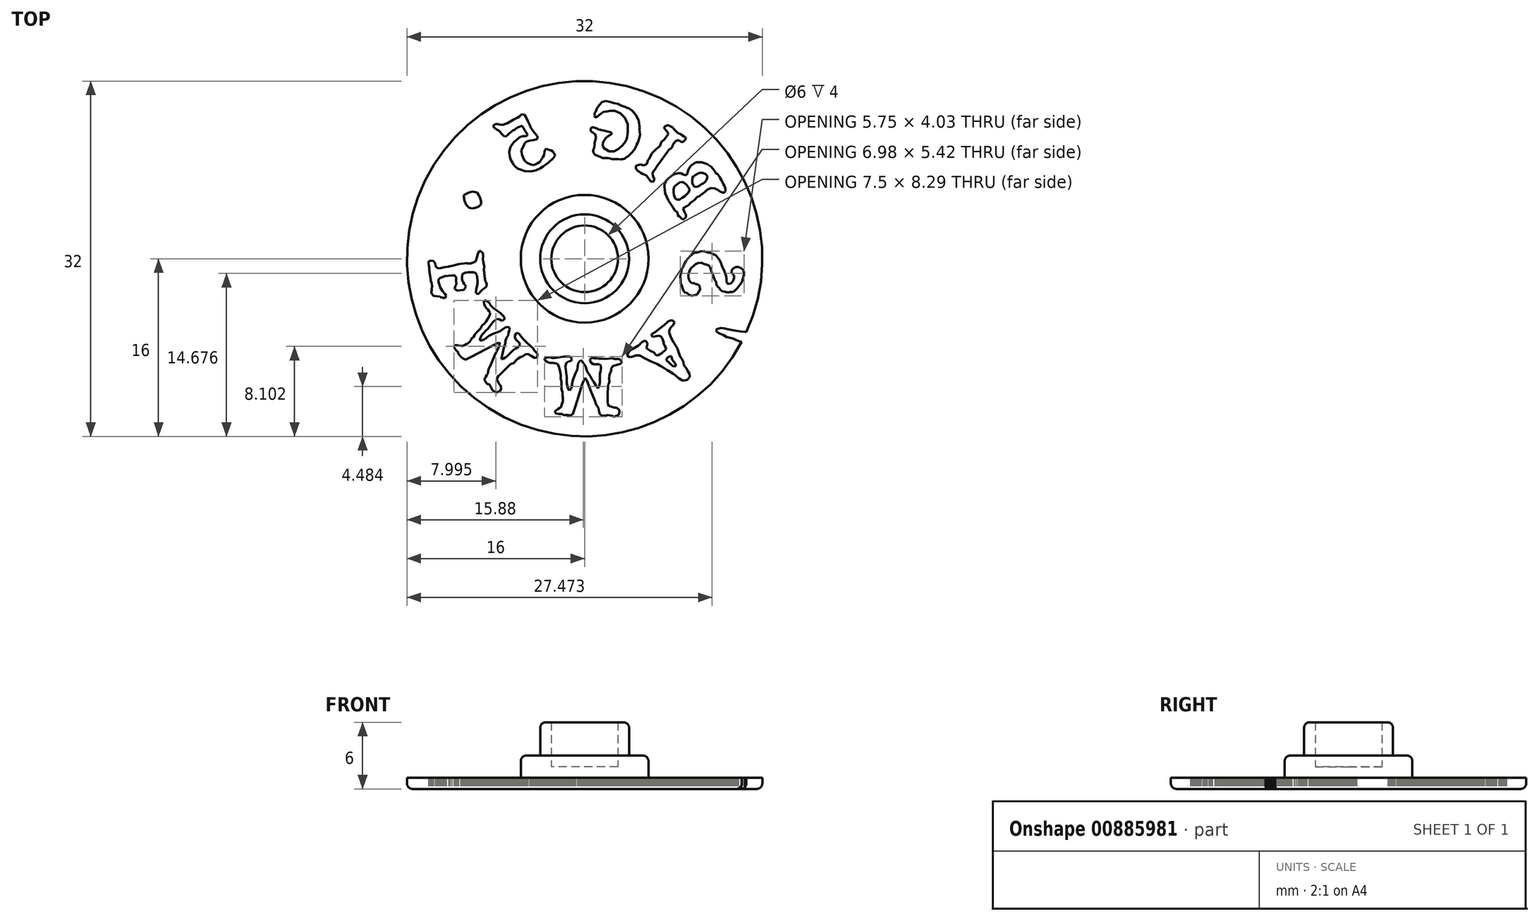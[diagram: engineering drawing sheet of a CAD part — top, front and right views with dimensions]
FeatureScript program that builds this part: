
annotation { "Feature Type Name" : "Feature", "Feature Type Description" : "" }
export const myFeature = defineFeature(function(context is Context, id is Id, definition is map)
    precondition{}
    {
        {
            var Q0;
            Q0=qCreatedBy(makeId("Top.planeOp"),FACE);
            var sketch = newSketch(context, id + "F0", { "sketchPlane" : qUnion([Q0])});
            skCircle(sketch, "E0", {"center": v(0, 0) * mm, "radius": 4 * mm});
            skCircle(sketch, "E1", {"center": v(0, 0) * mm, "radius": 5.75 * mm});
            skCircle(sketch, "E2", {"center": v(0, 0) * mm, "radius": 16 * mm});
            skCircle(sketch, "E3", {"center": v(0, 0) * mm, "radius": 3 * mm});
            skSolve(sketch);
        }
        {
            var Q0;
            Q0=makeQuery(id+"F0.imprint","IMPRINT",FACE,{"disambiguationData":[TD([[makeQuery(id+"F0.imprint","IMPRINT",EDGE,{"derivedFrom":sQuery(id+"F0.wireOp",EDGE,"E1")}),-1.0]])]});
            var Q1;
            Q1=makeQuery(id+"F0.imprint","IMPRINT",FACE,{"disambiguationData":[TD([[makeQuery(id+"F0.imprint","IMPRINT",EDGE,{"derivedFrom":sQuery(id+"F0.wireOp",EDGE,"E0")}),-1.0]])]});
            var Q2;
            Q2=makeQuery(id+"F0.imprint","IMPRINT",FACE,{"disambiguationData":[TD([[makeQuery(id+"F0.imprint","IMPRINT",EDGE,{"derivedFrom":sQuery(id+"F0.wireOp",EDGE,"E0")}),1.0]])]});
            var Q3;
            Q3=makeQuery(id+"F0.imprint","IMPRINT",FACE,{"disambiguationData":[TD([[makeQuery(id+"F0.imprint","IMPRINT",EDGE,{"derivedFrom":sQuery(id+"F0.wireOp",EDGE,"E3")}),1.0]])]});
            extrude(context, id + "F1", {"entities" : qUnion([Q0, Q1, Q2, Q3]), "depth" : 2 * mm, "offsetDistance" : 25 * mm});
        }
        {
            var Q0;
            Q0=makeQuery(id+"F0.imprint","IMPRINT",FACE,{"disambiguationData":[TD([[makeQuery(id+"F0.imprint","IMPRINT",EDGE,{"derivedFrom":sQuery(id+"F0.wireOp",EDGE,"E0")}),-1.0]])]});
            extrude(context, id + "F2", {"entities" : qUnion([Q0]), "operationType" : NewBodyOperationType.ADD, "depth" : 3 * mm, "offsetDistance" : 25 * mm});
        }
        {
            var Q0;
            Q0=makeQuery(id+"F0.imprint","IMPRINT",FACE,{"disambiguationData":[TD([[makeQuery(id+"F0.imprint","IMPRINT",EDGE,{"derivedFrom":sQuery(id+"F0.wireOp",EDGE,"E0")}),1.0]])]});
            extrude(context, id + "F3", {"entities" : qUnion([Q0]), "operationType" : NewBodyOperationType.ADD, "depth" : 6 * mm, "offsetDistance" : 25 * mm});
        }
        {
            var Q0;
            Q0=makeQuery(id+"F1.opExtrude","CAP_FACE",FACE,{"disambiguationData":[OSD([sQuery(id+"F0.wireOp",EDGE,"E2")])],"isStart":true});
            var sketch = newSketch(context, id + "F4", { "sketchPlane" : qUnion([Q0])});
            skLineSegment(sketch, "E4", {"start": v(0.68, -0.15) * mm, "end": v(0.68, -0.15) * mm});
            skLineSegment(sketch, "E5", {"start": v(0.68, -0.15) * mm, "end": v(0.68, -0.16) * mm});
            skLineSegment(sketch, "E6", {"start": v(0.68, -0.16) * mm, "end": v(0.68, -0.16) * mm});
            skLineSegment(sketch, "E7", {"start": v(0.68, -0.16) * mm, "end": v(0.67, -0.18) * mm});
            skLineSegment(sketch, "E8", {"start": v(0.67, -0.18) * mm, "end": v(0.68, -0.19) * mm});
            skLineSegment(sketch, "E9", {"start": v(0.68, -0.19) * mm, "end": v(0.68, -0.2) * mm});
            skLineSegment(sketch, "E10", {"start": v(0.68, -0.2) * mm, "end": v(0.68, -0.2) * mm});
            skLineSegment(sketch, "E11", {"start": v(0.68, -0.2) * mm, "end": v(0.67, -0.2) * mm});
            skLineSegment(sketch, "E12", {"start": v(0.67, -0.2) * mm, "end": v(0.67, -0.21) * mm});
            skLineSegment(sketch, "E13", {"start": v(0.67, -0.21) * mm, "end": v(0.66, -0.22) * mm});
            skLineSegment(sketch, "E14", {"start": v(0.66, -0.22) * mm, "end": v(0.65, -0.22) * mm});
            skLineSegment(sketch, "E15", {"start": v(0.65, -0.22) * mm, "end": v(0.64, -0.22) * mm});
            skLineSegment(sketch, "E16", {"start": v(0.64, -0.22) * mm, "end": v(0.63, -0.22) * mm});
            skLineSegment(sketch, "E17", {"start": v(0.63, -0.22) * mm, "end": v(0.63, -0.22) * mm});
            skLineSegment(sketch, "E18", {"start": v(0.63, -0.22) * mm, "end": v(0.62, -0.22) * mm});
            skLineSegment(sketch, "E19", {"start": v(0.62, -0.22) * mm, "end": v(0.61, -0.21) * mm});
            skLineSegment(sketch, "E20", {"start": v(0.61, -0.21) * mm, "end": v(0.62, -0.2) * mm});
            skLineSegment(sketch, "E21", {"start": v(0.62, -0.2) * mm, "end": v(0.63, -0.2) * mm});
            skLineSegment(sketch, "E22", {"start": v(0.63, -0.2) * mm, "end": v(0.64, -0.18) * mm});
            skLineSegment(sketch, "E23", {"start": v(0.64, -0.18) * mm, "end": v(0.65, -0.16) * mm});
            skLineSegment(sketch, "E24", {"start": v(0.65, -0.16) * mm, "end": v(0.65, -0.15) * mm});
            skLineSegment(sketch, "E25", {"start": v(0.65, -0.15) * mm, "end": v(0.64, -0.14) * mm});
            skLineSegment(sketch, "E26", {"start": v(0.64, -0.14) * mm, "end": v(0.64, -0.14) * mm});
            skLineSegment(sketch, "E27", {"start": v(0.64, -0.14) * mm, "end": v(0.63, -0.13) * mm});
            skLineSegment(sketch, "E28", {"start": v(0.63, -0.13) * mm, "end": v(0.63, -0.13) * mm});
            skLineSegment(sketch, "E29", {"start": v(0.63, -0.13) * mm, "end": v(0.62, -0.13) * mm});
            skLineSegment(sketch, "E30", {"start": v(0.62, -0.13) * mm, "end": v(0.6, -0.12) * mm});
            skLineSegment(sketch, "E31", {"start": v(0.6, -0.12) * mm, "end": v(0.58, -0.12) * mm});
            skLineSegment(sketch, "E32", {"start": v(0.58, -0.12) * mm, "end": v(0.57, -0.13) * mm});
            skLineSegment(sketch, "E33", {"start": v(0.57, -0.13) * mm, "end": v(0.57, -0.13) * mm});
            skLineSegment(sketch, "E34", {"start": v(0.57, -0.13) * mm, "end": v(0.57, -0.14) * mm});
            skLineSegment(sketch, "E35", {"start": v(0.57, -0.14) * mm, "end": v(0.57, -0.15) * mm});
            skLineSegment(sketch, "E36", {"start": v(0.57, -0.15) * mm, "end": v(0.57, -0.16) * mm});
            skLineSegment(sketch, "E37", {"start": v(0.57, -0.16) * mm, "end": v(0.57, -0.16) * mm});
            skLineSegment(sketch, "E38", {"start": v(0.57, -0.16) * mm, "end": v(0.57, -0.17) * mm});
            skLineSegment(sketch, "E39", {"start": v(0.57, -0.17) * mm, "end": v(0.58, -0.17) * mm});
            skLineSegment(sketch, "E40", {"start": v(0.58, -0.17) * mm, "end": v(0.58, -0.18) * mm});
            skLineSegment(sketch, "E41", {"start": v(0.58, -0.18) * mm, "end": v(0.58, -0.18) * mm});
            skLineSegment(sketch, "E42", {"start": v(0.58, -0.18) * mm, "end": v(0.57, -0.18) * mm});
            skLineSegment(sketch, "E43", {"start": v(0.57, -0.18) * mm, "end": v(0.56, -0.19) * mm});
            skLineSegment(sketch, "E44", {"start": v(0.56, -0.19) * mm, "end": v(0.54, -0.18) * mm});
            skLineSegment(sketch, "E45", {"start": v(0.54, -0.18) * mm, "end": v(0.53, -0.17) * mm});
            skLineSegment(sketch, "E46", {"start": v(0.53, -0.17) * mm, "end": v(0.53, -0.16) * mm});
            skLineSegment(sketch, "E47", {"start": v(0.53, -0.16) * mm, "end": v(0.54, -0.16) * mm});
            skLineSegment(sketch, "E48", {"start": v(0.54, -0.16) * mm, "end": v(0.54, -0.15) * mm});
            skLineSegment(sketch, "E49", {"start": v(0.54, -0.15) * mm, "end": v(0.55, -0.14) * mm});
            skLineSegment(sketch, "E50", {"start": v(0.55, -0.14) * mm, "end": v(0.55, -0.14) * mm});
            skLineSegment(sketch, "E51", {"start": v(0.55, -0.14) * mm, "end": v(0.55, -0.13) * mm});
            skLineSegment(sketch, "E52", {"start": v(0.55, -0.13) * mm, "end": v(0.55, -0.11) * mm});
            skLineSegment(sketch, "E53", {"start": v(0.55, -0.11) * mm, "end": v(0.54, -0.1) * mm});
            skLineSegment(sketch, "E54", {"start": v(0.54, -0.1) * mm, "end": v(0.53, -0.1) * mm});
            skLineSegment(sketch, "E55", {"start": v(0.53, -0.1) * mm, "end": v(0.51, -0.1) * mm});
            skLineSegment(sketch, "E56", {"start": v(0.51, -0.1) * mm, "end": v(0.5, -0.1) * mm});
            skLineSegment(sketch, "E57", {"start": v(0.5, -0.1) * mm, "end": v(0.5, -0.1) * mm});
            skLineSegment(sketch, "E58", {"start": v(0.5, -0.1) * mm, "end": v(0.49, -0.11) * mm});
            skLineSegment(sketch, "E59", {"start": v(0.49, -0.11) * mm, "end": v(0.48, -0.14) * mm});
            skLineSegment(sketch, "E60", {"start": v(0.48, -0.14) * mm, "end": v(0.48, -0.15) * mm});
            skLineSegment(sketch, "E61", {"start": v(0.48, -0.15) * mm, "end": v(0.48, -0.16) * mm});
            skLineSegment(sketch, "E62", {"start": v(0.48, -0.16) * mm, "end": v(0.49, -0.18) * mm});
            skLineSegment(sketch, "E63", {"start": v(0.49, -0.18) * mm, "end": v(0.48, -0.19) * mm});
            skLineSegment(sketch, "E64", {"start": v(0.48, -0.19) * mm, "end": v(0.48, -0.2) * mm});
            skLineSegment(sketch, "E65", {"start": v(0.48, -0.2) * mm, "end": v(0.48, -0.2) * mm});
            skLineSegment(sketch, "E66", {"start": v(0.48, -0.2) * mm, "end": v(0.47, -0.19) * mm});
            skLineSegment(sketch, "E67", {"start": v(0.47, -0.19) * mm, "end": v(0.47, -0.18) * mm});
            skLineSegment(sketch, "E68", {"start": v(0.47, -0.18) * mm, "end": v(0.46, -0.17) * mm});
            skLineSegment(sketch, "E69", {"start": v(0.46, -0.17) * mm, "end": v(0.45, -0.17) * mm});
            skLineSegment(sketch, "E70", {"start": v(0.45, -0.17) * mm, "end": v(0.44, -0.16) * mm});
            skLineSegment(sketch, "E71", {"start": v(0.44, -0.16) * mm, "end": v(0.44, -0.15) * mm});
            skLineSegment(sketch, "E72", {"start": v(0.44, -0.15) * mm, "end": v(0.44, -0.14) * mm});
            skLineSegment(sketch, "E73", {"start": v(0.44, -0.14) * mm, "end": v(0.45, -0.14) * mm});
            skLineSegment(sketch, "E74", {"start": v(0.45, -0.14) * mm, "end": v(0.45, -0.14) * mm});
            skLineSegment(sketch, "E75", {"start": v(0.45, -0.14) * mm, "end": v(0.45, -0.13) * mm});
            skLineSegment(sketch, "E76", {"start": v(0.45, -0.13) * mm, "end": v(0.46, -0.09) * mm});
            skLineSegment(sketch, "E77", {"start": v(0.46, -0.09) * mm, "end": v(0.46, -0.07) * mm});
            skLineSegment(sketch, "E78", {"start": v(0.46, -0.07) * mm, "end": v(0.46, -0.05) * mm});
            skLineSegment(sketch, "E79", {"start": v(0.46, -0.05) * mm, "end": v(0.47, -0.04) * mm});
            skLineSegment(sketch, "E80", {"start": v(0.47, -0.04) * mm, "end": v(0.47, -0.03) * mm});
            skLineSegment(sketch, "E81", {"start": v(0.47, -0.03) * mm, "end": v(0.47, -0.02) * mm});
            skLineSegment(sketch, "E82", {"start": v(0.47, -0.02) * mm, "end": v(0.47, -0.01) * mm});
            skLineSegment(sketch, "E83", {"start": v(0.47, -0.01) * mm, "end": v(0.48, -0.01) * mm});
            skLineSegment(sketch, "E84", {"start": v(0.48, -0.01) * mm, "end": v(0.48, 0) * mm});
            skLineSegment(sketch, "E85", {"start": v(0.48, 0) * mm, "end": v(0.49, 0) * mm});
            skLineSegment(sketch, "E86", {"start": v(0.49, 0) * mm, "end": v(0.5, -0.03) * mm});
            skLineSegment(sketch, "E87", {"start": v(0.5, -0.03) * mm, "end": v(0.5, -0.03) * mm});
            skLineSegment(sketch, "E88", {"start": v(0.5, -0.03) * mm, "end": v(0.5, -0.04) * mm});
            skLineSegment(sketch, "E89", {"start": v(0.5, -0.04) * mm, "end": v(0.5, -0.06) * mm});
            skLineSegment(sketch, "E90", {"start": v(0.5, -0.06) * mm, "end": v(0.51, -0.06) * mm});
            skLineSegment(sketch, "E91", {"start": v(0.51, -0.06) * mm, "end": v(0.52, -0.07) * mm});
            skLineSegment(sketch, "E92", {"start": v(0.52, -0.07) * mm, "end": v(0.52, -0.07) * mm});
            skLineSegment(sketch, "E93", {"start": v(0.52, -0.07) * mm, "end": v(0.53, -0.07) * mm});
            skLineSegment(sketch, "E94", {"start": v(0.53, -0.07) * mm, "end": v(0.53, -0.07) * mm});
            skLineSegment(sketch, "E95", {"start": v(0.53, -0.07) * mm, "end": v(0.54, -0.07) * mm});
            skLineSegment(sketch, "E96", {"start": v(0.54, -0.07) * mm, "end": v(0.55, -0.07) * mm});
            skLineSegment(sketch, "E97", {"start": v(0.55, -0.07) * mm, "end": v(0.56, -0.07) * mm});
            skLineSegment(sketch, "E98", {"start": v(0.56, -0.07) * mm, "end": v(0.57, -0.07) * mm});
            skLineSegment(sketch, "E99", {"start": v(0.57, -0.07) * mm, "end": v(0.6, -0.08) * mm});
            skLineSegment(sketch, "E100", {"start": v(0.6, -0.08) * mm, "end": v(0.6, -0.08) * mm});
            skLineSegment(sketch, "E101", {"start": v(0.6, -0.08) * mm, "end": v(0.6, -0.09) * mm});
            skLineSegment(sketch, "E102", {"start": v(0.6, -0.09) * mm, "end": v(0.61, -0.09) * mm});
            skLineSegment(sketch, "E103", {"start": v(0.61, -0.09) * mm, "end": v(0.63, -0.1) * mm});
            skLineSegment(sketch, "E104", {"start": v(0.63, -0.1) * mm, "end": v(0.64, -0.1) * mm});
            skLineSegment(sketch, "E105", {"start": v(0.64, -0.1) * mm, "end": v(0.66, -0.1) * mm});
            skLineSegment(sketch, "E106", {"start": v(0.66, -0.1) * mm, "end": v(0.66, -0.1) * mm});
            skLineSegment(sketch, "E107", {"start": v(0.66, -0.1) * mm, "end": v(0.67, -0.1) * mm});
            skLineSegment(sketch, "E108", {"start": v(0.67, -0.1) * mm, "end": v(0.67, -0.08) * mm});
            skLineSegment(sketch, "E109", {"start": v(0.67, -0.08) * mm, "end": v(0.68, -0.07) * mm});
            skLineSegment(sketch, "E110", {"start": v(0.68, -0.07) * mm, "end": v(0.7, -0.07) * mm});
            skLineSegment(sketch, "E111", {"start": v(0.7, -0.07) * mm, "end": v(0.7, -0.07) * mm});
            skLineSegment(sketch, "E112", {"start": v(0.7, -0.07) * mm, "end": v(0.7, -0.08) * mm});
            skLineSegment(sketch, "E113", {"start": v(0.7, -0.08) * mm, "end": v(0.7, -0.1) * mm});
            skLineSegment(sketch, "E114", {"start": v(0.7, -0.1) * mm, "end": v(0.7, -0.1) * mm});
            skLineSegment(sketch, "E115", {"start": v(0.7, -0.1) * mm, "end": v(0.7, -0.12) * mm});
            skLineSegment(sketch, "E116", {"start": v(0.7, -0.12) * mm, "end": v(0.68, -0.15) * mm});
            skLineSegment(sketch, "E117", {"start": v(0.38, -0.6) * mm, "end": v(0.36, -0.6) * mm});
            skLineSegment(sketch, "E118", {"start": v(0.36, -0.6) * mm, "end": v(0.34, -0.6) * mm});
            skLineSegment(sketch, "E119", {"start": v(0.34, -0.6) * mm, "end": v(0.34, -0.6) * mm});
            skLineSegment(sketch, "E120", {"start": v(0.34, -0.6) * mm, "end": v(0.34, -0.59) * mm});
            skLineSegment(sketch, "E121", {"start": v(0.34, -0.59) * mm, "end": v(0.34, -0.58) * mm});
            skLineSegment(sketch, "E122", {"start": v(0.34, -0.58) * mm, "end": v(0.34, -0.58) * mm});
            skLineSegment(sketch, "E123", {"start": v(0.34, -0.58) * mm, "end": v(0.35, -0.57) * mm});
            skLineSegment(sketch, "E124", {"start": v(0.35, -0.57) * mm, "end": v(0.35, -0.57) * mm});
            skLineSegment(sketch, "E125", {"start": v(0.35, -0.57) * mm, "end": v(0.36, -0.56) * mm});
            skLineSegment(sketch, "E126", {"start": v(0.36, -0.56) * mm, "end": v(0.36, -0.55) * mm});
            skLineSegment(sketch, "E127", {"start": v(0.36, -0.55) * mm, "end": v(0.36, -0.54) * mm});
            skLineSegment(sketch, "E128", {"start": v(0.36, -0.54) * mm, "end": v(0.36, -0.54) * mm});
            skLineSegment(sketch, "E129", {"start": v(0.36, -0.54) * mm, "end": v(0.35, -0.53) * mm});
            skLineSegment(sketch, "E130", {"start": v(0.35, -0.53) * mm, "end": v(0.33, -0.5) * mm});
            skLineSegment(sketch, "E131", {"start": v(0.33, -0.5) * mm, "end": v(0.31, -0.48) * mm});
            skLineSegment(sketch, "E132", {"start": v(0.31, -0.48) * mm, "end": v(0.3, -0.48) * mm});
            skLineSegment(sketch, "E133", {"start": v(0.3, -0.48) * mm, "end": v(0.3, -0.48) * mm});
            skLineSegment(sketch, "E134", {"start": v(0.3, -0.48) * mm, "end": v(0.3, -0.47) * mm});
            skLineSegment(sketch, "E135", {"start": v(0.3, -0.47) * mm, "end": v(0.29, -0.46) * mm});
            skLineSegment(sketch, "E136", {"start": v(0.29, -0.46) * mm, "end": v(0.28, -0.45) * mm});
            skLineSegment(sketch, "E137", {"start": v(0.28, -0.45) * mm, "end": v(0.27, -0.45) * mm});
            skLineSegment(sketch, "E138", {"start": v(0.27, -0.45) * mm, "end": v(0.26, -0.44) * mm});
            skLineSegment(sketch, "E139", {"start": v(0.26, -0.44) * mm, "end": v(0.25, -0.43) * mm});
            skLineSegment(sketch, "E140", {"start": v(0.25, -0.43) * mm, "end": v(0.24, -0.43) * mm});
            skLineSegment(sketch, "E141", {"start": v(0.24, -0.43) * mm, "end": v(0.22, -0.44) * mm});
            skLineSegment(sketch, "E142", {"start": v(0.22, -0.44) * mm, "end": v(0.21, -0.44) * mm});
            skLineSegment(sketch, "E143", {"start": v(0.21, -0.44) * mm, "end": v(0.2, -0.44) * mm});
            skLineSegment(sketch, "E144", {"start": v(0.2, -0.44) * mm, "end": v(0.2, -0.43) * mm});
            skLineSegment(sketch, "E145", {"start": v(0.2, -0.43) * mm, "end": v(0.21, -0.42) * mm});
            skLineSegment(sketch, "E146", {"start": v(0.21, -0.42) * mm, "end": v(0.22, -0.41) * mm});
            skLineSegment(sketch, "E147", {"start": v(0.22, -0.41) * mm, "end": v(0.22, -0.4) * mm});
            skLineSegment(sketch, "E148", {"start": v(0.22, -0.4) * mm, "end": v(0.25, -0.38) * mm});
            skLineSegment(sketch, "E149", {"start": v(0.25, -0.38) * mm, "end": v(0.26, -0.38) * mm});
            skLineSegment(sketch, "E150", {"start": v(0.26, -0.38) * mm, "end": v(0.26, -0.37) * mm});
            skLineSegment(sketch, "E151", {"start": v(0.26, -0.37) * mm, "end": v(0.27, -0.37) * mm});
            skLineSegment(sketch, "E152", {"start": v(0.27, -0.37) * mm, "end": v(0.27, -0.36) * mm});
            skLineSegment(sketch, "E153", {"start": v(0.27, -0.36) * mm, "end": v(0.28, -0.35) * mm});
            skLineSegment(sketch, "E154", {"start": v(0.28, -0.35) * mm, "end": v(0.28, -0.35) * mm});
            skLineSegment(sketch, "E155", {"start": v(0.28, -0.35) * mm, "end": v(0.3, -0.34) * mm});
            skLineSegment(sketch, "E156", {"start": v(0.3, -0.34) * mm, "end": v(0.3, -0.35) * mm});
            skLineSegment(sketch, "E157", {"start": v(0.3, -0.35) * mm, "end": v(0.3, -0.36) * mm});
            skLineSegment(sketch, "E158", {"start": v(0.3, -0.36) * mm, "end": v(0.3, -0.37) * mm});
            skLineSegment(sketch, "E159", {"start": v(0.3, -0.37) * mm, "end": v(0.3, -0.38) * mm});
            skLineSegment(sketch, "E160", {"start": v(0.3, -0.38) * mm, "end": v(0.28, -0.39) * mm});
            skLineSegment(sketch, "E161", {"start": v(0.28, -0.39) * mm, "end": v(0.28, -0.4) * mm});
            skLineSegment(sketch, "E162", {"start": v(0.28, -0.4) * mm, "end": v(0.28, -0.4) * mm});
            skLineSegment(sketch, "E163", {"start": v(0.28, -0.4) * mm, "end": v(0.3, -0.41) * mm});
            skLineSegment(sketch, "E164", {"start": v(0.3, -0.41) * mm, "end": v(0.3, -0.42) * mm});
            skLineSegment(sketch, "E165", {"start": v(0.3, -0.42) * mm, "end": v(0.31, -0.43) * mm});
            skLineSegment(sketch, "E166", {"start": v(0.31, -0.43) * mm, "end": v(0.32, -0.44) * mm});
            skLineSegment(sketch, "E167", {"start": v(0.32, -0.44) * mm, "end": v(0.33, -0.45) * mm});
            skLineSegment(sketch, "E168", {"start": v(0.33, -0.45) * mm, "end": v(0.33, -0.45) * mm});
            skLineSegment(sketch, "E169", {"start": v(0.33, -0.45) * mm, "end": v(0.34, -0.46) * mm});
            skLineSegment(sketch, "E170", {"start": v(0.34, -0.46) * mm, "end": v(0.35, -0.46) * mm});
            skLineSegment(sketch, "E171", {"start": v(0.35, -0.46) * mm, "end": v(0.35, -0.46) * mm});
            skLineSegment(sketch, "E172", {"start": v(0.35, -0.46) * mm, "end": v(0.35, -0.45) * mm});
            skLineSegment(sketch, "E173", {"start": v(0.35, -0.45) * mm, "end": v(0.35, -0.43) * mm});
            skLineSegment(sketch, "E174", {"start": v(0.35, -0.43) * mm, "end": v(0.35, -0.42) * mm});
            skLineSegment(sketch, "E175", {"start": v(0.35, -0.42) * mm, "end": v(0.34, -0.4) * mm});
            skLineSegment(sketch, "E176", {"start": v(0.34, -0.4) * mm, "end": v(0.34, -0.4) * mm});
            skLineSegment(sketch, "E177", {"start": v(0.34, -0.4) * mm, "end": v(0.34, -0.38) * mm});
            skLineSegment(sketch, "E178", {"start": v(0.34, -0.38) * mm, "end": v(0.34, -0.37) * mm});
            skLineSegment(sketch, "E179", {"start": v(0.34, -0.37) * mm, "end": v(0.33, -0.37) * mm});
            skLineSegment(sketch, "E180", {"start": v(0.33, -0.37) * mm, "end": v(0.33, -0.36) * mm});
            skLineSegment(sketch, "E181", {"start": v(0.33, -0.36) * mm, "end": v(0.33, -0.35) * mm});
            skLineSegment(sketch, "E182", {"start": v(0.33, -0.35) * mm, "end": v(0.33, -0.34) * mm});
            skLineSegment(sketch, "E183", {"start": v(0.33, -0.34) * mm, "end": v(0.33, -0.33) * mm});
            skLineSegment(sketch, "E184", {"start": v(0.33, -0.33) * mm, "end": v(0.33, -0.33) * mm});
            skLineSegment(sketch, "E185", {"start": v(0.33, -0.33) * mm, "end": v(0.34, -0.32) * mm});
            skLineSegment(sketch, "E186", {"start": v(0.34, -0.32) * mm, "end": v(0.35, -0.33) * mm});
            skLineSegment(sketch, "E187", {"start": v(0.35, -0.33) * mm, "end": v(0.37, -0.34) * mm});
            skLineSegment(sketch, "E188", {"start": v(0.37, -0.34) * mm, "end": v(0.38, -0.35) * mm});
            skLineSegment(sketch, "E189", {"start": v(0.38, -0.35) * mm, "end": v(0.4, -0.36) * mm});
            skLineSegment(sketch, "E190", {"start": v(0.4, -0.36) * mm, "end": v(0.41, -0.37) * mm});
            skLineSegment(sketch, "E191", {"start": v(0.41, -0.37) * mm, "end": v(0.42, -0.38) * mm});
            skLineSegment(sketch, "E192", {"start": v(0.42, -0.38) * mm, "end": v(0.43, -0.38) * mm});
            skLineSegment(sketch, "E193", {"start": v(0.43, -0.38) * mm, "end": v(0.43, -0.38) * mm});
            skLineSegment(sketch, "E194", {"start": v(0.43, -0.38) * mm, "end": v(0.44, -0.39) * mm});
            skLineSegment(sketch, "E195", {"start": v(0.44, -0.39) * mm, "end": v(0.45, -0.4) * mm});
            skLineSegment(sketch, "E196", {"start": v(0.45, -0.4) * mm, "end": v(0.45, -0.4) * mm});
            skLineSegment(sketch, "E197", {"start": v(0.45, -0.4) * mm, "end": v(0.45, -0.39) * mm});
            skLineSegment(sketch, "E198", {"start": v(0.45, -0.39) * mm, "end": v(0.45, -0.38) * mm});
            skLineSegment(sketch, "E199", {"start": v(0.45, -0.38) * mm, "end": v(0.44, -0.37) * mm});
            skLineSegment(sketch, "E200", {"start": v(0.44, -0.37) * mm, "end": v(0.44, -0.36) * mm});
            skLineSegment(sketch, "E201", {"start": v(0.44, -0.36) * mm, "end": v(0.43, -0.34) * mm});
            skLineSegment(sketch, "E202", {"start": v(0.43, -0.34) * mm, "end": v(0.42, -0.34) * mm});
            skLineSegment(sketch, "E203", {"start": v(0.42, -0.34) * mm, "end": v(0.4, -0.32) * mm});
            skLineSegment(sketch, "E204", {"start": v(0.4, -0.32) * mm, "end": v(0.4, -0.3) * mm});
            skLineSegment(sketch, "E205", {"start": v(0.4, -0.3) * mm, "end": v(0.4, -0.3) * mm});
            skLineSegment(sketch, "E206", {"start": v(0.4, -0.3) * mm, "end": v(0.38, -0.3) * mm});
            skLineSegment(sketch, "E207", {"start": v(0.38, -0.3) * mm, "end": v(0.37, -0.3) * mm});
            skLineSegment(sketch, "E208", {"start": v(0.37, -0.3) * mm, "end": v(0.36, -0.3) * mm});
            skLineSegment(sketch, "E209", {"start": v(0.36, -0.3) * mm, "end": v(0.36, -0.3) * mm});
            skLineSegment(sketch, "E210", {"start": v(0.36, -0.3) * mm, "end": v(0.35, -0.29) * mm});
            skLineSegment(sketch, "E211", {"start": v(0.35, -0.29) * mm, "end": v(0.35, -0.28) * mm});
            skLineSegment(sketch, "E212", {"start": v(0.35, -0.28) * mm, "end": v(0.36, -0.28) * mm});
            skLineSegment(sketch, "E213", {"start": v(0.36, -0.28) * mm, "end": v(0.36, -0.28) * mm});
            skLineSegment(sketch, "E214", {"start": v(0.36, -0.28) * mm, "end": v(0.37, -0.27) * mm});
            skLineSegment(sketch, "E215", {"start": v(0.37, -0.27) * mm, "end": v(0.4, -0.25) * mm});
            skLineSegment(sketch, "E216", {"start": v(0.4, -0.25) * mm, "end": v(0.41, -0.24) * mm});
            skLineSegment(sketch, "E217", {"start": v(0.41, -0.24) * mm, "end": v(0.42, -0.24) * mm});
            skLineSegment(sketch, "E218", {"start": v(0.42, -0.24) * mm, "end": v(0.42, -0.23) * mm});
            skLineSegment(sketch, "E219", {"start": v(0.42, -0.23) * mm, "end": v(0.42, -0.23) * mm});
            skLineSegment(sketch, "E220", {"start": v(0.42, -0.23) * mm, "end": v(0.43, -0.22) * mm});
            skLineSegment(sketch, "E221", {"start": v(0.43, -0.22) * mm, "end": v(0.43, -0.22) * mm});
            skLineSegment(sketch, "E222", {"start": v(0.43, -0.22) * mm, "end": v(0.44, -0.22) * mm});
            skLineSegment(sketch, "E223", {"start": v(0.44, -0.22) * mm, "end": v(0.44, -0.22) * mm});
            skLineSegment(sketch, "E224", {"start": v(0.44, -0.22) * mm, "end": v(0.45, -0.22) * mm});
            skLineSegment(sketch, "E225", {"start": v(0.45, -0.22) * mm, "end": v(0.45, -0.23) * mm});
            skLineSegment(sketch, "E226", {"start": v(0.45, -0.23) * mm, "end": v(0.45, -0.24) * mm});
            skLineSegment(sketch, "E227", {"start": v(0.45, -0.24) * mm, "end": v(0.44, -0.24) * mm});
            skLineSegment(sketch, "E228", {"start": v(0.44, -0.24) * mm, "end": v(0.44, -0.25) * mm});
            skLineSegment(sketch, "E229", {"start": v(0.44, -0.25) * mm, "end": v(0.43, -0.25) * mm});
            skLineSegment(sketch, "E230", {"start": v(0.43, -0.25) * mm, "end": v(0.43, -0.26) * mm});
            skLineSegment(sketch, "E231", {"start": v(0.43, -0.26) * mm, "end": v(0.42, -0.26) * mm});
            skLineSegment(sketch, "E232", {"start": v(0.42, -0.26) * mm, "end": v(0.42, -0.27) * mm});
            skLineSegment(sketch, "E233", {"start": v(0.42, -0.27) * mm, "end": v(0.42, -0.28) * mm});
            skLineSegment(sketch, "E234", {"start": v(0.42, -0.28) * mm, "end": v(0.43, -0.3) * mm});
            skLineSegment(sketch, "E235", {"start": v(0.43, -0.3) * mm, "end": v(0.43, -0.3) * mm});
            skLineSegment(sketch, "E236", {"start": v(0.43, -0.3) * mm, "end": v(0.44, -0.32) * mm});
            skLineSegment(sketch, "E237", {"start": v(0.44, -0.32) * mm, "end": v(0.45, -0.33) * mm});
            skLineSegment(sketch, "E238", {"start": v(0.45, -0.33) * mm, "end": v(0.45, -0.33) * mm});
            skLineSegment(sketch, "E239", {"start": v(0.45, -0.33) * mm, "end": v(0.45, -0.34) * mm});
            skLineSegment(sketch, "E240", {"start": v(0.45, -0.34) * mm, "end": v(0.45, -0.34) * mm});
            skLineSegment(sketch, "E241", {"start": v(0.45, -0.34) * mm, "end": v(0.46, -0.35) * mm});
            skLineSegment(sketch, "E242", {"start": v(0.46, -0.35) * mm, "end": v(0.47, -0.36) * mm});
            skLineSegment(sketch, "E243", {"start": v(0.47, -0.36) * mm, "end": v(0.47, -0.36) * mm});
            skLineSegment(sketch, "E244", {"start": v(0.47, -0.36) * mm, "end": v(0.47, -0.37) * mm});
            skLineSegment(sketch, "E245", {"start": v(0.47, -0.37) * mm, "end": v(0.48, -0.38) * mm});
            skLineSegment(sketch, "E246", {"start": v(0.48, -0.38) * mm, "end": v(0.49, -0.39) * mm});
            skLineSegment(sketch, "E247", {"start": v(0.49, -0.39) * mm, "end": v(0.49, -0.4) * mm});
            skLineSegment(sketch, "E248", {"start": v(0.49, -0.4) * mm, "end": v(0.49, -0.4) * mm});
            skLineSegment(sketch, "E249", {"start": v(0.49, -0.4) * mm, "end": v(0.5, -0.4) * mm});
            skLineSegment(sketch, "E250", {"start": v(0.5, -0.4) * mm, "end": v(0.5, -0.4) * mm});
            skLineSegment(sketch, "E251", {"start": v(0.5, -0.4) * mm, "end": v(0.51, -0.41) * mm});
            skLineSegment(sketch, "E252", {"start": v(0.51, -0.41) * mm, "end": v(0.52, -0.42) * mm});
            skLineSegment(sketch, "E253", {"start": v(0.52, -0.42) * mm, "end": v(0.53, -0.42) * mm});
            skLineSegment(sketch, "E254", {"start": v(0.53, -0.42) * mm, "end": v(0.54, -0.42) * mm});
            skLineSegment(sketch, "E255", {"start": v(0.54, -0.42) * mm, "end": v(0.55, -0.42) * mm});
            skLineSegment(sketch, "E256", {"start": v(0.55, -0.42) * mm, "end": v(0.55, -0.42) * mm});
            skLineSegment(sketch, "E257", {"start": v(0.55, -0.42) * mm, "end": v(0.56, -0.42) * mm});
            skLineSegment(sketch, "E258", {"start": v(0.56, -0.42) * mm, "end": v(0.56, -0.43) * mm});
            skLineSegment(sketch, "E259", {"start": v(0.56, -0.43) * mm, "end": v(0.56, -0.43) * mm});
            skLineSegment(sketch, "E260", {"start": v(0.56, -0.43) * mm, "end": v(0.55, -0.44) * mm});
            skLineSegment(sketch, "E261", {"start": v(0.55, -0.44) * mm, "end": v(0.54, -0.45) * mm});
            skLineSegment(sketch, "E262", {"start": v(0.54, -0.45) * mm, "end": v(0.54, -0.45) * mm});
            skLineSegment(sketch, "E263", {"start": v(0.54, -0.45) * mm, "end": v(0.54, -0.46) * mm});
            skLineSegment(sketch, "E264", {"start": v(0.54, -0.46) * mm, "end": v(0.52, -0.47) * mm});
            skLineSegment(sketch, "E265", {"start": v(0.52, -0.47) * mm, "end": v(0.52, -0.47) * mm});
            skLineSegment(sketch, "E266", {"start": v(0.52, -0.47) * mm, "end": v(0.5, -0.48) * mm});
            skLineSegment(sketch, "E267", {"start": v(0.5, -0.48) * mm, "end": v(0.48, -0.46) * mm});
            skLineSegment(sketch, "E268", {"start": v(0.48, -0.46) * mm, "end": v(0.45, -0.45) * mm});
            skLineSegment(sketch, "E269", {"start": v(0.45, -0.45) * mm, "end": v(0.42, -0.43) * mm});
            skLineSegment(sketch, "E270", {"start": v(0.42, -0.43) * mm, "end": v(0.4, -0.4) * mm});
            skLineSegment(sketch, "E271", {"start": v(0.4, -0.4) * mm, "end": v(0.37, -0.4) * mm});
            skLineSegment(sketch, "E272", {"start": v(0.37, -0.4) * mm, "end": v(0.36, -0.4) * mm});
            skLineSegment(sketch, "E273", {"start": v(0.36, -0.4) * mm, "end": v(0.36, -0.4) * mm});
            skLineSegment(sketch, "E274", {"start": v(0.36, -0.4) * mm, "end": v(0.37, -0.4) * mm});
            skLineSegment(sketch, "E275", {"start": v(0.37, -0.4) * mm, "end": v(0.37, -0.4) * mm});
            skLineSegment(sketch, "E276", {"start": v(0.37, -0.4) * mm, "end": v(0.38, -0.45) * mm});
            skLineSegment(sketch, "E277", {"start": v(0.38, -0.45) * mm, "end": v(0.4, -0.5) * mm});
            skLineSegment(sketch, "E278", {"start": v(0.4, -0.5) * mm, "end": v(0.4, -0.51) * mm});
            skLineSegment(sketch, "E279", {"start": v(0.4, -0.51) * mm, "end": v(0.4, -0.53) * mm});
            skLineSegment(sketch, "E280", {"start": v(0.4, -0.53) * mm, "end": v(0.4, -0.54) * mm});
            skLineSegment(sketch, "E281", {"start": v(0.4, -0.54) * mm, "end": v(0.41, -0.54) * mm});
            skLineSegment(sketch, "E282", {"start": v(0.41, -0.54) * mm, "end": v(0.42, -0.55) * mm});
            skLineSegment(sketch, "E283", {"start": v(0.42, -0.55) * mm, "end": v(0.41, -0.56) * mm});
            skLineSegment(sketch, "E284", {"start": v(0.41, -0.56) * mm, "end": v(0.4, -0.57) * mm});
            skLineSegment(sketch, "E285", {"start": v(0.4, -0.57) * mm, "end": v(0.4, -0.58) * mm});
            skLineSegment(sketch, "E286", {"start": v(0.4, -0.58) * mm, "end": v(0.39, -0.58) * mm});
            skLineSegment(sketch, "E287", {"start": v(0.39, -0.58) * mm, "end": v(0.38, -0.6) * mm});
            skLineSegment(sketch, "E288", {"start": v(0.38, -0.6) * mm, "end": v(0.38, -0.6) * mm});
            skLineSegment(sketch, "E289", {"start": v(-0.15, -0.67) * mm, "end": v(-0.17, -0.66) * mm});
            skLineSegment(sketch, "E290", {"start": v(-0.17, -0.66) * mm, "end": v(-0.17, -0.64) * mm});
            skLineSegment(sketch, "E291", {"start": v(-0.17, -0.64) * mm, "end": v(-0.17, -0.64) * mm});
            skLineSegment(sketch, "E292", {"start": v(-0.17, -0.64) * mm, "end": v(-0.17, -0.63) * mm});
            skLineSegment(sketch, "E293", {"start": v(-0.17, -0.63) * mm, "end": v(-0.16, -0.63) * mm});
            skLineSegment(sketch, "E294", {"start": v(-0.16, -0.63) * mm, "end": v(-0.16, -0.63) * mm});
            skLineSegment(sketch, "E295", {"start": v(-0.16, -0.63) * mm, "end": v(-0.15, -0.63) * mm});
            skLineSegment(sketch, "E296", {"start": v(-0.15, -0.63) * mm, "end": v(-0.14, -0.63) * mm});
            skLineSegment(sketch, "E297", {"start": v(-0.14, -0.63) * mm, "end": v(-0.14, -0.63) * mm});
            skLineSegment(sketch, "E298", {"start": v(-0.14, -0.63) * mm, "end": v(-0.13, -0.62) * mm});
            skLineSegment(sketch, "E299", {"start": v(-0.13, -0.62) * mm, "end": v(-0.12, -0.62) * mm});
            skLineSegment(sketch, "E300", {"start": v(-0.12, -0.62) * mm, "end": v(-0.12, -0.6) * mm});
            skLineSegment(sketch, "E301", {"start": v(-0.12, -0.6) * mm, "end": v(-0.12, -0.6) * mm});
            skLineSegment(sketch, "E302", {"start": v(-0.12, -0.6) * mm, "end": v(-0.12, -0.57) * mm});
            skLineSegment(sketch, "E303", {"start": v(-0.12, -0.57) * mm, "end": v(-0.11, -0.54) * mm});
            skLineSegment(sketch, "E304", {"start": v(-0.11, -0.54) * mm, "end": v(-0.11, -0.53) * mm});
            skLineSegment(sketch, "E305", {"start": v(-0.11, -0.53) * mm, "end": v(-0.12, -0.53) * mm});
            skLineSegment(sketch, "E306", {"start": v(-0.12, -0.53) * mm, "end": v(-0.12, -0.52) * mm});
            skLineSegment(sketch, "E307", {"start": v(-0.12, -0.52) * mm, "end": v(-0.12, -0.52) * mm});
            skLineSegment(sketch, "E308", {"start": v(-0.12, -0.52) * mm, "end": v(-0.12, -0.5) * mm});
            skLineSegment(sketch, "E309", {"start": v(-0.12, -0.5) * mm, "end": v(-0.12, -0.5) * mm});
            skLineSegment(sketch, "E310", {"start": v(-0.12, -0.5) * mm, "end": v(-0.12, -0.48) * mm});
            skLineSegment(sketch, "E311", {"start": v(-0.12, -0.48) * mm, "end": v(-0.12, -0.47) * mm});
            skLineSegment(sketch, "E312", {"start": v(-0.12, -0.47) * mm, "end": v(-0.12, -0.46) * mm});
            skLineSegment(sketch, "E313", {"start": v(-0.12, -0.46) * mm, "end": v(-0.13, -0.45) * mm});
            skLineSegment(sketch, "E314", {"start": v(-0.13, -0.45) * mm, "end": v(-0.14, -0.44) * mm});
            skLineSegment(sketch, "E315", {"start": v(-0.14, -0.44) * mm, "end": v(-0.16, -0.44) * mm});
            skLineSegment(sketch, "E316", {"start": v(-0.16, -0.44) * mm, "end": v(-0.17, -0.43) * mm});
            skLineSegment(sketch, "E317", {"start": v(-0.17, -0.43) * mm, "end": v(-0.15, -0.42) * mm});
            skLineSegment(sketch, "E318", {"start": v(-0.15, -0.42) * mm, "end": v(-0.14, -0.42) * mm});
            skLineSegment(sketch, "E319", {"start": v(-0.14, -0.42) * mm, "end": v(-0.13, -0.42) * mm});
            skLineSegment(sketch, "E320", {"start": v(-0.13, -0.42) * mm, "end": v(-0.12, -0.42) * mm});
            skLineSegment(sketch, "E321", {"start": v(-0.12, -0.42) * mm, "end": v(-0.1, -0.42) * mm});
            skLineSegment(sketch, "E322", {"start": v(-0.1, -0.42) * mm, "end": v(-0.08, -0.42) * mm});
            skLineSegment(sketch, "E323", {"start": v(-0.08, -0.42) * mm, "end": v(-0.07, -0.42) * mm});
            skLineSegment(sketch, "E324", {"start": v(-0.07, -0.42) * mm, "end": v(-0.06, -0.42) * mm});
            skLineSegment(sketch, "E325", {"start": v(-0.06, -0.42) * mm, "end": v(-0.06, -0.42) * mm});
            skLineSegment(sketch, "E326", {"start": v(-0.06, -0.42) * mm, "end": v(-0.05, -0.42) * mm});
            skLineSegment(sketch, "E327", {"start": v(-0.05, -0.42) * mm, "end": v(-0.04, -0.42) * mm});
            skLineSegment(sketch, "E328", {"start": v(-0.04, -0.42) * mm, "end": v(-0.03, -0.43) * mm});
            skLineSegment(sketch, "E329", {"start": v(-0.03, -0.43) * mm, "end": v(-0.03, -0.43) * mm});
            skLineSegment(sketch, "E330", {"start": v(-0.03, -0.43) * mm, "end": v(-0.03, -0.44) * mm});
            skLineSegment(sketch, "E331", {"start": v(-0.03, -0.44) * mm, "end": v(-0.04, -0.45) * mm});
            skLineSegment(sketch, "E332", {"start": v(-0.04, -0.45) * mm, "end": v(-0.05, -0.45) * mm});
            skLineSegment(sketch, "E333", {"start": v(-0.05, -0.45) * mm, "end": v(-0.07, -0.45) * mm});
            skLineSegment(sketch, "E334", {"start": v(-0.07, -0.45) * mm, "end": v(-0.07, -0.45) * mm});
            skLineSegment(sketch, "E335", {"start": v(-0.07, -0.45) * mm, "end": v(-0.08, -0.45) * mm});
            skLineSegment(sketch, "E336", {"start": v(-0.08, -0.45) * mm, "end": v(-0.08, -0.46) * mm});
            skLineSegment(sketch, "E337", {"start": v(-0.08, -0.46) * mm, "end": v(-0.08, -0.46) * mm});
            skLineSegment(sketch, "E338", {"start": v(-0.08, -0.46) * mm, "end": v(-0.08, -0.48) * mm});
            skLineSegment(sketch, "E339", {"start": v(-0.08, -0.48) * mm, "end": v(-0.08, -0.49) * mm});
            skLineSegment(sketch, "E340", {"start": v(-0.08, -0.49) * mm, "end": v(-0.08, -0.5) * mm});
            skLineSegment(sketch, "E341", {"start": v(-0.08, -0.5) * mm, "end": v(-0.08, -0.52) * mm});
            skLineSegment(sketch, "E342", {"start": v(-0.08, -0.52) * mm, "end": v(-0.08, -0.53) * mm});
            skLineSegment(sketch, "E343", {"start": v(-0.08, -0.53) * mm, "end": v(-0.08, -0.53) * mm});
            skLineSegment(sketch, "E344", {"start": v(-0.08, -0.53) * mm, "end": v(-0.08, -0.54) * mm});
            skLineSegment(sketch, "E345", {"start": v(-0.08, -0.54) * mm, "end": v(-0.07, -0.55) * mm});
            skLineSegment(sketch, "E346", {"start": v(-0.07, -0.55) * mm, "end": v(-0.07, -0.55) * mm});
            skLineSegment(sketch, "E347", {"start": v(-0.07, -0.55) * mm, "end": v(-0.06, -0.54) * mm});
            skLineSegment(sketch, "E348", {"start": v(-0.06, -0.54) * mm, "end": v(-0.05, -0.53) * mm});
            skLineSegment(sketch, "E349", {"start": v(-0.05, -0.53) * mm, "end": v(-0.04, -0.51) * mm});
            skLineSegment(sketch, "E350", {"start": v(-0.04, -0.51) * mm, "end": v(-0.03, -0.5) * mm});
            skLineSegment(sketch, "E351", {"start": v(-0.03, -0.5) * mm, "end": v(-0.03, -0.5) * mm});
            skLineSegment(sketch, "E352", {"start": v(-0.03, -0.5) * mm, "end": v(-0.02, -0.49) * mm});
            skLineSegment(sketch, "E353", {"start": v(-0.02, -0.49) * mm, "end": v(-0.02, -0.48) * mm});
            skLineSegment(sketch, "E354", {"start": v(-0.02, -0.48) * mm, "end": v(-0.01, -0.47) * mm});
            skLineSegment(sketch, "E355", {"start": v(-0.01, -0.47) * mm, "end": v(-0.01, -0.46) * mm});
            skLineSegment(sketch, "E356", {"start": v(-0.01, -0.46) * mm, "end": v(0, -0.45) * mm});
            skLineSegment(sketch, "E357", {"start": v(0, -0.45) * mm, "end": v(0, -0.45) * mm});
            skLineSegment(sketch, "E358", {"start": v(0, -0.45) * mm, "end": v(0, -0.44) * mm});
            skLineSegment(sketch, "E359", {"start": v(0, -0.44) * mm, "end": v(0.01, -0.44) * mm});
            skLineSegment(sketch, "E360", {"start": v(0.01, -0.44) * mm, "end": v(0.02, -0.44) * mm});
            skLineSegment(sketch, "E361", {"start": v(0.02, -0.44) * mm, "end": v(0.02, -0.45) * mm});
            skLineSegment(sketch, "E362", {"start": v(0.02, -0.45) * mm, "end": v(0.02, -0.48) * mm});
            skLineSegment(sketch, "E363", {"start": v(0.02, -0.48) * mm, "end": v(0.03, -0.5) * mm});
            skLineSegment(sketch, "E364", {"start": v(0.03, -0.5) * mm, "end": v(0.03, -0.51) * mm});
            skLineSegment(sketch, "E365", {"start": v(0.03, -0.51) * mm, "end": v(0.04, -0.53) * mm});
            skLineSegment(sketch, "E366", {"start": v(0.04, -0.53) * mm, "end": v(0.04, -0.54) * mm});
            skLineSegment(sketch, "E367", {"start": v(0.04, -0.54) * mm, "end": v(0.04, -0.55) * mm});
            skLineSegment(sketch, "E368", {"start": v(0.04, -0.55) * mm, "end": v(0.04, -0.55) * mm});
            skLineSegment(sketch, "E369", {"start": v(0.04, -0.55) * mm, "end": v(0.04, -0.56) * mm});
            skLineSegment(sketch, "E370", {"start": v(0.04, -0.56) * mm, "end": v(0.05, -0.57) * mm});
            skLineSegment(sketch, "E371", {"start": v(0.05, -0.57) * mm, "end": v(0.05, -0.57) * mm});
            skLineSegment(sketch, "E372", {"start": v(0.05, -0.57) * mm, "end": v(0.06, -0.56) * mm});
            skLineSegment(sketch, "E373", {"start": v(0.06, -0.56) * mm, "end": v(0.06, -0.55) * mm});
            skLineSegment(sketch, "E374", {"start": v(0.06, -0.55) * mm, "end": v(0.06, -0.54) * mm});
            skLineSegment(sketch, "E375", {"start": v(0.06, -0.54) * mm, "end": v(0.06, -0.52) * mm});
            skLineSegment(sketch, "E376", {"start": v(0.06, -0.52) * mm, "end": v(0.06, -0.51) * mm});
            skLineSegment(sketch, "E377", {"start": v(0.06, -0.51) * mm, "end": v(0.07, -0.5) * mm});
            skLineSegment(sketch, "E378", {"start": v(0.07, -0.5) * mm, "end": v(0.07, -0.48) * mm});
            skLineSegment(sketch, "E379", {"start": v(0.07, -0.48) * mm, "end": v(0.07, -0.47) * mm});
            skLineSegment(sketch, "E380", {"start": v(0.07, -0.47) * mm, "end": v(0.07, -0.45) * mm});
            skLineSegment(sketch, "E381", {"start": v(0.07, -0.45) * mm, "end": v(0.06, -0.45) * mm});
            skLineSegment(sketch, "E382", {"start": v(0.06, -0.45) * mm, "end": v(0.05, -0.45) * mm});
            skLineSegment(sketch, "E383", {"start": v(0.05, -0.45) * mm, "end": v(0.05, -0.44) * mm});
            skLineSegment(sketch, "E384", {"start": v(0.05, -0.44) * mm, "end": v(0.05, -0.43) * mm});
            skLineSegment(sketch, "E385", {"start": v(0.05, -0.43) * mm, "end": v(0.06, -0.43) * mm});
            skLineSegment(sketch, "E386", {"start": v(0.06, -0.43) * mm, "end": v(0.06, -0.43) * mm});
            skLineSegment(sketch, "E387", {"start": v(0.06, -0.43) * mm, "end": v(0.07, -0.43) * mm});
            skLineSegment(sketch, "E388", {"start": v(0.07, -0.43) * mm, "end": v(0.08, -0.43) * mm});
            skLineSegment(sketch, "E389", {"start": v(0.08, -0.43) * mm, "end": v(0.12, -0.44) * mm});
            skLineSegment(sketch, "E390", {"start": v(0.12, -0.44) * mm, "end": v(0.13, -0.44) * mm});
            skLineSegment(sketch, "E391", {"start": v(0.13, -0.44) * mm, "end": v(0.14, -0.44) * mm});
            skLineSegment(sketch, "E392", {"start": v(0.14, -0.44) * mm, "end": v(0.14, -0.44) * mm});
            skLineSegment(sketch, "E393", {"start": v(0.14, -0.44) * mm, "end": v(0.15, -0.44) * mm});
            skLineSegment(sketch, "E394", {"start": v(0.15, -0.44) * mm, "end": v(0.16, -0.44) * mm});
            skLineSegment(sketch, "E395", {"start": v(0.16, -0.44) * mm, "end": v(0.16, -0.44) * mm});
            skLineSegment(sketch, "E396", {"start": v(0.16, -0.44) * mm, "end": v(0.17, -0.44) * mm});
            skLineSegment(sketch, "E397", {"start": v(0.17, -0.44) * mm, "end": v(0.17, -0.45) * mm});
            skLineSegment(sketch, "E398", {"start": v(0.17, -0.45) * mm, "end": v(0.16, -0.45) * mm});
            skLineSegment(sketch, "E399", {"start": v(0.16, -0.45) * mm, "end": v(0.16, -0.46) * mm});
            skLineSegment(sketch, "E400", {"start": v(0.16, -0.46) * mm, "end": v(0.15, -0.46) * mm});
            skLineSegment(sketch, "E401", {"start": v(0.15, -0.46) * mm, "end": v(0.14, -0.46) * mm});
            skLineSegment(sketch, "E402", {"start": v(0.14, -0.46) * mm, "end": v(0.13, -0.46) * mm});
            skLineSegment(sketch, "E403", {"start": v(0.13, -0.46) * mm, "end": v(0.13, -0.46) * mm});
            skLineSegment(sketch, "E404", {"start": v(0.13, -0.46) * mm, "end": v(0.12, -0.46) * mm});
            skLineSegment(sketch, "E405", {"start": v(0.12, -0.46) * mm, "end": v(0.11, -0.46) * mm});
            skLineSegment(sketch, "E406", {"start": v(0.11, -0.46) * mm, "end": v(0.1, -0.47) * mm});
            skLineSegment(sketch, "E407", {"start": v(0.1, -0.47) * mm, "end": v(0.1, -0.49) * mm});
            skLineSegment(sketch, "E408", {"start": v(0.1, -0.49) * mm, "end": v(0.1, -0.5) * mm});
            skLineSegment(sketch, "E409", {"start": v(0.1, -0.5) * mm, "end": v(0.1, -0.5) * mm});
            skLineSegment(sketch, "E410", {"start": v(0.1, -0.5) * mm, "end": v(0.1, -0.52) * mm});
            skLineSegment(sketch, "E411", {"start": v(0.1, -0.52) * mm, "end": v(0.1, -0.53) * mm});
            skLineSegment(sketch, "E412", {"start": v(0.1, -0.53) * mm, "end": v(0.09, -0.53) * mm});
            skLineSegment(sketch, "E413", {"start": v(0.09, -0.53) * mm, "end": v(0.09, -0.54) * mm});
            skLineSegment(sketch, "E414", {"start": v(0.09, -0.54) * mm, "end": v(0.09, -0.54) * mm});
            skLineSegment(sketch, "E415", {"start": v(0.09, -0.54) * mm, "end": v(0.08, -0.56) * mm});
            skLineSegment(sketch, "E416", {"start": v(0.08, -0.56) * mm, "end": v(0.08, -0.57) * mm});
            skLineSegment(sketch, "E417", {"start": v(0.08, -0.57) * mm, "end": v(0.08, -0.57) * mm});
            skLineSegment(sketch, "E418", {"start": v(0.08, -0.57) * mm, "end": v(0.08, -0.58) * mm});
            skLineSegment(sketch, "E419", {"start": v(0.08, -0.58) * mm, "end": v(0.08, -0.6) * mm});
            skLineSegment(sketch, "E420", {"start": v(0.08, -0.6) * mm, "end": v(0.08, -0.6) * mm});
            skLineSegment(sketch, "E421", {"start": v(0.08, -0.6) * mm, "end": v(0.07, -0.6) * mm});
            skLineSegment(sketch, "E422", {"start": v(0.07, -0.6) * mm, "end": v(0.07, -0.6) * mm});
            skLineSegment(sketch, "E423", {"start": v(0.07, -0.6) * mm, "end": v(0.07, -0.62) * mm});
            skLineSegment(sketch, "E424", {"start": v(0.07, -0.62) * mm, "end": v(0.07, -0.62) * mm});
            skLineSegment(sketch, "E425", {"start": v(0.07, -0.62) * mm, "end": v(0.08, -0.63) * mm});
            skLineSegment(sketch, "E426", {"start": v(0.08, -0.63) * mm, "end": v(0.08, -0.64) * mm});
            skLineSegment(sketch, "E427", {"start": v(0.08, -0.64) * mm, "end": v(0.08, -0.65) * mm});
            skLineSegment(sketch, "E428", {"start": v(0.08, -0.65) * mm, "end": v(0.1, -0.66) * mm});
            skLineSegment(sketch, "E429", {"start": v(0.1, -0.66) * mm, "end": v(0.1, -0.66) * mm});
            skLineSegment(sketch, "E430", {"start": v(0.1, -0.66) * mm, "end": v(0.1, -0.67) * mm});
            skLineSegment(sketch, "E431", {"start": v(0.1, -0.67) * mm, "end": v(0.1, -0.67) * mm});
            skLineSegment(sketch, "E432", {"start": v(0.1, -0.67) * mm, "end": v(0.1, -0.68) * mm});
            skLineSegment(sketch, "E433", {"start": v(0.1, -0.68) * mm, "end": v(0.09, -0.68) * mm});
            skLineSegment(sketch, "E434", {"start": v(0.09, -0.68) * mm, "end": v(0.08, -0.68) * mm});
            skLineSegment(sketch, "E435", {"start": v(0.08, -0.68) * mm, "end": v(0.07, -0.68) * mm});
            skLineSegment(sketch, "E436", {"start": v(0.07, -0.68) * mm, "end": v(0.07, -0.68) * mm});
            skLineSegment(sketch, "E437", {"start": v(0.07, -0.68) * mm, "end": v(0.06, -0.68) * mm});
            skLineSegment(sketch, "E438", {"start": v(0.06, -0.68) * mm, "end": v(0.04, -0.68) * mm});
            skLineSegment(sketch, "E439", {"start": v(0.04, -0.68) * mm, "end": v(0.04, -0.68) * mm});
            skLineSegment(sketch, "E440", {"start": v(0.04, -0.68) * mm, "end": v(0.03, -0.67) * mm});
            skLineSegment(sketch, "E441", {"start": v(0.03, -0.67) * mm, "end": v(0.02, -0.64) * mm});
            skLineSegment(sketch, "E442", {"start": v(0.02, -0.64) * mm, "end": v(0.01, -0.61) * mm});
            skLineSegment(sketch, "E443", {"start": v(0.01, -0.61) * mm, "end": v(0, -0.58) * mm});
            skLineSegment(sketch, "E444", {"start": v(0, -0.58) * mm, "end": v(0, -0.54) * mm});
            skLineSegment(sketch, "E445", {"start": v(0, -0.54) * mm, "end": v(0, -0.52) * mm});
            skLineSegment(sketch, "E446", {"start": v(0, -0.52) * mm, "end": v(-0.01, -0.51) * mm});
            skLineSegment(sketch, "E447", {"start": v(-0.01, -0.51) * mm, "end": v(-0.02, -0.52) * mm});
            skLineSegment(sketch, "E448", {"start": v(-0.02, -0.52) * mm, "end": v(-0.02, -0.52) * mm});
            skLineSegment(sketch, "E449", {"start": v(-0.02, -0.52) * mm, "end": v(-0.04, -0.56) * mm});
            skLineSegment(sketch, "E450", {"start": v(-0.04, -0.56) * mm, "end": v(-0.06, -0.6) * mm});
            skLineSegment(sketch, "E451", {"start": v(-0.06, -0.6) * mm, "end": v(-0.07, -0.62) * mm});
            skLineSegment(sketch, "E452", {"start": v(-0.07, -0.62) * mm, "end": v(-0.08, -0.64) * mm});
            skLineSegment(sketch, "E453", {"start": v(-0.08, -0.64) * mm, "end": v(-0.08, -0.64) * mm});
            skLineSegment(sketch, "E454", {"start": v(-0.08, -0.64) * mm, "end": v(-0.09, -0.65) * mm});
            skLineSegment(sketch, "E455", {"start": v(-0.09, -0.65) * mm, "end": v(-0.1, -0.66) * mm});
            skLineSegment(sketch, "E456", {"start": v(-0.1, -0.66) * mm, "end": v(-0.1, -0.67) * mm});
            skLineSegment(sketch, "E457", {"start": v(-0.1, -0.67) * mm, "end": v(-0.12, -0.67) * mm});
            skLineSegment(sketch, "E458", {"start": v(-0.12, -0.67) * mm, "end": v(-0.12, -0.66) * mm});
            skLineSegment(sketch, "E459", {"start": v(-0.12, -0.66) * mm, "end": v(-0.13, -0.66) * mm});
            skLineSegment(sketch, "E460", {"start": v(-0.13, -0.66) * mm, "end": v(-0.14, -0.66) * mm});
            skLineSegment(sketch, "E461", {"start": v(-0.14, -0.66) * mm, "end": v(-0.15, -0.67) * mm});
            skLineSegment(sketch, "E462", {"start": v(-0.45, -0.48) * mm, "end": v(-0.46, -0.47) * mm});
            skLineSegment(sketch, "E463", {"start": v(-0.46, -0.47) * mm, "end": v(-0.46, -0.45) * mm});
            skLineSegment(sketch, "E464", {"start": v(-0.46, -0.45) * mm, "end": v(-0.45, -0.44) * mm});
            skLineSegment(sketch, "E465", {"start": v(-0.45, -0.44) * mm, "end": v(-0.44, -0.43) * mm});
            skLineSegment(sketch, "E466", {"start": v(-0.44, -0.43) * mm, "end": v(-0.43, -0.42) * mm});
            skLineSegment(sketch, "E467", {"start": v(-0.43, -0.42) * mm, "end": v(-0.43, -0.4) * mm});
            skLineSegment(sketch, "E468", {"start": v(-0.43, -0.4) * mm, "end": v(-0.42, -0.4) * mm});
            skLineSegment(sketch, "E469", {"start": v(-0.42, -0.4) * mm, "end": v(-0.41, -0.39) * mm});
            skLineSegment(sketch, "E470", {"start": v(-0.41, -0.39) * mm, "end": v(-0.4, -0.38) * mm});
            skLineSegment(sketch, "E471", {"start": v(-0.4, -0.38) * mm, "end": v(-0.4, -0.37) * mm});
            skLineSegment(sketch, "E472", {"start": v(-0.4, -0.37) * mm, "end": v(-0.4, -0.35) * mm});
            skLineSegment(sketch, "E473", {"start": v(-0.4, -0.35) * mm, "end": v(-0.4, -0.34) * mm});
            skLineSegment(sketch, "E474", {"start": v(-0.4, -0.34) * mm, "end": v(-0.38, -0.33) * mm});
            skLineSegment(sketch, "E475", {"start": v(-0.38, -0.33) * mm, "end": v(-0.36, -0.3) * mm});
            skLineSegment(sketch, "E476", {"start": v(-0.36, -0.3) * mm, "end": v(-0.36, -0.28) * mm});
            skLineSegment(sketch, "E477", {"start": v(-0.36, -0.28) * mm, "end": v(-0.36, -0.27) * mm});
            skLineSegment(sketch, "E478", {"start": v(-0.36, -0.27) * mm, "end": v(-0.36, -0.26) * mm});
            skLineSegment(sketch, "E479", {"start": v(-0.36, -0.26) * mm, "end": v(-0.37, -0.26) * mm});
            skLineSegment(sketch, "E480", {"start": v(-0.37, -0.26) * mm, "end": v(-0.37, -0.26) * mm});
            skLineSegment(sketch, "E481", {"start": v(-0.37, -0.26) * mm, "end": v(-0.37, -0.25) * mm});
            skLineSegment(sketch, "E482", {"start": v(-0.37, -0.25) * mm, "end": v(-0.37, -0.24) * mm});
            skLineSegment(sketch, "E483", {"start": v(-0.37, -0.24) * mm, "end": v(-0.37, -0.24) * mm});
            skLineSegment(sketch, "E484", {"start": v(-0.37, -0.24) * mm, "end": v(-0.36, -0.23) * mm});
            skLineSegment(sketch, "E485", {"start": v(-0.36, -0.23) * mm, "end": v(-0.35, -0.24) * mm});
            skLineSegment(sketch, "E486", {"start": v(-0.35, -0.24) * mm, "end": v(-0.33, -0.26) * mm});
            skLineSegment(sketch, "E487", {"start": v(-0.33, -0.26) * mm, "end": v(-0.32, -0.27) * mm});
            skLineSegment(sketch, "E488", {"start": v(-0.32, -0.27) * mm, "end": v(-0.3, -0.28) * mm});
            skLineSegment(sketch, "E489", {"start": v(-0.3, -0.28) * mm, "end": v(-0.3, -0.29) * mm});
            skLineSegment(sketch, "E490", {"start": v(-0.3, -0.29) * mm, "end": v(-0.29, -0.3) * mm});
            skLineSegment(sketch, "E491", {"start": v(-0.29, -0.3) * mm, "end": v(-0.28, -0.3) * mm});
            skLineSegment(sketch, "E492", {"start": v(-0.28, -0.3) * mm, "end": v(-0.28, -0.3) * mm});
            skLineSegment(sketch, "E493", {"start": v(-0.28, -0.3) * mm, "end": v(-0.3, -0.31) * mm});
            skLineSegment(sketch, "E494", {"start": v(-0.3, -0.31) * mm, "end": v(-0.3, -0.3) * mm});
            skLineSegment(sketch, "E495", {"start": v(-0.3, -0.3) * mm, "end": v(-0.31, -0.3) * mm});
            skLineSegment(sketch, "E496", {"start": v(-0.31, -0.3) * mm, "end": v(-0.32, -0.3) * mm});
            skLineSegment(sketch, "E497", {"start": v(-0.32, -0.3) * mm, "end": v(-0.33, -0.31) * mm});
            skLineSegment(sketch, "E498", {"start": v(-0.33, -0.31) * mm, "end": v(-0.33, -0.32) * mm});
            skLineSegment(sketch, "E499", {"start": v(-0.33, -0.32) * mm, "end": v(-0.34, -0.33) * mm});
            skLineSegment(sketch, "E500", {"start": v(-0.34, -0.33) * mm, "end": v(-0.34, -0.34) * mm});
            skLineSegment(sketch, "E501", {"start": v(-0.34, -0.34) * mm, "end": v(-0.34, -0.34) * mm});
            skLineSegment(sketch, "E502", {"start": v(-0.34, -0.34) * mm, "end": v(-0.35, -0.35) * mm});
            skLineSegment(sketch, "E503", {"start": v(-0.35, -0.35) * mm, "end": v(-0.35, -0.36) * mm});
            skLineSegment(sketch, "E504", {"start": v(-0.35, -0.36) * mm, "end": v(-0.34, -0.36) * mm});
            skLineSegment(sketch, "E505", {"start": v(-0.34, -0.36) * mm, "end": v(-0.33, -0.37) * mm});
            skLineSegment(sketch, "E506", {"start": v(-0.33, -0.37) * mm, "end": v(-0.33, -0.38) * mm});
            skLineSegment(sketch, "E507", {"start": v(-0.33, -0.38) * mm, "end": v(-0.32, -0.38) * mm});
            skLineSegment(sketch, "E508", {"start": v(-0.32, -0.38) * mm, "end": v(-0.32, -0.39) * mm});
            skLineSegment(sketch, "E509", {"start": v(-0.32, -0.39) * mm, "end": v(-0.31, -0.39) * mm});
            skLineSegment(sketch, "E510", {"start": v(-0.31, -0.39) * mm, "end": v(-0.3, -0.39) * mm});
            skLineSegment(sketch, "E511", {"start": v(-0.3, -0.39) * mm, "end": v(-0.3, -0.38) * mm});
            skLineSegment(sketch, "E512", {"start": v(-0.3, -0.38) * mm, "end": v(-0.3, -0.38) * mm});
            skLineSegment(sketch, "E513", {"start": v(-0.3, -0.38) * mm, "end": v(-0.28, -0.37) * mm});
            skLineSegment(sketch, "E514", {"start": v(-0.28, -0.37) * mm, "end": v(-0.27, -0.37) * mm});
            skLineSegment(sketch, "E515", {"start": v(-0.27, -0.37) * mm, "end": v(-0.27, -0.36) * mm});
            skLineSegment(sketch, "E516", {"start": v(-0.27, -0.36) * mm, "end": v(-0.26, -0.36) * mm});
            skLineSegment(sketch, "E517", {"start": v(-0.26, -0.36) * mm, "end": v(-0.27, -0.35) * mm});
            skLineSegment(sketch, "E518", {"start": v(-0.27, -0.35) * mm, "end": v(-0.27, -0.34) * mm});
            skLineSegment(sketch, "E519", {"start": v(-0.27, -0.34) * mm, "end": v(-0.26, -0.33) * mm});
            skLineSegment(sketch, "E520", {"start": v(-0.26, -0.33) * mm, "end": v(-0.26, -0.33) * mm});
            skLineSegment(sketch, "E521", {"start": v(-0.26, -0.33) * mm, "end": v(-0.25, -0.33) * mm});
            skLineSegment(sketch, "E522", {"start": v(-0.25, -0.33) * mm, "end": v(-0.25, -0.33) * mm});
            skLineSegment(sketch, "E523", {"start": v(-0.25, -0.33) * mm, "end": v(-0.25, -0.34) * mm});
            skLineSegment(sketch, "E524", {"start": v(-0.25, -0.34) * mm, "end": v(-0.24, -0.34) * mm});
            skLineSegment(sketch, "E525", {"start": v(-0.24, -0.34) * mm, "end": v(-0.24, -0.34) * mm});
            skLineSegment(sketch, "E526", {"start": v(-0.24, -0.34) * mm, "end": v(-0.23, -0.35) * mm});
            skLineSegment(sketch, "E527", {"start": v(-0.23, -0.35) * mm, "end": v(-0.23, -0.35) * mm});
            skLineSegment(sketch, "E528", {"start": v(-0.23, -0.35) * mm, "end": v(-0.22, -0.36) * mm});
            skLineSegment(sketch, "E529", {"start": v(-0.22, -0.36) * mm, "end": v(-0.21, -0.36) * mm});
            skLineSegment(sketch, "E530", {"start": v(-0.21, -0.36) * mm, "end": v(-0.2, -0.37) * mm});
            skLineSegment(sketch, "E531", {"start": v(-0.2, -0.37) * mm, "end": v(-0.2, -0.37) * mm});
            skLineSegment(sketch, "E532", {"start": v(-0.2, -0.37) * mm, "end": v(-0.2, -0.38) * mm});
            skLineSegment(sketch, "E533", {"start": v(-0.2, -0.38) * mm, "end": v(-0.19, -0.39) * mm});
            skLineSegment(sketch, "E534", {"start": v(-0.19, -0.39) * mm, "end": v(-0.18, -0.4) * mm});
            skLineSegment(sketch, "E535", {"start": v(-0.18, -0.4) * mm, "end": v(-0.18, -0.4) * mm});
            skLineSegment(sketch, "E536", {"start": v(-0.18, -0.4) * mm, "end": v(-0.2, -0.4) * mm});
            skLineSegment(sketch, "E537", {"start": v(-0.2, -0.4) * mm, "end": v(-0.21, -0.4) * mm});
            skLineSegment(sketch, "E538", {"start": v(-0.21, -0.4) * mm, "end": v(-0.22, -0.4) * mm});
            skLineSegment(sketch, "E539", {"start": v(-0.22, -0.4) * mm, "end": v(-0.22, -0.4) * mm});
            skLineSegment(sketch, "E540", {"start": v(-0.22, -0.4) * mm, "end": v(-0.23, -0.4) * mm});
            skLineSegment(sketch, "E541", {"start": v(-0.23, -0.4) * mm, "end": v(-0.23, -0.4) * mm});
            skLineSegment(sketch, "E542", {"start": v(-0.23, -0.4) * mm, "end": v(-0.24, -0.4) * mm});
            skLineSegment(sketch, "E543", {"start": v(-0.24, -0.4) * mm, "end": v(-0.26, -0.4) * mm});
            skLineSegment(sketch, "E544", {"start": v(-0.26, -0.4) * mm, "end": v(-0.29, -0.42) * mm});
            skLineSegment(sketch, "E545", {"start": v(-0.29, -0.42) * mm, "end": v(-0.3, -0.42) * mm});
            skLineSegment(sketch, "E546", {"start": v(-0.3, -0.42) * mm, "end": v(-0.31, -0.43) * mm});
            skLineSegment(sketch, "E547", {"start": v(-0.31, -0.43) * mm, "end": v(-0.33, -0.43) * mm});
            skLineSegment(sketch, "E548", {"start": v(-0.33, -0.43) * mm, "end": v(-0.35, -0.44) * mm});
            skLineSegment(sketch, "E549", {"start": v(-0.35, -0.44) * mm, "end": v(-0.36, -0.45) * mm});
            skLineSegment(sketch, "E550", {"start": v(-0.36, -0.45) * mm, "end": v(-0.38, -0.45) * mm});
            skLineSegment(sketch, "E551", {"start": v(-0.38, -0.45) * mm, "end": v(-0.39, -0.46) * mm});
            skLineSegment(sketch, "E552", {"start": v(-0.39, -0.46) * mm, "end": v(-0.4, -0.47) * mm});
            skLineSegment(sketch, "E553", {"start": v(-0.4, -0.47) * mm, "end": v(-0.41, -0.48) * mm});
            skLineSegment(sketch, "E554", {"start": v(-0.41, -0.48) * mm, "end": v(-0.43, -0.49) * mm});
            skLineSegment(sketch, "E555", {"start": v(-0.43, -0.49) * mm, "end": v(-0.44, -0.49) * mm});
            skLineSegment(sketch, "E556", {"start": v(-0.44, -0.49) * mm, "end": v(-0.45, -0.48) * mm});
            skLineSegment(sketch, "E557", {"start": v(-0.45, -0.48) * mm, "end": v(-0.45, -0.48) * mm});
            skLineSegment(sketch, "E558", {"start": v(-0.4, -0.43) * mm, "end": v(-0.4, -0.43) * mm});
            skLineSegment(sketch, "E559", {"start": v(-0.4, -0.43) * mm, "end": v(-0.38, -0.43) * mm});
            skLineSegment(sketch, "E560", {"start": v(-0.38, -0.43) * mm, "end": v(-0.38, -0.42) * mm});
            skLineSegment(sketch, "E561", {"start": v(-0.38, -0.42) * mm, "end": v(-0.37, -0.42) * mm});
            skLineSegment(sketch, "E562", {"start": v(-0.37, -0.42) * mm, "end": v(-0.37, -0.42) * mm});
            skLineSegment(sketch, "E563", {"start": v(-0.37, -0.42) * mm, "end": v(-0.36, -0.41) * mm});
            skLineSegment(sketch, "E564", {"start": v(-0.36, -0.41) * mm, "end": v(-0.36, -0.4) * mm});
            skLineSegment(sketch, "E565", {"start": v(-0.36, -0.4) * mm, "end": v(-0.36, -0.4) * mm});
            skLineSegment(sketch, "E566", {"start": v(-0.36, -0.4) * mm, "end": v(-0.35, -0.4) * mm});
            skLineSegment(sketch, "E567", {"start": v(-0.35, -0.4) * mm, "end": v(-0.36, -0.4) * mm});
            skLineSegment(sketch, "E568", {"start": v(-0.36, -0.4) * mm, "end": v(-0.37, -0.39) * mm});
            skLineSegment(sketch, "E569", {"start": v(-0.37, -0.39) * mm, "end": v(-0.37, -0.39) * mm});
            skLineSegment(sketch, "E570", {"start": v(-0.37, -0.39) * mm, "end": v(-0.38, -0.4) * mm});
            skLineSegment(sketch, "E571", {"start": v(-0.38, -0.4) * mm, "end": v(-0.38, -0.4) * mm});
            skLineSegment(sketch, "E572", {"start": v(-0.38, -0.4) * mm, "end": v(-0.4, -0.42) * mm});
            skLineSegment(sketch, "E573", {"start": v(-0.4, -0.42) * mm, "end": v(-0.4, -0.42) * mm});
            skLineSegment(sketch, "E574", {"start": v(-0.4, -0.42) * mm, "end": v(-0.4, -0.43) * mm});
            skLineSegment(sketch, "E575", {"start": v(-0.57, -0.27) * mm, "end": v(-0.58, -0.28) * mm});
            skLineSegment(sketch, "E576", {"start": v(-0.58, -0.28) * mm, "end": v(-0.59, -0.28) * mm});
            skLineSegment(sketch, "E577", {"start": v(-0.59, -0.28) * mm, "end": v(-0.6, -0.28) * mm});
            skLineSegment(sketch, "E578", {"start": v(-0.6, -0.28) * mm, "end": v(-0.6, -0.28) * mm});
            skLineSegment(sketch, "E579", {"start": v(-0.6, -0.28) * mm, "end": v(-0.61, -0.29) * mm});
            skLineSegment(sketch, "E580", {"start": v(-0.61, -0.29) * mm, "end": v(-0.62, -0.29) * mm});
            skLineSegment(sketch, "E581", {"start": v(-0.62, -0.29) * mm, "end": v(-0.62, -0.29) * mm});
            skLineSegment(sketch, "E582", {"start": v(-0.62, -0.29) * mm, "end": v(-0.63, -0.29) * mm});
            skLineSegment(sketch, "E583", {"start": v(-0.63, -0.29) * mm, "end": v(-0.64, -0.3) * mm});
            skLineSegment(sketch, "E584", {"start": v(-0.64, -0.3) * mm, "end": v(-0.65, -0.3) * mm});
            skLineSegment(sketch, "E585", {"start": v(-0.65, -0.3) * mm, "end": v(-0.67, -0.3) * mm});
            skLineSegment(sketch, "E586", {"start": v(-0.67, -0.3) * mm, "end": v(-0.67, -0.3) * mm});
            skLineSegment(sketch, "E587", {"start": v(-0.67, -0.3) * mm, "end": v(-0.68, -0.28) * mm});
            skLineSegment(sketch, "E588", {"start": v(-0.68, -0.28) * mm, "end": v(-0.69, -0.28) * mm});
            skLineSegment(sketch, "E589", {"start": v(-0.69, -0.28) * mm, "end": v(-0.7, -0.27) * mm});
            skLineSegment(sketch, "E590", {"start": v(-0.7, -0.27) * mm, "end": v(-0.7, -0.27) * mm});
            skLineSegment(sketch, "E591", {"start": v(-0.7, -0.27) * mm, "end": v(-0.7, -0.26) * mm});
            skLineSegment(sketch, "E592", {"start": v(-0.7, -0.26) * mm, "end": v(-0.68, -0.25) * mm});
            skLineSegment(sketch, "E593", {"start": v(-0.68, -0.25) * mm, "end": v(-0.66, -0.26) * mm});
            skLineSegment(sketch, "E594", {"start": v(-0.66, -0.26) * mm, "end": v(-0.64, -0.25) * mm});
            skLineSegment(sketch, "E595", {"start": v(-0.64, -0.25) * mm, "end": v(-0.62, -0.25) * mm});
            skLineSegment(sketch, "E596", {"start": v(-0.62, -0.25) * mm, "end": v(-0.6, -0.25) * mm});
            skLineSegment(sketch, "E597", {"start": v(-0.6, -0.25) * mm, "end": v(-0.59, -0.25) * mm});
            skLineSegment(sketch, "E598", {"start": v(-0.59, -0.25) * mm, "end": v(-0.58, -0.25) * mm});
            skLineSegment(sketch, "E599", {"start": v(-0.58, -0.25) * mm, "end": v(-0.56, -0.25) * mm});
            skLineSegment(sketch, "E600", {"start": v(-0.56, -0.25) * mm, "end": v(-0.56, -0.25) * mm});
            skLineSegment(sketch, "E601", {"start": v(-0.56, -0.25) * mm, "end": v(-0.55, -0.26) * mm});
            skLineSegment(sketch, "E602", {"start": v(-0.55, -0.26) * mm, "end": v(-0.56, -0.27) * mm});
            skLineSegment(sketch, "E603", {"start": v(-0.56, -0.27) * mm, "end": v(-0.57, -0.27) * mm});
            skLineSegment(sketch, "E604", {"start": v(-0.6, -0.1) * mm, "end": v(-0.61, -0.09) * mm});
            skLineSegment(sketch, "E605", {"start": v(-0.61, -0.09) * mm, "end": v(-0.62, -0.08) * mm});
            skLineSegment(sketch, "E606", {"start": v(-0.62, -0.08) * mm, "end": v(-0.63, -0.08) * mm});
            skLineSegment(sketch, "E607", {"start": v(-0.63, -0.08) * mm, "end": v(-0.63, -0.06) * mm});
            skLineSegment(sketch, "E608", {"start": v(-0.63, -0.06) * mm, "end": v(-0.65, -0.05) * mm});
            skLineSegment(sketch, "E609", {"start": v(-0.65, -0.05) * mm, "end": v(-0.65, -0.02) * mm});
            skLineSegment(sketch, "E610", {"start": v(-0.65, -0.02) * mm, "end": v(-0.65, 0) * mm});
            skLineSegment(sketch, "E611", {"start": v(-0.65, 0) * mm, "end": v(-0.65, 0) * mm});
            skLineSegment(sketch, "E612", {"start": v(-0.65, 0) * mm, "end": v(-0.64, 0.02) * mm});
            skLineSegment(sketch, "E613", {"start": v(-0.64, 0.02) * mm, "end": v(-0.63, 0.02) * mm});
            skLineSegment(sketch, "E614", {"start": v(-0.63, 0.02) * mm, "end": v(-0.62, 0.02) * mm});
            skLineSegment(sketch, "E615", {"start": v(-0.62, 0.02) * mm, "end": v(-0.6, 0.01) * mm});
            skLineSegment(sketch, "E616", {"start": v(-0.6, 0.01) * mm, "end": v(-0.6, 0) * mm});
            skLineSegment(sketch, "E617", {"start": v(-0.6, 0) * mm, "end": v(-0.6, 0) * mm});
            skLineSegment(sketch, "E618", {"start": v(-0.6, 0) * mm, "end": v(-0.6, -0.01) * mm});
            skLineSegment(sketch, "E619", {"start": v(-0.6, -0.01) * mm, "end": v(-0.61, -0.02) * mm});
            skLineSegment(sketch, "E620", {"start": v(-0.61, -0.02) * mm, "end": v(-0.61, -0.03) * mm});
            skLineSegment(sketch, "E621", {"start": v(-0.61, -0.03) * mm, "end": v(-0.61, -0.04) * mm});
            skLineSegment(sketch, "E622", {"start": v(-0.61, -0.04) * mm, "end": v(-0.6, -0.05) * mm});
            skLineSegment(sketch, "E623", {"start": v(-0.6, -0.05) * mm, "end": v(-0.6, -0.05) * mm});
            skLineSegment(sketch, "E624", {"start": v(-0.6, -0.05) * mm, "end": v(-0.6, -0.06) * mm});
            skLineSegment(sketch, "E625", {"start": v(-0.6, -0.06) * mm, "end": v(-0.58, -0.05) * mm});
            skLineSegment(sketch, "E626", {"start": v(-0.58, -0.05) * mm, "end": v(-0.58, -0.04) * mm});
            skLineSegment(sketch, "E627", {"start": v(-0.58, -0.04) * mm, "end": v(-0.58, -0.03) * mm});
            skLineSegment(sketch, "E628", {"start": v(-0.58, -0.03) * mm, "end": v(-0.58, -0.02) * mm});
            skLineSegment(sketch, "E629", {"start": v(-0.58, -0.02) * mm, "end": v(-0.57, 0) * mm});
            skLineSegment(sketch, "E630", {"start": v(-0.57, 0) * mm, "end": v(-0.56, 0.02) * mm});
            skLineSegment(sketch, "E631", {"start": v(-0.56, 0.02) * mm, "end": v(-0.55, 0.02) * mm});
            skLineSegment(sketch, "E632", {"start": v(-0.55, 0.02) * mm, "end": v(-0.55, 0.03) * mm});
            skLineSegment(sketch, "E633", {"start": v(-0.55, 0.03) * mm, "end": v(-0.55, 0.03) * mm});
            skLineSegment(sketch, "E634", {"start": v(-0.55, 0.03) * mm, "end": v(-0.54, 0.04) * mm});
            skLineSegment(sketch, "E635", {"start": v(-0.54, 0.04) * mm, "end": v(-0.53, 0.06) * mm});
            skLineSegment(sketch, "E636", {"start": v(-0.53, 0.06) * mm, "end": v(-0.5, 0.07) * mm});
            skLineSegment(sketch, "E637", {"start": v(-0.5, 0.07) * mm, "end": v(-0.5, 0.07) * mm});
            skLineSegment(sketch, "E638", {"start": v(-0.5, 0.07) * mm, "end": v(-0.48, 0.07) * mm});
            skLineSegment(sketch, "E639", {"start": v(-0.48, 0.07) * mm, "end": v(-0.47, 0.07) * mm});
            skLineSegment(sketch, "E640", {"start": v(-0.47, 0.07) * mm, "end": v(-0.46, 0.07) * mm});
            skLineSegment(sketch, "E641", {"start": v(-0.46, 0.07) * mm, "end": v(-0.45, 0.07) * mm});
            skLineSegment(sketch, "E642", {"start": v(-0.45, 0.07) * mm, "end": v(-0.44, 0.07) * mm});
            skLineSegment(sketch, "E643", {"start": v(-0.44, 0.07) * mm, "end": v(-0.44, 0.06) * mm});
            skLineSegment(sketch, "E644", {"start": v(-0.44, 0.06) * mm, "end": v(-0.43, 0.06) * mm});
            skLineSegment(sketch, "E645", {"start": v(-0.43, 0.06) * mm, "end": v(-0.42, 0.05) * mm});
            skLineSegment(sketch, "E646", {"start": v(-0.42, 0.05) * mm, "end": v(-0.42, 0.05) * mm});
            skLineSegment(sketch, "E647", {"start": v(-0.42, 0.05) * mm, "end": v(-0.41, 0.04) * mm});
            skLineSegment(sketch, "E648", {"start": v(-0.41, 0.04) * mm, "end": v(-0.4, 0.03) * mm});
            skLineSegment(sketch, "E649", {"start": v(-0.4, 0.03) * mm, "end": v(-0.4, 0.02) * mm});
            skLineSegment(sketch, "E650", {"start": v(-0.4, 0.02) * mm, "end": v(-0.4, 0.01) * mm});
            skLineSegment(sketch, "E651", {"start": v(-0.4, 0.01) * mm, "end": v(-0.39, 0) * mm});
            skLineSegment(sketch, "E652", {"start": v(-0.39, 0) * mm, "end": v(-0.39, 0) * mm});
            skLineSegment(sketch, "E653", {"start": v(-0.39, 0) * mm, "end": v(-0.38, -0.01) * mm});
            skLineSegment(sketch, "E654", {"start": v(-0.38, -0.01) * mm, "end": v(-0.38, -0.02) * mm});
            skLineSegment(sketch, "E655", {"start": v(-0.38, -0.02) * mm, "end": v(-0.38, -0.02) * mm});
            skLineSegment(sketch, "E656", {"start": v(-0.38, -0.02) * mm, "end": v(-0.38, -0.03) * mm});
            skLineSegment(sketch, "E657", {"start": v(-0.38, -0.03) * mm, "end": v(-0.38, -0.04) * mm});
            skLineSegment(sketch, "E658", {"start": v(-0.38, -0.04) * mm, "end": v(-0.38, -0.05) * mm});
            skLineSegment(sketch, "E659", {"start": v(-0.38, -0.05) * mm, "end": v(-0.38, -0.05) * mm});
            skLineSegment(sketch, "E660", {"start": v(-0.38, -0.05) * mm, "end": v(-0.39, -0.06) * mm});
            skLineSegment(sketch, "E661", {"start": v(-0.39, -0.06) * mm, "end": v(-0.39, -0.07) * mm});
            skLineSegment(sketch, "E662", {"start": v(-0.39, -0.07) * mm, "end": v(-0.39, -0.08) * mm});
            skLineSegment(sketch, "E663", {"start": v(-0.39, -0.08) * mm, "end": v(-0.4, -0.09) * mm});
            skLineSegment(sketch, "E664", {"start": v(-0.4, -0.09) * mm, "end": v(-0.4, -0.1) * mm});
            skLineSegment(sketch, "E665", {"start": v(-0.4, -0.1) * mm, "end": v(-0.4, -0.1) * mm});
            skLineSegment(sketch, "E666", {"start": v(-0.4, -0.1) * mm, "end": v(-0.42, -0.11) * mm});
            skLineSegment(sketch, "E667", {"start": v(-0.42, -0.11) * mm, "end": v(-0.43, -0.12) * mm});
            skLineSegment(sketch, "E668", {"start": v(-0.43, -0.12) * mm, "end": v(-0.44, -0.12) * mm});
            skLineSegment(sketch, "E669", {"start": v(-0.44, -0.12) * mm, "end": v(-0.46, -0.11) * mm});
            skLineSegment(sketch, "E670", {"start": v(-0.46, -0.11) * mm, "end": v(-0.47, -0.1) * mm});
            skLineSegment(sketch, "E671", {"start": v(-0.47, -0.1) * mm, "end": v(-0.47, -0.08) * mm});
            skLineSegment(sketch, "E672", {"start": v(-0.47, -0.08) * mm, "end": v(-0.46, -0.07) * mm});
            skLineSegment(sketch, "E673", {"start": v(-0.46, -0.07) * mm, "end": v(-0.45, -0.07) * mm});
            skLineSegment(sketch, "E674", {"start": v(-0.45, -0.07) * mm, "end": v(-0.45, -0.07) * mm});
            skLineSegment(sketch, "E675", {"start": v(-0.45, -0.07) * mm, "end": v(-0.44, -0.07) * mm});
            skLineSegment(sketch, "E676", {"start": v(-0.44, -0.07) * mm, "end": v(-0.44, -0.07) * mm});
            skLineSegment(sketch, "E677", {"start": v(-0.44, -0.07) * mm, "end": v(-0.43, -0.06) * mm});
            skLineSegment(sketch, "E678", {"start": v(-0.43, -0.06) * mm, "end": v(-0.42, -0.05) * mm});
            skLineSegment(sketch, "E679", {"start": v(-0.42, -0.05) * mm, "end": v(-0.42, -0.04) * mm});
            skLineSegment(sketch, "E680", {"start": v(-0.42, -0.04) * mm, "end": v(-0.42, -0.03) * mm});
            skLineSegment(sketch, "E681", {"start": v(-0.42, -0.03) * mm, "end": v(-0.42, 0) * mm});
            skLineSegment(sketch, "E682", {"start": v(-0.42, 0) * mm, "end": v(-0.44, 0.01) * mm});
            skLineSegment(sketch, "E683", {"start": v(-0.44, 0.01) * mm, "end": v(-0.45, 0.02) * mm});
            skLineSegment(sketch, "E684", {"start": v(-0.45, 0.02) * mm, "end": v(-0.47, 0.02) * mm});
            skLineSegment(sketch, "E685", {"start": v(-0.47, 0.02) * mm, "end": v(-0.48, 0.02) * mm});
            skLineSegment(sketch, "E686", {"start": v(-0.48, 0.02) * mm, "end": v(-0.49, 0.02) * mm});
            skLineSegment(sketch, "E687", {"start": v(-0.49, 0.02) * mm, "end": v(-0.49, 0.02) * mm});
            skLineSegment(sketch, "E688", {"start": v(-0.49, 0.02) * mm, "end": v(-0.5, 0.01) * mm});
            skLineSegment(sketch, "E689", {"start": v(-0.5, 0.01) * mm, "end": v(-0.5, 0) * mm});
            skLineSegment(sketch, "E690", {"start": v(-0.5, 0) * mm, "end": v(-0.51, 0) * mm});
            skLineSegment(sketch, "E691", {"start": v(-0.51, 0) * mm, "end": v(-0.52, -0.02) * mm});
            skLineSegment(sketch, "E692", {"start": v(-0.52, -0.02) * mm, "end": v(-0.52, -0.02) * mm});
            skLineSegment(sketch, "E693", {"start": v(-0.52, -0.02) * mm, "end": v(-0.52, -0.03) * mm});
            skLineSegment(sketch, "E694", {"start": v(-0.52, -0.03) * mm, "end": v(-0.53, -0.03) * mm});
            skLineSegment(sketch, "E695", {"start": v(-0.53, -0.03) * mm, "end": v(-0.53, -0.04) * mm});
            skLineSegment(sketch, "E696", {"start": v(-0.53, -0.04) * mm, "end": v(-0.53, -0.05) * mm});
            skLineSegment(sketch, "E697", {"start": v(-0.53, -0.05) * mm, "end": v(-0.54, -0.05) * mm});
            skLineSegment(sketch, "E698", {"start": v(-0.54, -0.05) * mm, "end": v(-0.54, -0.06) * mm});
            skLineSegment(sketch, "E699", {"start": v(-0.54, -0.06) * mm, "end": v(-0.54, -0.07) * mm});
            skLineSegment(sketch, "E700", {"start": v(-0.54, -0.07) * mm, "end": v(-0.55, -0.07) * mm});
            skLineSegment(sketch, "E701", {"start": v(-0.55, -0.07) * mm, "end": v(-0.55, -0.08) * mm});
            skLineSegment(sketch, "E702", {"start": v(-0.55, -0.08) * mm, "end": v(-0.56, -0.09) * mm});
            skLineSegment(sketch, "E703", {"start": v(-0.56, -0.09) * mm, "end": v(-0.57, -0.1) * mm});
            skLineSegment(sketch, "E704", {"start": v(-0.57, -0.1) * mm, "end": v(-0.58, -0.1) * mm});
            skLineSegment(sketch, "E705", {"start": v(-0.58, -0.1) * mm, "end": v(-0.58, -0.1) * mm});
            skLineSegment(sketch, "E706", {"start": v(-0.58, -0.1) * mm, "end": v(-0.59, -0.1) * mm});
            skLineSegment(sketch, "E707", {"start": v(-0.59, -0.1) * mm, "end": v(-0.6, -0.1) * mm});
            skLineSegment(sketch, "E708", {"start": v(-0.6, -0.1) * mm, "end": v(-0.6, -0.1) * mm});
            skLineSegment(sketch, "E709", {"start": v(-0.51, 0.4) * mm, "end": v(-0.5, 0.4) * mm});
            skLineSegment(sketch, "E710", {"start": v(-0.5, 0.4) * mm, "end": v(-0.5, 0.4) * mm});
            skLineSegment(sketch, "E711", {"start": v(-0.5, 0.4) * mm, "end": v(-0.5, 0.41) * mm});
            skLineSegment(sketch, "E712", {"start": v(-0.5, 0.41) * mm, "end": v(-0.5, 0.42) * mm});
            skLineSegment(sketch, "E713", {"start": v(-0.5, 0.42) * mm, "end": v(-0.5, 0.42) * mm});
            skLineSegment(sketch, "E714", {"start": v(-0.5, 0.42) * mm, "end": v(-0.49, 0.42) * mm});
            skLineSegment(sketch, "E715", {"start": v(-0.49, 0.42) * mm, "end": v(-0.47, 0.44) * mm});
            skLineSegment(sketch, "E716", {"start": v(-0.47, 0.44) * mm, "end": v(-0.45, 0.45) * mm});
            skLineSegment(sketch, "E717", {"start": v(-0.45, 0.45) * mm, "end": v(-0.43, 0.45) * mm});
            skLineSegment(sketch, "E718", {"start": v(-0.43, 0.45) * mm, "end": v(-0.4, 0.45) * mm});
            skLineSegment(sketch, "E719", {"start": v(-0.4, 0.45) * mm, "end": v(-0.39, 0.44) * mm});
            skLineSegment(sketch, "E720", {"start": v(-0.39, 0.44) * mm, "end": v(-0.38, 0.43) * mm});
            skLineSegment(sketch, "E721", {"start": v(-0.38, 0.43) * mm, "end": v(-0.38, 0.41) * mm});
            skLineSegment(sketch, "E722", {"start": v(-0.38, 0.41) * mm, "end": v(-0.37, 0.4) * mm});
            skLineSegment(sketch, "E723", {"start": v(-0.37, 0.4) * mm, "end": v(-0.37, 0.4) * mm});
            skLineSegment(sketch, "E724", {"start": v(-0.37, 0.4) * mm, "end": v(-0.36, 0.4) * mm});
            skLineSegment(sketch, "E725", {"start": v(-0.36, 0.4) * mm, "end": v(-0.35, 0.4) * mm});
            skLineSegment(sketch, "E726", {"start": v(-0.35, 0.4) * mm, "end": v(-0.35, 0.4) * mm});
            skLineSegment(sketch, "E727", {"start": v(-0.35, 0.4) * mm, "end": v(-0.33, 0.4) * mm});
            skLineSegment(sketch, "E728", {"start": v(-0.33, 0.4) * mm, "end": v(-0.32, 0.4) * mm});
            skLineSegment(sketch, "E729", {"start": v(-0.32, 0.4) * mm, "end": v(-0.31, 0.39) * mm});
            skLineSegment(sketch, "E730", {"start": v(-0.31, 0.39) * mm, "end": v(-0.3, 0.38) * mm});
            skLineSegment(sketch, "E731", {"start": v(-0.3, 0.38) * mm, "end": v(-0.3, 0.37) * mm});
            skLineSegment(sketch, "E732", {"start": v(-0.3, 0.37) * mm, "end": v(-0.28, 0.36) * mm});
            skLineSegment(sketch, "E733", {"start": v(-0.28, 0.36) * mm, "end": v(-0.28, 0.35) * mm});
            skLineSegment(sketch, "E734", {"start": v(-0.28, 0.35) * mm, "end": v(-0.28, 0.35) * mm});
            skLineSegment(sketch, "E735", {"start": v(-0.28, 0.35) * mm, "end": v(-0.28, 0.34) * mm});
            skLineSegment(sketch, "E736", {"start": v(-0.28, 0.34) * mm, "end": v(-0.28, 0.34) * mm});
            skLineSegment(sketch, "E737", {"start": v(-0.28, 0.34) * mm, "end": v(-0.29, 0.3) * mm});
            skLineSegment(sketch, "E738", {"start": v(-0.29, 0.3) * mm, "end": v(-0.3, 0.28) * mm});
            skLineSegment(sketch, "E739", {"start": v(-0.3, 0.28) * mm, "end": v(-0.32, 0.26) * mm});
            skLineSegment(sketch, "E740", {"start": v(-0.32, 0.26) * mm, "end": v(-0.33, 0.25) * mm});
            skLineSegment(sketch, "E741", {"start": v(-0.33, 0.25) * mm, "end": v(-0.33, 0.24) * mm});
            skLineSegment(sketch, "E742", {"start": v(-0.33, 0.24) * mm, "end": v(-0.33, 0.24) * mm});
            skLineSegment(sketch, "E743", {"start": v(-0.33, 0.24) * mm, "end": v(-0.35, 0.23) * mm});
            skLineSegment(sketch, "E744", {"start": v(-0.35, 0.23) * mm, "end": v(-0.35, 0.23) * mm});
            skLineSegment(sketch, "E745", {"start": v(-0.35, 0.23) * mm, "end": v(-0.35, 0.22) * mm});
            skLineSegment(sketch, "E746", {"start": v(-0.35, 0.22) * mm, "end": v(-0.35, 0.21) * mm});
            skLineSegment(sketch, "E747", {"start": v(-0.35, 0.21) * mm, "end": v(-0.35, 0.21) * mm});
            skLineSegment(sketch, "E748", {"start": v(-0.35, 0.21) * mm, "end": v(-0.36, 0.21) * mm});
            skLineSegment(sketch, "E749", {"start": v(-0.36, 0.21) * mm, "end": v(-0.36, 0.2) * mm});
            skLineSegment(sketch, "E750", {"start": v(-0.36, 0.2) * mm, "end": v(-0.36, 0.2) * mm});
            skLineSegment(sketch, "E751", {"start": v(-0.36, 0.2) * mm, "end": v(-0.37, 0.2) * mm});
            skLineSegment(sketch, "E752", {"start": v(-0.37, 0.2) * mm, "end": v(-0.38, 0.2) * mm});
            skLineSegment(sketch, "E753", {"start": v(-0.38, 0.2) * mm, "end": v(-0.38, 0.21) * mm});
            skLineSegment(sketch, "E754", {"start": v(-0.38, 0.21) * mm, "end": v(-0.38, 0.22) * mm});
            skLineSegment(sketch, "E755", {"start": v(-0.38, 0.22) * mm, "end": v(-0.38, 0.23) * mm});
            skLineSegment(sketch, "E756", {"start": v(-0.38, 0.23) * mm, "end": v(-0.37, 0.24) * mm});
            skLineSegment(sketch, "E757", {"start": v(-0.37, 0.24) * mm, "end": v(-0.37, 0.25) * mm});
            skLineSegment(sketch, "E758", {"start": v(-0.37, 0.25) * mm, "end": v(-0.37, 0.25) * mm});
            skLineSegment(sketch, "E759", {"start": v(-0.37, 0.25) * mm, "end": v(-0.38, 0.26) * mm});
            skLineSegment(sketch, "E760", {"start": v(-0.38, 0.26) * mm, "end": v(-0.38, 0.26) * mm});
            skLineSegment(sketch, "E761", {"start": v(-0.38, 0.26) * mm, "end": v(-0.4, 0.27) * mm});
            skLineSegment(sketch, "E762", {"start": v(-0.4, 0.27) * mm, "end": v(-0.4, 0.27) * mm});
            skLineSegment(sketch, "E763", {"start": v(-0.4, 0.27) * mm, "end": v(-0.4, 0.28) * mm});
            skLineSegment(sketch, "E764", {"start": v(-0.4, 0.28) * mm, "end": v(-0.41, 0.29) * mm});
            skLineSegment(sketch, "E765", {"start": v(-0.41, 0.29) * mm, "end": v(-0.42, 0.3) * mm});
            skLineSegment(sketch, "E766", {"start": v(-0.42, 0.3) * mm, "end": v(-0.42, 0.3) * mm});
            skLineSegment(sketch, "E767", {"start": v(-0.42, 0.3) * mm, "end": v(-0.43, 0.3) * mm});
            skLineSegment(sketch, "E768", {"start": v(-0.43, 0.3) * mm, "end": v(-0.43, 0.3) * mm});
            skLineSegment(sketch, "E769", {"start": v(-0.43, 0.3) * mm, "end": v(-0.44, 0.32) * mm});
            skLineSegment(sketch, "E770", {"start": v(-0.44, 0.32) * mm, "end": v(-0.45, 0.32) * mm});
            skLineSegment(sketch, "E771", {"start": v(-0.45, 0.32) * mm, "end": v(-0.46, 0.33) * mm});
            skLineSegment(sketch, "E772", {"start": v(-0.46, 0.33) * mm, "end": v(-0.46, 0.33) * mm});
            skLineSegment(sketch, "E773", {"start": v(-0.46, 0.33) * mm, "end": v(-0.46, 0.34) * mm});
            skLineSegment(sketch, "E774", {"start": v(-0.46, 0.34) * mm, "end": v(-0.48, 0.35) * mm});
            skLineSegment(sketch, "E775", {"start": v(-0.48, 0.35) * mm, "end": v(-0.5, 0.35) * mm});
            skLineSegment(sketch, "E776", {"start": v(-0.5, 0.35) * mm, "end": v(-0.5, 0.34) * mm});
            skLineSegment(sketch, "E777", {"start": v(-0.5, 0.34) * mm, "end": v(-0.52, 0.33) * mm});
            skLineSegment(sketch, "E778", {"start": v(-0.52, 0.33) * mm, "end": v(-0.53, 0.33) * mm});
            skLineSegment(sketch, "E779", {"start": v(-0.53, 0.33) * mm, "end": v(-0.54, 0.33) * mm});
            skLineSegment(sketch, "E780", {"start": v(-0.54, 0.33) * mm, "end": v(-0.54, 0.34) * mm});
            skLineSegment(sketch, "E781", {"start": v(-0.54, 0.34) * mm, "end": v(-0.54, 0.35) * mm});
            skLineSegment(sketch, "E782", {"start": v(-0.54, 0.35) * mm, "end": v(-0.54, 0.35) * mm});
            skLineSegment(sketch, "E783", {"start": v(-0.54, 0.35) * mm, "end": v(-0.54, 0.36) * mm});
            skLineSegment(sketch, "E784", {"start": v(-0.54, 0.36) * mm, "end": v(-0.53, 0.37) * mm});
            skLineSegment(sketch, "E785", {"start": v(-0.53, 0.37) * mm, "end": v(-0.52, 0.38) * mm});
            skLineSegment(sketch, "E786", {"start": v(-0.52, 0.38) * mm, "end": v(-0.51, 0.4) * mm});
            skLineSegment(sketch, "E787", {"start": v(-0.46, 0.4) * mm, "end": v(-0.46, 0.4) * mm});
            skLineSegment(sketch, "E788", {"start": v(-0.46, 0.4) * mm, "end": v(-0.46, 0.38) * mm});
            skLineSegment(sketch, "E789", {"start": v(-0.46, 0.38) * mm, "end": v(-0.46, 0.37) * mm});
            skLineSegment(sketch, "E790", {"start": v(-0.46, 0.37) * mm, "end": v(-0.45, 0.37) * mm});
            skLineSegment(sketch, "E791", {"start": v(-0.45, 0.37) * mm, "end": v(-0.44, 0.36) * mm});
            skLineSegment(sketch, "E792", {"start": v(-0.44, 0.36) * mm, "end": v(-0.44, 0.36) * mm});
            skLineSegment(sketch, "E793", {"start": v(-0.44, 0.36) * mm, "end": v(-0.43, 0.35) * mm});
            skLineSegment(sketch, "E794", {"start": v(-0.43, 0.35) * mm, "end": v(-0.42, 0.35) * mm});
            skLineSegment(sketch, "E795", {"start": v(-0.42, 0.35) * mm, "end": v(-0.41, 0.35) * mm});
            skLineSegment(sketch, "E796", {"start": v(-0.41, 0.35) * mm, "end": v(-0.4, 0.35) * mm});
            skLineSegment(sketch, "E797", {"start": v(-0.4, 0.35) * mm, "end": v(-0.4, 0.35) * mm});
            skLineSegment(sketch, "E798", {"start": v(-0.4, 0.35) * mm, "end": v(-0.4, 0.36) * mm});
            skLineSegment(sketch, "E799", {"start": v(-0.4, 0.36) * mm, "end": v(-0.4, 0.37) * mm});
            skLineSegment(sketch, "E800", {"start": v(-0.4, 0.37) * mm, "end": v(-0.4, 0.38) * mm});
            skLineSegment(sketch, "E801", {"start": v(-0.4, 0.38) * mm, "end": v(-0.4, 0.39) * mm});
            skLineSegment(sketch, "E802", {"start": v(-0.4, 0.39) * mm, "end": v(-0.4, 0.4) * mm});
            skLineSegment(sketch, "E803", {"start": v(-0.4, 0.4) * mm, "end": v(-0.42, 0.4) * mm});
            skLineSegment(sketch, "E804", {"start": v(-0.42, 0.4) * mm, "end": v(-0.43, 0.4) * mm});
            skLineSegment(sketch, "E805", {"start": v(-0.43, 0.4) * mm, "end": v(-0.44, 0.4) * mm});
            skLineSegment(sketch, "E806", {"start": v(-0.44, 0.4) * mm, "end": v(-0.45, 0.4) * mm});
            skLineSegment(sketch, "E807", {"start": v(-0.45, 0.4) * mm, "end": v(-0.46, 0.4) * mm});
            skLineSegment(sketch, "E808", {"start": v(-0.39, 0.34) * mm, "end": v(-0.39, 0.33) * mm});
            skLineSegment(sketch, "E809", {"start": v(-0.39, 0.33) * mm, "end": v(-0.38, 0.32) * mm});
            skLineSegment(sketch, "E810", {"start": v(-0.38, 0.32) * mm, "end": v(-0.38, 0.3) * mm});
            skLineSegment(sketch, "E811", {"start": v(-0.38, 0.3) * mm, "end": v(-0.37, 0.3) * mm});
            skLineSegment(sketch, "E812", {"start": v(-0.37, 0.3) * mm, "end": v(-0.36, 0.3) * mm});
            skLineSegment(sketch, "E813", {"start": v(-0.36, 0.3) * mm, "end": v(-0.35, 0.29) * mm});
            skLineSegment(sketch, "E814", {"start": v(-0.35, 0.29) * mm, "end": v(-0.35, 0.29) * mm});
            skLineSegment(sketch, "E815", {"start": v(-0.35, 0.29) * mm, "end": v(-0.34, 0.28) * mm});
            skLineSegment(sketch, "E816", {"start": v(-0.34, 0.28) * mm, "end": v(-0.34, 0.29) * mm});
            skLineSegment(sketch, "E817", {"start": v(-0.34, 0.29) * mm, "end": v(-0.33, 0.29) * mm});
            skLineSegment(sketch, "E818", {"start": v(-0.33, 0.29) * mm, "end": v(-0.33, 0.3) * mm});
            skLineSegment(sketch, "E819", {"start": v(-0.33, 0.3) * mm, "end": v(-0.33, 0.3) * mm});
            skLineSegment(sketch, "E820", {"start": v(-0.33, 0.3) * mm, "end": v(-0.32, 0.31) * mm});
            skLineSegment(sketch, "E821", {"start": v(-0.32, 0.31) * mm, "end": v(-0.32, 0.33) * mm});
            skLineSegment(sketch, "E822", {"start": v(-0.32, 0.33) * mm, "end": v(-0.32, 0.34) * mm});
            skLineSegment(sketch, "E823", {"start": v(-0.32, 0.34) * mm, "end": v(-0.33, 0.35) * mm});
            skLineSegment(sketch, "E824", {"start": v(-0.33, 0.35) * mm, "end": v(-0.34, 0.35) * mm});
            skLineSegment(sketch, "E825", {"start": v(-0.34, 0.35) * mm, "end": v(-0.34, 0.36) * mm});
            skLineSegment(sketch, "E826", {"start": v(-0.34, 0.36) * mm, "end": v(-0.34, 0.36) * mm});
            skLineSegment(sketch, "E827", {"start": v(-0.34, 0.36) * mm, "end": v(-0.35, 0.36) * mm});
            skLineSegment(sketch, "E828", {"start": v(-0.35, 0.36) * mm, "end": v(-0.36, 0.36) * mm});
            skLineSegment(sketch, "E829", {"start": v(-0.36, 0.36) * mm, "end": v(-0.37, 0.36) * mm});
            skLineSegment(sketch, "E830", {"start": v(-0.37, 0.36) * mm, "end": v(-0.37, 0.35) * mm});
            skLineSegment(sketch, "E831", {"start": v(-0.37, 0.35) * mm, "end": v(-0.38, 0.34) * mm});
            skLineSegment(sketch, "E832", {"start": v(-0.38, 0.34) * mm, "end": v(-0.38, 0.34) * mm});
            skLineSegment(sketch, "E833", {"start": v(-0.38, 0.34) * mm, "end": v(-0.39, 0.34) * mm});
            skLineSegment(sketch, "E834", {"start": v(-0.3, 0.59) * mm, "end": v(-0.3, 0.6) * mm});
            skLineSegment(sketch, "E835", {"start": v(-0.3, 0.6) * mm, "end": v(-0.29, 0.6) * mm});
            skLineSegment(sketch, "E836", {"start": v(-0.29, 0.6) * mm, "end": v(-0.28, 0.6) * mm});
            skLineSegment(sketch, "E837", {"start": v(-0.28, 0.6) * mm, "end": v(-0.28, 0.6) * mm});
            skLineSegment(sketch, "E838", {"start": v(-0.28, 0.6) * mm, "end": v(-0.27, 0.6) * mm});
            skLineSegment(sketch, "E839", {"start": v(-0.27, 0.6) * mm, "end": v(-0.27, 0.6) * mm});
            skLineSegment(sketch, "E840", {"start": v(-0.27, 0.6) * mm, "end": v(-0.26, 0.6) * mm});
            skLineSegment(sketch, "E841", {"start": v(-0.26, 0.6) * mm, "end": v(-0.26, 0.59) * mm});
            skLineSegment(sketch, "E842", {"start": v(-0.26, 0.59) * mm, "end": v(-0.26, 0.58) * mm});
            skLineSegment(sketch, "E843", {"start": v(-0.26, 0.58) * mm, "end": v(-0.27, 0.58) * mm});
            skLineSegment(sketch, "E844", {"start": v(-0.27, 0.58) * mm, "end": v(-0.28, 0.57) * mm});
            skLineSegment(sketch, "E845", {"start": v(-0.28, 0.57) * mm, "end": v(-0.28, 0.56) * mm});
            skLineSegment(sketch, "E846", {"start": v(-0.28, 0.56) * mm, "end": v(-0.26, 0.54) * mm});
            skLineSegment(sketch, "E847", {"start": v(-0.26, 0.54) * mm, "end": v(-0.26, 0.53) * mm});
            skLineSegment(sketch, "E848", {"start": v(-0.26, 0.53) * mm, "end": v(-0.25, 0.53) * mm});
            skLineSegment(sketch, "E849", {"start": v(-0.25, 0.53) * mm, "end": v(-0.25, 0.53) * mm});
            skLineSegment(sketch, "E850", {"start": v(-0.25, 0.53) * mm, "end": v(-0.25, 0.5) * mm});
            skLineSegment(sketch, "E851", {"start": v(-0.25, 0.5) * mm, "end": v(-0.24, 0.5) * mm});
            skLineSegment(sketch, "E852", {"start": v(-0.24, 0.5) * mm, "end": v(-0.24, 0.5) * mm});
            skLineSegment(sketch, "E853", {"start": v(-0.24, 0.5) * mm, "end": v(-0.23, 0.5) * mm});
            skLineSegment(sketch, "E854", {"start": v(-0.23, 0.5) * mm, "end": v(-0.23, 0.49) * mm});
            skLineSegment(sketch, "E855", {"start": v(-0.23, 0.49) * mm, "end": v(-0.22, 0.47) * mm});
            skLineSegment(sketch, "E856", {"start": v(-0.22, 0.47) * mm, "end": v(-0.2, 0.46) * mm});
            skLineSegment(sketch, "E857", {"start": v(-0.2, 0.46) * mm, "end": v(-0.2, 0.45) * mm});
            skLineSegment(sketch, "E858", {"start": v(-0.2, 0.45) * mm, "end": v(-0.2, 0.44) * mm});
            skLineSegment(sketch, "E859", {"start": v(-0.2, 0.44) * mm, "end": v(-0.2, 0.43) * mm});
            skLineSegment(sketch, "E860", {"start": v(-0.2, 0.43) * mm, "end": v(-0.2, 0.42) * mm});
            skLineSegment(sketch, "E861", {"start": v(-0.2, 0.42) * mm, "end": v(-0.2, 0.42) * mm});
            skLineSegment(sketch, "E862", {"start": v(-0.2, 0.42) * mm, "end": v(-0.19, 0.42) * mm});
            skLineSegment(sketch, "E863", {"start": v(-0.19, 0.42) * mm, "end": v(-0.18, 0.42) * mm});
            skLineSegment(sketch, "E864", {"start": v(-0.18, 0.42) * mm, "end": v(-0.18, 0.42) * mm});
            skLineSegment(sketch, "E865", {"start": v(-0.18, 0.42) * mm, "end": v(-0.17, 0.42) * mm});
            skLineSegment(sketch, "E866", {"start": v(-0.17, 0.42) * mm, "end": v(-0.15, 0.41) * mm});
            skLineSegment(sketch, "E867", {"start": v(-0.15, 0.41) * mm, "end": v(-0.15, 0.4) * mm});
            skLineSegment(sketch, "E868", {"start": v(-0.15, 0.4) * mm, "end": v(-0.16, 0.4) * mm});
            skLineSegment(sketch, "E869", {"start": v(-0.16, 0.4) * mm, "end": v(-0.17, 0.39) * mm});
            skLineSegment(sketch, "E870", {"start": v(-0.17, 0.39) * mm, "end": v(-0.18, 0.38) * mm});
            skLineSegment(sketch, "E871", {"start": v(-0.18, 0.38) * mm, "end": v(-0.18, 0.38) * mm});
            skLineSegment(sketch, "E872", {"start": v(-0.18, 0.38) * mm, "end": v(-0.2, 0.38) * mm});
            skLineSegment(sketch, "E873", {"start": v(-0.2, 0.38) * mm, "end": v(-0.2, 0.37) * mm});
            skLineSegment(sketch, "E874", {"start": v(-0.2, 0.37) * mm, "end": v(-0.2, 0.36) * mm});
            skLineSegment(sketch, "E875", {"start": v(-0.2, 0.36) * mm, "end": v(-0.22, 0.36) * mm});
            skLineSegment(sketch, "E876", {"start": v(-0.22, 0.36) * mm, "end": v(-0.22, 0.35) * mm});
            skLineSegment(sketch, "E877", {"start": v(-0.22, 0.35) * mm, "end": v(-0.23, 0.35) * mm});
            skLineSegment(sketch, "E878", {"start": v(-0.23, 0.35) * mm, "end": v(-0.23, 0.35) * mm});
            skLineSegment(sketch, "E879", {"start": v(-0.23, 0.35) * mm, "end": v(-0.23, 0.36) * mm});
            skLineSegment(sketch, "E880", {"start": v(-0.23, 0.36) * mm, "end": v(-0.23, 0.38) * mm});
            skLineSegment(sketch, "E881", {"start": v(-0.23, 0.38) * mm, "end": v(-0.22, 0.39) * mm});
            skLineSegment(sketch, "E882", {"start": v(-0.22, 0.39) * mm, "end": v(-0.23, 0.4) * mm});
            skLineSegment(sketch, "E883", {"start": v(-0.23, 0.4) * mm, "end": v(-0.23, 0.4) * mm});
            skLineSegment(sketch, "E884", {"start": v(-0.23, 0.4) * mm, "end": v(-0.24, 0.41) * mm});
            skLineSegment(sketch, "E885", {"start": v(-0.24, 0.41) * mm, "end": v(-0.24, 0.42) * mm});
            skLineSegment(sketch, "E886", {"start": v(-0.24, 0.42) * mm, "end": v(-0.26, 0.44) * mm});
            skLineSegment(sketch, "E887", {"start": v(-0.26, 0.44) * mm, "end": v(-0.29, 0.5) * mm});
            skLineSegment(sketch, "E888", {"start": v(-0.29, 0.5) * mm, "end": v(-0.3, 0.5) * mm});
            skLineSegment(sketch, "E889", {"start": v(-0.3, 0.5) * mm, "end": v(-0.3, 0.51) * mm});
            skLineSegment(sketch, "E890", {"start": v(-0.3, 0.51) * mm, "end": v(-0.3, 0.52) * mm});
            skLineSegment(sketch, "E891", {"start": v(-0.3, 0.52) * mm, "end": v(-0.3, 0.52) * mm});
            skLineSegment(sketch, "E892", {"start": v(-0.3, 0.52) * mm, "end": v(-0.31, 0.53) * mm});
            skLineSegment(sketch, "E893", {"start": v(-0.31, 0.53) * mm, "end": v(-0.32, 0.54) * mm});
            skLineSegment(sketch, "E894", {"start": v(-0.32, 0.54) * mm, "end": v(-0.32, 0.54) * mm});
            skLineSegment(sketch, "E895", {"start": v(-0.32, 0.54) * mm, "end": v(-0.33, 0.54) * mm});
            skLineSegment(sketch, "E896", {"start": v(-0.33, 0.54) * mm, "end": v(-0.33, 0.53) * mm});
            skLineSegment(sketch, "E897", {"start": v(-0.33, 0.53) * mm, "end": v(-0.34, 0.53) * mm});
            skLineSegment(sketch, "E898", {"start": v(-0.34, 0.53) * mm, "end": v(-0.35, 0.53) * mm});
            skLineSegment(sketch, "E899", {"start": v(-0.35, 0.53) * mm, "end": v(-0.35, 0.54) * mm});
            skLineSegment(sketch, "E900", {"start": v(-0.35, 0.54) * mm, "end": v(-0.35, 0.55) * mm});
            skLineSegment(sketch, "E901", {"start": v(-0.35, 0.55) * mm, "end": v(-0.35, 0.55) * mm});
            skLineSegment(sketch, "E902", {"start": v(-0.35, 0.55) * mm, "end": v(-0.35, 0.56) * mm});
            skLineSegment(sketch, "E903", {"start": v(-0.35, 0.56) * mm, "end": v(-0.33, 0.56) * mm});
            skLineSegment(sketch, "E904", {"start": v(-0.33, 0.56) * mm, "end": v(-0.33, 0.57) * mm});
            skLineSegment(sketch, "E905", {"start": v(-0.33, 0.57) * mm, "end": v(-0.33, 0.57) * mm});
            skLineSegment(sketch, "E906", {"start": v(-0.33, 0.57) * mm, "end": v(-0.32, 0.57) * mm});
            skLineSegment(sketch, "E907", {"start": v(-0.32, 0.57) * mm, "end": v(-0.32, 0.57) * mm});
            skLineSegment(sketch, "E908", {"start": v(-0.32, 0.57) * mm, "end": v(-0.31, 0.58) * mm});
            skLineSegment(sketch, "E909", {"start": v(-0.31, 0.58) * mm, "end": v(-0.3, 0.58) * mm});
            skLineSegment(sketch, "E910", {"start": v(-0.3, 0.58) * mm, "end": v(-0.3, 0.58) * mm});
            skLineSegment(sketch, "E911", {"start": v(-0.3, 0.58) * mm, "end": v(-0.3, 0.59) * mm});
            skLineSegment(sketch, "E912", {"start": v(-0.3, 0.59) * mm, "end": v(-0.3, 0.59) * mm});
            skLineSegment(sketch, "E913", {"start": v(-0.02, 0.68) * mm, "end": v(-0.01, 0.68) * mm});
            skLineSegment(sketch, "E914", {"start": v(-0.01, 0.68) * mm, "end": v(0, 0.68) * mm});
            skLineSegment(sketch, "E915", {"start": v(0, 0.68) * mm, "end": v(0.02, 0.67) * mm});
            skLineSegment(sketch, "E916", {"start": v(0.02, 0.67) * mm, "end": v(0.03, 0.66) * mm});
            skLineSegment(sketch, "E917", {"start": v(0.03, 0.66) * mm, "end": v(0.04, 0.64) * mm});
            skLineSegment(sketch, "E918", {"start": v(0.04, 0.64) * mm, "end": v(0.04, 0.63) * mm});
            skLineSegment(sketch, "E919", {"start": v(0.04, 0.63) * mm, "end": v(0.04, 0.63) * mm});
            skLineSegment(sketch, "E920", {"start": v(0.04, 0.63) * mm, "end": v(0.04, 0.62) * mm});
            skLineSegment(sketch, "E921", {"start": v(0.04, 0.62) * mm, "end": v(0.05, 0.62) * mm});
            skLineSegment(sketch, "E922", {"start": v(0.05, 0.62) * mm, "end": v(0.05, 0.62) * mm});
            skLineSegment(sketch, "E923", {"start": v(0.05, 0.62) * mm, "end": v(0.04, 0.61) * mm});
            skLineSegment(sketch, "E924", {"start": v(0.04, 0.61) * mm, "end": v(0.04, 0.6) * mm});
            skLineSegment(sketch, "E925", {"start": v(0.04, 0.6) * mm, "end": v(0.04, 0.6) * mm});
            skLineSegment(sketch, "E926", {"start": v(0.04, 0.6) * mm, "end": v(0.03, 0.6) * mm});
            skLineSegment(sketch, "E927", {"start": v(0.03, 0.6) * mm, "end": v(0.02, 0.62) * mm});
            skLineSegment(sketch, "E928", {"start": v(0.02, 0.62) * mm, "end": v(0, 0.63) * mm});
            skLineSegment(sketch, "E929", {"start": v(0, 0.63) * mm, "end": v(0, 0.63) * mm});
            skLineSegment(sketch, "E930", {"start": v(0, 0.63) * mm, "end": v(-0.02, 0.64) * mm});
            skLineSegment(sketch, "E931", {"start": v(-0.02, 0.64) * mm, "end": v(-0.04, 0.64) * mm});
            skLineSegment(sketch, "E932", {"start": v(-0.04, 0.64) * mm, "end": v(-0.06, 0.63) * mm});
            skLineSegment(sketch, "E933", {"start": v(-0.06, 0.63) * mm, "end": v(-0.09, 0.61) * mm});
            skLineSegment(sketch, "E934", {"start": v(-0.09, 0.61) * mm, "end": v(-0.1, 0.59) * mm});
            skLineSegment(sketch, "E935", {"start": v(-0.1, 0.59) * mm, "end": v(-0.1, 0.56) * mm});
            skLineSegment(sketch, "E936", {"start": v(-0.1, 0.56) * mm, "end": v(-0.1, 0.54) * mm});
            skLineSegment(sketch, "E937", {"start": v(-0.1, 0.54) * mm, "end": v(-0.1, 0.53) * mm});
            skLineSegment(sketch, "E938", {"start": v(-0.1, 0.53) * mm, "end": v(-0.1, 0.52) * mm});
            skLineSegment(sketch, "E939", {"start": v(-0.1, 0.52) * mm, "end": v(-0.1, 0.51) * mm});
            skLineSegment(sketch, "E940", {"start": v(-0.1, 0.51) * mm, "end": v(-0.09, 0.5) * mm});
            skLineSegment(sketch, "E941", {"start": v(-0.09, 0.5) * mm, "end": v(-0.07, 0.48) * mm});
            skLineSegment(sketch, "E942", {"start": v(-0.07, 0.48) * mm, "end": v(-0.05, 0.47) * mm});
            skLineSegment(sketch, "E943", {"start": v(-0.05, 0.47) * mm, "end": v(-0.03, 0.46) * mm});
            skLineSegment(sketch, "E944", {"start": v(-0.03, 0.46) * mm, "end": v(-0.02, 0.47) * mm});
            skLineSegment(sketch, "E945", {"start": v(-0.02, 0.47) * mm, "end": v(0, 0.48) * mm});
            skLineSegment(sketch, "E946", {"start": v(0, 0.48) * mm, "end": v(0, 0.5) * mm});
            skLineSegment(sketch, "E947", {"start": v(0, 0.5) * mm, "end": v(0, 0.5) * mm});
            skLineSegment(sketch, "E948", {"start": v(0, 0.5) * mm, "end": v(-0.01, 0.52) * mm});
            skLineSegment(sketch, "E949", {"start": v(-0.01, 0.52) * mm, "end": v(-0.02, 0.53) * mm});
            skLineSegment(sketch, "E950", {"start": v(-0.02, 0.53) * mm, "end": v(-0.03, 0.54) * mm});
            skLineSegment(sketch, "E951", {"start": v(-0.03, 0.54) * mm, "end": v(-0.04, 0.54) * mm});
            skLineSegment(sketch, "E952", {"start": v(-0.04, 0.54) * mm, "end": v(-0.04, 0.54) * mm});
            skLineSegment(sketch, "E953", {"start": v(-0.04, 0.54) * mm, "end": v(-0.03, 0.55) * mm});
            skLineSegment(sketch, "E954", {"start": v(-0.03, 0.55) * mm, "end": v(-0.02, 0.55) * mm});
            skLineSegment(sketch, "E955", {"start": v(-0.02, 0.55) * mm, "end": v(0, 0.55) * mm});
            skLineSegment(sketch, "E956", {"start": v(0, 0.55) * mm, "end": v(0.01, 0.55) * mm});
            skLineSegment(sketch, "E957", {"start": v(0.01, 0.55) * mm, "end": v(0.02, 0.56) * mm});
            skLineSegment(sketch, "E958", {"start": v(0.02, 0.56) * mm, "end": v(0.03, 0.56) * mm});
            skLineSegment(sketch, "E959", {"start": v(0.03, 0.56) * mm, "end": v(0.03, 0.56) * mm});
            skLineSegment(sketch, "E960", {"start": v(0.03, 0.56) * mm, "end": v(0.04, 0.56) * mm});
            skLineSegment(sketch, "E961", {"start": v(0.04, 0.56) * mm, "end": v(0.05, 0.56) * mm});
            skLineSegment(sketch, "E962", {"start": v(0.05, 0.56) * mm, "end": v(0.05, 0.56) * mm});
            skLineSegment(sketch, "E963", {"start": v(0.05, 0.56) * mm, "end": v(0.06, 0.56) * mm});
            skLineSegment(sketch, "E964", {"start": v(0.06, 0.56) * mm, "end": v(0.05, 0.55) * mm});
            skLineSegment(sketch, "E965", {"start": v(0.05, 0.55) * mm, "end": v(0.05, 0.54) * mm});
            skLineSegment(sketch, "E966", {"start": v(0.05, 0.54) * mm, "end": v(0.05, 0.54) * mm});
            skLineSegment(sketch, "E967", {"start": v(0.05, 0.54) * mm, "end": v(0.03, 0.53) * mm});
            skLineSegment(sketch, "E968", {"start": v(0.03, 0.53) * mm, "end": v(0.03, 0.52) * mm});
            skLineSegment(sketch, "E969", {"start": v(0.03, 0.52) * mm, "end": v(0.03, 0.5) * mm});
            skLineSegment(sketch, "E970", {"start": v(0.03, 0.5) * mm, "end": v(0.03, 0.5) * mm});
            skLineSegment(sketch, "E971", {"start": v(0.03, 0.5) * mm, "end": v(0.03, 0.49) * mm});
            skLineSegment(sketch, "E972", {"start": v(0.03, 0.49) * mm, "end": v(0.03, 0.48) * mm});
            skLineSegment(sketch, "E973", {"start": v(0.03, 0.48) * mm, "end": v(0.04, 0.47) * mm});
            skLineSegment(sketch, "E974", {"start": v(0.04, 0.47) * mm, "end": v(0.04, 0.46) * mm});
            skLineSegment(sketch, "E975", {"start": v(0.04, 0.46) * mm, "end": v(0.04, 0.46) * mm});
            skLineSegment(sketch, "E976", {"start": v(0.04, 0.46) * mm, "end": v(0.04, 0.45) * mm});
            skLineSegment(sketch, "E977", {"start": v(0.04, 0.45) * mm, "end": v(0.03, 0.45) * mm});
            skLineSegment(sketch, "E978", {"start": v(0.03, 0.45) * mm, "end": v(0.03, 0.44) * mm});
            skLineSegment(sketch, "E979", {"start": v(0.03, 0.44) * mm, "end": v(0, 0.44) * mm});
            skLineSegment(sketch, "E980", {"start": v(0, 0.44) * mm, "end": v(0, 0.43) * mm});
            skLineSegment(sketch, "E981", {"start": v(0, 0.43) * mm, "end": v(-0.01, 0.43) * mm});
            skLineSegment(sketch, "E982", {"start": v(-0.01, 0.43) * mm, "end": v(-0.02, 0.44) * mm});
            skLineSegment(sketch, "E983", {"start": v(-0.02, 0.44) * mm, "end": v(-0.03, 0.44) * mm});
            skLineSegment(sketch, "E984", {"start": v(-0.03, 0.44) * mm, "end": v(-0.04, 0.43) * mm});
            skLineSegment(sketch, "E985", {"start": v(-0.04, 0.43) * mm, "end": v(-0.05, 0.43) * mm});
            skLineSegment(sketch, "E986", {"start": v(-0.05, 0.43) * mm, "end": v(-0.05, 0.43) * mm});
            skLineSegment(sketch, "E987", {"start": v(-0.05, 0.43) * mm, "end": v(-0.06, 0.43) * mm});
            skLineSegment(sketch, "E988", {"start": v(-0.06, 0.43) * mm, "end": v(-0.07, 0.44) * mm});
            skLineSegment(sketch, "E989", {"start": v(-0.07, 0.44) * mm, "end": v(-0.08, 0.43) * mm});
            skLineSegment(sketch, "E990", {"start": v(-0.08, 0.43) * mm, "end": v(-0.09, 0.44) * mm});
            skLineSegment(sketch, "E991", {"start": v(-0.09, 0.44) * mm, "end": v(-0.1, 0.44) * mm});
            skLineSegment(sketch, "E992", {"start": v(-0.1, 0.44) * mm, "end": v(-0.1, 0.44) * mm});
            skLineSegment(sketch, "E993", {"start": v(-0.1, 0.44) * mm, "end": v(-0.11, 0.45) * mm});
            skLineSegment(sketch, "E994", {"start": v(-0.11, 0.45) * mm, "end": v(-0.13, 0.47) * mm});
            skLineSegment(sketch, "E995", {"start": v(-0.13, 0.47) * mm, "end": v(-0.14, 0.48) * mm});
            skLineSegment(sketch, "E996", {"start": v(-0.14, 0.48) * mm, "end": v(-0.14, 0.5) * mm});
            skLineSegment(sketch, "E997", {"start": v(-0.14, 0.5) * mm, "end": v(-0.15, 0.5) * mm});
            skLineSegment(sketch, "E998", {"start": v(-0.15, 0.5) * mm, "end": v(-0.15, 0.51) * mm});
            skLineSegment(sketch, "E999", {"start": v(-0.15, 0.51) * mm, "end": v(-0.15, 0.52) * mm});
            skLineSegment(sketch, "E1000", {"start": v(-0.15, 0.52) * mm, "end": v(-0.16, 0.54) * mm});
            skLineSegment(sketch, "E1001", {"start": v(-0.16, 0.54) * mm, "end": v(-0.16, 0.55) * mm});
            skLineSegment(sketch, "E1002", {"start": v(-0.16, 0.55) * mm, "end": v(-0.15, 0.56) * mm});
            skLineSegment(sketch, "E1003", {"start": v(-0.15, 0.56) * mm, "end": v(-0.15, 0.57) * mm});
            skLineSegment(sketch, "E1004", {"start": v(-0.15, 0.57) * mm, "end": v(-0.15, 0.58) * mm});
            skLineSegment(sketch, "E1005", {"start": v(-0.15, 0.58) * mm, "end": v(-0.15, 0.59) * mm});
            skLineSegment(sketch, "E1006", {"start": v(-0.15, 0.59) * mm, "end": v(-0.15, 0.6) * mm});
            skLineSegment(sketch, "E1007", {"start": v(-0.15, 0.6) * mm, "end": v(-0.13, 0.63) * mm});
            skLineSegment(sketch, "E1008", {"start": v(-0.13, 0.63) * mm, "end": v(-0.12, 0.65) * mm});
            skLineSegment(sketch, "E1009", {"start": v(-0.12, 0.65) * mm, "end": v(-0.1, 0.66) * mm});
            skLineSegment(sketch, "E1010", {"start": v(-0.1, 0.66) * mm, "end": v(-0.1, 0.66) * mm});
            skLineSegment(sketch, "E1011", {"start": v(-0.1, 0.66) * mm, "end": v(-0.09, 0.66) * mm});
            skLineSegment(sketch, "E1012", {"start": v(-0.09, 0.66) * mm, "end": v(-0.08, 0.66) * mm});
            skLineSegment(sketch, "E1013", {"start": v(-0.08, 0.66) * mm, "end": v(-0.08, 0.66) * mm});
            skLineSegment(sketch, "E1014", {"start": v(-0.08, 0.66) * mm, "end": v(-0.07, 0.66) * mm});
            skLineSegment(sketch, "E1015", {"start": v(-0.07, 0.66) * mm, "end": v(-0.07, 0.67) * mm});
            skLineSegment(sketch, "E1016", {"start": v(-0.07, 0.67) * mm, "end": v(-0.06, 0.67) * mm});
            skLineSegment(sketch, "E1017", {"start": v(-0.06, 0.67) * mm, "end": v(-0.05, 0.67) * mm});
            skLineSegment(sketch, "E1018", {"start": v(-0.05, 0.67) * mm, "end": v(-0.03, 0.67) * mm});
            skLineSegment(sketch, "E1019", {"start": v(-0.03, 0.67) * mm, "end": v(-0.02, 0.68) * mm});
            skLineSegment(sketch, "E1020", {"start": v(0.36, 0.59) * mm, "end": v(0.36, 0.58) * mm});
            skLineSegment(sketch, "E1021", {"start": v(0.36, 0.58) * mm, "end": v(0.37, 0.58) * mm});
            skLineSegment(sketch, "E1022", {"start": v(0.37, 0.58) * mm, "end": v(0.38, 0.57) * mm});
            skLineSegment(sketch, "E1023", {"start": v(0.38, 0.57) * mm, "end": v(0.39, 0.57) * mm});
            skLineSegment(sketch, "E1024", {"start": v(0.39, 0.57) * mm, "end": v(0.41, 0.55) * mm});
            skLineSegment(sketch, "E1025", {"start": v(0.41, 0.55) * mm, "end": v(0.43, 0.54) * mm});
            skLineSegment(sketch, "E1026", {"start": v(0.43, 0.54) * mm, "end": v(0.45, 0.54) * mm});
            skLineSegment(sketch, "E1027", {"start": v(0.45, 0.54) * mm, "end": v(0.46, 0.54) * mm});
            skLineSegment(sketch, "E1028", {"start": v(0.46, 0.54) * mm, "end": v(0.46, 0.54) * mm});
            skLineSegment(sketch, "E1029", {"start": v(0.46, 0.54) * mm, "end": v(0.47, 0.54) * mm});
            skLineSegment(sketch, "E1030", {"start": v(0.47, 0.54) * mm, "end": v(0.47, 0.53) * mm});
            skLineSegment(sketch, "E1031", {"start": v(0.47, 0.53) * mm, "end": v(0.47, 0.53) * mm});
            skLineSegment(sketch, "E1032", {"start": v(0.47, 0.53) * mm, "end": v(0.46, 0.52) * mm});
            skLineSegment(sketch, "E1033", {"start": v(0.46, 0.52) * mm, "end": v(0.45, 0.52) * mm});
            skLineSegment(sketch, "E1034", {"start": v(0.45, 0.52) * mm, "end": v(0.45, 0.51) * mm});
            skLineSegment(sketch, "E1035", {"start": v(0.45, 0.51) * mm, "end": v(0.44, 0.5) * mm});
            skLineSegment(sketch, "E1036", {"start": v(0.44, 0.5) * mm, "end": v(0.43, 0.5) * mm});
            skLineSegment(sketch, "E1037", {"start": v(0.43, 0.5) * mm, "end": v(0.43, 0.5) * mm});
            skLineSegment(sketch, "E1038", {"start": v(0.43, 0.5) * mm, "end": v(0.42, 0.49) * mm});
            skLineSegment(sketch, "E1039", {"start": v(0.42, 0.49) * mm, "end": v(0.41, 0.5) * mm});
            skLineSegment(sketch, "E1040", {"start": v(0.41, 0.5) * mm, "end": v(0.4, 0.5) * mm});
            skLineSegment(sketch, "E1041", {"start": v(0.4, 0.5) * mm, "end": v(0.4, 0.5) * mm});
            skLineSegment(sketch, "E1042", {"start": v(0.4, 0.5) * mm, "end": v(0.4, 0.51) * mm});
            skLineSegment(sketch, "E1043", {"start": v(0.4, 0.51) * mm, "end": v(0.39, 0.52) * mm});
            skLineSegment(sketch, "E1044", {"start": v(0.39, 0.52) * mm, "end": v(0.38, 0.52) * mm});
            skLineSegment(sketch, "E1045", {"start": v(0.38, 0.52) * mm, "end": v(0.38, 0.53) * mm});
            skLineSegment(sketch, "E1046", {"start": v(0.38, 0.53) * mm, "end": v(0.37, 0.53) * mm});
            skLineSegment(sketch, "E1047", {"start": v(0.37, 0.53) * mm, "end": v(0.36, 0.54) * mm});
            skLineSegment(sketch, "E1048", {"start": v(0.36, 0.54) * mm, "end": v(0.35, 0.54) * mm});
            skLineSegment(sketch, "E1049", {"start": v(0.35, 0.54) * mm, "end": v(0.35, 0.54) * mm});
            skLineSegment(sketch, "E1050", {"start": v(0.35, 0.54) * mm, "end": v(0.34, 0.53) * mm});
            skLineSegment(sketch, "E1051", {"start": v(0.34, 0.53) * mm, "end": v(0.34, 0.52) * mm});
            skLineSegment(sketch, "E1052", {"start": v(0.34, 0.52) * mm, "end": v(0.33, 0.52) * mm});
            skLineSegment(sketch, "E1053", {"start": v(0.33, 0.52) * mm, "end": v(0.33, 0.51) * mm});
            skLineSegment(sketch, "E1054", {"start": v(0.33, 0.51) * mm, "end": v(0.32, 0.5) * mm});
            skLineSegment(sketch, "E1055", {"start": v(0.32, 0.5) * mm, "end": v(0.33, 0.5) * mm});
            skLineSegment(sketch, "E1056", {"start": v(0.33, 0.5) * mm, "end": v(0.33, 0.5) * mm});
            skLineSegment(sketch, "E1057", {"start": v(0.33, 0.5) * mm, "end": v(0.34, 0.5) * mm});
            skLineSegment(sketch, "E1058", {"start": v(0.34, 0.5) * mm, "end": v(0.35, 0.5) * mm});
            skLineSegment(sketch, "E1059", {"start": v(0.35, 0.5) * mm, "end": v(0.37, 0.48) * mm});
            skLineSegment(sketch, "E1060", {"start": v(0.37, 0.48) * mm, "end": v(0.38, 0.47) * mm});
            skLineSegment(sketch, "E1061", {"start": v(0.38, 0.47) * mm, "end": v(0.4, 0.45) * mm});
            skLineSegment(sketch, "E1062", {"start": v(0.4, 0.45) * mm, "end": v(0.4, 0.43) * mm});
            skLineSegment(sketch, "E1063", {"start": v(0.4, 0.43) * mm, "end": v(0.4, 0.4) * mm});
            skLineSegment(sketch, "E1064", {"start": v(0.4, 0.4) * mm, "end": v(0.39, 0.4) * mm});
            skLineSegment(sketch, "E1065", {"start": v(0.39, 0.4) * mm, "end": v(0.38, 0.38) * mm});
            skLineSegment(sketch, "E1066", {"start": v(0.38, 0.38) * mm, "end": v(0.37, 0.37) * mm});
            skLineSegment(sketch, "E1067", {"start": v(0.37, 0.37) * mm, "end": v(0.36, 0.36) * mm});
            skLineSegment(sketch, "E1068", {"start": v(0.36, 0.36) * mm, "end": v(0.35, 0.36) * mm});
            skLineSegment(sketch, "E1069", {"start": v(0.35, 0.36) * mm, "end": v(0.32, 0.35) * mm});
            skLineSegment(sketch, "E1070", {"start": v(0.32, 0.35) * mm, "end": v(0.3, 0.35) * mm});
            skLineSegment(sketch, "E1071", {"start": v(0.3, 0.35) * mm, "end": v(0.28, 0.36) * mm});
            skLineSegment(sketch, "E1072", {"start": v(0.28, 0.36) * mm, "end": v(0.26, 0.37) * mm});
            skLineSegment(sketch, "E1073", {"start": v(0.26, 0.37) * mm, "end": v(0.24, 0.38) * mm});
            skLineSegment(sketch, "E1074", {"start": v(0.24, 0.38) * mm, "end": v(0.22, 0.4) * mm});
            skLineSegment(sketch, "E1075", {"start": v(0.22, 0.4) * mm, "end": v(0.2, 0.41) * mm});
            skLineSegment(sketch, "E1076", {"start": v(0.2, 0.41) * mm, "end": v(0.2, 0.43) * mm});
            skLineSegment(sketch, "E1077", {"start": v(0.2, 0.43) * mm, "end": v(0.2, 0.44) * mm});
            skLineSegment(sketch, "E1078", {"start": v(0.2, 0.44) * mm, "end": v(0.2, 0.44) * mm});
            skLineSegment(sketch, "E1079", {"start": v(0.2, 0.44) * mm, "end": v(0.22, 0.45) * mm});
            skLineSegment(sketch, "E1080", {"start": v(0.22, 0.45) * mm, "end": v(0.23, 0.45) * mm});
            skLineSegment(sketch, "E1081", {"start": v(0.23, 0.45) * mm, "end": v(0.23, 0.45) * mm});
            skLineSegment(sketch, "E1082", {"start": v(0.23, 0.45) * mm, "end": v(0.24, 0.45) * mm});
            skLineSegment(sketch, "E1083", {"start": v(0.24, 0.45) * mm, "end": v(0.24, 0.45) * mm});
            skLineSegment(sketch, "E1084", {"start": v(0.24, 0.45) * mm, "end": v(0.24, 0.44) * mm});
            skLineSegment(sketch, "E1085", {"start": v(0.24, 0.44) * mm, "end": v(0.24, 0.43) * mm});
            skLineSegment(sketch, "E1086", {"start": v(0.24, 0.43) * mm, "end": v(0.25, 0.42) * mm});
            skLineSegment(sketch, "E1087", {"start": v(0.25, 0.42) * mm, "end": v(0.25, 0.42) * mm});
            skLineSegment(sketch, "E1088", {"start": v(0.25, 0.42) * mm, "end": v(0.25, 0.4) * mm});
            skLineSegment(sketch, "E1089", {"start": v(0.25, 0.4) * mm, "end": v(0.26, 0.4) * mm});
            skLineSegment(sketch, "E1090", {"start": v(0.26, 0.4) * mm, "end": v(0.26, 0.4) * mm});
            skLineSegment(sketch, "E1091", {"start": v(0.26, 0.4) * mm, "end": v(0.27, 0.39) * mm});
            skLineSegment(sketch, "E1092", {"start": v(0.27, 0.39) * mm, "end": v(0.28, 0.38) * mm});
            skLineSegment(sketch, "E1093", {"start": v(0.28, 0.38) * mm, "end": v(0.29, 0.38) * mm});
            skLineSegment(sketch, "E1094", {"start": v(0.29, 0.38) * mm, "end": v(0.3, 0.38) * mm});
            skLineSegment(sketch, "E1095", {"start": v(0.3, 0.38) * mm, "end": v(0.31, 0.39) * mm});
            skLineSegment(sketch, "E1096", {"start": v(0.31, 0.39) * mm, "end": v(0.33, 0.4) * mm});
            skLineSegment(sketch, "E1097", {"start": v(0.33, 0.4) * mm, "end": v(0.33, 0.4) * mm});
            skLineSegment(sketch, "E1098", {"start": v(0.33, 0.4) * mm, "end": v(0.34, 0.42) * mm});
            skLineSegment(sketch, "E1099", {"start": v(0.34, 0.42) * mm, "end": v(0.34, 0.43) * mm});
            skLineSegment(sketch, "E1100", {"start": v(0.34, 0.43) * mm, "end": v(0.34, 0.44) * mm});
            skLineSegment(sketch, "E1101", {"start": v(0.34, 0.44) * mm, "end": v(0.34, 0.45) * mm});
            skLineSegment(sketch, "E1102", {"start": v(0.34, 0.45) * mm, "end": v(0.34, 0.46) * mm});
            skLineSegment(sketch, "E1103", {"start": v(0.34, 0.46) * mm, "end": v(0.33, 0.47) * mm});
            skLineSegment(sketch, "E1104", {"start": v(0.33, 0.47) * mm, "end": v(0.33, 0.47) * mm});
            skLineSegment(sketch, "E1105", {"start": v(0.33, 0.47) * mm, "end": v(0.32, 0.48) * mm});
            skLineSegment(sketch, "E1106", {"start": v(0.32, 0.48) * mm, "end": v(0.3, 0.48) * mm});
            skLineSegment(sketch, "E1107", {"start": v(0.3, 0.48) * mm, "end": v(0.3, 0.49) * mm});
            skLineSegment(sketch, "E1108", {"start": v(0.3, 0.49) * mm, "end": v(0.28, 0.49) * mm});
            skLineSegment(sketch, "E1109", {"start": v(0.28, 0.49) * mm, "end": v(0.28, 0.5) * mm});
            skLineSegment(sketch, "E1110", {"start": v(0.28, 0.5) * mm, "end": v(0.28, 0.5) * mm});
            skLineSegment(sketch, "E1111", {"start": v(0.28, 0.5) * mm, "end": v(0.3, 0.51) * mm});
            skLineSegment(sketch, "E1112", {"start": v(0.3, 0.51) * mm, "end": v(0.3, 0.52) * mm});
            skLineSegment(sketch, "E1113", {"start": v(0.3, 0.52) * mm, "end": v(0.3, 0.53) * mm});
            skLineSegment(sketch, "E1114", {"start": v(0.3, 0.53) * mm, "end": v(0.31, 0.54) * mm});
            skLineSegment(sketch, "E1115", {"start": v(0.31, 0.54) * mm, "end": v(0.32, 0.55) * mm});
            skLineSegment(sketch, "E1116", {"start": v(0.32, 0.55) * mm, "end": v(0.33, 0.56) * mm});
            skLineSegment(sketch, "E1117", {"start": v(0.33, 0.56) * mm, "end": v(0.34, 0.58) * mm});
            skLineSegment(sketch, "E1118", {"start": v(0.34, 0.58) * mm, "end": v(0.34, 0.59) * mm});
            skLineSegment(sketch, "E1119", {"start": v(0.34, 0.59) * mm, "end": v(0.35, 0.6) * mm});
            skLineSegment(sketch, "E1120", {"start": v(0.35, 0.6) * mm, "end": v(0.36, 0.59) * mm});
            skLineSegment(sketch, "E1121", {"start": v(0.57, 0.22) * mm, "end": v(0.57, 0.22) * mm});
            skLineSegment(sketch, "E1122", {"start": v(0.57, 0.22) * mm, "end": v(0.57, 0.2) * mm});
            skLineSegment(sketch, "E1123", {"start": v(0.57, 0.2) * mm, "end": v(0.56, 0.18) * mm});
            skLineSegment(sketch, "E1124", {"start": v(0.56, 0.18) * mm, "end": v(0.55, 0.17) * mm});
            skLineSegment(sketch, "E1125", {"start": v(0.55, 0.17) * mm, "end": v(0.53, 0.17) * mm});
            skLineSegment(sketch, "E1126", {"start": v(0.53, 0.17) * mm, "end": v(0.52, 0.17) * mm});
            skLineSegment(sketch, "E1127", {"start": v(0.52, 0.17) * mm, "end": v(0.5, 0.18) * mm});
            skLineSegment(sketch, "E1128", {"start": v(0.5, 0.18) * mm, "end": v(0.5, 0.2) * mm});
            skLineSegment(sketch, "E1129", {"start": v(0.5, 0.2) * mm, "end": v(0.5, 0.2) * mm});
            skLineSegment(sketch, "E1130", {"start": v(0.5, 0.2) * mm, "end": v(0.5, 0.22) * mm});
            skLineSegment(sketch, "E1131", {"start": v(0.5, 0.22) * mm, "end": v(0.51, 0.23) * mm});
            skLineSegment(sketch, "E1132", {"start": v(0.51, 0.23) * mm, "end": v(0.52, 0.24) * mm});
            skLineSegment(sketch, "E1133", {"start": v(0.52, 0.24) * mm, "end": v(0.54, 0.24) * mm});
            skLineSegment(sketch, "E1134", {"start": v(0.54, 0.24) * mm, "end": v(0.55, 0.24) * mm});
            skLineSegment(sketch, "E1135", {"start": v(0.55, 0.24) * mm, "end": v(0.57, 0.23) * mm});
            skLineSegment(sketch, "E1136", {"start": v(0.57, 0.23) * mm, "end": v(0.57, 0.22) * mm});
            skSolve(sketch);
        }
        {
            var Q0;
            Q0=makeQuery(id+"F4.imprint","IMPRINT",FACE,{"disambiguationData":[TD([[makeQuery(id+"F4.imprint","IMPRINT",EDGE,{"derivedFrom":sQuery(id+"F4.wireOp",EDGE,"E913")}),-1.0]])]});
            var Q1;
            Q1=makeQuery(id+"F4.imprint","IMPRINT",FACE,{"disambiguationData":[TD([[makeQuery(id+"F4.imprint","IMPRINT",EDGE,{"derivedFrom":sQuery(id+"F4.wireOp",EDGE,"E1020")}),-1.0]])]});
            var Q2;
            Q2=makeQuery(id+"F4.imprint","IMPRINT",FACE,{"disambiguationData":[TD([[makeQuery(id+"F4.imprint","IMPRINT",EDGE,{"derivedFrom":sQuery(id+"F4.wireOp",EDGE,"E4")}),-1.0]])]});
            var Q3;
            Q3=makeQuery(id+"F4.imprint","IMPRINT",FACE,{"disambiguationData":[TD([[makeQuery(id+"F4.imprint","IMPRINT",EDGE,{"derivedFrom":sQuery(id+"F4.wireOp",EDGE,"E117")}),-1.0]])]});
            var Q4;
            Q4=makeQuery(id+"F4.imprint","IMPRINT",FACE,{"disambiguationData":[TD([[makeQuery(id+"F4.imprint","IMPRINT",EDGE,{"derivedFrom":sQuery(id+"F4.wireOp",EDGE,"E462")}),-1.0]])]});
            var Q5;
            Q5=makeQuery(id+"F4.imprint","IMPRINT",FACE,{"disambiguationData":[TD([[makeQuery(id+"F4.imprint","IMPRINT",EDGE,{"derivedFrom":sQuery(id+"F4.wireOp",EDGE,"E834")}),-1.0]])]});
            var Q6;
            Q6=makeQuery(id+"F4.imprint","IMPRINT",FACE,{"disambiguationData":[TD([[makeQuery(id+"F4.imprint","IMPRINT",EDGE,{"derivedFrom":sQuery(id+"F4.wireOp",EDGE,"E1121")}),-1.0]])]});
            var Q7;
            Q7=makeQuery(id+"F4.imprint","IMPRINT",FACE,{"disambiguationData":[TD([[makeQuery(id+"F4.imprint","IMPRINT",EDGE,{"derivedFrom":sQuery(id+"F4.wireOp",EDGE,"E709")}),-1.0]])]});
            var Q8;
            Q8=makeQuery(id+"F4.imprint","IMPRINT",FACE,{"disambiguationData":[TD([[makeQuery(id+"F4.imprint","IMPRINT",EDGE,{"derivedFrom":sQuery(id+"F4.wireOp",EDGE,"E575")}),-1.0]])]});
            var Q9;
            Q9=makeQuery(id+"F4.imprint","IMPRINT",FACE,{"disambiguationData":[TD([[makeQuery(id+"F4.imprint","IMPRINT",EDGE,{"derivedFrom":sQuery(id+"F4.wireOp",EDGE,"E604")}),-1.0]])]});
            var Q10;
            Q10=makeQuery(id+"F4.imprint","IMPRINT",FACE,{"disambiguationData":[TD([[makeQuery(id+"F4.imprint","IMPRINT",EDGE,{"derivedFrom":sQuery(id+"F4.wireOp",EDGE,"E289")}),-1.0]])]});
            extrude(context, id + "F5", {"entities" : qUnion([Q0, Q1, Q2, Q3, Q4, Q5, Q6, Q7, Q8, Q9, Q10]), "oppositeDirection" : true, "depth" : 1 * mm, "offsetDistance" : 25 * mm});
        }
        {
            var Q0;
            Q0=makeQuery(id+"F5.opExtrude","SWEPT_BODY",BODY,{"disambiguationData":[OSD([sQuery(id+"F4.wireOp",EDGE,"E4"),sQuery(id+"F4.wireOp",EDGE,"E5"),sQuery(id+"F4.wireOp",EDGE,"E6"),sQuery(id+"F4.wireOp",EDGE,"E7"),sQuery(id+"F4.wireOp",EDGE,"E8"),sQuery(id+"F4.wireOp",EDGE,"E9"),sQuery(id+"F4.wireOp",EDGE,"E10"),sQuery(id+"F4.wireOp",EDGE,"E11"),sQuery(id+"F4.wireOp",EDGE,"E12"),sQuery(id+"F4.wireOp",EDGE,"E13"),sQuery(id+"F4.wireOp",EDGE,"E14"),sQuery(id+"F4.wireOp",EDGE,"E15"),sQuery(id+"F4.wireOp",EDGE,"E16"),sQuery(id+"F4.wireOp",EDGE,"E17"),sQuery(id+"F4.wireOp",EDGE,"E18"),sQuery(id+"F4.wireOp",EDGE,"E19"),sQuery(id+"F4.wireOp",EDGE,"E20"),sQuery(id+"F4.wireOp",EDGE,"E21"),sQuery(id+"F4.wireOp",EDGE,"E22"),sQuery(id+"F4.wireOp",EDGE,"E23"),sQuery(id+"F4.wireOp",EDGE,"E24"),sQuery(id+"F4.wireOp",EDGE,"E25"),sQuery(id+"F4.wireOp",EDGE,"E26"),sQuery(id+"F4.wireOp",EDGE,"E26"),sQuery(id+"F4.wireOp",EDGE,"E27"),sQuery(id+"F4.wireOp",EDGE,"E28"),sQuery(id+"F4.wireOp",EDGE,"E29"),sQuery(id+"F4.wireOp",EDGE,"E30"),sQuery(id+"F4.wireOp",EDGE,"E31"),sQuery(id+"F4.wireOp",EDGE,"E32"),sQuery(id+"F4.wireOp",EDGE,"E33"),sQuery(id+"F4.wireOp",EDGE,"E34"),sQuery(id+"F4.wireOp",EDGE,"E35"),sQuery(id+"F4.wireOp",EDGE,"E36"),sQuery(id+"F4.wireOp",EDGE,"E37"),sQuery(id+"F4.wireOp",EDGE,"E38"),sQuery(id+"F4.wireOp",EDGE,"E39"),sQuery(id+"F4.wireOp",EDGE,"E40"),sQuery(id+"F4.wireOp",EDGE,"E41"),sQuery(id+"F4.wireOp",EDGE,"E42"),sQuery(id+"F4.wireOp",EDGE,"E43"),sQuery(id+"F4.wireOp",EDGE,"E44"),sQuery(id+"F4.wireOp",EDGE,"E45"),sQuery(id+"F4.wireOp",EDGE,"E46"),sQuery(id+"F4.wireOp",EDGE,"E47"),sQuery(id+"F4.wireOp",EDGE,"E48"),sQuery(id+"F4.wireOp",EDGE,"E49"),sQuery(id+"F4.wireOp",EDGE,"E50"),sQuery(id+"F4.wireOp",EDGE,"E51"),sQuery(id+"F4.wireOp",EDGE,"E52"),sQuery(id+"F4.wireOp",EDGE,"E53"),sQuery(id+"F4.wireOp",EDGE,"E54"),sQuery(id+"F4.wireOp",EDGE,"E55"),sQuery(id+"F4.wireOp",EDGE,"E56"),sQuery(id+"F4.wireOp",EDGE,"E57"),sQuery(id+"F4.wireOp",EDGE,"E58"),sQuery(id+"F4.wireOp",EDGE,"E59"),sQuery(id+"F4.wireOp",EDGE,"E60"),sQuery(id+"F4.wireOp",EDGE,"E61"),sQuery(id+"F4.wireOp",EDGE,"E62"),sQuery(id+"F4.wireOp",EDGE,"E63"),sQuery(id+"F4.wireOp",EDGE,"E64"),sQuery(id+"F4.wireOp",EDGE,"E65"),sQuery(id+"F4.wireOp",EDGE,"E65"),sQuery(id+"F4.wireOp",EDGE,"E66"),sQuery(id+"F4.wireOp",EDGE,"E67"),sQuery(id+"F4.wireOp",EDGE,"E68"),sQuery(id+"F4.wireOp",EDGE,"E69"),sQuery(id+"F4.wireOp",EDGE,"E70"),sQuery(id+"F4.wireOp",EDGE,"E71"),sQuery(id+"F4.wireOp",EDGE,"E72"),sQuery(id+"F4.wireOp",EDGE,"E73"),sQuery(id+"F4.wireOp",EDGE,"E74"),sQuery(id+"F4.wireOp",EDGE,"E75"),sQuery(id+"F4.wireOp",EDGE,"E76"),sQuery(id+"F4.wireOp",EDGE,"E77"),sQuery(id+"F4.wireOp",EDGE,"E78"),sQuery(id+"F4.wireOp",EDGE,"E79"),sQuery(id+"F4.wireOp",EDGE,"E80"),sQuery(id+"F4.wireOp",EDGE,"E81"),sQuery(id+"F4.wireOp",EDGE,"E82"),sQuery(id+"F4.wireOp",EDGE,"E83"),sQuery(id+"F4.wireOp",EDGE,"E84"),sQuery(id+"F4.wireOp",EDGE,"E85"),sQuery(id+"F4.wireOp",EDGE,"E86"),sQuery(id+"F4.wireOp",EDGE,"E87"),sQuery(id+"F4.wireOp",EDGE,"E88"),sQuery(id+"F4.wireOp",EDGE,"E89"),sQuery(id+"F4.wireOp",EDGE,"E90"),sQuery(id+"F4.wireOp",EDGE,"E91"),sQuery(id+"F4.wireOp",EDGE,"E92"),sQuery(id+"F4.wireOp",EDGE,"E93"),sQuery(id+"F4.wireOp",EDGE,"E94"),sQuery(id+"F4.wireOp",EDGE,"E95"),sQuery(id+"F4.wireOp",EDGE,"E96"),sQuery(id+"F4.wireOp",EDGE,"E97"),sQuery(id+"F4.wireOp",EDGE,"E98"),sQuery(id+"F4.wireOp",EDGE,"E99"),sQuery(id+"F4.wireOp",EDGE,"E100"),sQuery(id+"F4.wireOp",EDGE,"E101"),sQuery(id+"F4.wireOp",EDGE,"E102"),sQuery(id+"F4.wireOp",EDGE,"E103"),sQuery(id+"F4.wireOp",EDGE,"E104"),sQuery(id+"F4.wireOp",EDGE,"E105"),sQuery(id+"F4.wireOp",EDGE,"E106"),sQuery(id+"F4.wireOp",EDGE,"E107"),sQuery(id+"F4.wireOp",EDGE,"E108"),sQuery(id+"F4.wireOp",EDGE,"E109"),sQuery(id+"F4.wireOp",EDGE,"E110"),sQuery(id+"F4.wireOp",EDGE,"E111"),sQuery(id+"F4.wireOp",EDGE,"E112"),sQuery(id+"F4.wireOp",EDGE,"E113"),sQuery(id+"F4.wireOp",EDGE,"E114"),sQuery(id+"F4.wireOp",EDGE,"E114"),sQuery(id+"F4.wireOp",EDGE,"E115"),sQuery(id+"F4.wireOp",EDGE,"E116")])]});
            var Q1;
            Q1=makeQuery(id+"F5.opExtrude","SWEPT_BODY",BODY,{"disambiguationData":[OSD([sQuery(id+"F4.wireOp",EDGE,"E117"),sQuery(id+"F4.wireOp",EDGE,"E118"),sQuery(id+"F4.wireOp",EDGE,"E119"),sQuery(id+"F4.wireOp",EDGE,"E120"),sQuery(id+"F4.wireOp",EDGE,"E121"),sQuery(id+"F4.wireOp",EDGE,"E122"),sQuery(id+"F4.wireOp",EDGE,"E123"),sQuery(id+"F4.wireOp",EDGE,"E124"),sQuery(id+"F4.wireOp",EDGE,"E125"),sQuery(id+"F4.wireOp",EDGE,"E126"),sQuery(id+"F4.wireOp",EDGE,"E127"),sQuery(id+"F4.wireOp",EDGE,"E128"),sQuery(id+"F4.wireOp",EDGE,"E129"),sQuery(id+"F4.wireOp",EDGE,"E130"),sQuery(id+"F4.wireOp",EDGE,"E131"),sQuery(id+"F4.wireOp",EDGE,"E132"),sQuery(id+"F4.wireOp",EDGE,"E133"),sQuery(id+"F4.wireOp",EDGE,"E133"),sQuery(id+"F4.wireOp",EDGE,"E134"),sQuery(id+"F4.wireOp",EDGE,"E135"),sQuery(id+"F4.wireOp",EDGE,"E136"),sQuery(id+"F4.wireOp",EDGE,"E137"),sQuery(id+"F4.wireOp",EDGE,"E138"),sQuery(id+"F4.wireOp",EDGE,"E139"),sQuery(id+"F4.wireOp",EDGE,"E140"),sQuery(id+"F4.wireOp",EDGE,"E141"),sQuery(id+"F4.wireOp",EDGE,"E142"),sQuery(id+"F4.wireOp",EDGE,"E143"),sQuery(id+"F4.wireOp",EDGE,"E144"),sQuery(id+"F4.wireOp",EDGE,"E145"),sQuery(id+"F4.wireOp",EDGE,"E146"),sQuery(id+"F4.wireOp",EDGE,"E147"),sQuery(id+"F4.wireOp",EDGE,"E148"),sQuery(id+"F4.wireOp",EDGE,"E149"),sQuery(id+"F4.wireOp",EDGE,"E150"),sQuery(id+"F4.wireOp",EDGE,"E151"),sQuery(id+"F4.wireOp",EDGE,"E152"),sQuery(id+"F4.wireOp",EDGE,"E153"),sQuery(id+"F4.wireOp",EDGE,"E154"),sQuery(id+"F4.wireOp",EDGE,"E155"),sQuery(id+"F4.wireOp",EDGE,"E156"),sQuery(id+"F4.wireOp",EDGE,"E157"),sQuery(id+"F4.wireOp",EDGE,"E158"),sQuery(id+"F4.wireOp",EDGE,"E159"),sQuery(id+"F4.wireOp",EDGE,"E160"),sQuery(id+"F4.wireOp",EDGE,"E161"),sQuery(id+"F4.wireOp",EDGE,"E162"),sQuery(id+"F4.wireOp",EDGE,"E162"),sQuery(id+"F4.wireOp",EDGE,"E162"),sQuery(id+"F4.wireOp",EDGE,"E163"),sQuery(id+"F4.wireOp",EDGE,"E164"),sQuery(id+"F4.wireOp",EDGE,"E165"),sQuery(id+"F4.wireOp",EDGE,"E166"),sQuery(id+"F4.wireOp",EDGE,"E167"),sQuery(id+"F4.wireOp",EDGE,"E168"),sQuery(id+"F4.wireOp",EDGE,"E169"),sQuery(id+"F4.wireOp",EDGE,"E170"),sQuery(id+"F4.wireOp",EDGE,"E171"),sQuery(id+"F4.wireOp",EDGE,"E171"),sQuery(id+"F4.wireOp",EDGE,"E172"),sQuery(id+"F4.wireOp",EDGE,"E173"),sQuery(id+"F4.wireOp",EDGE,"E174"),sQuery(id+"F4.wireOp",EDGE,"E175"),sQuery(id+"F4.wireOp",EDGE,"E176"),sQuery(id+"F4.wireOp",EDGE,"E177"),sQuery(id+"F4.wireOp",EDGE,"E178"),sQuery(id+"F4.wireOp",EDGE,"E179"),sQuery(id+"F4.wireOp",EDGE,"E180"),sQuery(id+"F4.wireOp",EDGE,"E181"),sQuery(id+"F4.wireOp",EDGE,"E182"),sQuery(id+"F4.wireOp",EDGE,"E183"),sQuery(id+"F4.wireOp",EDGE,"E184"),sQuery(id+"F4.wireOp",EDGE,"E185"),sQuery(id+"F4.wireOp",EDGE,"E186"),sQuery(id+"F4.wireOp",EDGE,"E187"),sQuery(id+"F4.wireOp",EDGE,"E188"),sQuery(id+"F4.wireOp",EDGE,"E189"),sQuery(id+"F4.wireOp",EDGE,"E190"),sQuery(id+"F4.wireOp",EDGE,"E191"),sQuery(id+"F4.wireOp",EDGE,"E192"),sQuery(id+"F4.wireOp",EDGE,"E193"),sQuery(id+"F4.wireOp",EDGE,"E194"),sQuery(id+"F4.wireOp",EDGE,"E195"),sQuery(id+"F4.wireOp",EDGE,"E196"),sQuery(id+"F4.wireOp",EDGE,"E197"),sQuery(id+"F4.wireOp",EDGE,"E198"),sQuery(id+"F4.wireOp",EDGE,"E199"),sQuery(id+"F4.wireOp",EDGE,"E200"),sQuery(id+"F4.wireOp",EDGE,"E201"),sQuery(id+"F4.wireOp",EDGE,"E202"),sQuery(id+"F4.wireOp",EDGE,"E203"),sQuery(id+"F4.wireOp",EDGE,"E204"),sQuery(id+"F4.wireOp",EDGE,"E205"),sQuery(id+"F4.wireOp",EDGE,"E206"),sQuery(id+"F4.wireOp",EDGE,"E207"),sQuery(id+"F4.wireOp",EDGE,"E208"),sQuery(id+"F4.wireOp",EDGE,"E209"),sQuery(id+"F4.wireOp",EDGE,"E210"),sQuery(id+"F4.wireOp",EDGE,"E211"),sQuery(id+"F4.wireOp",EDGE,"E212"),sQuery(id+"F4.wireOp",EDGE,"E213"),sQuery(id+"F4.wireOp",EDGE,"E214"),sQuery(id+"F4.wireOp",EDGE,"E215"),sQuery(id+"F4.wireOp",EDGE,"E216"),sQuery(id+"F4.wireOp",EDGE,"E217"),sQuery(id+"F4.wireOp",EDGE,"E218"),sQuery(id+"F4.wireOp",EDGE,"E219"),sQuery(id+"F4.wireOp",EDGE,"E220"),sQuery(id+"F4.wireOp",EDGE,"E221"),sQuery(id+"F4.wireOp",EDGE,"E222"),sQuery(id+"F4.wireOp",EDGE,"E223"),sQuery(id+"F4.wireOp",EDGE,"E224"),sQuery(id+"F4.wireOp",EDGE,"E225"),sQuery(id+"F4.wireOp",EDGE,"E226"),sQuery(id+"F4.wireOp",EDGE,"E227"),sQuery(id+"F4.wireOp",EDGE,"E228"),sQuery(id+"F4.wireOp",EDGE,"E229"),sQuery(id+"F4.wireOp",EDGE,"E230"),sQuery(id+"F4.wireOp",EDGE,"E231"),sQuery(id+"F4.wireOp",EDGE,"E232"),sQuery(id+"F4.wireOp",EDGE,"E233"),sQuery(id+"F4.wireOp",EDGE,"E234"),sQuery(id+"F4.wireOp",EDGE,"E235"),sQuery(id+"F4.wireOp",EDGE,"E236"),sQuery(id+"F4.wireOp",EDGE,"E237"),sQuery(id+"F4.wireOp",EDGE,"E238"),sQuery(id+"F4.wireOp",EDGE,"E239"),sQuery(id+"F4.wireOp",EDGE,"E240"),sQuery(id+"F4.wireOp",EDGE,"E241"),sQuery(id+"F4.wireOp",EDGE,"E242"),sQuery(id+"F4.wireOp",EDGE,"E243"),sQuery(id+"F4.wireOp",EDGE,"E244"),sQuery(id+"F4.wireOp",EDGE,"E245"),sQuery(id+"F4.wireOp",EDGE,"E246"),sQuery(id+"F4.wireOp",EDGE,"E247"),sQuery(id+"F4.wireOp",EDGE,"E248"),sQuery(id+"F4.wireOp",EDGE,"E249"),sQuery(id+"F4.wireOp",EDGE,"E250"),sQuery(id+"F4.wireOp",EDGE,"E250"),sQuery(id+"F4.wireOp",EDGE,"E251"),sQuery(id+"F4.wireOp",EDGE,"E252"),sQuery(id+"F4.wireOp",EDGE,"E253"),sQuery(id+"F4.wireOp",EDGE,"E254"),sQuery(id+"F4.wireOp",EDGE,"E255"),sQuery(id+"F4.wireOp",EDGE,"E256"),sQuery(id+"F4.wireOp",EDGE,"E257"),sQuery(id+"F4.wireOp",EDGE,"E258"),sQuery(id+"F4.wireOp",EDGE,"E259"),sQuery(id+"F4.wireOp",EDGE,"E260"),sQuery(id+"F4.wireOp",EDGE,"E261"),sQuery(id+"F4.wireOp",EDGE,"E262"),sQuery(id+"F4.wireOp",EDGE,"E262"),sQuery(id+"F4.wireOp",EDGE,"E262"),sQuery(id+"F4.wireOp",EDGE,"E263"),sQuery(id+"F4.wireOp",EDGE,"E264"),sQuery(id+"F4.wireOp",EDGE,"E265"),sQuery(id+"F4.wireOp",EDGE,"E266"),sQuery(id+"F4.wireOp",EDGE,"E267"),sQuery(id+"F4.wireOp",EDGE,"E268"),sQuery(id+"F4.wireOp",EDGE,"E269"),sQuery(id+"F4.wireOp",EDGE,"E270"),sQuery(id+"F4.wireOp",EDGE,"E271"),sQuery(id+"F4.wireOp",EDGE,"E272"),sQuery(id+"F4.wireOp",EDGE,"E273"),sQuery(id+"F4.wireOp",EDGE,"E274"),sQuery(id+"F4.wireOp",EDGE,"E275"),sQuery(id+"F4.wireOp",EDGE,"E276"),sQuery(id+"F4.wireOp",EDGE,"E277"),sQuery(id+"F4.wireOp",EDGE,"E278"),sQuery(id+"F4.wireOp",EDGE,"E279"),sQuery(id+"F4.wireOp",EDGE,"E280"),sQuery(id+"F4.wireOp",EDGE,"E281"),sQuery(id+"F4.wireOp",EDGE,"E282"),sQuery(id+"F4.wireOp",EDGE,"E283"),sQuery(id+"F4.wireOp",EDGE,"E284"),sQuery(id+"F4.wireOp",EDGE,"E285"),sQuery(id+"F4.wireOp",EDGE,"E286"),sQuery(id+"F4.wireOp",EDGE,"E287"),sQuery(id+"F4.wireOp",EDGE,"E288")])]});
            var Q2;
            Q2=makeQuery(id+"F5.opExtrude","SWEPT_BODY",BODY,{"disambiguationData":[OSD([sQuery(id+"F4.wireOp",EDGE,"E289"),sQuery(id+"F4.wireOp",EDGE,"E290"),sQuery(id+"F4.wireOp",EDGE,"E291"),sQuery(id+"F4.wireOp",EDGE,"E292"),sQuery(id+"F4.wireOp",EDGE,"E293"),sQuery(id+"F4.wireOp",EDGE,"E294"),sQuery(id+"F4.wireOp",EDGE,"E295"),sQuery(id+"F4.wireOp",EDGE,"E296"),sQuery(id+"F4.wireOp",EDGE,"E297"),sQuery(id+"F4.wireOp",EDGE,"E298"),sQuery(id+"F4.wireOp",EDGE,"E299"),sQuery(id+"F4.wireOp",EDGE,"E300"),sQuery(id+"F4.wireOp",EDGE,"E301"),sQuery(id+"F4.wireOp",EDGE,"E302"),sQuery(id+"F4.wireOp",EDGE,"E303"),sQuery(id+"F4.wireOp",EDGE,"E304"),sQuery(id+"F4.wireOp",EDGE,"E305"),sQuery(id+"F4.wireOp",EDGE,"E306"),sQuery(id+"F4.wireOp",EDGE,"E307"),sQuery(id+"F4.wireOp",EDGE,"E308"),sQuery(id+"F4.wireOp",EDGE,"E309"),sQuery(id+"F4.wireOp",EDGE,"E310"),sQuery(id+"F4.wireOp",EDGE,"E311"),sQuery(id+"F4.wireOp",EDGE,"E312"),sQuery(id+"F4.wireOp",EDGE,"E313"),sQuery(id+"F4.wireOp",EDGE,"E314"),sQuery(id+"F4.wireOp",EDGE,"E315"),sQuery(id+"F4.wireOp",EDGE,"E316"),sQuery(id+"F4.wireOp",EDGE,"E317"),sQuery(id+"F4.wireOp",EDGE,"E318"),sQuery(id+"F4.wireOp",EDGE,"E319"),sQuery(id+"F4.wireOp",EDGE,"E320"),sQuery(id+"F4.wireOp",EDGE,"E321"),sQuery(id+"F4.wireOp",EDGE,"E322"),sQuery(id+"F4.wireOp",EDGE,"E323"),sQuery(id+"F4.wireOp",EDGE,"E324"),sQuery(id+"F4.wireOp",EDGE,"E325"),sQuery(id+"F4.wireOp",EDGE,"E326"),sQuery(id+"F4.wireOp",EDGE,"E327"),sQuery(id+"F4.wireOp",EDGE,"E328"),sQuery(id+"F4.wireOp",EDGE,"E329"),sQuery(id+"F4.wireOp",EDGE,"E330"),sQuery(id+"F4.wireOp",EDGE,"E331"),sQuery(id+"F4.wireOp",EDGE,"E332"),sQuery(id+"F4.wireOp",EDGE,"E333"),sQuery(id+"F4.wireOp",EDGE,"E334"),sQuery(id+"F4.wireOp",EDGE,"E335"),sQuery(id+"F4.wireOp",EDGE,"E336"),sQuery(id+"F4.wireOp",EDGE,"E337"),sQuery(id+"F4.wireOp",EDGE,"E338"),sQuery(id+"F4.wireOp",EDGE,"E339"),sQuery(id+"F4.wireOp",EDGE,"E340"),sQuery(id+"F4.wireOp",EDGE,"E341"),sQuery(id+"F4.wireOp",EDGE,"E342"),sQuery(id+"F4.wireOp",EDGE,"E343"),sQuery(id+"F4.wireOp",EDGE,"E344"),sQuery(id+"F4.wireOp",EDGE,"E345"),sQuery(id+"F4.wireOp",EDGE,"E346"),sQuery(id+"F4.wireOp",EDGE,"E346"),sQuery(id+"F4.wireOp",EDGE,"E347"),sQuery(id+"F4.wireOp",EDGE,"E348"),sQuery(id+"F4.wireOp",EDGE,"E349"),sQuery(id+"F4.wireOp",EDGE,"E350"),sQuery(id+"F4.wireOp",EDGE,"E351"),sQuery(id+"F4.wireOp",EDGE,"E352"),sQuery(id+"F4.wireOp",EDGE,"E353"),sQuery(id+"F4.wireOp",EDGE,"E354"),sQuery(id+"F4.wireOp",EDGE,"E355"),sQuery(id+"F4.wireOp",EDGE,"E356"),sQuery(id+"F4.wireOp",EDGE,"E357"),sQuery(id+"F4.wireOp",EDGE,"E358"),sQuery(id+"F4.wireOp",EDGE,"E359"),sQuery(id+"F4.wireOp",EDGE,"E360"),sQuery(id+"F4.wireOp",EDGE,"E361"),sQuery(id+"F4.wireOp",EDGE,"E362"),sQuery(id+"F4.wireOp",EDGE,"E363"),sQuery(id+"F4.wireOp",EDGE,"E364"),sQuery(id+"F4.wireOp",EDGE,"E365"),sQuery(id+"F4.wireOp",EDGE,"E366"),sQuery(id+"F4.wireOp",EDGE,"E367"),sQuery(id+"F4.wireOp",EDGE,"E368"),sQuery(id+"F4.wireOp",EDGE,"E369"),sQuery(id+"F4.wireOp",EDGE,"E370"),sQuery(id+"F4.wireOp",EDGE,"E371"),sQuery(id+"F4.wireOp",EDGE,"E371"),sQuery(id+"F4.wireOp",EDGE,"E372"),sQuery(id+"F4.wireOp",EDGE,"E373"),sQuery(id+"F4.wireOp",EDGE,"E374"),sQuery(id+"F4.wireOp",EDGE,"E375"),sQuery(id+"F4.wireOp",EDGE,"E376"),sQuery(id+"F4.wireOp",EDGE,"E377"),sQuery(id+"F4.wireOp",EDGE,"E378"),sQuery(id+"F4.wireOp",EDGE,"E379"),sQuery(id+"F4.wireOp",EDGE,"E380"),sQuery(id+"F4.wireOp",EDGE,"E381"),sQuery(id+"F4.wireOp",EDGE,"E382"),sQuery(id+"F4.wireOp",EDGE,"E383"),sQuery(id+"F4.wireOp",EDGE,"E384"),sQuery(id+"F4.wireOp",EDGE,"E385"),sQuery(id+"F4.wireOp",EDGE,"E386"),sQuery(id+"F4.wireOp",EDGE,"E387"),sQuery(id+"F4.wireOp",EDGE,"E388"),sQuery(id+"F4.wireOp",EDGE,"E389"),sQuery(id+"F4.wireOp",EDGE,"E390"),sQuery(id+"F4.wireOp",EDGE,"E391"),sQuery(id+"F4.wireOp",EDGE,"E392"),sQuery(id+"F4.wireOp",EDGE,"E392"),sQuery(id+"F4.wireOp",EDGE,"E393"),sQuery(id+"F4.wireOp",EDGE,"E394"),sQuery(id+"F4.wireOp",EDGE,"E395"),sQuery(id+"F4.wireOp",EDGE,"E396"),sQuery(id+"F4.wireOp",EDGE,"E397"),sQuery(id+"F4.wireOp",EDGE,"E398"),sQuery(id+"F4.wireOp",EDGE,"E399"),sQuery(id+"F4.wireOp",EDGE,"E400"),sQuery(id+"F4.wireOp",EDGE,"E401"),sQuery(id+"F4.wireOp",EDGE,"E402"),sQuery(id+"F4.wireOp",EDGE,"E403"),sQuery(id+"F4.wireOp",EDGE,"E404"),sQuery(id+"F4.wireOp",EDGE,"E405"),sQuery(id+"F4.wireOp",EDGE,"E406"),sQuery(id+"F4.wireOp",EDGE,"E407"),sQuery(id+"F4.wireOp",EDGE,"E408"),sQuery(id+"F4.wireOp",EDGE,"E409"),sQuery(id+"F4.wireOp",EDGE,"E410"),sQuery(id+"F4.wireOp",EDGE,"E411"),sQuery(id+"F4.wireOp",EDGE,"E412"),sQuery(id+"F4.wireOp",EDGE,"E413"),sQuery(id+"F4.wireOp",EDGE,"E414"),sQuery(id+"F4.wireOp",EDGE,"E415"),sQuery(id+"F4.wireOp",EDGE,"E416"),sQuery(id+"F4.wireOp",EDGE,"E417"),sQuery(id+"F4.wireOp",EDGE,"E418"),sQuery(id+"F4.wireOp",EDGE,"E419"),sQuery(id+"F4.wireOp",EDGE,"E420"),sQuery(id+"F4.wireOp",EDGE,"E421"),sQuery(id+"F4.wireOp",EDGE,"E422"),sQuery(id+"F4.wireOp",EDGE,"E423"),sQuery(id+"F4.wireOp",EDGE,"E424"),sQuery(id+"F4.wireOp",EDGE,"E425"),sQuery(id+"F4.wireOp",EDGE,"E426"),sQuery(id+"F4.wireOp",EDGE,"E427"),sQuery(id+"F4.wireOp",EDGE,"E428"),sQuery(id+"F4.wireOp",EDGE,"E429"),sQuery(id+"F4.wireOp",EDGE,"E430"),sQuery(id+"F4.wireOp",EDGE,"E431"),sQuery(id+"F4.wireOp",EDGE,"E431"),sQuery(id+"F4.wireOp",EDGE,"E432"),sQuery(id+"F4.wireOp",EDGE,"E433"),sQuery(id+"F4.wireOp",EDGE,"E434"),sQuery(id+"F4.wireOp",EDGE,"E435"),sQuery(id+"F4.wireOp",EDGE,"E436"),sQuery(id+"F4.wireOp",EDGE,"E436"),sQuery(id+"F4.wireOp",EDGE,"E437"),sQuery(id+"F4.wireOp",EDGE,"E438"),sQuery(id+"F4.wireOp",EDGE,"E439"),sQuery(id+"F4.wireOp",EDGE,"E440"),sQuery(id+"F4.wireOp",EDGE,"E441"),sQuery(id+"F4.wireOp",EDGE,"E442"),sQuery(id+"F4.wireOp",EDGE,"E443"),sQuery(id+"F4.wireOp",EDGE,"E444"),sQuery(id+"F4.wireOp",EDGE,"E445"),sQuery(id+"F4.wireOp",EDGE,"E446"),sQuery(id+"F4.wireOp",EDGE,"E447"),sQuery(id+"F4.wireOp",EDGE,"E448"),sQuery(id+"F4.wireOp",EDGE,"E448"),sQuery(id+"F4.wireOp",EDGE,"E449"),sQuery(id+"F4.wireOp",EDGE,"E450"),sQuery(id+"F4.wireOp",EDGE,"E451"),sQuery(id+"F4.wireOp",EDGE,"E452"),sQuery(id+"F4.wireOp",EDGE,"E453"),sQuery(id+"F4.wireOp",EDGE,"E454"),sQuery(id+"F4.wireOp",EDGE,"E455"),sQuery(id+"F4.wireOp",EDGE,"E456"),sQuery(id+"F4.wireOp",EDGE,"E457"),sQuery(id+"F4.wireOp",EDGE,"E458"),sQuery(id+"F4.wireOp",EDGE,"E459"),sQuery(id+"F4.wireOp",EDGE,"E460"),sQuery(id+"F4.wireOp",EDGE,"E461")])]});
            var Q3;
            Q3=makeQuery(id+"F5.opExtrude","SWEPT_BODY",BODY,{"disambiguationData":[OSD([sQuery(id+"F4.wireOp",EDGE,"E462"),sQuery(id+"F4.wireOp",EDGE,"E463"),sQuery(id+"F4.wireOp",EDGE,"E464"),sQuery(id+"F4.wireOp",EDGE,"E465"),sQuery(id+"F4.wireOp",EDGE,"E466"),sQuery(id+"F4.wireOp",EDGE,"E467"),sQuery(id+"F4.wireOp",EDGE,"E468"),sQuery(id+"F4.wireOp",EDGE,"E469"),sQuery(id+"F4.wireOp",EDGE,"E470"),sQuery(id+"F4.wireOp",EDGE,"E471"),sQuery(id+"F4.wireOp",EDGE,"E472"),sQuery(id+"F4.wireOp",EDGE,"E473"),sQuery(id+"F4.wireOp",EDGE,"E474"),sQuery(id+"F4.wireOp",EDGE,"E475"),sQuery(id+"F4.wireOp",EDGE,"E476"),sQuery(id+"F4.wireOp",EDGE,"E477"),sQuery(id+"F4.wireOp",EDGE,"E478"),sQuery(id+"F4.wireOp",EDGE,"E479"),sQuery(id+"F4.wireOp",EDGE,"E480"),sQuery(id+"F4.wireOp",EDGE,"E481"),sQuery(id+"F4.wireOp",EDGE,"E482"),sQuery(id+"F4.wireOp",EDGE,"E483"),sQuery(id+"F4.wireOp",EDGE,"E484"),sQuery(id+"F4.wireOp",EDGE,"E485"),sQuery(id+"F4.wireOp",EDGE,"E486"),sQuery(id+"F4.wireOp",EDGE,"E487"),sQuery(id+"F4.wireOp",EDGE,"E488"),sQuery(id+"F4.wireOp",EDGE,"E489"),sQuery(id+"F4.wireOp",EDGE,"E490"),sQuery(id+"F4.wireOp",EDGE,"E491"),sQuery(id+"F4.wireOp",EDGE,"E492"),sQuery(id+"F4.wireOp",EDGE,"E493"),sQuery(id+"F4.wireOp",EDGE,"E494"),sQuery(id+"F4.wireOp",EDGE,"E495"),sQuery(id+"F4.wireOp",EDGE,"E496"),sQuery(id+"F4.wireOp",EDGE,"E497"),sQuery(id+"F4.wireOp",EDGE,"E498"),sQuery(id+"F4.wireOp",EDGE,"E499"),sQuery(id+"F4.wireOp",EDGE,"E500"),sQuery(id+"F4.wireOp",EDGE,"E501"),sQuery(id+"F4.wireOp",EDGE,"E502"),sQuery(id+"F4.wireOp",EDGE,"E503"),sQuery(id+"F4.wireOp",EDGE,"E504"),sQuery(id+"F4.wireOp",EDGE,"E505"),sQuery(id+"F4.wireOp",EDGE,"E506"),sQuery(id+"F4.wireOp",EDGE,"E507"),sQuery(id+"F4.wireOp",EDGE,"E508"),sQuery(id+"F4.wireOp",EDGE,"E509"),sQuery(id+"F4.wireOp",EDGE,"E510"),sQuery(id+"F4.wireOp",EDGE,"E511"),sQuery(id+"F4.wireOp",EDGE,"E512"),sQuery(id+"F4.wireOp",EDGE,"E513"),sQuery(id+"F4.wireOp",EDGE,"E514"),sQuery(id+"F4.wireOp",EDGE,"E515"),sQuery(id+"F4.wireOp",EDGE,"E516"),sQuery(id+"F4.wireOp",EDGE,"E517"),sQuery(id+"F4.wireOp",EDGE,"E518"),sQuery(id+"F4.wireOp",EDGE,"E519"),sQuery(id+"F4.wireOp",EDGE,"E520"),sQuery(id+"F4.wireOp",EDGE,"E521"),sQuery(id+"F4.wireOp",EDGE,"E522"),sQuery(id+"F4.wireOp",EDGE,"E523"),sQuery(id+"F4.wireOp",EDGE,"E524"),sQuery(id+"F4.wireOp",EDGE,"E525"),sQuery(id+"F4.wireOp",EDGE,"E525"),sQuery(id+"F4.wireOp",EDGE,"E525"),sQuery(id+"F4.wireOp",EDGE,"E526"),sQuery(id+"F4.wireOp",EDGE,"E527"),sQuery(id+"F4.wireOp",EDGE,"E528"),sQuery(id+"F4.wireOp",EDGE,"E529"),sQuery(id+"F4.wireOp",EDGE,"E530"),sQuery(id+"F4.wireOp",EDGE,"E531"),sQuery(id+"F4.wireOp",EDGE,"E531"),sQuery(id+"F4.wireOp",EDGE,"E531"),sQuery(id+"F4.wireOp",EDGE,"E532"),sQuery(id+"F4.wireOp",EDGE,"E533"),sQuery(id+"F4.wireOp",EDGE,"E534"),sQuery(id+"F4.wireOp",EDGE,"E535"),sQuery(id+"F4.wireOp",EDGE,"E536"),sQuery(id+"F4.wireOp",EDGE,"E537"),sQuery(id+"F4.wireOp",EDGE,"E538"),sQuery(id+"F4.wireOp",EDGE,"E539"),sQuery(id+"F4.wireOp",EDGE,"E540"),sQuery(id+"F4.wireOp",EDGE,"E541"),sQuery(id+"F4.wireOp",EDGE,"E542"),sQuery(id+"F4.wireOp",EDGE,"E543"),sQuery(id+"F4.wireOp",EDGE,"E544"),sQuery(id+"F4.wireOp",EDGE,"E545"),sQuery(id+"F4.wireOp",EDGE,"E546"),sQuery(id+"F4.wireOp",EDGE,"E547"),sQuery(id+"F4.wireOp",EDGE,"E548"),sQuery(id+"F4.wireOp",EDGE,"E549"),sQuery(id+"F4.wireOp",EDGE,"E550"),sQuery(id+"F4.wireOp",EDGE,"E551"),sQuery(id+"F4.wireOp",EDGE,"E552"),sQuery(id+"F4.wireOp",EDGE,"E553"),sQuery(id+"F4.wireOp",EDGE,"E554"),sQuery(id+"F4.wireOp",EDGE,"E555"),sQuery(id+"F4.wireOp",EDGE,"E556"),sQuery(id+"F4.wireOp",EDGE,"E557"),sQuery(id+"F4.wireOp",EDGE,"E558"),sQuery(id+"F4.wireOp",EDGE,"E559"),sQuery(id+"F4.wireOp",EDGE,"E560"),sQuery(id+"F4.wireOp",EDGE,"E561"),sQuery(id+"F4.wireOp",EDGE,"E562"),sQuery(id+"F4.wireOp",EDGE,"E562"),sQuery(id+"F4.wireOp",EDGE,"E563"),sQuery(id+"F4.wireOp",EDGE,"E564"),sQuery(id+"F4.wireOp",EDGE,"E565"),sQuery(id+"F4.wireOp",EDGE,"E566"),sQuery(id+"F4.wireOp",EDGE,"E567"),sQuery(id+"F4.wireOp",EDGE,"E565"),sQuery(id+"F4.wireOp",EDGE,"E568"),sQuery(id+"F4.wireOp",EDGE,"E569"),sQuery(id+"F4.wireOp",EDGE,"E569"),sQuery(id+"F4.wireOp",EDGE,"E570"),sQuery(id+"F4.wireOp",EDGE,"E571"),sQuery(id+"F4.wireOp",EDGE,"E572"),sQuery(id+"F4.wireOp",EDGE,"E573"),sQuery(id+"F4.wireOp",EDGE,"E574")])]});
            var Q4;
            Q4=makeQuery(id+"F5.opExtrude","SWEPT_BODY",BODY,{"disambiguationData":[OSD([sQuery(id+"F4.wireOp",EDGE,"E575"),sQuery(id+"F4.wireOp",EDGE,"E576"),sQuery(id+"F4.wireOp",EDGE,"E577"),sQuery(id+"F4.wireOp",EDGE,"E578"),sQuery(id+"F4.wireOp",EDGE,"E579"),sQuery(id+"F4.wireOp",EDGE,"E580"),sQuery(id+"F4.wireOp",EDGE,"E581"),sQuery(id+"F4.wireOp",EDGE,"E582"),sQuery(id+"F4.wireOp",EDGE,"E583"),sQuery(id+"F4.wireOp",EDGE,"E584"),sQuery(id+"F4.wireOp",EDGE,"E585"),sQuery(id+"F4.wireOp",EDGE,"E586"),sQuery(id+"F4.wireOp",EDGE,"E587"),sQuery(id+"F4.wireOp",EDGE,"E588"),sQuery(id+"F4.wireOp",EDGE,"E589"),sQuery(id+"F4.wireOp",EDGE,"E590"),sQuery(id+"F4.wireOp",EDGE,"E591"),sQuery(id+"F4.wireOp",EDGE,"E592"),sQuery(id+"F4.wireOp",EDGE,"E593"),sQuery(id+"F4.wireOp",EDGE,"E594"),sQuery(id+"F4.wireOp",EDGE,"E595"),sQuery(id+"F4.wireOp",EDGE,"E596"),sQuery(id+"F4.wireOp",EDGE,"E597"),sQuery(id+"F4.wireOp",EDGE,"E598"),sQuery(id+"F4.wireOp",EDGE,"E599"),sQuery(id+"F4.wireOp",EDGE,"E600"),sQuery(id+"F4.wireOp",EDGE,"E601"),sQuery(id+"F4.wireOp",EDGE,"E602"),sQuery(id+"F4.wireOp",EDGE,"E603")])]});
            var Q5;
            Q5=makeQuery(id+"F5.opExtrude","SWEPT_BODY",BODY,{"disambiguationData":[OSD([sQuery(id+"F4.wireOp",EDGE,"E604"),sQuery(id+"F4.wireOp",EDGE,"E605"),sQuery(id+"F4.wireOp",EDGE,"E606"),sQuery(id+"F4.wireOp",EDGE,"E607"),sQuery(id+"F4.wireOp",EDGE,"E608"),sQuery(id+"F4.wireOp",EDGE,"E609"),sQuery(id+"F4.wireOp",EDGE,"E610"),sQuery(id+"F4.wireOp",EDGE,"E611"),sQuery(id+"F4.wireOp",EDGE,"E612"),sQuery(id+"F4.wireOp",EDGE,"E613"),sQuery(id+"F4.wireOp",EDGE,"E614"),sQuery(id+"F4.wireOp",EDGE,"E615"),sQuery(id+"F4.wireOp",EDGE,"E616"),sQuery(id+"F4.wireOp",EDGE,"E617"),sQuery(id+"F4.wireOp",EDGE,"E617"),sQuery(id+"F4.wireOp",EDGE,"E618"),sQuery(id+"F4.wireOp",EDGE,"E619"),sQuery(id+"F4.wireOp",EDGE,"E620"),sQuery(id+"F4.wireOp",EDGE,"E621"),sQuery(id+"F4.wireOp",EDGE,"E622"),sQuery(id+"F4.wireOp",EDGE,"E623"),sQuery(id+"F4.wireOp",EDGE,"E624"),sQuery(id+"F4.wireOp",EDGE,"E625"),sQuery(id+"F4.wireOp",EDGE,"E626"),sQuery(id+"F4.wireOp",EDGE,"E627"),sQuery(id+"F4.wireOp",EDGE,"E628"),sQuery(id+"F4.wireOp",EDGE,"E629"),sQuery(id+"F4.wireOp",EDGE,"E630"),sQuery(id+"F4.wireOp",EDGE,"E631"),sQuery(id+"F4.wireOp",EDGE,"E632"),sQuery(id+"F4.wireOp",EDGE,"E633"),sQuery(id+"F4.wireOp",EDGE,"E634"),sQuery(id+"F4.wireOp",EDGE,"E635"),sQuery(id+"F4.wireOp",EDGE,"E636"),sQuery(id+"F4.wireOp",EDGE,"E637"),sQuery(id+"F4.wireOp",EDGE,"E638"),sQuery(id+"F4.wireOp",EDGE,"E639"),sQuery(id+"F4.wireOp",EDGE,"E640"),sQuery(id+"F4.wireOp",EDGE,"E641"),sQuery(id+"F4.wireOp",EDGE,"E642"),sQuery(id+"F4.wireOp",EDGE,"E643"),sQuery(id+"F4.wireOp",EDGE,"E644"),sQuery(id+"F4.wireOp",EDGE,"E645"),sQuery(id+"F4.wireOp",EDGE,"E646"),sQuery(id+"F4.wireOp",EDGE,"E647"),sQuery(id+"F4.wireOp",EDGE,"E648"),sQuery(id+"F4.wireOp",EDGE,"E649"),sQuery(id+"F4.wireOp",EDGE,"E650"),sQuery(id+"F4.wireOp",EDGE,"E651"),sQuery(id+"F4.wireOp",EDGE,"E652"),sQuery(id+"F4.wireOp",EDGE,"E653"),sQuery(id+"F4.wireOp",EDGE,"E654"),sQuery(id+"F4.wireOp",EDGE,"E655"),sQuery(id+"F4.wireOp",EDGE,"E656"),sQuery(id+"F4.wireOp",EDGE,"E657"),sQuery(id+"F4.wireOp",EDGE,"E658"),sQuery(id+"F4.wireOp",EDGE,"E659"),sQuery(id+"F4.wireOp",EDGE,"E660"),sQuery(id+"F4.wireOp",EDGE,"E661"),sQuery(id+"F4.wireOp",EDGE,"E662"),sQuery(id+"F4.wireOp",EDGE,"E663"),sQuery(id+"F4.wireOp",EDGE,"E664"),sQuery(id+"F4.wireOp",EDGE,"E665"),sQuery(id+"F4.wireOp",EDGE,"E665"),sQuery(id+"F4.wireOp",EDGE,"E666"),sQuery(id+"F4.wireOp",EDGE,"E667"),sQuery(id+"F4.wireOp",EDGE,"E668"),sQuery(id+"F4.wireOp",EDGE,"E669"),sQuery(id+"F4.wireOp",EDGE,"E670"),sQuery(id+"F4.wireOp",EDGE,"E671"),sQuery(id+"F4.wireOp",EDGE,"E672"),sQuery(id+"F4.wireOp",EDGE,"E673"),sQuery(id+"F4.wireOp",EDGE,"E674"),sQuery(id+"F4.wireOp",EDGE,"E674"),sQuery(id+"F4.wireOp",EDGE,"E675"),sQuery(id+"F4.wireOp",EDGE,"E676"),sQuery(id+"F4.wireOp",EDGE,"E676"),sQuery(id+"F4.wireOp",EDGE,"E677"),sQuery(id+"F4.wireOp",EDGE,"E678"),sQuery(id+"F4.wireOp",EDGE,"E679"),sQuery(id+"F4.wireOp",EDGE,"E680"),sQuery(id+"F4.wireOp",EDGE,"E681"),sQuery(id+"F4.wireOp",EDGE,"E682"),sQuery(id+"F4.wireOp",EDGE,"E683"),sQuery(id+"F4.wireOp",EDGE,"E684"),sQuery(id+"F4.wireOp",EDGE,"E685"),sQuery(id+"F4.wireOp",EDGE,"E686"),sQuery(id+"F4.wireOp",EDGE,"E687"),sQuery(id+"F4.wireOp",EDGE,"E687"),sQuery(id+"F4.wireOp",EDGE,"E688"),sQuery(id+"F4.wireOp",EDGE,"E689"),sQuery(id+"F4.wireOp",EDGE,"E690"),sQuery(id+"F4.wireOp",EDGE,"E691"),sQuery(id+"F4.wireOp",EDGE,"E692"),sQuery(id+"F4.wireOp",EDGE,"E693"),sQuery(id+"F4.wireOp",EDGE,"E694"),sQuery(id+"F4.wireOp",EDGE,"E695"),sQuery(id+"F4.wireOp",EDGE,"E696"),sQuery(id+"F4.wireOp",EDGE,"E697"),sQuery(id+"F4.wireOp",EDGE,"E698"),sQuery(id+"F4.wireOp",EDGE,"E699"),sQuery(id+"F4.wireOp",EDGE,"E700"),sQuery(id+"F4.wireOp",EDGE,"E701"),sQuery(id+"F4.wireOp",EDGE,"E702"),sQuery(id+"F4.wireOp",EDGE,"E703"),sQuery(id+"F4.wireOp",EDGE,"E704"),sQuery(id+"F4.wireOp",EDGE,"E705"),sQuery(id+"F4.wireOp",EDGE,"E706"),sQuery(id+"F4.wireOp",EDGE,"E707"),sQuery(id+"F4.wireOp",EDGE,"E708"),sQuery(id+"F4.wireOp",EDGE,"E708"),sQuery(id+"F4.wireOp",EDGE,"E708")])]});
            var Q6;
            Q6=makeQuery(id+"F5.opExtrude","SWEPT_BODY",BODY,{"disambiguationData":[OSD([sQuery(id+"F4.wireOp",EDGE,"E709"),sQuery(id+"F4.wireOp",EDGE,"E710"),sQuery(id+"F4.wireOp",EDGE,"E711"),sQuery(id+"F4.wireOp",EDGE,"E712"),sQuery(id+"F4.wireOp",EDGE,"E713"),sQuery(id+"F4.wireOp",EDGE,"E714"),sQuery(id+"F4.wireOp",EDGE,"E715"),sQuery(id+"F4.wireOp",EDGE,"E716"),sQuery(id+"F4.wireOp",EDGE,"E717"),sQuery(id+"F4.wireOp",EDGE,"E718"),sQuery(id+"F4.wireOp",EDGE,"E719"),sQuery(id+"F4.wireOp",EDGE,"E720"),sQuery(id+"F4.wireOp",EDGE,"E721"),sQuery(id+"F4.wireOp",EDGE,"E722"),sQuery(id+"F4.wireOp",EDGE,"E723"),sQuery(id+"F4.wireOp",EDGE,"E723"),sQuery(id+"F4.wireOp",EDGE,"E724"),sQuery(id+"F4.wireOp",EDGE,"E725"),sQuery(id+"F4.wireOp",EDGE,"E726"),sQuery(id+"F4.wireOp",EDGE,"E727"),sQuery(id+"F4.wireOp",EDGE,"E728"),sQuery(id+"F4.wireOp",EDGE,"E729"),sQuery(id+"F4.wireOp",EDGE,"E730"),sQuery(id+"F4.wireOp",EDGE,"E731"),sQuery(id+"F4.wireOp",EDGE,"E732"),sQuery(id+"F4.wireOp",EDGE,"E733"),sQuery(id+"F4.wireOp",EDGE,"E734"),sQuery(id+"F4.wireOp",EDGE,"E735"),sQuery(id+"F4.wireOp",EDGE,"E736"),sQuery(id+"F4.wireOp",EDGE,"E737"),sQuery(id+"F4.wireOp",EDGE,"E738"),sQuery(id+"F4.wireOp",EDGE,"E739"),sQuery(id+"F4.wireOp",EDGE,"E740"),sQuery(id+"F4.wireOp",EDGE,"E741"),sQuery(id+"F4.wireOp",EDGE,"E742"),sQuery(id+"F4.wireOp",EDGE,"E743"),sQuery(id+"F4.wireOp",EDGE,"E744"),sQuery(id+"F4.wireOp",EDGE,"E745"),sQuery(id+"F4.wireOp",EDGE,"E746"),sQuery(id+"F4.wireOp",EDGE,"E747"),sQuery(id+"F4.wireOp",EDGE,"E748"),sQuery(id+"F4.wireOp",EDGE,"E749"),sQuery(id+"F4.wireOp",EDGE,"E750"),sQuery(id+"F4.wireOp",EDGE,"E751"),sQuery(id+"F4.wireOp",EDGE,"E752"),sQuery(id+"F4.wireOp",EDGE,"E753"),sQuery(id+"F4.wireOp",EDGE,"E754"),sQuery(id+"F4.wireOp",EDGE,"E755"),sQuery(id+"F4.wireOp",EDGE,"E756"),sQuery(id+"F4.wireOp",EDGE,"E757"),sQuery(id+"F4.wireOp",EDGE,"E758"),sQuery(id+"F4.wireOp",EDGE,"E758"),sQuery(id+"F4.wireOp",EDGE,"E758"),sQuery(id+"F4.wireOp",EDGE,"E759"),sQuery(id+"F4.wireOp",EDGE,"E760"),sQuery(id+"F4.wireOp",EDGE,"E760"),sQuery(id+"F4.wireOp",EDGE,"E761"),sQuery(id+"F4.wireOp",EDGE,"E762"),sQuery(id+"F4.wireOp",EDGE,"E763"),sQuery(id+"F4.wireOp",EDGE,"E764"),sQuery(id+"F4.wireOp",EDGE,"E765"),sQuery(id+"F4.wireOp",EDGE,"E766"),sQuery(id+"F4.wireOp",EDGE,"E767"),sQuery(id+"F4.wireOp",EDGE,"E768"),sQuery(id+"F4.wireOp",EDGE,"E768"),sQuery(id+"F4.wireOp",EDGE,"E768"),sQuery(id+"F4.wireOp",EDGE,"E769"),sQuery(id+"F4.wireOp",EDGE,"E770"),sQuery(id+"F4.wireOp",EDGE,"E771"),sQuery(id+"F4.wireOp",EDGE,"E772"),sQuery(id+"F4.wireOp",EDGE,"E773"),sQuery(id+"F4.wireOp",EDGE,"E774"),sQuery(id+"F4.wireOp",EDGE,"E775"),sQuery(id+"F4.wireOp",EDGE,"E776"),sQuery(id+"F4.wireOp",EDGE,"E777"),sQuery(id+"F4.wireOp",EDGE,"E778"),sQuery(id+"F4.wireOp",EDGE,"E779"),sQuery(id+"F4.wireOp",EDGE,"E780"),sQuery(id+"F4.wireOp",EDGE,"E781"),sQuery(id+"F4.wireOp",EDGE,"E782"),sQuery(id+"F4.wireOp",EDGE,"E783"),sQuery(id+"F4.wireOp",EDGE,"E784"),sQuery(id+"F4.wireOp",EDGE,"E785"),sQuery(id+"F4.wireOp",EDGE,"E786"),sQuery(id+"F4.wireOp",EDGE,"E787"),sQuery(id+"F4.wireOp",EDGE,"E788"),sQuery(id+"F4.wireOp",EDGE,"E789"),sQuery(id+"F4.wireOp",EDGE,"E790"),sQuery(id+"F4.wireOp",EDGE,"E791"),sQuery(id+"F4.wireOp",EDGE,"E792"),sQuery(id+"F4.wireOp",EDGE,"E793"),sQuery(id+"F4.wireOp",EDGE,"E794"),sQuery(id+"F4.wireOp",EDGE,"E795"),sQuery(id+"F4.wireOp",EDGE,"E796"),sQuery(id+"F4.wireOp",EDGE,"E797"),sQuery(id+"F4.wireOp",EDGE,"E798"),sQuery(id+"F4.wireOp",EDGE,"E799"),sQuery(id+"F4.wireOp",EDGE,"E800"),sQuery(id+"F4.wireOp",EDGE,"E801"),sQuery(id+"F4.wireOp",EDGE,"E802"),sQuery(id+"F4.wireOp",EDGE,"E803"),sQuery(id+"F4.wireOp",EDGE,"E804"),sQuery(id+"F4.wireOp",EDGE,"E805"),sQuery(id+"F4.wireOp",EDGE,"E806"),sQuery(id+"F4.wireOp",EDGE,"E807"),sQuery(id+"F4.wireOp",EDGE,"E808"),sQuery(id+"F4.wireOp",EDGE,"E809"),sQuery(id+"F4.wireOp",EDGE,"E810"),sQuery(id+"F4.wireOp",EDGE,"E811"),sQuery(id+"F4.wireOp",EDGE,"E812"),sQuery(id+"F4.wireOp",EDGE,"E813"),sQuery(id+"F4.wireOp",EDGE,"E814"),sQuery(id+"F4.wireOp",EDGE,"E815"),sQuery(id+"F4.wireOp",EDGE,"E816"),sQuery(id+"F4.wireOp",EDGE,"E817"),sQuery(id+"F4.wireOp",EDGE,"E818"),sQuery(id+"F4.wireOp",EDGE,"E819"),sQuery(id+"F4.wireOp",EDGE,"E820"),sQuery(id+"F4.wireOp",EDGE,"E821"),sQuery(id+"F4.wireOp",EDGE,"E822"),sQuery(id+"F4.wireOp",EDGE,"E823"),sQuery(id+"F4.wireOp",EDGE,"E824"),sQuery(id+"F4.wireOp",EDGE,"E825"),sQuery(id+"F4.wireOp",EDGE,"E826"),sQuery(id+"F4.wireOp",EDGE,"E827"),sQuery(id+"F4.wireOp",EDGE,"E828"),sQuery(id+"F4.wireOp",EDGE,"E829"),sQuery(id+"F4.wireOp",EDGE,"E830"),sQuery(id+"F4.wireOp",EDGE,"E831"),sQuery(id+"F4.wireOp",EDGE,"E832"),sQuery(id+"F4.wireOp",EDGE,"E833")])]});
            var Q7;
            Q7=makeQuery(id+"F5.opExtrude","SWEPT_BODY",BODY,{"disambiguationData":[OSD([sQuery(id+"F4.wireOp",EDGE,"E834"),sQuery(id+"F4.wireOp",EDGE,"E835"),sQuery(id+"F4.wireOp",EDGE,"E836"),sQuery(id+"F4.wireOp",EDGE,"E837"),sQuery(id+"F4.wireOp",EDGE,"E838"),sQuery(id+"F4.wireOp",EDGE,"E839"),sQuery(id+"F4.wireOp",EDGE,"E840"),sQuery(id+"F4.wireOp",EDGE,"E841"),sQuery(id+"F4.wireOp",EDGE,"E842"),sQuery(id+"F4.wireOp",EDGE,"E843"),sQuery(id+"F4.wireOp",EDGE,"E844"),sQuery(id+"F4.wireOp",EDGE,"E845"),sQuery(id+"F4.wireOp",EDGE,"E846"),sQuery(id+"F4.wireOp",EDGE,"E847"),sQuery(id+"F4.wireOp",EDGE,"E848"),sQuery(id+"F4.wireOp",EDGE,"E849"),sQuery(id+"F4.wireOp",EDGE,"E850"),sQuery(id+"F4.wireOp",EDGE,"E851"),sQuery(id+"F4.wireOp",EDGE,"E852"),sQuery(id+"F4.wireOp",EDGE,"E853"),sQuery(id+"F4.wireOp",EDGE,"E854"),sQuery(id+"F4.wireOp",EDGE,"E855"),sQuery(id+"F4.wireOp",EDGE,"E856"),sQuery(id+"F4.wireOp",EDGE,"E857"),sQuery(id+"F4.wireOp",EDGE,"E858"),sQuery(id+"F4.wireOp",EDGE,"E859"),sQuery(id+"F4.wireOp",EDGE,"E860"),sQuery(id+"F4.wireOp",EDGE,"E861"),sQuery(id+"F4.wireOp",EDGE,"E862"),sQuery(id+"F4.wireOp",EDGE,"E863"),sQuery(id+"F4.wireOp",EDGE,"E864"),sQuery(id+"F4.wireOp",EDGE,"E865"),sQuery(id+"F4.wireOp",EDGE,"E866"),sQuery(id+"F4.wireOp",EDGE,"E867"),sQuery(id+"F4.wireOp",EDGE,"E868"),sQuery(id+"F4.wireOp",EDGE,"E869"),sQuery(id+"F4.wireOp",EDGE,"E870"),sQuery(id+"F4.wireOp",EDGE,"E871"),sQuery(id+"F4.wireOp",EDGE,"E872"),sQuery(id+"F4.wireOp",EDGE,"E873"),sQuery(id+"F4.wireOp",EDGE,"E874"),sQuery(id+"F4.wireOp",EDGE,"E875"),sQuery(id+"F4.wireOp",EDGE,"E876"),sQuery(id+"F4.wireOp",EDGE,"E877"),sQuery(id+"F4.wireOp",EDGE,"E878"),sQuery(id+"F4.wireOp",EDGE,"E879"),sQuery(id+"F4.wireOp",EDGE,"E880"),sQuery(id+"F4.wireOp",EDGE,"E881"),sQuery(id+"F4.wireOp",EDGE,"E882"),sQuery(id+"F4.wireOp",EDGE,"E883"),sQuery(id+"F4.wireOp",EDGE,"E884"),sQuery(id+"F4.wireOp",EDGE,"E885"),sQuery(id+"F4.wireOp",EDGE,"E886"),sQuery(id+"F4.wireOp",EDGE,"E887"),sQuery(id+"F4.wireOp",EDGE,"E888"),sQuery(id+"F4.wireOp",EDGE,"E889"),sQuery(id+"F4.wireOp",EDGE,"E890"),sQuery(id+"F4.wireOp",EDGE,"E891"),sQuery(id+"F4.wireOp",EDGE,"E892"),sQuery(id+"F4.wireOp",EDGE,"E893"),sQuery(id+"F4.wireOp",EDGE,"E894"),sQuery(id+"F4.wireOp",EDGE,"E895"),sQuery(id+"F4.wireOp",EDGE,"E896"),sQuery(id+"F4.wireOp",EDGE,"E897"),sQuery(id+"F4.wireOp",EDGE,"E898"),sQuery(id+"F4.wireOp",EDGE,"E899"),sQuery(id+"F4.wireOp",EDGE,"E900"),sQuery(id+"F4.wireOp",EDGE,"E901"),sQuery(id+"F4.wireOp",EDGE,"E901"),sQuery(id+"F4.wireOp",EDGE,"E902"),sQuery(id+"F4.wireOp",EDGE,"E903"),sQuery(id+"F4.wireOp",EDGE,"E904"),sQuery(id+"F4.wireOp",EDGE,"E905"),sQuery(id+"F4.wireOp",EDGE,"E906"),sQuery(id+"F4.wireOp",EDGE,"E907"),sQuery(id+"F4.wireOp",EDGE,"E908"),sQuery(id+"F4.wireOp",EDGE,"E909"),sQuery(id+"F4.wireOp",EDGE,"E910"),sQuery(id+"F4.wireOp",EDGE,"E911"),sQuery(id+"F4.wireOp",EDGE,"E912")])]});
            var Q8;
            Q8=makeQuery(id+"F5.opExtrude","SWEPT_BODY",BODY,{"disambiguationData":[OSD([sQuery(id+"F4.wireOp",EDGE,"E913"),sQuery(id+"F4.wireOp",EDGE,"E914"),sQuery(id+"F4.wireOp",EDGE,"E915"),sQuery(id+"F4.wireOp",EDGE,"E916"),sQuery(id+"F4.wireOp",EDGE,"E917"),sQuery(id+"F4.wireOp",EDGE,"E918"),sQuery(id+"F4.wireOp",EDGE,"E919"),sQuery(id+"F4.wireOp",EDGE,"E920"),sQuery(id+"F4.wireOp",EDGE,"E921"),sQuery(id+"F4.wireOp",EDGE,"E922"),sQuery(id+"F4.wireOp",EDGE,"E923"),sQuery(id+"F4.wireOp",EDGE,"E924"),sQuery(id+"F4.wireOp",EDGE,"E925"),sQuery(id+"F4.wireOp",EDGE,"E926"),sQuery(id+"F4.wireOp",EDGE,"E927"),sQuery(id+"F4.wireOp",EDGE,"E928"),sQuery(id+"F4.wireOp",EDGE,"E929"),sQuery(id+"F4.wireOp",EDGE,"E930"),sQuery(id+"F4.wireOp",EDGE,"E931"),sQuery(id+"F4.wireOp",EDGE,"E932"),sQuery(id+"F4.wireOp",EDGE,"E933"),sQuery(id+"F4.wireOp",EDGE,"E934"),sQuery(id+"F4.wireOp",EDGE,"E935"),sQuery(id+"F4.wireOp",EDGE,"E936"),sQuery(id+"F4.wireOp",EDGE,"E937"),sQuery(id+"F4.wireOp",EDGE,"E938"),sQuery(id+"F4.wireOp",EDGE,"E939"),sQuery(id+"F4.wireOp",EDGE,"E940"),sQuery(id+"F4.wireOp",EDGE,"E941"),sQuery(id+"F4.wireOp",EDGE,"E942"),sQuery(id+"F4.wireOp",EDGE,"E943"),sQuery(id+"F4.wireOp",EDGE,"E944"),sQuery(id+"F4.wireOp",EDGE,"E945"),sQuery(id+"F4.wireOp",EDGE,"E946"),sQuery(id+"F4.wireOp",EDGE,"E947"),sQuery(id+"F4.wireOp",EDGE,"E947"),sQuery(id+"F4.wireOp",EDGE,"E948"),sQuery(id+"F4.wireOp",EDGE,"E949"),sQuery(id+"F4.wireOp",EDGE,"E950"),sQuery(id+"F4.wireOp",EDGE,"E951"),sQuery(id+"F4.wireOp",EDGE,"E952"),sQuery(id+"F4.wireOp",EDGE,"E953"),sQuery(id+"F4.wireOp",EDGE,"E954"),sQuery(id+"F4.wireOp",EDGE,"E955"),sQuery(id+"F4.wireOp",EDGE,"E956"),sQuery(id+"F4.wireOp",EDGE,"E957"),sQuery(id+"F4.wireOp",EDGE,"E958"),sQuery(id+"F4.wireOp",EDGE,"E959"),sQuery(id+"F4.wireOp",EDGE,"E959"),sQuery(id+"F4.wireOp",EDGE,"E960"),sQuery(id+"F4.wireOp",EDGE,"E961"),sQuery(id+"F4.wireOp",EDGE,"E962"),sQuery(id+"F4.wireOp",EDGE,"E963"),sQuery(id+"F4.wireOp",EDGE,"E964"),sQuery(id+"F4.wireOp",EDGE,"E965"),sQuery(id+"F4.wireOp",EDGE,"E966"),sQuery(id+"F4.wireOp",EDGE,"E967"),sQuery(id+"F4.wireOp",EDGE,"E968"),sQuery(id+"F4.wireOp",EDGE,"E969"),sQuery(id+"F4.wireOp",EDGE,"E970"),sQuery(id+"F4.wireOp",EDGE,"E971"),sQuery(id+"F4.wireOp",EDGE,"E972"),sQuery(id+"F4.wireOp",EDGE,"E973"),sQuery(id+"F4.wireOp",EDGE,"E974"),sQuery(id+"F4.wireOp",EDGE,"E975"),sQuery(id+"F4.wireOp",EDGE,"E976"),sQuery(id+"F4.wireOp",EDGE,"E977"),sQuery(id+"F4.wireOp",EDGE,"E978"),sQuery(id+"F4.wireOp",EDGE,"E979"),sQuery(id+"F4.wireOp",EDGE,"E980"),sQuery(id+"F4.wireOp",EDGE,"E981"),sQuery(id+"F4.wireOp",EDGE,"E982"),sQuery(id+"F4.wireOp",EDGE,"E983"),sQuery(id+"F4.wireOp",EDGE,"E984"),sQuery(id+"F4.wireOp",EDGE,"E985"),sQuery(id+"F4.wireOp",EDGE,"E986"),sQuery(id+"F4.wireOp",EDGE,"E987"),sQuery(id+"F4.wireOp",EDGE,"E988"),sQuery(id+"F4.wireOp",EDGE,"E989"),sQuery(id+"F4.wireOp",EDGE,"E990"),sQuery(id+"F4.wireOp",EDGE,"E991"),sQuery(id+"F4.wireOp",EDGE,"E992"),sQuery(id+"F4.wireOp",EDGE,"E992"),sQuery(id+"F4.wireOp",EDGE,"E993"),sQuery(id+"F4.wireOp",EDGE,"E994"),sQuery(id+"F4.wireOp",EDGE,"E995"),sQuery(id+"F4.wireOp",EDGE,"E996"),sQuery(id+"F4.wireOp",EDGE,"E997"),sQuery(id+"F4.wireOp",EDGE,"E998"),sQuery(id+"F4.wireOp",EDGE,"E999"),sQuery(id+"F4.wireOp",EDGE,"E1000"),sQuery(id+"F4.wireOp",EDGE,"E1001"),sQuery(id+"F4.wireOp",EDGE,"E1002"),sQuery(id+"F4.wireOp",EDGE,"E1003"),sQuery(id+"F4.wireOp",EDGE,"E1004"),sQuery(id+"F4.wireOp",EDGE,"E1005"),sQuery(id+"F4.wireOp",EDGE,"E1006"),sQuery(id+"F4.wireOp",EDGE,"E1007"),sQuery(id+"F4.wireOp",EDGE,"E1008"),sQuery(id+"F4.wireOp",EDGE,"E1009"),sQuery(id+"F4.wireOp",EDGE,"E1010"),sQuery(id+"F4.wireOp",EDGE,"E1011"),sQuery(id+"F4.wireOp",EDGE,"E1012"),sQuery(id+"F4.wireOp",EDGE,"E1013"),sQuery(id+"F4.wireOp",EDGE,"E1014"),sQuery(id+"F4.wireOp",EDGE,"E1015"),sQuery(id+"F4.wireOp",EDGE,"E1016"),sQuery(id+"F4.wireOp",EDGE,"E1017"),sQuery(id+"F4.wireOp",EDGE,"E1018"),sQuery(id+"F4.wireOp",EDGE,"E1019")])]});
            var Q9;
            Q9=makeQuery(id+"F5.opExtrude","SWEPT_BODY",BODY,{"disambiguationData":[OSD([sQuery(id+"F4.wireOp",EDGE,"E1020"),sQuery(id+"F4.wireOp",EDGE,"E1021"),sQuery(id+"F4.wireOp",EDGE,"E1022"),sQuery(id+"F4.wireOp",EDGE,"E1023"),sQuery(id+"F4.wireOp",EDGE,"E1024"),sQuery(id+"F4.wireOp",EDGE,"E1025"),sQuery(id+"F4.wireOp",EDGE,"E1026"),sQuery(id+"F4.wireOp",EDGE,"E1027"),sQuery(id+"F4.wireOp",EDGE,"E1028"),sQuery(id+"F4.wireOp",EDGE,"E1029"),sQuery(id+"F4.wireOp",EDGE,"E1030"),sQuery(id+"F4.wireOp",EDGE,"E1031"),sQuery(id+"F4.wireOp",EDGE,"E1031"),sQuery(id+"F4.wireOp",EDGE,"E1032"),sQuery(id+"F4.wireOp",EDGE,"E1033"),sQuery(id+"F4.wireOp",EDGE,"E1034"),sQuery(id+"F4.wireOp",EDGE,"E1035"),sQuery(id+"F4.wireOp",EDGE,"E1036"),sQuery(id+"F4.wireOp",EDGE,"E1037"),sQuery(id+"F4.wireOp",EDGE,"E1038"),sQuery(id+"F4.wireOp",EDGE,"E1039"),sQuery(id+"F4.wireOp",EDGE,"E1040"),sQuery(id+"F4.wireOp",EDGE,"E1041"),sQuery(id+"F4.wireOp",EDGE,"E1041"),sQuery(id+"F4.wireOp",EDGE,"E1042"),sQuery(id+"F4.wireOp",EDGE,"E1043"),sQuery(id+"F4.wireOp",EDGE,"E1044"),sQuery(id+"F4.wireOp",EDGE,"E1045"),sQuery(id+"F4.wireOp",EDGE,"E1046"),sQuery(id+"F4.wireOp",EDGE,"E1047"),sQuery(id+"F4.wireOp",EDGE,"E1048"),sQuery(id+"F4.wireOp",EDGE,"E1049"),sQuery(id+"F4.wireOp",EDGE,"E1049"),sQuery(id+"F4.wireOp",EDGE,"E1049"),sQuery(id+"F4.wireOp",EDGE,"E1049"),sQuery(id+"F4.wireOp",EDGE,"E1050"),sQuery(id+"F4.wireOp",EDGE,"E1051"),sQuery(id+"F4.wireOp",EDGE,"E1052"),sQuery(id+"F4.wireOp",EDGE,"E1053"),sQuery(id+"F4.wireOp",EDGE,"E1054"),sQuery(id+"F4.wireOp",EDGE,"E1055"),sQuery(id+"F4.wireOp",EDGE,"E1056"),sQuery(id+"F4.wireOp",EDGE,"E1057"),sQuery(id+"F4.wireOp",EDGE,"E1058"),sQuery(id+"F4.wireOp",EDGE,"E1059"),sQuery(id+"F4.wireOp",EDGE,"E1060"),sQuery(id+"F4.wireOp",EDGE,"E1061"),sQuery(id+"F4.wireOp",EDGE,"E1062"),sQuery(id+"F4.wireOp",EDGE,"E1063"),sQuery(id+"F4.wireOp",EDGE,"E1064"),sQuery(id+"F4.wireOp",EDGE,"E1065"),sQuery(id+"F4.wireOp",EDGE,"E1066"),sQuery(id+"F4.wireOp",EDGE,"E1067"),sQuery(id+"F4.wireOp",EDGE,"E1068"),sQuery(id+"F4.wireOp",EDGE,"E1069"),sQuery(id+"F4.wireOp",EDGE,"E1070"),sQuery(id+"F4.wireOp",EDGE,"E1071"),sQuery(id+"F4.wireOp",EDGE,"E1072"),sQuery(id+"F4.wireOp",EDGE,"E1073"),sQuery(id+"F4.wireOp",EDGE,"E1074"),sQuery(id+"F4.wireOp",EDGE,"E1075"),sQuery(id+"F4.wireOp",EDGE,"E1076"),sQuery(id+"F4.wireOp",EDGE,"E1077"),sQuery(id+"F4.wireOp",EDGE,"E1078"),sQuery(id+"F4.wireOp",EDGE,"E1079"),sQuery(id+"F4.wireOp",EDGE,"E1080"),sQuery(id+"F4.wireOp",EDGE,"E1081"),sQuery(id+"F4.wireOp",EDGE,"E1082"),sQuery(id+"F4.wireOp",EDGE,"E1083"),sQuery(id+"F4.wireOp",EDGE,"E1083"),sQuery(id+"F4.wireOp",EDGE,"E1084"),sQuery(id+"F4.wireOp",EDGE,"E1085"),sQuery(id+"F4.wireOp",EDGE,"E1086"),sQuery(id+"F4.wireOp",EDGE,"E1087"),sQuery(id+"F4.wireOp",EDGE,"E1088"),sQuery(id+"F4.wireOp",EDGE,"E1089"),sQuery(id+"F4.wireOp",EDGE,"E1090"),sQuery(id+"F4.wireOp",EDGE,"E1090"),sQuery(id+"F4.wireOp",EDGE,"E1091"),sQuery(id+"F4.wireOp",EDGE,"E1092"),sQuery(id+"F4.wireOp",EDGE,"E1093"),sQuery(id+"F4.wireOp",EDGE,"E1094"),sQuery(id+"F4.wireOp",EDGE,"E1095"),sQuery(id+"F4.wireOp",EDGE,"E1096"),sQuery(id+"F4.wireOp",EDGE,"E1097"),sQuery(id+"F4.wireOp",EDGE,"E1098"),sQuery(id+"F4.wireOp",EDGE,"E1099"),sQuery(id+"F4.wireOp",EDGE,"E1100"),sQuery(id+"F4.wireOp",EDGE,"E1101"),sQuery(id+"F4.wireOp",EDGE,"E1102"),sQuery(id+"F4.wireOp",EDGE,"E1103"),sQuery(id+"F4.wireOp",EDGE,"E1104"),sQuery(id+"F4.wireOp",EDGE,"E1105"),sQuery(id+"F4.wireOp",EDGE,"E1106"),sQuery(id+"F4.wireOp",EDGE,"E1107"),sQuery(id+"F4.wireOp",EDGE,"E1108"),sQuery(id+"F4.wireOp",EDGE,"E1109"),sQuery(id+"F4.wireOp",EDGE,"E1110"),sQuery(id+"F4.wireOp",EDGE,"E1110"),sQuery(id+"F4.wireOp",EDGE,"E1110"),sQuery(id+"F4.wireOp",EDGE,"E1111"),sQuery(id+"F4.wireOp",EDGE,"E1112"),sQuery(id+"F4.wireOp",EDGE,"E1113"),sQuery(id+"F4.wireOp",EDGE,"E1114"),sQuery(id+"F4.wireOp",EDGE,"E1115"),sQuery(id+"F4.wireOp",EDGE,"E1116"),sQuery(id+"F4.wireOp",EDGE,"E1117"),sQuery(id+"F4.wireOp",EDGE,"E1118"),sQuery(id+"F4.wireOp",EDGE,"E1119"),sQuery(id+"F4.wireOp",EDGE,"E1120")])]});
            var Q10;
            Q10=makeQuery(id+"F5.opExtrude","SWEPT_BODY",BODY,{"disambiguationData":[OSD([sQuery(id+"F4.wireOp",EDGE,"E1121"),sQuery(id+"F4.wireOp",EDGE,"E1122"),sQuery(id+"F4.wireOp",EDGE,"E1123"),sQuery(id+"F4.wireOp",EDGE,"E1124"),sQuery(id+"F4.wireOp",EDGE,"E1125"),sQuery(id+"F4.wireOp",EDGE,"E1126"),sQuery(id+"F4.wireOp",EDGE,"E1127"),sQuery(id+"F4.wireOp",EDGE,"E1128"),sQuery(id+"F4.wireOp",EDGE,"E1129"),sQuery(id+"F4.wireOp",EDGE,"E1130"),sQuery(id+"F4.wireOp",EDGE,"E1131"),sQuery(id+"F4.wireOp",EDGE,"E1132"),sQuery(id+"F4.wireOp",EDGE,"E1133"),sQuery(id+"F4.wireOp",EDGE,"E1134"),sQuery(id+"F4.wireOp",EDGE,"E1135"),sQuery(id+"F4.wireOp",EDGE,"E1136")])]});
            var Q11;
            Q11=qCreatedBy(makeId("Origin.pointOp"),VERTEX);
            transform(context, id + "F6", {"entities" : qUnion([Q0, Q1, Q2, Q3, Q4, Q5, Q6, Q7, Q8, Q9, Q10]), "transformType" : TransformType.SCALE_UNIFORMLY, "scale" : 21, "scalePoint" : qUnion([Q11]), "makeCopy" : false});
        }
        {
            var Q0;
            Q0=qCreatedBy(makeId("Right.planeOp"),FACE);
            var sketch = newSketch(context, id + "F7", { "sketchPlane" : qUnion([Q0])});
            skLineSegment(sketch, "E1137", {"start": v(0, 29.93) * mm, "end": v(0, 0) * mm, "construction": true});
            skSolve(sketch);
        }
        {
            var Q0;
            Q0=makeQuery(id+"F5.opExtrude","SWEPT_BODY",BODY,{"disambiguationData":[OSD([sQuery(id+"F4.wireOp",EDGE,"E4"),sQuery(id+"F4.wireOp",EDGE,"E5"),sQuery(id+"F4.wireOp",EDGE,"E6"),sQuery(id+"F4.wireOp",EDGE,"E7"),sQuery(id+"F4.wireOp",EDGE,"E8"),sQuery(id+"F4.wireOp",EDGE,"E9"),sQuery(id+"F4.wireOp",EDGE,"E10"),sQuery(id+"F4.wireOp",EDGE,"E11"),sQuery(id+"F4.wireOp",EDGE,"E12"),sQuery(id+"F4.wireOp",EDGE,"E13"),sQuery(id+"F4.wireOp",EDGE,"E14"),sQuery(id+"F4.wireOp",EDGE,"E15"),sQuery(id+"F4.wireOp",EDGE,"E16"),sQuery(id+"F4.wireOp",EDGE,"E17"),sQuery(id+"F4.wireOp",EDGE,"E18"),sQuery(id+"F4.wireOp",EDGE,"E19"),sQuery(id+"F4.wireOp",EDGE,"E20"),sQuery(id+"F4.wireOp",EDGE,"E21"),sQuery(id+"F4.wireOp",EDGE,"E22"),sQuery(id+"F4.wireOp",EDGE,"E23"),sQuery(id+"F4.wireOp",EDGE,"E24"),sQuery(id+"F4.wireOp",EDGE,"E25"),sQuery(id+"F4.wireOp",EDGE,"E26"),sQuery(id+"F4.wireOp",EDGE,"E26"),sQuery(id+"F4.wireOp",EDGE,"E27"),sQuery(id+"F4.wireOp",EDGE,"E28"),sQuery(id+"F4.wireOp",EDGE,"E29"),sQuery(id+"F4.wireOp",EDGE,"E30"),sQuery(id+"F4.wireOp",EDGE,"E31"),sQuery(id+"F4.wireOp",EDGE,"E32"),sQuery(id+"F4.wireOp",EDGE,"E33"),sQuery(id+"F4.wireOp",EDGE,"E34"),sQuery(id+"F4.wireOp",EDGE,"E35"),sQuery(id+"F4.wireOp",EDGE,"E36"),sQuery(id+"F4.wireOp",EDGE,"E37"),sQuery(id+"F4.wireOp",EDGE,"E38"),sQuery(id+"F4.wireOp",EDGE,"E39"),sQuery(id+"F4.wireOp",EDGE,"E40"),sQuery(id+"F4.wireOp",EDGE,"E41"),sQuery(id+"F4.wireOp",EDGE,"E42"),sQuery(id+"F4.wireOp",EDGE,"E43"),sQuery(id+"F4.wireOp",EDGE,"E44"),sQuery(id+"F4.wireOp",EDGE,"E45"),sQuery(id+"F4.wireOp",EDGE,"E46"),sQuery(id+"F4.wireOp",EDGE,"E47"),sQuery(id+"F4.wireOp",EDGE,"E48"),sQuery(id+"F4.wireOp",EDGE,"E49"),sQuery(id+"F4.wireOp",EDGE,"E50"),sQuery(id+"F4.wireOp",EDGE,"E51"),sQuery(id+"F4.wireOp",EDGE,"E52"),sQuery(id+"F4.wireOp",EDGE,"E53"),sQuery(id+"F4.wireOp",EDGE,"E54"),sQuery(id+"F4.wireOp",EDGE,"E55"),sQuery(id+"F4.wireOp",EDGE,"E56"),sQuery(id+"F4.wireOp",EDGE,"E57"),sQuery(id+"F4.wireOp",EDGE,"E58"),sQuery(id+"F4.wireOp",EDGE,"E59"),sQuery(id+"F4.wireOp",EDGE,"E60"),sQuery(id+"F4.wireOp",EDGE,"E61"),sQuery(id+"F4.wireOp",EDGE,"E62"),sQuery(id+"F4.wireOp",EDGE,"E63"),sQuery(id+"F4.wireOp",EDGE,"E64"),sQuery(id+"F4.wireOp",EDGE,"E65"),sQuery(id+"F4.wireOp",EDGE,"E65"),sQuery(id+"F4.wireOp",EDGE,"E66"),sQuery(id+"F4.wireOp",EDGE,"E67"),sQuery(id+"F4.wireOp",EDGE,"E68"),sQuery(id+"F4.wireOp",EDGE,"E69"),sQuery(id+"F4.wireOp",EDGE,"E70"),sQuery(id+"F4.wireOp",EDGE,"E71"),sQuery(id+"F4.wireOp",EDGE,"E72"),sQuery(id+"F4.wireOp",EDGE,"E73"),sQuery(id+"F4.wireOp",EDGE,"E74"),sQuery(id+"F4.wireOp",EDGE,"E75"),sQuery(id+"F4.wireOp",EDGE,"E76"),sQuery(id+"F4.wireOp",EDGE,"E77"),sQuery(id+"F4.wireOp",EDGE,"E78"),sQuery(id+"F4.wireOp",EDGE,"E79"),sQuery(id+"F4.wireOp",EDGE,"E80"),sQuery(id+"F4.wireOp",EDGE,"E81"),sQuery(id+"F4.wireOp",EDGE,"E82"),sQuery(id+"F4.wireOp",EDGE,"E83"),sQuery(id+"F4.wireOp",EDGE,"E84"),sQuery(id+"F4.wireOp",EDGE,"E85"),sQuery(id+"F4.wireOp",EDGE,"E86"),sQuery(id+"F4.wireOp",EDGE,"E87"),sQuery(id+"F4.wireOp",EDGE,"E88"),sQuery(id+"F4.wireOp",EDGE,"E89"),sQuery(id+"F4.wireOp",EDGE,"E90"),sQuery(id+"F4.wireOp",EDGE,"E91"),sQuery(id+"F4.wireOp",EDGE,"E92"),sQuery(id+"F4.wireOp",EDGE,"E93"),sQuery(id+"F4.wireOp",EDGE,"E94"),sQuery(id+"F4.wireOp",EDGE,"E95"),sQuery(id+"F4.wireOp",EDGE,"E96"),sQuery(id+"F4.wireOp",EDGE,"E97"),sQuery(id+"F4.wireOp",EDGE,"E98"),sQuery(id+"F4.wireOp",EDGE,"E99"),sQuery(id+"F4.wireOp",EDGE,"E100"),sQuery(id+"F4.wireOp",EDGE,"E101"),sQuery(id+"F4.wireOp",EDGE,"E102"),sQuery(id+"F4.wireOp",EDGE,"E103"),sQuery(id+"F4.wireOp",EDGE,"E104"),sQuery(id+"F4.wireOp",EDGE,"E105"),sQuery(id+"F4.wireOp",EDGE,"E106"),sQuery(id+"F4.wireOp",EDGE,"E107"),sQuery(id+"F4.wireOp",EDGE,"E108"),sQuery(id+"F4.wireOp",EDGE,"E109"),sQuery(id+"F4.wireOp",EDGE,"E110"),sQuery(id+"F4.wireOp",EDGE,"E111"),sQuery(id+"F4.wireOp",EDGE,"E112"),sQuery(id+"F4.wireOp",EDGE,"E113"),sQuery(id+"F4.wireOp",EDGE,"E114"),sQuery(id+"F4.wireOp",EDGE,"E114"),sQuery(id+"F4.wireOp",EDGE,"E115"),sQuery(id+"F4.wireOp",EDGE,"E116")])]});
            var Q1;
            Q1=makeQuery(id+"F5.opExtrude","SWEPT_BODY",BODY,{"disambiguationData":[OSD([sQuery(id+"F4.wireOp",EDGE,"E117"),sQuery(id+"F4.wireOp",EDGE,"E118"),sQuery(id+"F4.wireOp",EDGE,"E119"),sQuery(id+"F4.wireOp",EDGE,"E120"),sQuery(id+"F4.wireOp",EDGE,"E121"),sQuery(id+"F4.wireOp",EDGE,"E122"),sQuery(id+"F4.wireOp",EDGE,"E123"),sQuery(id+"F4.wireOp",EDGE,"E124"),sQuery(id+"F4.wireOp",EDGE,"E125"),sQuery(id+"F4.wireOp",EDGE,"E126"),sQuery(id+"F4.wireOp",EDGE,"E127"),sQuery(id+"F4.wireOp",EDGE,"E128"),sQuery(id+"F4.wireOp",EDGE,"E129"),sQuery(id+"F4.wireOp",EDGE,"E130"),sQuery(id+"F4.wireOp",EDGE,"E131"),sQuery(id+"F4.wireOp",EDGE,"E132"),sQuery(id+"F4.wireOp",EDGE,"E133"),sQuery(id+"F4.wireOp",EDGE,"E133"),sQuery(id+"F4.wireOp",EDGE,"E134"),sQuery(id+"F4.wireOp",EDGE,"E135"),sQuery(id+"F4.wireOp",EDGE,"E136"),sQuery(id+"F4.wireOp",EDGE,"E137"),sQuery(id+"F4.wireOp",EDGE,"E138"),sQuery(id+"F4.wireOp",EDGE,"E139"),sQuery(id+"F4.wireOp",EDGE,"E140"),sQuery(id+"F4.wireOp",EDGE,"E141"),sQuery(id+"F4.wireOp",EDGE,"E142"),sQuery(id+"F4.wireOp",EDGE,"E143"),sQuery(id+"F4.wireOp",EDGE,"E144"),sQuery(id+"F4.wireOp",EDGE,"E145"),sQuery(id+"F4.wireOp",EDGE,"E146"),sQuery(id+"F4.wireOp",EDGE,"E147"),sQuery(id+"F4.wireOp",EDGE,"E148"),sQuery(id+"F4.wireOp",EDGE,"E149"),sQuery(id+"F4.wireOp",EDGE,"E150"),sQuery(id+"F4.wireOp",EDGE,"E151"),sQuery(id+"F4.wireOp",EDGE,"E152"),sQuery(id+"F4.wireOp",EDGE,"E153"),sQuery(id+"F4.wireOp",EDGE,"E154"),sQuery(id+"F4.wireOp",EDGE,"E155"),sQuery(id+"F4.wireOp",EDGE,"E156"),sQuery(id+"F4.wireOp",EDGE,"E157"),sQuery(id+"F4.wireOp",EDGE,"E158"),sQuery(id+"F4.wireOp",EDGE,"E159"),sQuery(id+"F4.wireOp",EDGE,"E160"),sQuery(id+"F4.wireOp",EDGE,"E161"),sQuery(id+"F4.wireOp",EDGE,"E162"),sQuery(id+"F4.wireOp",EDGE,"E162"),sQuery(id+"F4.wireOp",EDGE,"E162"),sQuery(id+"F4.wireOp",EDGE,"E163"),sQuery(id+"F4.wireOp",EDGE,"E164"),sQuery(id+"F4.wireOp",EDGE,"E165"),sQuery(id+"F4.wireOp",EDGE,"E166"),sQuery(id+"F4.wireOp",EDGE,"E167"),sQuery(id+"F4.wireOp",EDGE,"E168"),sQuery(id+"F4.wireOp",EDGE,"E169"),sQuery(id+"F4.wireOp",EDGE,"E170"),sQuery(id+"F4.wireOp",EDGE,"E171"),sQuery(id+"F4.wireOp",EDGE,"E171"),sQuery(id+"F4.wireOp",EDGE,"E172"),sQuery(id+"F4.wireOp",EDGE,"E173"),sQuery(id+"F4.wireOp",EDGE,"E174"),sQuery(id+"F4.wireOp",EDGE,"E175"),sQuery(id+"F4.wireOp",EDGE,"E176"),sQuery(id+"F4.wireOp",EDGE,"E177"),sQuery(id+"F4.wireOp",EDGE,"E178"),sQuery(id+"F4.wireOp",EDGE,"E179"),sQuery(id+"F4.wireOp",EDGE,"E180"),sQuery(id+"F4.wireOp",EDGE,"E181"),sQuery(id+"F4.wireOp",EDGE,"E182"),sQuery(id+"F4.wireOp",EDGE,"E183"),sQuery(id+"F4.wireOp",EDGE,"E184"),sQuery(id+"F4.wireOp",EDGE,"E185"),sQuery(id+"F4.wireOp",EDGE,"E186"),sQuery(id+"F4.wireOp",EDGE,"E187"),sQuery(id+"F4.wireOp",EDGE,"E188"),sQuery(id+"F4.wireOp",EDGE,"E189"),sQuery(id+"F4.wireOp",EDGE,"E190"),sQuery(id+"F4.wireOp",EDGE,"E191"),sQuery(id+"F4.wireOp",EDGE,"E192"),sQuery(id+"F4.wireOp",EDGE,"E193"),sQuery(id+"F4.wireOp",EDGE,"E194"),sQuery(id+"F4.wireOp",EDGE,"E195"),sQuery(id+"F4.wireOp",EDGE,"E196"),sQuery(id+"F4.wireOp",EDGE,"E197"),sQuery(id+"F4.wireOp",EDGE,"E198"),sQuery(id+"F4.wireOp",EDGE,"E199"),sQuery(id+"F4.wireOp",EDGE,"E200"),sQuery(id+"F4.wireOp",EDGE,"E201"),sQuery(id+"F4.wireOp",EDGE,"E202"),sQuery(id+"F4.wireOp",EDGE,"E203"),sQuery(id+"F4.wireOp",EDGE,"E204"),sQuery(id+"F4.wireOp",EDGE,"E205"),sQuery(id+"F4.wireOp",EDGE,"E206"),sQuery(id+"F4.wireOp",EDGE,"E207"),sQuery(id+"F4.wireOp",EDGE,"E208"),sQuery(id+"F4.wireOp",EDGE,"E209"),sQuery(id+"F4.wireOp",EDGE,"E210"),sQuery(id+"F4.wireOp",EDGE,"E211"),sQuery(id+"F4.wireOp",EDGE,"E212"),sQuery(id+"F4.wireOp",EDGE,"E213"),sQuery(id+"F4.wireOp",EDGE,"E214"),sQuery(id+"F4.wireOp",EDGE,"E215"),sQuery(id+"F4.wireOp",EDGE,"E216"),sQuery(id+"F4.wireOp",EDGE,"E217"),sQuery(id+"F4.wireOp",EDGE,"E218"),sQuery(id+"F4.wireOp",EDGE,"E219"),sQuery(id+"F4.wireOp",EDGE,"E220"),sQuery(id+"F4.wireOp",EDGE,"E221"),sQuery(id+"F4.wireOp",EDGE,"E222"),sQuery(id+"F4.wireOp",EDGE,"E223"),sQuery(id+"F4.wireOp",EDGE,"E224"),sQuery(id+"F4.wireOp",EDGE,"E225"),sQuery(id+"F4.wireOp",EDGE,"E226"),sQuery(id+"F4.wireOp",EDGE,"E227"),sQuery(id+"F4.wireOp",EDGE,"E228"),sQuery(id+"F4.wireOp",EDGE,"E229"),sQuery(id+"F4.wireOp",EDGE,"E230"),sQuery(id+"F4.wireOp",EDGE,"E231"),sQuery(id+"F4.wireOp",EDGE,"E232"),sQuery(id+"F4.wireOp",EDGE,"E233"),sQuery(id+"F4.wireOp",EDGE,"E234"),sQuery(id+"F4.wireOp",EDGE,"E235"),sQuery(id+"F4.wireOp",EDGE,"E236"),sQuery(id+"F4.wireOp",EDGE,"E237"),sQuery(id+"F4.wireOp",EDGE,"E238"),sQuery(id+"F4.wireOp",EDGE,"E239"),sQuery(id+"F4.wireOp",EDGE,"E240"),sQuery(id+"F4.wireOp",EDGE,"E241"),sQuery(id+"F4.wireOp",EDGE,"E242"),sQuery(id+"F4.wireOp",EDGE,"E243"),sQuery(id+"F4.wireOp",EDGE,"E244"),sQuery(id+"F4.wireOp",EDGE,"E245"),sQuery(id+"F4.wireOp",EDGE,"E246"),sQuery(id+"F4.wireOp",EDGE,"E247"),sQuery(id+"F4.wireOp",EDGE,"E248"),sQuery(id+"F4.wireOp",EDGE,"E249"),sQuery(id+"F4.wireOp",EDGE,"E250"),sQuery(id+"F4.wireOp",EDGE,"E250"),sQuery(id+"F4.wireOp",EDGE,"E251"),sQuery(id+"F4.wireOp",EDGE,"E252"),sQuery(id+"F4.wireOp",EDGE,"E253"),sQuery(id+"F4.wireOp",EDGE,"E254"),sQuery(id+"F4.wireOp",EDGE,"E255"),sQuery(id+"F4.wireOp",EDGE,"E256"),sQuery(id+"F4.wireOp",EDGE,"E257"),sQuery(id+"F4.wireOp",EDGE,"E258"),sQuery(id+"F4.wireOp",EDGE,"E259"),sQuery(id+"F4.wireOp",EDGE,"E260"),sQuery(id+"F4.wireOp",EDGE,"E261"),sQuery(id+"F4.wireOp",EDGE,"E262"),sQuery(id+"F4.wireOp",EDGE,"E262"),sQuery(id+"F4.wireOp",EDGE,"E262"),sQuery(id+"F4.wireOp",EDGE,"E263"),sQuery(id+"F4.wireOp",EDGE,"E264"),sQuery(id+"F4.wireOp",EDGE,"E265"),sQuery(id+"F4.wireOp",EDGE,"E266"),sQuery(id+"F4.wireOp",EDGE,"E267"),sQuery(id+"F4.wireOp",EDGE,"E268"),sQuery(id+"F4.wireOp",EDGE,"E269"),sQuery(id+"F4.wireOp",EDGE,"E270"),sQuery(id+"F4.wireOp",EDGE,"E271"),sQuery(id+"F4.wireOp",EDGE,"E272"),sQuery(id+"F4.wireOp",EDGE,"E273"),sQuery(id+"F4.wireOp",EDGE,"E274"),sQuery(id+"F4.wireOp",EDGE,"E275"),sQuery(id+"F4.wireOp",EDGE,"E276"),sQuery(id+"F4.wireOp",EDGE,"E277"),sQuery(id+"F4.wireOp",EDGE,"E278"),sQuery(id+"F4.wireOp",EDGE,"E279"),sQuery(id+"F4.wireOp",EDGE,"E280"),sQuery(id+"F4.wireOp",EDGE,"E281"),sQuery(id+"F4.wireOp",EDGE,"E282"),sQuery(id+"F4.wireOp",EDGE,"E283"),sQuery(id+"F4.wireOp",EDGE,"E284"),sQuery(id+"F4.wireOp",EDGE,"E285"),sQuery(id+"F4.wireOp",EDGE,"E286"),sQuery(id+"F4.wireOp",EDGE,"E287"),sQuery(id+"F4.wireOp",EDGE,"E288")])]});
            var Q2;
            Q2=makeQuery(id+"F5.opExtrude","SWEPT_BODY",BODY,{"disambiguationData":[OSD([sQuery(id+"F4.wireOp",EDGE,"E289"),sQuery(id+"F4.wireOp",EDGE,"E290"),sQuery(id+"F4.wireOp",EDGE,"E291"),sQuery(id+"F4.wireOp",EDGE,"E292"),sQuery(id+"F4.wireOp",EDGE,"E293"),sQuery(id+"F4.wireOp",EDGE,"E294"),sQuery(id+"F4.wireOp",EDGE,"E295"),sQuery(id+"F4.wireOp",EDGE,"E296"),sQuery(id+"F4.wireOp",EDGE,"E297"),sQuery(id+"F4.wireOp",EDGE,"E298"),sQuery(id+"F4.wireOp",EDGE,"E299"),sQuery(id+"F4.wireOp",EDGE,"E300"),sQuery(id+"F4.wireOp",EDGE,"E301"),sQuery(id+"F4.wireOp",EDGE,"E302"),sQuery(id+"F4.wireOp",EDGE,"E303"),sQuery(id+"F4.wireOp",EDGE,"E304"),sQuery(id+"F4.wireOp",EDGE,"E305"),sQuery(id+"F4.wireOp",EDGE,"E306"),sQuery(id+"F4.wireOp",EDGE,"E307"),sQuery(id+"F4.wireOp",EDGE,"E308"),sQuery(id+"F4.wireOp",EDGE,"E309"),sQuery(id+"F4.wireOp",EDGE,"E310"),sQuery(id+"F4.wireOp",EDGE,"E311"),sQuery(id+"F4.wireOp",EDGE,"E312"),sQuery(id+"F4.wireOp",EDGE,"E313"),sQuery(id+"F4.wireOp",EDGE,"E314"),sQuery(id+"F4.wireOp",EDGE,"E315"),sQuery(id+"F4.wireOp",EDGE,"E316"),sQuery(id+"F4.wireOp",EDGE,"E317"),sQuery(id+"F4.wireOp",EDGE,"E318"),sQuery(id+"F4.wireOp",EDGE,"E319"),sQuery(id+"F4.wireOp",EDGE,"E320"),sQuery(id+"F4.wireOp",EDGE,"E321"),sQuery(id+"F4.wireOp",EDGE,"E322"),sQuery(id+"F4.wireOp",EDGE,"E323"),sQuery(id+"F4.wireOp",EDGE,"E324"),sQuery(id+"F4.wireOp",EDGE,"E325"),sQuery(id+"F4.wireOp",EDGE,"E326"),sQuery(id+"F4.wireOp",EDGE,"E327"),sQuery(id+"F4.wireOp",EDGE,"E328"),sQuery(id+"F4.wireOp",EDGE,"E329"),sQuery(id+"F4.wireOp",EDGE,"E330"),sQuery(id+"F4.wireOp",EDGE,"E331"),sQuery(id+"F4.wireOp",EDGE,"E332"),sQuery(id+"F4.wireOp",EDGE,"E333"),sQuery(id+"F4.wireOp",EDGE,"E334"),sQuery(id+"F4.wireOp",EDGE,"E335"),sQuery(id+"F4.wireOp",EDGE,"E336"),sQuery(id+"F4.wireOp",EDGE,"E337"),sQuery(id+"F4.wireOp",EDGE,"E338"),sQuery(id+"F4.wireOp",EDGE,"E339"),sQuery(id+"F4.wireOp",EDGE,"E340"),sQuery(id+"F4.wireOp",EDGE,"E341"),sQuery(id+"F4.wireOp",EDGE,"E342"),sQuery(id+"F4.wireOp",EDGE,"E343"),sQuery(id+"F4.wireOp",EDGE,"E344"),sQuery(id+"F4.wireOp",EDGE,"E345"),sQuery(id+"F4.wireOp",EDGE,"E346"),sQuery(id+"F4.wireOp",EDGE,"E346"),sQuery(id+"F4.wireOp",EDGE,"E347"),sQuery(id+"F4.wireOp",EDGE,"E348"),sQuery(id+"F4.wireOp",EDGE,"E349"),sQuery(id+"F4.wireOp",EDGE,"E350"),sQuery(id+"F4.wireOp",EDGE,"E351"),sQuery(id+"F4.wireOp",EDGE,"E352"),sQuery(id+"F4.wireOp",EDGE,"E353"),sQuery(id+"F4.wireOp",EDGE,"E354"),sQuery(id+"F4.wireOp",EDGE,"E355"),sQuery(id+"F4.wireOp",EDGE,"E356"),sQuery(id+"F4.wireOp",EDGE,"E357"),sQuery(id+"F4.wireOp",EDGE,"E358"),sQuery(id+"F4.wireOp",EDGE,"E359"),sQuery(id+"F4.wireOp",EDGE,"E360"),sQuery(id+"F4.wireOp",EDGE,"E361"),sQuery(id+"F4.wireOp",EDGE,"E362"),sQuery(id+"F4.wireOp",EDGE,"E363"),sQuery(id+"F4.wireOp",EDGE,"E364"),sQuery(id+"F4.wireOp",EDGE,"E365"),sQuery(id+"F4.wireOp",EDGE,"E366"),sQuery(id+"F4.wireOp",EDGE,"E367"),sQuery(id+"F4.wireOp",EDGE,"E368"),sQuery(id+"F4.wireOp",EDGE,"E369"),sQuery(id+"F4.wireOp",EDGE,"E370"),sQuery(id+"F4.wireOp",EDGE,"E371"),sQuery(id+"F4.wireOp",EDGE,"E371"),sQuery(id+"F4.wireOp",EDGE,"E372"),sQuery(id+"F4.wireOp",EDGE,"E373"),sQuery(id+"F4.wireOp",EDGE,"E374"),sQuery(id+"F4.wireOp",EDGE,"E375"),sQuery(id+"F4.wireOp",EDGE,"E376"),sQuery(id+"F4.wireOp",EDGE,"E377"),sQuery(id+"F4.wireOp",EDGE,"E378"),sQuery(id+"F4.wireOp",EDGE,"E379"),sQuery(id+"F4.wireOp",EDGE,"E380"),sQuery(id+"F4.wireOp",EDGE,"E381"),sQuery(id+"F4.wireOp",EDGE,"E382"),sQuery(id+"F4.wireOp",EDGE,"E383"),sQuery(id+"F4.wireOp",EDGE,"E384"),sQuery(id+"F4.wireOp",EDGE,"E385"),sQuery(id+"F4.wireOp",EDGE,"E386"),sQuery(id+"F4.wireOp",EDGE,"E387"),sQuery(id+"F4.wireOp",EDGE,"E388"),sQuery(id+"F4.wireOp",EDGE,"E389"),sQuery(id+"F4.wireOp",EDGE,"E390"),sQuery(id+"F4.wireOp",EDGE,"E391"),sQuery(id+"F4.wireOp",EDGE,"E392"),sQuery(id+"F4.wireOp",EDGE,"E392"),sQuery(id+"F4.wireOp",EDGE,"E393"),sQuery(id+"F4.wireOp",EDGE,"E394"),sQuery(id+"F4.wireOp",EDGE,"E395"),sQuery(id+"F4.wireOp",EDGE,"E396"),sQuery(id+"F4.wireOp",EDGE,"E397"),sQuery(id+"F4.wireOp",EDGE,"E398"),sQuery(id+"F4.wireOp",EDGE,"E399"),sQuery(id+"F4.wireOp",EDGE,"E400"),sQuery(id+"F4.wireOp",EDGE,"E401"),sQuery(id+"F4.wireOp",EDGE,"E402"),sQuery(id+"F4.wireOp",EDGE,"E403"),sQuery(id+"F4.wireOp",EDGE,"E404"),sQuery(id+"F4.wireOp",EDGE,"E405"),sQuery(id+"F4.wireOp",EDGE,"E406"),sQuery(id+"F4.wireOp",EDGE,"E407"),sQuery(id+"F4.wireOp",EDGE,"E408"),sQuery(id+"F4.wireOp",EDGE,"E409"),sQuery(id+"F4.wireOp",EDGE,"E410"),sQuery(id+"F4.wireOp",EDGE,"E411"),sQuery(id+"F4.wireOp",EDGE,"E412"),sQuery(id+"F4.wireOp",EDGE,"E413"),sQuery(id+"F4.wireOp",EDGE,"E414"),sQuery(id+"F4.wireOp",EDGE,"E415"),sQuery(id+"F4.wireOp",EDGE,"E416"),sQuery(id+"F4.wireOp",EDGE,"E417"),sQuery(id+"F4.wireOp",EDGE,"E418"),sQuery(id+"F4.wireOp",EDGE,"E419"),sQuery(id+"F4.wireOp",EDGE,"E420"),sQuery(id+"F4.wireOp",EDGE,"E421"),sQuery(id+"F4.wireOp",EDGE,"E422"),sQuery(id+"F4.wireOp",EDGE,"E423"),sQuery(id+"F4.wireOp",EDGE,"E424"),sQuery(id+"F4.wireOp",EDGE,"E425"),sQuery(id+"F4.wireOp",EDGE,"E426"),sQuery(id+"F4.wireOp",EDGE,"E427"),sQuery(id+"F4.wireOp",EDGE,"E428"),sQuery(id+"F4.wireOp",EDGE,"E429"),sQuery(id+"F4.wireOp",EDGE,"E430"),sQuery(id+"F4.wireOp",EDGE,"E431"),sQuery(id+"F4.wireOp",EDGE,"E431"),sQuery(id+"F4.wireOp",EDGE,"E432"),sQuery(id+"F4.wireOp",EDGE,"E433"),sQuery(id+"F4.wireOp",EDGE,"E434"),sQuery(id+"F4.wireOp",EDGE,"E435"),sQuery(id+"F4.wireOp",EDGE,"E436"),sQuery(id+"F4.wireOp",EDGE,"E436"),sQuery(id+"F4.wireOp",EDGE,"E437"),sQuery(id+"F4.wireOp",EDGE,"E438"),sQuery(id+"F4.wireOp",EDGE,"E439"),sQuery(id+"F4.wireOp",EDGE,"E440"),sQuery(id+"F4.wireOp",EDGE,"E441"),sQuery(id+"F4.wireOp",EDGE,"E442"),sQuery(id+"F4.wireOp",EDGE,"E443"),sQuery(id+"F4.wireOp",EDGE,"E444"),sQuery(id+"F4.wireOp",EDGE,"E445"),sQuery(id+"F4.wireOp",EDGE,"E446"),sQuery(id+"F4.wireOp",EDGE,"E447"),sQuery(id+"F4.wireOp",EDGE,"E448"),sQuery(id+"F4.wireOp",EDGE,"E448"),sQuery(id+"F4.wireOp",EDGE,"E449"),sQuery(id+"F4.wireOp",EDGE,"E450"),sQuery(id+"F4.wireOp",EDGE,"E451"),sQuery(id+"F4.wireOp",EDGE,"E452"),sQuery(id+"F4.wireOp",EDGE,"E453"),sQuery(id+"F4.wireOp",EDGE,"E454"),sQuery(id+"F4.wireOp",EDGE,"E455"),sQuery(id+"F4.wireOp",EDGE,"E456"),sQuery(id+"F4.wireOp",EDGE,"E457"),sQuery(id+"F4.wireOp",EDGE,"E458"),sQuery(id+"F4.wireOp",EDGE,"E459"),sQuery(id+"F4.wireOp",EDGE,"E460"),sQuery(id+"F4.wireOp",EDGE,"E461")])]});
            var Q3;
            Q3=makeQuery(id+"F5.opExtrude","SWEPT_BODY",BODY,{"disambiguationData":[OSD([sQuery(id+"F4.wireOp",EDGE,"E462"),sQuery(id+"F4.wireOp",EDGE,"E463"),sQuery(id+"F4.wireOp",EDGE,"E464"),sQuery(id+"F4.wireOp",EDGE,"E465"),sQuery(id+"F4.wireOp",EDGE,"E466"),sQuery(id+"F4.wireOp",EDGE,"E467"),sQuery(id+"F4.wireOp",EDGE,"E468"),sQuery(id+"F4.wireOp",EDGE,"E469"),sQuery(id+"F4.wireOp",EDGE,"E470"),sQuery(id+"F4.wireOp",EDGE,"E471"),sQuery(id+"F4.wireOp",EDGE,"E472"),sQuery(id+"F4.wireOp",EDGE,"E473"),sQuery(id+"F4.wireOp",EDGE,"E474"),sQuery(id+"F4.wireOp",EDGE,"E475"),sQuery(id+"F4.wireOp",EDGE,"E476"),sQuery(id+"F4.wireOp",EDGE,"E477"),sQuery(id+"F4.wireOp",EDGE,"E478"),sQuery(id+"F4.wireOp",EDGE,"E479"),sQuery(id+"F4.wireOp",EDGE,"E480"),sQuery(id+"F4.wireOp",EDGE,"E481"),sQuery(id+"F4.wireOp",EDGE,"E482"),sQuery(id+"F4.wireOp",EDGE,"E483"),sQuery(id+"F4.wireOp",EDGE,"E484"),sQuery(id+"F4.wireOp",EDGE,"E485"),sQuery(id+"F4.wireOp",EDGE,"E486"),sQuery(id+"F4.wireOp",EDGE,"E487"),sQuery(id+"F4.wireOp",EDGE,"E488"),sQuery(id+"F4.wireOp",EDGE,"E489"),sQuery(id+"F4.wireOp",EDGE,"E490"),sQuery(id+"F4.wireOp",EDGE,"E491"),sQuery(id+"F4.wireOp",EDGE,"E492"),sQuery(id+"F4.wireOp",EDGE,"E493"),sQuery(id+"F4.wireOp",EDGE,"E494"),sQuery(id+"F4.wireOp",EDGE,"E495"),sQuery(id+"F4.wireOp",EDGE,"E496"),sQuery(id+"F4.wireOp",EDGE,"E497"),sQuery(id+"F4.wireOp",EDGE,"E498"),sQuery(id+"F4.wireOp",EDGE,"E499"),sQuery(id+"F4.wireOp",EDGE,"E500"),sQuery(id+"F4.wireOp",EDGE,"E501"),sQuery(id+"F4.wireOp",EDGE,"E502"),sQuery(id+"F4.wireOp",EDGE,"E503"),sQuery(id+"F4.wireOp",EDGE,"E504"),sQuery(id+"F4.wireOp",EDGE,"E505"),sQuery(id+"F4.wireOp",EDGE,"E506"),sQuery(id+"F4.wireOp",EDGE,"E507"),sQuery(id+"F4.wireOp",EDGE,"E508"),sQuery(id+"F4.wireOp",EDGE,"E509"),sQuery(id+"F4.wireOp",EDGE,"E510"),sQuery(id+"F4.wireOp",EDGE,"E511"),sQuery(id+"F4.wireOp",EDGE,"E512"),sQuery(id+"F4.wireOp",EDGE,"E513"),sQuery(id+"F4.wireOp",EDGE,"E514"),sQuery(id+"F4.wireOp",EDGE,"E515"),sQuery(id+"F4.wireOp",EDGE,"E516"),sQuery(id+"F4.wireOp",EDGE,"E517"),sQuery(id+"F4.wireOp",EDGE,"E518"),sQuery(id+"F4.wireOp",EDGE,"E519"),sQuery(id+"F4.wireOp",EDGE,"E520"),sQuery(id+"F4.wireOp",EDGE,"E521"),sQuery(id+"F4.wireOp",EDGE,"E522"),sQuery(id+"F4.wireOp",EDGE,"E523"),sQuery(id+"F4.wireOp",EDGE,"E524"),sQuery(id+"F4.wireOp",EDGE,"E525"),sQuery(id+"F4.wireOp",EDGE,"E525"),sQuery(id+"F4.wireOp",EDGE,"E525"),sQuery(id+"F4.wireOp",EDGE,"E526"),sQuery(id+"F4.wireOp",EDGE,"E527"),sQuery(id+"F4.wireOp",EDGE,"E528"),sQuery(id+"F4.wireOp",EDGE,"E529"),sQuery(id+"F4.wireOp",EDGE,"E530"),sQuery(id+"F4.wireOp",EDGE,"E531"),sQuery(id+"F4.wireOp",EDGE,"E531"),sQuery(id+"F4.wireOp",EDGE,"E531"),sQuery(id+"F4.wireOp",EDGE,"E532"),sQuery(id+"F4.wireOp",EDGE,"E533"),sQuery(id+"F4.wireOp",EDGE,"E534"),sQuery(id+"F4.wireOp",EDGE,"E535"),sQuery(id+"F4.wireOp",EDGE,"E536"),sQuery(id+"F4.wireOp",EDGE,"E537"),sQuery(id+"F4.wireOp",EDGE,"E538"),sQuery(id+"F4.wireOp",EDGE,"E539"),sQuery(id+"F4.wireOp",EDGE,"E540"),sQuery(id+"F4.wireOp",EDGE,"E541"),sQuery(id+"F4.wireOp",EDGE,"E542"),sQuery(id+"F4.wireOp",EDGE,"E543"),sQuery(id+"F4.wireOp",EDGE,"E544"),sQuery(id+"F4.wireOp",EDGE,"E545"),sQuery(id+"F4.wireOp",EDGE,"E546"),sQuery(id+"F4.wireOp",EDGE,"E547"),sQuery(id+"F4.wireOp",EDGE,"E548"),sQuery(id+"F4.wireOp",EDGE,"E549"),sQuery(id+"F4.wireOp",EDGE,"E550"),sQuery(id+"F4.wireOp",EDGE,"E551"),sQuery(id+"F4.wireOp",EDGE,"E552"),sQuery(id+"F4.wireOp",EDGE,"E553"),sQuery(id+"F4.wireOp",EDGE,"E554"),sQuery(id+"F4.wireOp",EDGE,"E555"),sQuery(id+"F4.wireOp",EDGE,"E556"),sQuery(id+"F4.wireOp",EDGE,"E557"),sQuery(id+"F4.wireOp",EDGE,"E558"),sQuery(id+"F4.wireOp",EDGE,"E559"),sQuery(id+"F4.wireOp",EDGE,"E560"),sQuery(id+"F4.wireOp",EDGE,"E561"),sQuery(id+"F4.wireOp",EDGE,"E562"),sQuery(id+"F4.wireOp",EDGE,"E562"),sQuery(id+"F4.wireOp",EDGE,"E563"),sQuery(id+"F4.wireOp",EDGE,"E564"),sQuery(id+"F4.wireOp",EDGE,"E565"),sQuery(id+"F4.wireOp",EDGE,"E566"),sQuery(id+"F4.wireOp",EDGE,"E567"),sQuery(id+"F4.wireOp",EDGE,"E565"),sQuery(id+"F4.wireOp",EDGE,"E568"),sQuery(id+"F4.wireOp",EDGE,"E569"),sQuery(id+"F4.wireOp",EDGE,"E569"),sQuery(id+"F4.wireOp",EDGE,"E570"),sQuery(id+"F4.wireOp",EDGE,"E571"),sQuery(id+"F4.wireOp",EDGE,"E572"),sQuery(id+"F4.wireOp",EDGE,"E573"),sQuery(id+"F4.wireOp",EDGE,"E574")])]});
            var Q4;
            Q4=makeQuery(id+"F5.opExtrude","SWEPT_BODY",BODY,{"disambiguationData":[OSD([sQuery(id+"F4.wireOp",EDGE,"E575"),sQuery(id+"F4.wireOp",EDGE,"E576"),sQuery(id+"F4.wireOp",EDGE,"E577"),sQuery(id+"F4.wireOp",EDGE,"E578"),sQuery(id+"F4.wireOp",EDGE,"E579"),sQuery(id+"F4.wireOp",EDGE,"E580"),sQuery(id+"F4.wireOp",EDGE,"E581"),sQuery(id+"F4.wireOp",EDGE,"E582"),sQuery(id+"F4.wireOp",EDGE,"E583"),sQuery(id+"F4.wireOp",EDGE,"E584"),sQuery(id+"F4.wireOp",EDGE,"E585"),sQuery(id+"F4.wireOp",EDGE,"E586"),sQuery(id+"F4.wireOp",EDGE,"E587"),sQuery(id+"F4.wireOp",EDGE,"E588"),sQuery(id+"F4.wireOp",EDGE,"E589"),sQuery(id+"F4.wireOp",EDGE,"E590"),sQuery(id+"F4.wireOp",EDGE,"E591"),sQuery(id+"F4.wireOp",EDGE,"E592"),sQuery(id+"F4.wireOp",EDGE,"E593"),sQuery(id+"F4.wireOp",EDGE,"E594"),sQuery(id+"F4.wireOp",EDGE,"E595"),sQuery(id+"F4.wireOp",EDGE,"E596"),sQuery(id+"F4.wireOp",EDGE,"E597"),sQuery(id+"F4.wireOp",EDGE,"E598"),sQuery(id+"F4.wireOp",EDGE,"E599"),sQuery(id+"F4.wireOp",EDGE,"E600"),sQuery(id+"F4.wireOp",EDGE,"E601"),sQuery(id+"F4.wireOp",EDGE,"E602"),sQuery(id+"F4.wireOp",EDGE,"E603")])]});
            var Q5;
            Q5=makeQuery(id+"F5.opExtrude","SWEPT_BODY",BODY,{"disambiguationData":[OSD([sQuery(id+"F4.wireOp",EDGE,"E604"),sQuery(id+"F4.wireOp",EDGE,"E605"),sQuery(id+"F4.wireOp",EDGE,"E606"),sQuery(id+"F4.wireOp",EDGE,"E607"),sQuery(id+"F4.wireOp",EDGE,"E608"),sQuery(id+"F4.wireOp",EDGE,"E609"),sQuery(id+"F4.wireOp",EDGE,"E610"),sQuery(id+"F4.wireOp",EDGE,"E611"),sQuery(id+"F4.wireOp",EDGE,"E612"),sQuery(id+"F4.wireOp",EDGE,"E613"),sQuery(id+"F4.wireOp",EDGE,"E614"),sQuery(id+"F4.wireOp",EDGE,"E615"),sQuery(id+"F4.wireOp",EDGE,"E616"),sQuery(id+"F4.wireOp",EDGE,"E617"),sQuery(id+"F4.wireOp",EDGE,"E617"),sQuery(id+"F4.wireOp",EDGE,"E618"),sQuery(id+"F4.wireOp",EDGE,"E619"),sQuery(id+"F4.wireOp",EDGE,"E620"),sQuery(id+"F4.wireOp",EDGE,"E621"),sQuery(id+"F4.wireOp",EDGE,"E622"),sQuery(id+"F4.wireOp",EDGE,"E623"),sQuery(id+"F4.wireOp",EDGE,"E624"),sQuery(id+"F4.wireOp",EDGE,"E625"),sQuery(id+"F4.wireOp",EDGE,"E626"),sQuery(id+"F4.wireOp",EDGE,"E627"),sQuery(id+"F4.wireOp",EDGE,"E628"),sQuery(id+"F4.wireOp",EDGE,"E629"),sQuery(id+"F4.wireOp",EDGE,"E630"),sQuery(id+"F4.wireOp",EDGE,"E631"),sQuery(id+"F4.wireOp",EDGE,"E632"),sQuery(id+"F4.wireOp",EDGE,"E633"),sQuery(id+"F4.wireOp",EDGE,"E634"),sQuery(id+"F4.wireOp",EDGE,"E635"),sQuery(id+"F4.wireOp",EDGE,"E636"),sQuery(id+"F4.wireOp",EDGE,"E637"),sQuery(id+"F4.wireOp",EDGE,"E638"),sQuery(id+"F4.wireOp",EDGE,"E639"),sQuery(id+"F4.wireOp",EDGE,"E640"),sQuery(id+"F4.wireOp",EDGE,"E641"),sQuery(id+"F4.wireOp",EDGE,"E642"),sQuery(id+"F4.wireOp",EDGE,"E643"),sQuery(id+"F4.wireOp",EDGE,"E644"),sQuery(id+"F4.wireOp",EDGE,"E645"),sQuery(id+"F4.wireOp",EDGE,"E646"),sQuery(id+"F4.wireOp",EDGE,"E647"),sQuery(id+"F4.wireOp",EDGE,"E648"),sQuery(id+"F4.wireOp",EDGE,"E649"),sQuery(id+"F4.wireOp",EDGE,"E650"),sQuery(id+"F4.wireOp",EDGE,"E651"),sQuery(id+"F4.wireOp",EDGE,"E652"),sQuery(id+"F4.wireOp",EDGE,"E653"),sQuery(id+"F4.wireOp",EDGE,"E654"),sQuery(id+"F4.wireOp",EDGE,"E655"),sQuery(id+"F4.wireOp",EDGE,"E656"),sQuery(id+"F4.wireOp",EDGE,"E657"),sQuery(id+"F4.wireOp",EDGE,"E658"),sQuery(id+"F4.wireOp",EDGE,"E659"),sQuery(id+"F4.wireOp",EDGE,"E660"),sQuery(id+"F4.wireOp",EDGE,"E661"),sQuery(id+"F4.wireOp",EDGE,"E662"),sQuery(id+"F4.wireOp",EDGE,"E663"),sQuery(id+"F4.wireOp",EDGE,"E664"),sQuery(id+"F4.wireOp",EDGE,"E665"),sQuery(id+"F4.wireOp",EDGE,"E665"),sQuery(id+"F4.wireOp",EDGE,"E666"),sQuery(id+"F4.wireOp",EDGE,"E667"),sQuery(id+"F4.wireOp",EDGE,"E668"),sQuery(id+"F4.wireOp",EDGE,"E669"),sQuery(id+"F4.wireOp",EDGE,"E670"),sQuery(id+"F4.wireOp",EDGE,"E671"),sQuery(id+"F4.wireOp",EDGE,"E672"),sQuery(id+"F4.wireOp",EDGE,"E673"),sQuery(id+"F4.wireOp",EDGE,"E674"),sQuery(id+"F4.wireOp",EDGE,"E674"),sQuery(id+"F4.wireOp",EDGE,"E675"),sQuery(id+"F4.wireOp",EDGE,"E676"),sQuery(id+"F4.wireOp",EDGE,"E676"),sQuery(id+"F4.wireOp",EDGE,"E677"),sQuery(id+"F4.wireOp",EDGE,"E678"),sQuery(id+"F4.wireOp",EDGE,"E679"),sQuery(id+"F4.wireOp",EDGE,"E680"),sQuery(id+"F4.wireOp",EDGE,"E681"),sQuery(id+"F4.wireOp",EDGE,"E682"),sQuery(id+"F4.wireOp",EDGE,"E683"),sQuery(id+"F4.wireOp",EDGE,"E684"),sQuery(id+"F4.wireOp",EDGE,"E685"),sQuery(id+"F4.wireOp",EDGE,"E686"),sQuery(id+"F4.wireOp",EDGE,"E687"),sQuery(id+"F4.wireOp",EDGE,"E687"),sQuery(id+"F4.wireOp",EDGE,"E688"),sQuery(id+"F4.wireOp",EDGE,"E689"),sQuery(id+"F4.wireOp",EDGE,"E690"),sQuery(id+"F4.wireOp",EDGE,"E691"),sQuery(id+"F4.wireOp",EDGE,"E692"),sQuery(id+"F4.wireOp",EDGE,"E693"),sQuery(id+"F4.wireOp",EDGE,"E694"),sQuery(id+"F4.wireOp",EDGE,"E695"),sQuery(id+"F4.wireOp",EDGE,"E696"),sQuery(id+"F4.wireOp",EDGE,"E697"),sQuery(id+"F4.wireOp",EDGE,"E698"),sQuery(id+"F4.wireOp",EDGE,"E699"),sQuery(id+"F4.wireOp",EDGE,"E700"),sQuery(id+"F4.wireOp",EDGE,"E701"),sQuery(id+"F4.wireOp",EDGE,"E702"),sQuery(id+"F4.wireOp",EDGE,"E703"),sQuery(id+"F4.wireOp",EDGE,"E704"),sQuery(id+"F4.wireOp",EDGE,"E705"),sQuery(id+"F4.wireOp",EDGE,"E706"),sQuery(id+"F4.wireOp",EDGE,"E707"),sQuery(id+"F4.wireOp",EDGE,"E708"),sQuery(id+"F4.wireOp",EDGE,"E708"),sQuery(id+"F4.wireOp",EDGE,"E708")])]});
            var Q6;
            Q6=makeQuery(id+"F5.opExtrude","SWEPT_BODY",BODY,{"disambiguationData":[OSD([sQuery(id+"F4.wireOp",EDGE,"E709"),sQuery(id+"F4.wireOp",EDGE,"E710"),sQuery(id+"F4.wireOp",EDGE,"E711"),sQuery(id+"F4.wireOp",EDGE,"E712"),sQuery(id+"F4.wireOp",EDGE,"E713"),sQuery(id+"F4.wireOp",EDGE,"E714"),sQuery(id+"F4.wireOp",EDGE,"E715"),sQuery(id+"F4.wireOp",EDGE,"E716"),sQuery(id+"F4.wireOp",EDGE,"E717"),sQuery(id+"F4.wireOp",EDGE,"E718"),sQuery(id+"F4.wireOp",EDGE,"E719"),sQuery(id+"F4.wireOp",EDGE,"E720"),sQuery(id+"F4.wireOp",EDGE,"E721"),sQuery(id+"F4.wireOp",EDGE,"E722"),sQuery(id+"F4.wireOp",EDGE,"E723"),sQuery(id+"F4.wireOp",EDGE,"E723"),sQuery(id+"F4.wireOp",EDGE,"E724"),sQuery(id+"F4.wireOp",EDGE,"E725"),sQuery(id+"F4.wireOp",EDGE,"E726"),sQuery(id+"F4.wireOp",EDGE,"E727"),sQuery(id+"F4.wireOp",EDGE,"E728"),sQuery(id+"F4.wireOp",EDGE,"E729"),sQuery(id+"F4.wireOp",EDGE,"E730"),sQuery(id+"F4.wireOp",EDGE,"E731"),sQuery(id+"F4.wireOp",EDGE,"E732"),sQuery(id+"F4.wireOp",EDGE,"E733"),sQuery(id+"F4.wireOp",EDGE,"E734"),sQuery(id+"F4.wireOp",EDGE,"E735"),sQuery(id+"F4.wireOp",EDGE,"E736"),sQuery(id+"F4.wireOp",EDGE,"E737"),sQuery(id+"F4.wireOp",EDGE,"E738"),sQuery(id+"F4.wireOp",EDGE,"E739"),sQuery(id+"F4.wireOp",EDGE,"E740"),sQuery(id+"F4.wireOp",EDGE,"E741"),sQuery(id+"F4.wireOp",EDGE,"E742"),sQuery(id+"F4.wireOp",EDGE,"E743"),sQuery(id+"F4.wireOp",EDGE,"E744"),sQuery(id+"F4.wireOp",EDGE,"E745"),sQuery(id+"F4.wireOp",EDGE,"E746"),sQuery(id+"F4.wireOp",EDGE,"E747"),sQuery(id+"F4.wireOp",EDGE,"E748"),sQuery(id+"F4.wireOp",EDGE,"E749"),sQuery(id+"F4.wireOp",EDGE,"E750"),sQuery(id+"F4.wireOp",EDGE,"E751"),sQuery(id+"F4.wireOp",EDGE,"E752"),sQuery(id+"F4.wireOp",EDGE,"E753"),sQuery(id+"F4.wireOp",EDGE,"E754"),sQuery(id+"F4.wireOp",EDGE,"E755"),sQuery(id+"F4.wireOp",EDGE,"E756"),sQuery(id+"F4.wireOp",EDGE,"E757"),sQuery(id+"F4.wireOp",EDGE,"E758"),sQuery(id+"F4.wireOp",EDGE,"E758"),sQuery(id+"F4.wireOp",EDGE,"E758"),sQuery(id+"F4.wireOp",EDGE,"E759"),sQuery(id+"F4.wireOp",EDGE,"E760"),sQuery(id+"F4.wireOp",EDGE,"E760"),sQuery(id+"F4.wireOp",EDGE,"E761"),sQuery(id+"F4.wireOp",EDGE,"E762"),sQuery(id+"F4.wireOp",EDGE,"E763"),sQuery(id+"F4.wireOp",EDGE,"E764"),sQuery(id+"F4.wireOp",EDGE,"E765"),sQuery(id+"F4.wireOp",EDGE,"E766"),sQuery(id+"F4.wireOp",EDGE,"E767"),sQuery(id+"F4.wireOp",EDGE,"E768"),sQuery(id+"F4.wireOp",EDGE,"E768"),sQuery(id+"F4.wireOp",EDGE,"E768"),sQuery(id+"F4.wireOp",EDGE,"E769"),sQuery(id+"F4.wireOp",EDGE,"E770"),sQuery(id+"F4.wireOp",EDGE,"E771"),sQuery(id+"F4.wireOp",EDGE,"E772"),sQuery(id+"F4.wireOp",EDGE,"E773"),sQuery(id+"F4.wireOp",EDGE,"E774"),sQuery(id+"F4.wireOp",EDGE,"E775"),sQuery(id+"F4.wireOp",EDGE,"E776"),sQuery(id+"F4.wireOp",EDGE,"E777"),sQuery(id+"F4.wireOp",EDGE,"E778"),sQuery(id+"F4.wireOp",EDGE,"E779"),sQuery(id+"F4.wireOp",EDGE,"E780"),sQuery(id+"F4.wireOp",EDGE,"E781"),sQuery(id+"F4.wireOp",EDGE,"E782"),sQuery(id+"F4.wireOp",EDGE,"E783"),sQuery(id+"F4.wireOp",EDGE,"E784"),sQuery(id+"F4.wireOp",EDGE,"E785"),sQuery(id+"F4.wireOp",EDGE,"E786"),sQuery(id+"F4.wireOp",EDGE,"E787"),sQuery(id+"F4.wireOp",EDGE,"E788"),sQuery(id+"F4.wireOp",EDGE,"E789"),sQuery(id+"F4.wireOp",EDGE,"E790"),sQuery(id+"F4.wireOp",EDGE,"E791"),sQuery(id+"F4.wireOp",EDGE,"E792"),sQuery(id+"F4.wireOp",EDGE,"E793"),sQuery(id+"F4.wireOp",EDGE,"E794"),sQuery(id+"F4.wireOp",EDGE,"E795"),sQuery(id+"F4.wireOp",EDGE,"E796"),sQuery(id+"F4.wireOp",EDGE,"E797"),sQuery(id+"F4.wireOp",EDGE,"E798"),sQuery(id+"F4.wireOp",EDGE,"E799"),sQuery(id+"F4.wireOp",EDGE,"E800"),sQuery(id+"F4.wireOp",EDGE,"E801"),sQuery(id+"F4.wireOp",EDGE,"E802"),sQuery(id+"F4.wireOp",EDGE,"E803"),sQuery(id+"F4.wireOp",EDGE,"E804"),sQuery(id+"F4.wireOp",EDGE,"E805"),sQuery(id+"F4.wireOp",EDGE,"E806"),sQuery(id+"F4.wireOp",EDGE,"E807"),sQuery(id+"F4.wireOp",EDGE,"E808"),sQuery(id+"F4.wireOp",EDGE,"E809"),sQuery(id+"F4.wireOp",EDGE,"E810"),sQuery(id+"F4.wireOp",EDGE,"E811"),sQuery(id+"F4.wireOp",EDGE,"E812"),sQuery(id+"F4.wireOp",EDGE,"E813"),sQuery(id+"F4.wireOp",EDGE,"E814"),sQuery(id+"F4.wireOp",EDGE,"E815"),sQuery(id+"F4.wireOp",EDGE,"E816"),sQuery(id+"F4.wireOp",EDGE,"E817"),sQuery(id+"F4.wireOp",EDGE,"E818"),sQuery(id+"F4.wireOp",EDGE,"E819"),sQuery(id+"F4.wireOp",EDGE,"E820"),sQuery(id+"F4.wireOp",EDGE,"E821"),sQuery(id+"F4.wireOp",EDGE,"E822"),sQuery(id+"F4.wireOp",EDGE,"E823"),sQuery(id+"F4.wireOp",EDGE,"E824"),sQuery(id+"F4.wireOp",EDGE,"E825"),sQuery(id+"F4.wireOp",EDGE,"E826"),sQuery(id+"F4.wireOp",EDGE,"E827"),sQuery(id+"F4.wireOp",EDGE,"E828"),sQuery(id+"F4.wireOp",EDGE,"E829"),sQuery(id+"F4.wireOp",EDGE,"E830"),sQuery(id+"F4.wireOp",EDGE,"E831"),sQuery(id+"F4.wireOp",EDGE,"E832"),sQuery(id+"F4.wireOp",EDGE,"E833")])]});
            var Q7;
            Q7=makeQuery(id+"F5.opExtrude","SWEPT_BODY",BODY,{"disambiguationData":[OSD([sQuery(id+"F4.wireOp",EDGE,"E834"),sQuery(id+"F4.wireOp",EDGE,"E835"),sQuery(id+"F4.wireOp",EDGE,"E836"),sQuery(id+"F4.wireOp",EDGE,"E837"),sQuery(id+"F4.wireOp",EDGE,"E838"),sQuery(id+"F4.wireOp",EDGE,"E839"),sQuery(id+"F4.wireOp",EDGE,"E840"),sQuery(id+"F4.wireOp",EDGE,"E841"),sQuery(id+"F4.wireOp",EDGE,"E842"),sQuery(id+"F4.wireOp",EDGE,"E843"),sQuery(id+"F4.wireOp",EDGE,"E844"),sQuery(id+"F4.wireOp",EDGE,"E845"),sQuery(id+"F4.wireOp",EDGE,"E846"),sQuery(id+"F4.wireOp",EDGE,"E847"),sQuery(id+"F4.wireOp",EDGE,"E848"),sQuery(id+"F4.wireOp",EDGE,"E849"),sQuery(id+"F4.wireOp",EDGE,"E850"),sQuery(id+"F4.wireOp",EDGE,"E851"),sQuery(id+"F4.wireOp",EDGE,"E852"),sQuery(id+"F4.wireOp",EDGE,"E853"),sQuery(id+"F4.wireOp",EDGE,"E854"),sQuery(id+"F4.wireOp",EDGE,"E855"),sQuery(id+"F4.wireOp",EDGE,"E856"),sQuery(id+"F4.wireOp",EDGE,"E857"),sQuery(id+"F4.wireOp",EDGE,"E858"),sQuery(id+"F4.wireOp",EDGE,"E859"),sQuery(id+"F4.wireOp",EDGE,"E860"),sQuery(id+"F4.wireOp",EDGE,"E861"),sQuery(id+"F4.wireOp",EDGE,"E862"),sQuery(id+"F4.wireOp",EDGE,"E863"),sQuery(id+"F4.wireOp",EDGE,"E864"),sQuery(id+"F4.wireOp",EDGE,"E865"),sQuery(id+"F4.wireOp",EDGE,"E866"),sQuery(id+"F4.wireOp",EDGE,"E867"),sQuery(id+"F4.wireOp",EDGE,"E868"),sQuery(id+"F4.wireOp",EDGE,"E869"),sQuery(id+"F4.wireOp",EDGE,"E870"),sQuery(id+"F4.wireOp",EDGE,"E871"),sQuery(id+"F4.wireOp",EDGE,"E872"),sQuery(id+"F4.wireOp",EDGE,"E873"),sQuery(id+"F4.wireOp",EDGE,"E874"),sQuery(id+"F4.wireOp",EDGE,"E875"),sQuery(id+"F4.wireOp",EDGE,"E876"),sQuery(id+"F4.wireOp",EDGE,"E877"),sQuery(id+"F4.wireOp",EDGE,"E878"),sQuery(id+"F4.wireOp",EDGE,"E879"),sQuery(id+"F4.wireOp",EDGE,"E880"),sQuery(id+"F4.wireOp",EDGE,"E881"),sQuery(id+"F4.wireOp",EDGE,"E882"),sQuery(id+"F4.wireOp",EDGE,"E883"),sQuery(id+"F4.wireOp",EDGE,"E884"),sQuery(id+"F4.wireOp",EDGE,"E885"),sQuery(id+"F4.wireOp",EDGE,"E886"),sQuery(id+"F4.wireOp",EDGE,"E887"),sQuery(id+"F4.wireOp",EDGE,"E888"),sQuery(id+"F4.wireOp",EDGE,"E889"),sQuery(id+"F4.wireOp",EDGE,"E890"),sQuery(id+"F4.wireOp",EDGE,"E891"),sQuery(id+"F4.wireOp",EDGE,"E892"),sQuery(id+"F4.wireOp",EDGE,"E893"),sQuery(id+"F4.wireOp",EDGE,"E894"),sQuery(id+"F4.wireOp",EDGE,"E895"),sQuery(id+"F4.wireOp",EDGE,"E896"),sQuery(id+"F4.wireOp",EDGE,"E897"),sQuery(id+"F4.wireOp",EDGE,"E898"),sQuery(id+"F4.wireOp",EDGE,"E899"),sQuery(id+"F4.wireOp",EDGE,"E900"),sQuery(id+"F4.wireOp",EDGE,"E901"),sQuery(id+"F4.wireOp",EDGE,"E901"),sQuery(id+"F4.wireOp",EDGE,"E902"),sQuery(id+"F4.wireOp",EDGE,"E903"),sQuery(id+"F4.wireOp",EDGE,"E904"),sQuery(id+"F4.wireOp",EDGE,"E905"),sQuery(id+"F4.wireOp",EDGE,"E906"),sQuery(id+"F4.wireOp",EDGE,"E907"),sQuery(id+"F4.wireOp",EDGE,"E908"),sQuery(id+"F4.wireOp",EDGE,"E909"),sQuery(id+"F4.wireOp",EDGE,"E910"),sQuery(id+"F4.wireOp",EDGE,"E911"),sQuery(id+"F4.wireOp",EDGE,"E912")])]});
            var Q8;
            Q8=makeQuery(id+"F5.opExtrude","SWEPT_BODY",BODY,{"disambiguationData":[OSD([sQuery(id+"F4.wireOp",EDGE,"E913"),sQuery(id+"F4.wireOp",EDGE,"E914"),sQuery(id+"F4.wireOp",EDGE,"E915"),sQuery(id+"F4.wireOp",EDGE,"E916"),sQuery(id+"F4.wireOp",EDGE,"E917"),sQuery(id+"F4.wireOp",EDGE,"E918"),sQuery(id+"F4.wireOp",EDGE,"E919"),sQuery(id+"F4.wireOp",EDGE,"E920"),sQuery(id+"F4.wireOp",EDGE,"E921"),sQuery(id+"F4.wireOp",EDGE,"E922"),sQuery(id+"F4.wireOp",EDGE,"E923"),sQuery(id+"F4.wireOp",EDGE,"E924"),sQuery(id+"F4.wireOp",EDGE,"E925"),sQuery(id+"F4.wireOp",EDGE,"E926"),sQuery(id+"F4.wireOp",EDGE,"E927"),sQuery(id+"F4.wireOp",EDGE,"E928"),sQuery(id+"F4.wireOp",EDGE,"E929"),sQuery(id+"F4.wireOp",EDGE,"E930"),sQuery(id+"F4.wireOp",EDGE,"E931"),sQuery(id+"F4.wireOp",EDGE,"E932"),sQuery(id+"F4.wireOp",EDGE,"E933"),sQuery(id+"F4.wireOp",EDGE,"E934"),sQuery(id+"F4.wireOp",EDGE,"E935"),sQuery(id+"F4.wireOp",EDGE,"E936"),sQuery(id+"F4.wireOp",EDGE,"E937"),sQuery(id+"F4.wireOp",EDGE,"E938"),sQuery(id+"F4.wireOp",EDGE,"E939"),sQuery(id+"F4.wireOp",EDGE,"E940"),sQuery(id+"F4.wireOp",EDGE,"E941"),sQuery(id+"F4.wireOp",EDGE,"E942"),sQuery(id+"F4.wireOp",EDGE,"E943"),sQuery(id+"F4.wireOp",EDGE,"E944"),sQuery(id+"F4.wireOp",EDGE,"E945"),sQuery(id+"F4.wireOp",EDGE,"E946"),sQuery(id+"F4.wireOp",EDGE,"E947"),sQuery(id+"F4.wireOp",EDGE,"E947"),sQuery(id+"F4.wireOp",EDGE,"E948"),sQuery(id+"F4.wireOp",EDGE,"E949"),sQuery(id+"F4.wireOp",EDGE,"E950"),sQuery(id+"F4.wireOp",EDGE,"E951"),sQuery(id+"F4.wireOp",EDGE,"E952"),sQuery(id+"F4.wireOp",EDGE,"E953"),sQuery(id+"F4.wireOp",EDGE,"E954"),sQuery(id+"F4.wireOp",EDGE,"E955"),sQuery(id+"F4.wireOp",EDGE,"E956"),sQuery(id+"F4.wireOp",EDGE,"E957"),sQuery(id+"F4.wireOp",EDGE,"E958"),sQuery(id+"F4.wireOp",EDGE,"E959"),sQuery(id+"F4.wireOp",EDGE,"E959"),sQuery(id+"F4.wireOp",EDGE,"E960"),sQuery(id+"F4.wireOp",EDGE,"E961"),sQuery(id+"F4.wireOp",EDGE,"E962"),sQuery(id+"F4.wireOp",EDGE,"E963"),sQuery(id+"F4.wireOp",EDGE,"E964"),sQuery(id+"F4.wireOp",EDGE,"E965"),sQuery(id+"F4.wireOp",EDGE,"E966"),sQuery(id+"F4.wireOp",EDGE,"E967"),sQuery(id+"F4.wireOp",EDGE,"E968"),sQuery(id+"F4.wireOp",EDGE,"E969"),sQuery(id+"F4.wireOp",EDGE,"E970"),sQuery(id+"F4.wireOp",EDGE,"E971"),sQuery(id+"F4.wireOp",EDGE,"E972"),sQuery(id+"F4.wireOp",EDGE,"E973"),sQuery(id+"F4.wireOp",EDGE,"E974"),sQuery(id+"F4.wireOp",EDGE,"E975"),sQuery(id+"F4.wireOp",EDGE,"E976"),sQuery(id+"F4.wireOp",EDGE,"E977"),sQuery(id+"F4.wireOp",EDGE,"E978"),sQuery(id+"F4.wireOp",EDGE,"E979"),sQuery(id+"F4.wireOp",EDGE,"E980"),sQuery(id+"F4.wireOp",EDGE,"E981"),sQuery(id+"F4.wireOp",EDGE,"E982"),sQuery(id+"F4.wireOp",EDGE,"E983"),sQuery(id+"F4.wireOp",EDGE,"E984"),sQuery(id+"F4.wireOp",EDGE,"E985"),sQuery(id+"F4.wireOp",EDGE,"E986"),sQuery(id+"F4.wireOp",EDGE,"E987"),sQuery(id+"F4.wireOp",EDGE,"E988"),sQuery(id+"F4.wireOp",EDGE,"E989"),sQuery(id+"F4.wireOp",EDGE,"E990"),sQuery(id+"F4.wireOp",EDGE,"E991"),sQuery(id+"F4.wireOp",EDGE,"E992"),sQuery(id+"F4.wireOp",EDGE,"E992"),sQuery(id+"F4.wireOp",EDGE,"E993"),sQuery(id+"F4.wireOp",EDGE,"E994"),sQuery(id+"F4.wireOp",EDGE,"E995"),sQuery(id+"F4.wireOp",EDGE,"E996"),sQuery(id+"F4.wireOp",EDGE,"E997"),sQuery(id+"F4.wireOp",EDGE,"E998"),sQuery(id+"F4.wireOp",EDGE,"E999"),sQuery(id+"F4.wireOp",EDGE,"E1000"),sQuery(id+"F4.wireOp",EDGE,"E1001"),sQuery(id+"F4.wireOp",EDGE,"E1002"),sQuery(id+"F4.wireOp",EDGE,"E1003"),sQuery(id+"F4.wireOp",EDGE,"E1004"),sQuery(id+"F4.wireOp",EDGE,"E1005"),sQuery(id+"F4.wireOp",EDGE,"E1006"),sQuery(id+"F4.wireOp",EDGE,"E1007"),sQuery(id+"F4.wireOp",EDGE,"E1008"),sQuery(id+"F4.wireOp",EDGE,"E1009"),sQuery(id+"F4.wireOp",EDGE,"E1010"),sQuery(id+"F4.wireOp",EDGE,"E1011"),sQuery(id+"F4.wireOp",EDGE,"E1012"),sQuery(id+"F4.wireOp",EDGE,"E1013"),sQuery(id+"F4.wireOp",EDGE,"E1014"),sQuery(id+"F4.wireOp",EDGE,"E1015"),sQuery(id+"F4.wireOp",EDGE,"E1016"),sQuery(id+"F4.wireOp",EDGE,"E1017"),sQuery(id+"F4.wireOp",EDGE,"E1018"),sQuery(id+"F4.wireOp",EDGE,"E1019")])]});
            var Q9;
            Q9=makeQuery(id+"F5.opExtrude","SWEPT_BODY",BODY,{"disambiguationData":[OSD([sQuery(id+"F4.wireOp",EDGE,"E1020"),sQuery(id+"F4.wireOp",EDGE,"E1021"),sQuery(id+"F4.wireOp",EDGE,"E1022"),sQuery(id+"F4.wireOp",EDGE,"E1023"),sQuery(id+"F4.wireOp",EDGE,"E1024"),sQuery(id+"F4.wireOp",EDGE,"E1025"),sQuery(id+"F4.wireOp",EDGE,"E1026"),sQuery(id+"F4.wireOp",EDGE,"E1027"),sQuery(id+"F4.wireOp",EDGE,"E1028"),sQuery(id+"F4.wireOp",EDGE,"E1029"),sQuery(id+"F4.wireOp",EDGE,"E1030"),sQuery(id+"F4.wireOp",EDGE,"E1031"),sQuery(id+"F4.wireOp",EDGE,"E1031"),sQuery(id+"F4.wireOp",EDGE,"E1032"),sQuery(id+"F4.wireOp",EDGE,"E1033"),sQuery(id+"F4.wireOp",EDGE,"E1034"),sQuery(id+"F4.wireOp",EDGE,"E1035"),sQuery(id+"F4.wireOp",EDGE,"E1036"),sQuery(id+"F4.wireOp",EDGE,"E1037"),sQuery(id+"F4.wireOp",EDGE,"E1038"),sQuery(id+"F4.wireOp",EDGE,"E1039"),sQuery(id+"F4.wireOp",EDGE,"E1040"),sQuery(id+"F4.wireOp",EDGE,"E1041"),sQuery(id+"F4.wireOp",EDGE,"E1041"),sQuery(id+"F4.wireOp",EDGE,"E1042"),sQuery(id+"F4.wireOp",EDGE,"E1043"),sQuery(id+"F4.wireOp",EDGE,"E1044"),sQuery(id+"F4.wireOp",EDGE,"E1045"),sQuery(id+"F4.wireOp",EDGE,"E1046"),sQuery(id+"F4.wireOp",EDGE,"E1047"),sQuery(id+"F4.wireOp",EDGE,"E1048"),sQuery(id+"F4.wireOp",EDGE,"E1049"),sQuery(id+"F4.wireOp",EDGE,"E1049"),sQuery(id+"F4.wireOp",EDGE,"E1049"),sQuery(id+"F4.wireOp",EDGE,"E1049"),sQuery(id+"F4.wireOp",EDGE,"E1050"),sQuery(id+"F4.wireOp",EDGE,"E1051"),sQuery(id+"F4.wireOp",EDGE,"E1052"),sQuery(id+"F4.wireOp",EDGE,"E1053"),sQuery(id+"F4.wireOp",EDGE,"E1054"),sQuery(id+"F4.wireOp",EDGE,"E1055"),sQuery(id+"F4.wireOp",EDGE,"E1056"),sQuery(id+"F4.wireOp",EDGE,"E1057"),sQuery(id+"F4.wireOp",EDGE,"E1058"),sQuery(id+"F4.wireOp",EDGE,"E1059"),sQuery(id+"F4.wireOp",EDGE,"E1060"),sQuery(id+"F4.wireOp",EDGE,"E1061"),sQuery(id+"F4.wireOp",EDGE,"E1062"),sQuery(id+"F4.wireOp",EDGE,"E1063"),sQuery(id+"F4.wireOp",EDGE,"E1064"),sQuery(id+"F4.wireOp",EDGE,"E1065"),sQuery(id+"F4.wireOp",EDGE,"E1066"),sQuery(id+"F4.wireOp",EDGE,"E1067"),sQuery(id+"F4.wireOp",EDGE,"E1068"),sQuery(id+"F4.wireOp",EDGE,"E1069"),sQuery(id+"F4.wireOp",EDGE,"E1070"),sQuery(id+"F4.wireOp",EDGE,"E1071"),sQuery(id+"F4.wireOp",EDGE,"E1072"),sQuery(id+"F4.wireOp",EDGE,"E1073"),sQuery(id+"F4.wireOp",EDGE,"E1074"),sQuery(id+"F4.wireOp",EDGE,"E1075"),sQuery(id+"F4.wireOp",EDGE,"E1076"),sQuery(id+"F4.wireOp",EDGE,"E1077"),sQuery(id+"F4.wireOp",EDGE,"E1078"),sQuery(id+"F4.wireOp",EDGE,"E1079"),sQuery(id+"F4.wireOp",EDGE,"E1080"),sQuery(id+"F4.wireOp",EDGE,"E1081"),sQuery(id+"F4.wireOp",EDGE,"E1082"),sQuery(id+"F4.wireOp",EDGE,"E1083"),sQuery(id+"F4.wireOp",EDGE,"E1083"),sQuery(id+"F4.wireOp",EDGE,"E1084"),sQuery(id+"F4.wireOp",EDGE,"E1085"),sQuery(id+"F4.wireOp",EDGE,"E1086"),sQuery(id+"F4.wireOp",EDGE,"E1087"),sQuery(id+"F4.wireOp",EDGE,"E1088"),sQuery(id+"F4.wireOp",EDGE,"E1089"),sQuery(id+"F4.wireOp",EDGE,"E1090"),sQuery(id+"F4.wireOp",EDGE,"E1090"),sQuery(id+"F4.wireOp",EDGE,"E1091"),sQuery(id+"F4.wireOp",EDGE,"E1092"),sQuery(id+"F4.wireOp",EDGE,"E1093"),sQuery(id+"F4.wireOp",EDGE,"E1094"),sQuery(id+"F4.wireOp",EDGE,"E1095"),sQuery(id+"F4.wireOp",EDGE,"E1096"),sQuery(id+"F4.wireOp",EDGE,"E1097"),sQuery(id+"F4.wireOp",EDGE,"E1098"),sQuery(id+"F4.wireOp",EDGE,"E1099"),sQuery(id+"F4.wireOp",EDGE,"E1100"),sQuery(id+"F4.wireOp",EDGE,"E1101"),sQuery(id+"F4.wireOp",EDGE,"E1102"),sQuery(id+"F4.wireOp",EDGE,"E1103"),sQuery(id+"F4.wireOp",EDGE,"E1104"),sQuery(id+"F4.wireOp",EDGE,"E1105"),sQuery(id+"F4.wireOp",EDGE,"E1106"),sQuery(id+"F4.wireOp",EDGE,"E1107"),sQuery(id+"F4.wireOp",EDGE,"E1108"),sQuery(id+"F4.wireOp",EDGE,"E1109"),sQuery(id+"F4.wireOp",EDGE,"E1110"),sQuery(id+"F4.wireOp",EDGE,"E1110"),sQuery(id+"F4.wireOp",EDGE,"E1110"),sQuery(id+"F4.wireOp",EDGE,"E1111"),sQuery(id+"F4.wireOp",EDGE,"E1112"),sQuery(id+"F4.wireOp",EDGE,"E1113"),sQuery(id+"F4.wireOp",EDGE,"E1114"),sQuery(id+"F4.wireOp",EDGE,"E1115"),sQuery(id+"F4.wireOp",EDGE,"E1116"),sQuery(id+"F4.wireOp",EDGE,"E1117"),sQuery(id+"F4.wireOp",EDGE,"E1118"),sQuery(id+"F4.wireOp",EDGE,"E1119"),sQuery(id+"F4.wireOp",EDGE,"E1120")])]});
            var Q10;
            Q10=makeQuery(id+"F5.opExtrude","SWEPT_BODY",BODY,{"disambiguationData":[OSD([sQuery(id+"F4.wireOp",EDGE,"E1121"),sQuery(id+"F4.wireOp",EDGE,"E1122"),sQuery(id+"F4.wireOp",EDGE,"E1123"),sQuery(id+"F4.wireOp",EDGE,"E1124"),sQuery(id+"F4.wireOp",EDGE,"E1125"),sQuery(id+"F4.wireOp",EDGE,"E1126"),sQuery(id+"F4.wireOp",EDGE,"E1127"),sQuery(id+"F4.wireOp",EDGE,"E1128"),sQuery(id+"F4.wireOp",EDGE,"E1129"),sQuery(id+"F4.wireOp",EDGE,"E1130"),sQuery(id+"F4.wireOp",EDGE,"E1131"),sQuery(id+"F4.wireOp",EDGE,"E1132"),sQuery(id+"F4.wireOp",EDGE,"E1133"),sQuery(id+"F4.wireOp",EDGE,"E1134"),sQuery(id+"F4.wireOp",EDGE,"E1135"),sQuery(id+"F4.wireOp",EDGE,"E1136")])]});
            var Q11;
            Q11=sQuery(id+"F7.wireOp",EDGE,"E1137");
            transform(context, id + "F8", {"entities" : qUnion([Q0, Q1, Q2, Q3, Q4, Q5, Q6, Q7, Q8, Q9, Q10]), "transformType" : TransformType.ROTATION, "transformAxis" : qUnion([Q11]), "angle" : 185 * degree, "makeCopy" : false});
        }
        {
            var Q0;
            Q0=makeQuery(id+"F5.opExtrude","SWEPT_BODY",BODY,{"disambiguationData":[OSD([sQuery(id+"F4.wireOp",EDGE,"E4"),sQuery(id+"F4.wireOp",EDGE,"E5"),sQuery(id+"F4.wireOp",EDGE,"E6"),sQuery(id+"F4.wireOp",EDGE,"E7"),sQuery(id+"F4.wireOp",EDGE,"E8"),sQuery(id+"F4.wireOp",EDGE,"E9"),sQuery(id+"F4.wireOp",EDGE,"E10"),sQuery(id+"F4.wireOp",EDGE,"E11"),sQuery(id+"F4.wireOp",EDGE,"E12"),sQuery(id+"F4.wireOp",EDGE,"E13"),sQuery(id+"F4.wireOp",EDGE,"E14"),sQuery(id+"F4.wireOp",EDGE,"E15"),sQuery(id+"F4.wireOp",EDGE,"E16"),sQuery(id+"F4.wireOp",EDGE,"E17"),sQuery(id+"F4.wireOp",EDGE,"E18"),sQuery(id+"F4.wireOp",EDGE,"E19"),sQuery(id+"F4.wireOp",EDGE,"E20"),sQuery(id+"F4.wireOp",EDGE,"E21"),sQuery(id+"F4.wireOp",EDGE,"E22"),sQuery(id+"F4.wireOp",EDGE,"E23"),sQuery(id+"F4.wireOp",EDGE,"E24"),sQuery(id+"F4.wireOp",EDGE,"E25"),sQuery(id+"F4.wireOp",EDGE,"E26"),sQuery(id+"F4.wireOp",EDGE,"E26"),sQuery(id+"F4.wireOp",EDGE,"E27"),sQuery(id+"F4.wireOp",EDGE,"E28"),sQuery(id+"F4.wireOp",EDGE,"E29"),sQuery(id+"F4.wireOp",EDGE,"E30"),sQuery(id+"F4.wireOp",EDGE,"E31"),sQuery(id+"F4.wireOp",EDGE,"E32"),sQuery(id+"F4.wireOp",EDGE,"E33"),sQuery(id+"F4.wireOp",EDGE,"E34"),sQuery(id+"F4.wireOp",EDGE,"E35"),sQuery(id+"F4.wireOp",EDGE,"E36"),sQuery(id+"F4.wireOp",EDGE,"E37"),sQuery(id+"F4.wireOp",EDGE,"E38"),sQuery(id+"F4.wireOp",EDGE,"E39"),sQuery(id+"F4.wireOp",EDGE,"E40"),sQuery(id+"F4.wireOp",EDGE,"E41"),sQuery(id+"F4.wireOp",EDGE,"E42"),sQuery(id+"F4.wireOp",EDGE,"E43"),sQuery(id+"F4.wireOp",EDGE,"E44"),sQuery(id+"F4.wireOp",EDGE,"E45"),sQuery(id+"F4.wireOp",EDGE,"E46"),sQuery(id+"F4.wireOp",EDGE,"E47"),sQuery(id+"F4.wireOp",EDGE,"E48"),sQuery(id+"F4.wireOp",EDGE,"E49"),sQuery(id+"F4.wireOp",EDGE,"E50"),sQuery(id+"F4.wireOp",EDGE,"E51"),sQuery(id+"F4.wireOp",EDGE,"E52"),sQuery(id+"F4.wireOp",EDGE,"E53"),sQuery(id+"F4.wireOp",EDGE,"E54"),sQuery(id+"F4.wireOp",EDGE,"E55"),sQuery(id+"F4.wireOp",EDGE,"E56"),sQuery(id+"F4.wireOp",EDGE,"E57"),sQuery(id+"F4.wireOp",EDGE,"E58"),sQuery(id+"F4.wireOp",EDGE,"E59"),sQuery(id+"F4.wireOp",EDGE,"E60"),sQuery(id+"F4.wireOp",EDGE,"E61"),sQuery(id+"F4.wireOp",EDGE,"E62"),sQuery(id+"F4.wireOp",EDGE,"E63"),sQuery(id+"F4.wireOp",EDGE,"E64"),sQuery(id+"F4.wireOp",EDGE,"E65"),sQuery(id+"F4.wireOp",EDGE,"E65"),sQuery(id+"F4.wireOp",EDGE,"E66"),sQuery(id+"F4.wireOp",EDGE,"E67"),sQuery(id+"F4.wireOp",EDGE,"E68"),sQuery(id+"F4.wireOp",EDGE,"E69"),sQuery(id+"F4.wireOp",EDGE,"E70"),sQuery(id+"F4.wireOp",EDGE,"E71"),sQuery(id+"F4.wireOp",EDGE,"E72"),sQuery(id+"F4.wireOp",EDGE,"E73"),sQuery(id+"F4.wireOp",EDGE,"E74"),sQuery(id+"F4.wireOp",EDGE,"E75"),sQuery(id+"F4.wireOp",EDGE,"E76"),sQuery(id+"F4.wireOp",EDGE,"E77"),sQuery(id+"F4.wireOp",EDGE,"E78"),sQuery(id+"F4.wireOp",EDGE,"E79"),sQuery(id+"F4.wireOp",EDGE,"E80"),sQuery(id+"F4.wireOp",EDGE,"E81"),sQuery(id+"F4.wireOp",EDGE,"E82"),sQuery(id+"F4.wireOp",EDGE,"E83"),sQuery(id+"F4.wireOp",EDGE,"E84"),sQuery(id+"F4.wireOp",EDGE,"E85"),sQuery(id+"F4.wireOp",EDGE,"E86"),sQuery(id+"F4.wireOp",EDGE,"E87"),sQuery(id+"F4.wireOp",EDGE,"E88"),sQuery(id+"F4.wireOp",EDGE,"E89"),sQuery(id+"F4.wireOp",EDGE,"E90"),sQuery(id+"F4.wireOp",EDGE,"E91"),sQuery(id+"F4.wireOp",EDGE,"E92"),sQuery(id+"F4.wireOp",EDGE,"E93"),sQuery(id+"F4.wireOp",EDGE,"E94"),sQuery(id+"F4.wireOp",EDGE,"E95"),sQuery(id+"F4.wireOp",EDGE,"E96"),sQuery(id+"F4.wireOp",EDGE,"E97"),sQuery(id+"F4.wireOp",EDGE,"E98"),sQuery(id+"F4.wireOp",EDGE,"E99"),sQuery(id+"F4.wireOp",EDGE,"E100"),sQuery(id+"F4.wireOp",EDGE,"E101"),sQuery(id+"F4.wireOp",EDGE,"E102"),sQuery(id+"F4.wireOp",EDGE,"E103"),sQuery(id+"F4.wireOp",EDGE,"E104"),sQuery(id+"F4.wireOp",EDGE,"E105"),sQuery(id+"F4.wireOp",EDGE,"E106"),sQuery(id+"F4.wireOp",EDGE,"E107"),sQuery(id+"F4.wireOp",EDGE,"E108"),sQuery(id+"F4.wireOp",EDGE,"E109"),sQuery(id+"F4.wireOp",EDGE,"E110"),sQuery(id+"F4.wireOp",EDGE,"E111"),sQuery(id+"F4.wireOp",EDGE,"E112"),sQuery(id+"F4.wireOp",EDGE,"E113"),sQuery(id+"F4.wireOp",EDGE,"E114"),sQuery(id+"F4.wireOp",EDGE,"E114"),sQuery(id+"F4.wireOp",EDGE,"E115"),sQuery(id+"F4.wireOp",EDGE,"E116")])]});
            var Q1;
            Q1=makeQuery(id+"F5.opExtrude","SWEPT_BODY",BODY,{"disambiguationData":[OSD([sQuery(id+"F4.wireOp",EDGE,"E117"),sQuery(id+"F4.wireOp",EDGE,"E118"),sQuery(id+"F4.wireOp",EDGE,"E119"),sQuery(id+"F4.wireOp",EDGE,"E120"),sQuery(id+"F4.wireOp",EDGE,"E121"),sQuery(id+"F4.wireOp",EDGE,"E122"),sQuery(id+"F4.wireOp",EDGE,"E123"),sQuery(id+"F4.wireOp",EDGE,"E124"),sQuery(id+"F4.wireOp",EDGE,"E125"),sQuery(id+"F4.wireOp",EDGE,"E126"),sQuery(id+"F4.wireOp",EDGE,"E127"),sQuery(id+"F4.wireOp",EDGE,"E128"),sQuery(id+"F4.wireOp",EDGE,"E129"),sQuery(id+"F4.wireOp",EDGE,"E130"),sQuery(id+"F4.wireOp",EDGE,"E131"),sQuery(id+"F4.wireOp",EDGE,"E132"),sQuery(id+"F4.wireOp",EDGE,"E133"),sQuery(id+"F4.wireOp",EDGE,"E133"),sQuery(id+"F4.wireOp",EDGE,"E134"),sQuery(id+"F4.wireOp",EDGE,"E135"),sQuery(id+"F4.wireOp",EDGE,"E136"),sQuery(id+"F4.wireOp",EDGE,"E137"),sQuery(id+"F4.wireOp",EDGE,"E138"),sQuery(id+"F4.wireOp",EDGE,"E139"),sQuery(id+"F4.wireOp",EDGE,"E140"),sQuery(id+"F4.wireOp",EDGE,"E141"),sQuery(id+"F4.wireOp",EDGE,"E142"),sQuery(id+"F4.wireOp",EDGE,"E143"),sQuery(id+"F4.wireOp",EDGE,"E144"),sQuery(id+"F4.wireOp",EDGE,"E145"),sQuery(id+"F4.wireOp",EDGE,"E146"),sQuery(id+"F4.wireOp",EDGE,"E147"),sQuery(id+"F4.wireOp",EDGE,"E148"),sQuery(id+"F4.wireOp",EDGE,"E149"),sQuery(id+"F4.wireOp",EDGE,"E150"),sQuery(id+"F4.wireOp",EDGE,"E151"),sQuery(id+"F4.wireOp",EDGE,"E152"),sQuery(id+"F4.wireOp",EDGE,"E153"),sQuery(id+"F4.wireOp",EDGE,"E154"),sQuery(id+"F4.wireOp",EDGE,"E155"),sQuery(id+"F4.wireOp",EDGE,"E156"),sQuery(id+"F4.wireOp",EDGE,"E157"),sQuery(id+"F4.wireOp",EDGE,"E158"),sQuery(id+"F4.wireOp",EDGE,"E159"),sQuery(id+"F4.wireOp",EDGE,"E160"),sQuery(id+"F4.wireOp",EDGE,"E161"),sQuery(id+"F4.wireOp",EDGE,"E162"),sQuery(id+"F4.wireOp",EDGE,"E162"),sQuery(id+"F4.wireOp",EDGE,"E162"),sQuery(id+"F4.wireOp",EDGE,"E163"),sQuery(id+"F4.wireOp",EDGE,"E164"),sQuery(id+"F4.wireOp",EDGE,"E165"),sQuery(id+"F4.wireOp",EDGE,"E166"),sQuery(id+"F4.wireOp",EDGE,"E167"),sQuery(id+"F4.wireOp",EDGE,"E168"),sQuery(id+"F4.wireOp",EDGE,"E169"),sQuery(id+"F4.wireOp",EDGE,"E170"),sQuery(id+"F4.wireOp",EDGE,"E171"),sQuery(id+"F4.wireOp",EDGE,"E171"),sQuery(id+"F4.wireOp",EDGE,"E172"),sQuery(id+"F4.wireOp",EDGE,"E173"),sQuery(id+"F4.wireOp",EDGE,"E174"),sQuery(id+"F4.wireOp",EDGE,"E175"),sQuery(id+"F4.wireOp",EDGE,"E176"),sQuery(id+"F4.wireOp",EDGE,"E177"),sQuery(id+"F4.wireOp",EDGE,"E178"),sQuery(id+"F4.wireOp",EDGE,"E179"),sQuery(id+"F4.wireOp",EDGE,"E180"),sQuery(id+"F4.wireOp",EDGE,"E181"),sQuery(id+"F4.wireOp",EDGE,"E182"),sQuery(id+"F4.wireOp",EDGE,"E183"),sQuery(id+"F4.wireOp",EDGE,"E184"),sQuery(id+"F4.wireOp",EDGE,"E185"),sQuery(id+"F4.wireOp",EDGE,"E186"),sQuery(id+"F4.wireOp",EDGE,"E187"),sQuery(id+"F4.wireOp",EDGE,"E188"),sQuery(id+"F4.wireOp",EDGE,"E189"),sQuery(id+"F4.wireOp",EDGE,"E190"),sQuery(id+"F4.wireOp",EDGE,"E191"),sQuery(id+"F4.wireOp",EDGE,"E192"),sQuery(id+"F4.wireOp",EDGE,"E193"),sQuery(id+"F4.wireOp",EDGE,"E194"),sQuery(id+"F4.wireOp",EDGE,"E195"),sQuery(id+"F4.wireOp",EDGE,"E196"),sQuery(id+"F4.wireOp",EDGE,"E197"),sQuery(id+"F4.wireOp",EDGE,"E198"),sQuery(id+"F4.wireOp",EDGE,"E199"),sQuery(id+"F4.wireOp",EDGE,"E200"),sQuery(id+"F4.wireOp",EDGE,"E201"),sQuery(id+"F4.wireOp",EDGE,"E202"),sQuery(id+"F4.wireOp",EDGE,"E203"),sQuery(id+"F4.wireOp",EDGE,"E204"),sQuery(id+"F4.wireOp",EDGE,"E205"),sQuery(id+"F4.wireOp",EDGE,"E206"),sQuery(id+"F4.wireOp",EDGE,"E207"),sQuery(id+"F4.wireOp",EDGE,"E208"),sQuery(id+"F4.wireOp",EDGE,"E209"),sQuery(id+"F4.wireOp",EDGE,"E210"),sQuery(id+"F4.wireOp",EDGE,"E211"),sQuery(id+"F4.wireOp",EDGE,"E212"),sQuery(id+"F4.wireOp",EDGE,"E213"),sQuery(id+"F4.wireOp",EDGE,"E214"),sQuery(id+"F4.wireOp",EDGE,"E215"),sQuery(id+"F4.wireOp",EDGE,"E216"),sQuery(id+"F4.wireOp",EDGE,"E217"),sQuery(id+"F4.wireOp",EDGE,"E218"),sQuery(id+"F4.wireOp",EDGE,"E219"),sQuery(id+"F4.wireOp",EDGE,"E220"),sQuery(id+"F4.wireOp",EDGE,"E221"),sQuery(id+"F4.wireOp",EDGE,"E222"),sQuery(id+"F4.wireOp",EDGE,"E223"),sQuery(id+"F4.wireOp",EDGE,"E224"),sQuery(id+"F4.wireOp",EDGE,"E225"),sQuery(id+"F4.wireOp",EDGE,"E226"),sQuery(id+"F4.wireOp",EDGE,"E227"),sQuery(id+"F4.wireOp",EDGE,"E228"),sQuery(id+"F4.wireOp",EDGE,"E229"),sQuery(id+"F4.wireOp",EDGE,"E230"),sQuery(id+"F4.wireOp",EDGE,"E231"),sQuery(id+"F4.wireOp",EDGE,"E232"),sQuery(id+"F4.wireOp",EDGE,"E233"),sQuery(id+"F4.wireOp",EDGE,"E234"),sQuery(id+"F4.wireOp",EDGE,"E235"),sQuery(id+"F4.wireOp",EDGE,"E236"),sQuery(id+"F4.wireOp",EDGE,"E237"),sQuery(id+"F4.wireOp",EDGE,"E238"),sQuery(id+"F4.wireOp",EDGE,"E239"),sQuery(id+"F4.wireOp",EDGE,"E240"),sQuery(id+"F4.wireOp",EDGE,"E241"),sQuery(id+"F4.wireOp",EDGE,"E242"),sQuery(id+"F4.wireOp",EDGE,"E243"),sQuery(id+"F4.wireOp",EDGE,"E244"),sQuery(id+"F4.wireOp",EDGE,"E245"),sQuery(id+"F4.wireOp",EDGE,"E246"),sQuery(id+"F4.wireOp",EDGE,"E247"),sQuery(id+"F4.wireOp",EDGE,"E248"),sQuery(id+"F4.wireOp",EDGE,"E249"),sQuery(id+"F4.wireOp",EDGE,"E250"),sQuery(id+"F4.wireOp",EDGE,"E250"),sQuery(id+"F4.wireOp",EDGE,"E251"),sQuery(id+"F4.wireOp",EDGE,"E252"),sQuery(id+"F4.wireOp",EDGE,"E253"),sQuery(id+"F4.wireOp",EDGE,"E254"),sQuery(id+"F4.wireOp",EDGE,"E255"),sQuery(id+"F4.wireOp",EDGE,"E256"),sQuery(id+"F4.wireOp",EDGE,"E257"),sQuery(id+"F4.wireOp",EDGE,"E258"),sQuery(id+"F4.wireOp",EDGE,"E259"),sQuery(id+"F4.wireOp",EDGE,"E260"),sQuery(id+"F4.wireOp",EDGE,"E261"),sQuery(id+"F4.wireOp",EDGE,"E262"),sQuery(id+"F4.wireOp",EDGE,"E262"),sQuery(id+"F4.wireOp",EDGE,"E262"),sQuery(id+"F4.wireOp",EDGE,"E263"),sQuery(id+"F4.wireOp",EDGE,"E264"),sQuery(id+"F4.wireOp",EDGE,"E265"),sQuery(id+"F4.wireOp",EDGE,"E266"),sQuery(id+"F4.wireOp",EDGE,"E267"),sQuery(id+"F4.wireOp",EDGE,"E268"),sQuery(id+"F4.wireOp",EDGE,"E269"),sQuery(id+"F4.wireOp",EDGE,"E270"),sQuery(id+"F4.wireOp",EDGE,"E271"),sQuery(id+"F4.wireOp",EDGE,"E272"),sQuery(id+"F4.wireOp",EDGE,"E273"),sQuery(id+"F4.wireOp",EDGE,"E274"),sQuery(id+"F4.wireOp",EDGE,"E275"),sQuery(id+"F4.wireOp",EDGE,"E276"),sQuery(id+"F4.wireOp",EDGE,"E277"),sQuery(id+"F4.wireOp",EDGE,"E278"),sQuery(id+"F4.wireOp",EDGE,"E279"),sQuery(id+"F4.wireOp",EDGE,"E280"),sQuery(id+"F4.wireOp",EDGE,"E281"),sQuery(id+"F4.wireOp",EDGE,"E282"),sQuery(id+"F4.wireOp",EDGE,"E283"),sQuery(id+"F4.wireOp",EDGE,"E284"),sQuery(id+"F4.wireOp",EDGE,"E285"),sQuery(id+"F4.wireOp",EDGE,"E286"),sQuery(id+"F4.wireOp",EDGE,"E287"),sQuery(id+"F4.wireOp",EDGE,"E288")])]});
            var Q2;
            Q2=makeQuery(id+"F5.opExtrude","SWEPT_BODY",BODY,{"disambiguationData":[OSD([sQuery(id+"F4.wireOp",EDGE,"E289"),sQuery(id+"F4.wireOp",EDGE,"E290"),sQuery(id+"F4.wireOp",EDGE,"E291"),sQuery(id+"F4.wireOp",EDGE,"E292"),sQuery(id+"F4.wireOp",EDGE,"E293"),sQuery(id+"F4.wireOp",EDGE,"E294"),sQuery(id+"F4.wireOp",EDGE,"E295"),sQuery(id+"F4.wireOp",EDGE,"E296"),sQuery(id+"F4.wireOp",EDGE,"E297"),sQuery(id+"F4.wireOp",EDGE,"E298"),sQuery(id+"F4.wireOp",EDGE,"E299"),sQuery(id+"F4.wireOp",EDGE,"E300"),sQuery(id+"F4.wireOp",EDGE,"E301"),sQuery(id+"F4.wireOp",EDGE,"E302"),sQuery(id+"F4.wireOp",EDGE,"E303"),sQuery(id+"F4.wireOp",EDGE,"E304"),sQuery(id+"F4.wireOp",EDGE,"E305"),sQuery(id+"F4.wireOp",EDGE,"E306"),sQuery(id+"F4.wireOp",EDGE,"E307"),sQuery(id+"F4.wireOp",EDGE,"E308"),sQuery(id+"F4.wireOp",EDGE,"E309"),sQuery(id+"F4.wireOp",EDGE,"E310"),sQuery(id+"F4.wireOp",EDGE,"E311"),sQuery(id+"F4.wireOp",EDGE,"E312"),sQuery(id+"F4.wireOp",EDGE,"E313"),sQuery(id+"F4.wireOp",EDGE,"E314"),sQuery(id+"F4.wireOp",EDGE,"E315"),sQuery(id+"F4.wireOp",EDGE,"E316"),sQuery(id+"F4.wireOp",EDGE,"E317"),sQuery(id+"F4.wireOp",EDGE,"E318"),sQuery(id+"F4.wireOp",EDGE,"E319"),sQuery(id+"F4.wireOp",EDGE,"E320"),sQuery(id+"F4.wireOp",EDGE,"E321"),sQuery(id+"F4.wireOp",EDGE,"E322"),sQuery(id+"F4.wireOp",EDGE,"E323"),sQuery(id+"F4.wireOp",EDGE,"E324"),sQuery(id+"F4.wireOp",EDGE,"E325"),sQuery(id+"F4.wireOp",EDGE,"E326"),sQuery(id+"F4.wireOp",EDGE,"E327"),sQuery(id+"F4.wireOp",EDGE,"E328"),sQuery(id+"F4.wireOp",EDGE,"E329"),sQuery(id+"F4.wireOp",EDGE,"E330"),sQuery(id+"F4.wireOp",EDGE,"E331"),sQuery(id+"F4.wireOp",EDGE,"E332"),sQuery(id+"F4.wireOp",EDGE,"E333"),sQuery(id+"F4.wireOp",EDGE,"E334"),sQuery(id+"F4.wireOp",EDGE,"E335"),sQuery(id+"F4.wireOp",EDGE,"E336"),sQuery(id+"F4.wireOp",EDGE,"E337"),sQuery(id+"F4.wireOp",EDGE,"E338"),sQuery(id+"F4.wireOp",EDGE,"E339"),sQuery(id+"F4.wireOp",EDGE,"E340"),sQuery(id+"F4.wireOp",EDGE,"E341"),sQuery(id+"F4.wireOp",EDGE,"E342"),sQuery(id+"F4.wireOp",EDGE,"E343"),sQuery(id+"F4.wireOp",EDGE,"E344"),sQuery(id+"F4.wireOp",EDGE,"E345"),sQuery(id+"F4.wireOp",EDGE,"E346"),sQuery(id+"F4.wireOp",EDGE,"E346"),sQuery(id+"F4.wireOp",EDGE,"E347"),sQuery(id+"F4.wireOp",EDGE,"E348"),sQuery(id+"F4.wireOp",EDGE,"E349"),sQuery(id+"F4.wireOp",EDGE,"E350"),sQuery(id+"F4.wireOp",EDGE,"E351"),sQuery(id+"F4.wireOp",EDGE,"E352"),sQuery(id+"F4.wireOp",EDGE,"E353"),sQuery(id+"F4.wireOp",EDGE,"E354"),sQuery(id+"F4.wireOp",EDGE,"E355"),sQuery(id+"F4.wireOp",EDGE,"E356"),sQuery(id+"F4.wireOp",EDGE,"E357"),sQuery(id+"F4.wireOp",EDGE,"E358"),sQuery(id+"F4.wireOp",EDGE,"E359"),sQuery(id+"F4.wireOp",EDGE,"E360"),sQuery(id+"F4.wireOp",EDGE,"E361"),sQuery(id+"F4.wireOp",EDGE,"E362"),sQuery(id+"F4.wireOp",EDGE,"E363"),sQuery(id+"F4.wireOp",EDGE,"E364"),sQuery(id+"F4.wireOp",EDGE,"E365"),sQuery(id+"F4.wireOp",EDGE,"E366"),sQuery(id+"F4.wireOp",EDGE,"E367"),sQuery(id+"F4.wireOp",EDGE,"E368"),sQuery(id+"F4.wireOp",EDGE,"E369"),sQuery(id+"F4.wireOp",EDGE,"E370"),sQuery(id+"F4.wireOp",EDGE,"E371"),sQuery(id+"F4.wireOp",EDGE,"E371"),sQuery(id+"F4.wireOp",EDGE,"E372"),sQuery(id+"F4.wireOp",EDGE,"E373"),sQuery(id+"F4.wireOp",EDGE,"E374"),sQuery(id+"F4.wireOp",EDGE,"E375"),sQuery(id+"F4.wireOp",EDGE,"E376"),sQuery(id+"F4.wireOp",EDGE,"E377"),sQuery(id+"F4.wireOp",EDGE,"E378"),sQuery(id+"F4.wireOp",EDGE,"E379"),sQuery(id+"F4.wireOp",EDGE,"E380"),sQuery(id+"F4.wireOp",EDGE,"E381"),sQuery(id+"F4.wireOp",EDGE,"E382"),sQuery(id+"F4.wireOp",EDGE,"E383"),sQuery(id+"F4.wireOp",EDGE,"E384"),sQuery(id+"F4.wireOp",EDGE,"E385"),sQuery(id+"F4.wireOp",EDGE,"E386"),sQuery(id+"F4.wireOp",EDGE,"E387"),sQuery(id+"F4.wireOp",EDGE,"E388"),sQuery(id+"F4.wireOp",EDGE,"E389"),sQuery(id+"F4.wireOp",EDGE,"E390"),sQuery(id+"F4.wireOp",EDGE,"E391"),sQuery(id+"F4.wireOp",EDGE,"E392"),sQuery(id+"F4.wireOp",EDGE,"E392"),sQuery(id+"F4.wireOp",EDGE,"E393"),sQuery(id+"F4.wireOp",EDGE,"E394"),sQuery(id+"F4.wireOp",EDGE,"E395"),sQuery(id+"F4.wireOp",EDGE,"E396"),sQuery(id+"F4.wireOp",EDGE,"E397"),sQuery(id+"F4.wireOp",EDGE,"E398"),sQuery(id+"F4.wireOp",EDGE,"E399"),sQuery(id+"F4.wireOp",EDGE,"E400"),sQuery(id+"F4.wireOp",EDGE,"E401"),sQuery(id+"F4.wireOp",EDGE,"E402"),sQuery(id+"F4.wireOp",EDGE,"E403"),sQuery(id+"F4.wireOp",EDGE,"E404"),sQuery(id+"F4.wireOp",EDGE,"E405"),sQuery(id+"F4.wireOp",EDGE,"E406"),sQuery(id+"F4.wireOp",EDGE,"E407"),sQuery(id+"F4.wireOp",EDGE,"E408"),sQuery(id+"F4.wireOp",EDGE,"E409"),sQuery(id+"F4.wireOp",EDGE,"E410"),sQuery(id+"F4.wireOp",EDGE,"E411"),sQuery(id+"F4.wireOp",EDGE,"E412"),sQuery(id+"F4.wireOp",EDGE,"E413"),sQuery(id+"F4.wireOp",EDGE,"E414"),sQuery(id+"F4.wireOp",EDGE,"E415"),sQuery(id+"F4.wireOp",EDGE,"E416"),sQuery(id+"F4.wireOp",EDGE,"E417"),sQuery(id+"F4.wireOp",EDGE,"E418"),sQuery(id+"F4.wireOp",EDGE,"E419"),sQuery(id+"F4.wireOp",EDGE,"E420"),sQuery(id+"F4.wireOp",EDGE,"E421"),sQuery(id+"F4.wireOp",EDGE,"E422"),sQuery(id+"F4.wireOp",EDGE,"E423"),sQuery(id+"F4.wireOp",EDGE,"E424"),sQuery(id+"F4.wireOp",EDGE,"E425"),sQuery(id+"F4.wireOp",EDGE,"E426"),sQuery(id+"F4.wireOp",EDGE,"E427"),sQuery(id+"F4.wireOp",EDGE,"E428"),sQuery(id+"F4.wireOp",EDGE,"E429"),sQuery(id+"F4.wireOp",EDGE,"E430"),sQuery(id+"F4.wireOp",EDGE,"E431"),sQuery(id+"F4.wireOp",EDGE,"E431"),sQuery(id+"F4.wireOp",EDGE,"E432"),sQuery(id+"F4.wireOp",EDGE,"E433"),sQuery(id+"F4.wireOp",EDGE,"E434"),sQuery(id+"F4.wireOp",EDGE,"E435"),sQuery(id+"F4.wireOp",EDGE,"E436"),sQuery(id+"F4.wireOp",EDGE,"E436"),sQuery(id+"F4.wireOp",EDGE,"E437"),sQuery(id+"F4.wireOp",EDGE,"E438"),sQuery(id+"F4.wireOp",EDGE,"E439"),sQuery(id+"F4.wireOp",EDGE,"E440"),sQuery(id+"F4.wireOp",EDGE,"E441"),sQuery(id+"F4.wireOp",EDGE,"E442"),sQuery(id+"F4.wireOp",EDGE,"E443"),sQuery(id+"F4.wireOp",EDGE,"E444"),sQuery(id+"F4.wireOp",EDGE,"E445"),sQuery(id+"F4.wireOp",EDGE,"E446"),sQuery(id+"F4.wireOp",EDGE,"E447"),sQuery(id+"F4.wireOp",EDGE,"E448"),sQuery(id+"F4.wireOp",EDGE,"E448"),sQuery(id+"F4.wireOp",EDGE,"E449"),sQuery(id+"F4.wireOp",EDGE,"E450"),sQuery(id+"F4.wireOp",EDGE,"E451"),sQuery(id+"F4.wireOp",EDGE,"E452"),sQuery(id+"F4.wireOp",EDGE,"E453"),sQuery(id+"F4.wireOp",EDGE,"E454"),sQuery(id+"F4.wireOp",EDGE,"E455"),sQuery(id+"F4.wireOp",EDGE,"E456"),sQuery(id+"F4.wireOp",EDGE,"E457"),sQuery(id+"F4.wireOp",EDGE,"E458"),sQuery(id+"F4.wireOp",EDGE,"E459"),sQuery(id+"F4.wireOp",EDGE,"E460"),sQuery(id+"F4.wireOp",EDGE,"E461")])]});
            var Q3;
            Q3=makeQuery(id+"F5.opExtrude","SWEPT_BODY",BODY,{"disambiguationData":[OSD([sQuery(id+"F4.wireOp",EDGE,"E462"),sQuery(id+"F4.wireOp",EDGE,"E463"),sQuery(id+"F4.wireOp",EDGE,"E464"),sQuery(id+"F4.wireOp",EDGE,"E465"),sQuery(id+"F4.wireOp",EDGE,"E466"),sQuery(id+"F4.wireOp",EDGE,"E467"),sQuery(id+"F4.wireOp",EDGE,"E468"),sQuery(id+"F4.wireOp",EDGE,"E469"),sQuery(id+"F4.wireOp",EDGE,"E470"),sQuery(id+"F4.wireOp",EDGE,"E471"),sQuery(id+"F4.wireOp",EDGE,"E472"),sQuery(id+"F4.wireOp",EDGE,"E473"),sQuery(id+"F4.wireOp",EDGE,"E474"),sQuery(id+"F4.wireOp",EDGE,"E475"),sQuery(id+"F4.wireOp",EDGE,"E476"),sQuery(id+"F4.wireOp",EDGE,"E477"),sQuery(id+"F4.wireOp",EDGE,"E478"),sQuery(id+"F4.wireOp",EDGE,"E479"),sQuery(id+"F4.wireOp",EDGE,"E480"),sQuery(id+"F4.wireOp",EDGE,"E481"),sQuery(id+"F4.wireOp",EDGE,"E482"),sQuery(id+"F4.wireOp",EDGE,"E483"),sQuery(id+"F4.wireOp",EDGE,"E484"),sQuery(id+"F4.wireOp",EDGE,"E485"),sQuery(id+"F4.wireOp",EDGE,"E486"),sQuery(id+"F4.wireOp",EDGE,"E487"),sQuery(id+"F4.wireOp",EDGE,"E488"),sQuery(id+"F4.wireOp",EDGE,"E489"),sQuery(id+"F4.wireOp",EDGE,"E490"),sQuery(id+"F4.wireOp",EDGE,"E491"),sQuery(id+"F4.wireOp",EDGE,"E492"),sQuery(id+"F4.wireOp",EDGE,"E493"),sQuery(id+"F4.wireOp",EDGE,"E494"),sQuery(id+"F4.wireOp",EDGE,"E495"),sQuery(id+"F4.wireOp",EDGE,"E496"),sQuery(id+"F4.wireOp",EDGE,"E497"),sQuery(id+"F4.wireOp",EDGE,"E498"),sQuery(id+"F4.wireOp",EDGE,"E499"),sQuery(id+"F4.wireOp",EDGE,"E500"),sQuery(id+"F4.wireOp",EDGE,"E501"),sQuery(id+"F4.wireOp",EDGE,"E502"),sQuery(id+"F4.wireOp",EDGE,"E503"),sQuery(id+"F4.wireOp",EDGE,"E504"),sQuery(id+"F4.wireOp",EDGE,"E505"),sQuery(id+"F4.wireOp",EDGE,"E506"),sQuery(id+"F4.wireOp",EDGE,"E507"),sQuery(id+"F4.wireOp",EDGE,"E508"),sQuery(id+"F4.wireOp",EDGE,"E509"),sQuery(id+"F4.wireOp",EDGE,"E510"),sQuery(id+"F4.wireOp",EDGE,"E511"),sQuery(id+"F4.wireOp",EDGE,"E512"),sQuery(id+"F4.wireOp",EDGE,"E513"),sQuery(id+"F4.wireOp",EDGE,"E514"),sQuery(id+"F4.wireOp",EDGE,"E515"),sQuery(id+"F4.wireOp",EDGE,"E516"),sQuery(id+"F4.wireOp",EDGE,"E517"),sQuery(id+"F4.wireOp",EDGE,"E518"),sQuery(id+"F4.wireOp",EDGE,"E519"),sQuery(id+"F4.wireOp",EDGE,"E520"),sQuery(id+"F4.wireOp",EDGE,"E521"),sQuery(id+"F4.wireOp",EDGE,"E522"),sQuery(id+"F4.wireOp",EDGE,"E523"),sQuery(id+"F4.wireOp",EDGE,"E524"),sQuery(id+"F4.wireOp",EDGE,"E525"),sQuery(id+"F4.wireOp",EDGE,"E525"),sQuery(id+"F4.wireOp",EDGE,"E525"),sQuery(id+"F4.wireOp",EDGE,"E526"),sQuery(id+"F4.wireOp",EDGE,"E527"),sQuery(id+"F4.wireOp",EDGE,"E528"),sQuery(id+"F4.wireOp",EDGE,"E529"),sQuery(id+"F4.wireOp",EDGE,"E530"),sQuery(id+"F4.wireOp",EDGE,"E531"),sQuery(id+"F4.wireOp",EDGE,"E531"),sQuery(id+"F4.wireOp",EDGE,"E531"),sQuery(id+"F4.wireOp",EDGE,"E532"),sQuery(id+"F4.wireOp",EDGE,"E533"),sQuery(id+"F4.wireOp",EDGE,"E534"),sQuery(id+"F4.wireOp",EDGE,"E535"),sQuery(id+"F4.wireOp",EDGE,"E536"),sQuery(id+"F4.wireOp",EDGE,"E537"),sQuery(id+"F4.wireOp",EDGE,"E538"),sQuery(id+"F4.wireOp",EDGE,"E539"),sQuery(id+"F4.wireOp",EDGE,"E540"),sQuery(id+"F4.wireOp",EDGE,"E541"),sQuery(id+"F4.wireOp",EDGE,"E542"),sQuery(id+"F4.wireOp",EDGE,"E543"),sQuery(id+"F4.wireOp",EDGE,"E544"),sQuery(id+"F4.wireOp",EDGE,"E545"),sQuery(id+"F4.wireOp",EDGE,"E546"),sQuery(id+"F4.wireOp",EDGE,"E547"),sQuery(id+"F4.wireOp",EDGE,"E548"),sQuery(id+"F4.wireOp",EDGE,"E549"),sQuery(id+"F4.wireOp",EDGE,"E550"),sQuery(id+"F4.wireOp",EDGE,"E551"),sQuery(id+"F4.wireOp",EDGE,"E552"),sQuery(id+"F4.wireOp",EDGE,"E553"),sQuery(id+"F4.wireOp",EDGE,"E554"),sQuery(id+"F4.wireOp",EDGE,"E555"),sQuery(id+"F4.wireOp",EDGE,"E556"),sQuery(id+"F4.wireOp",EDGE,"E557"),sQuery(id+"F4.wireOp",EDGE,"E558"),sQuery(id+"F4.wireOp",EDGE,"E559"),sQuery(id+"F4.wireOp",EDGE,"E560"),sQuery(id+"F4.wireOp",EDGE,"E561"),sQuery(id+"F4.wireOp",EDGE,"E562"),sQuery(id+"F4.wireOp",EDGE,"E562"),sQuery(id+"F4.wireOp",EDGE,"E563"),sQuery(id+"F4.wireOp",EDGE,"E564"),sQuery(id+"F4.wireOp",EDGE,"E565"),sQuery(id+"F4.wireOp",EDGE,"E566"),sQuery(id+"F4.wireOp",EDGE,"E567"),sQuery(id+"F4.wireOp",EDGE,"E565"),sQuery(id+"F4.wireOp",EDGE,"E568"),sQuery(id+"F4.wireOp",EDGE,"E569"),sQuery(id+"F4.wireOp",EDGE,"E569"),sQuery(id+"F4.wireOp",EDGE,"E570"),sQuery(id+"F4.wireOp",EDGE,"E571"),sQuery(id+"F4.wireOp",EDGE,"E572"),sQuery(id+"F4.wireOp",EDGE,"E573"),sQuery(id+"F4.wireOp",EDGE,"E574")])]});
            var Q4;
            Q4=makeQuery(id+"F5.opExtrude","SWEPT_BODY",BODY,{"disambiguationData":[OSD([sQuery(id+"F4.wireOp",EDGE,"E575"),sQuery(id+"F4.wireOp",EDGE,"E576"),sQuery(id+"F4.wireOp",EDGE,"E577"),sQuery(id+"F4.wireOp",EDGE,"E578"),sQuery(id+"F4.wireOp",EDGE,"E579"),sQuery(id+"F4.wireOp",EDGE,"E580"),sQuery(id+"F4.wireOp",EDGE,"E581"),sQuery(id+"F4.wireOp",EDGE,"E582"),sQuery(id+"F4.wireOp",EDGE,"E583"),sQuery(id+"F4.wireOp",EDGE,"E584"),sQuery(id+"F4.wireOp",EDGE,"E585"),sQuery(id+"F4.wireOp",EDGE,"E586"),sQuery(id+"F4.wireOp",EDGE,"E587"),sQuery(id+"F4.wireOp",EDGE,"E588"),sQuery(id+"F4.wireOp",EDGE,"E589"),sQuery(id+"F4.wireOp",EDGE,"E590"),sQuery(id+"F4.wireOp",EDGE,"E591"),sQuery(id+"F4.wireOp",EDGE,"E592"),sQuery(id+"F4.wireOp",EDGE,"E593"),sQuery(id+"F4.wireOp",EDGE,"E594"),sQuery(id+"F4.wireOp",EDGE,"E595"),sQuery(id+"F4.wireOp",EDGE,"E596"),sQuery(id+"F4.wireOp",EDGE,"E597"),sQuery(id+"F4.wireOp",EDGE,"E598"),sQuery(id+"F4.wireOp",EDGE,"E599"),sQuery(id+"F4.wireOp",EDGE,"E600"),sQuery(id+"F4.wireOp",EDGE,"E601"),sQuery(id+"F4.wireOp",EDGE,"E602"),sQuery(id+"F4.wireOp",EDGE,"E603")])]});
            var Q5;
            Q5=makeQuery(id+"F5.opExtrude","SWEPT_BODY",BODY,{"disambiguationData":[OSD([sQuery(id+"F4.wireOp",EDGE,"E604"),sQuery(id+"F4.wireOp",EDGE,"E605"),sQuery(id+"F4.wireOp",EDGE,"E606"),sQuery(id+"F4.wireOp",EDGE,"E607"),sQuery(id+"F4.wireOp",EDGE,"E608"),sQuery(id+"F4.wireOp",EDGE,"E609"),sQuery(id+"F4.wireOp",EDGE,"E610"),sQuery(id+"F4.wireOp",EDGE,"E611"),sQuery(id+"F4.wireOp",EDGE,"E612"),sQuery(id+"F4.wireOp",EDGE,"E613"),sQuery(id+"F4.wireOp",EDGE,"E614"),sQuery(id+"F4.wireOp",EDGE,"E615"),sQuery(id+"F4.wireOp",EDGE,"E616"),sQuery(id+"F4.wireOp",EDGE,"E617"),sQuery(id+"F4.wireOp",EDGE,"E617"),sQuery(id+"F4.wireOp",EDGE,"E618"),sQuery(id+"F4.wireOp",EDGE,"E619"),sQuery(id+"F4.wireOp",EDGE,"E620"),sQuery(id+"F4.wireOp",EDGE,"E621"),sQuery(id+"F4.wireOp",EDGE,"E622"),sQuery(id+"F4.wireOp",EDGE,"E623"),sQuery(id+"F4.wireOp",EDGE,"E624"),sQuery(id+"F4.wireOp",EDGE,"E625"),sQuery(id+"F4.wireOp",EDGE,"E626"),sQuery(id+"F4.wireOp",EDGE,"E627"),sQuery(id+"F4.wireOp",EDGE,"E628"),sQuery(id+"F4.wireOp",EDGE,"E629"),sQuery(id+"F4.wireOp",EDGE,"E630"),sQuery(id+"F4.wireOp",EDGE,"E631"),sQuery(id+"F4.wireOp",EDGE,"E632"),sQuery(id+"F4.wireOp",EDGE,"E633"),sQuery(id+"F4.wireOp",EDGE,"E634"),sQuery(id+"F4.wireOp",EDGE,"E635"),sQuery(id+"F4.wireOp",EDGE,"E636"),sQuery(id+"F4.wireOp",EDGE,"E637"),sQuery(id+"F4.wireOp",EDGE,"E638"),sQuery(id+"F4.wireOp",EDGE,"E639"),sQuery(id+"F4.wireOp",EDGE,"E640"),sQuery(id+"F4.wireOp",EDGE,"E641"),sQuery(id+"F4.wireOp",EDGE,"E642"),sQuery(id+"F4.wireOp",EDGE,"E643"),sQuery(id+"F4.wireOp",EDGE,"E644"),sQuery(id+"F4.wireOp",EDGE,"E645"),sQuery(id+"F4.wireOp",EDGE,"E646"),sQuery(id+"F4.wireOp",EDGE,"E647"),sQuery(id+"F4.wireOp",EDGE,"E648"),sQuery(id+"F4.wireOp",EDGE,"E649"),sQuery(id+"F4.wireOp",EDGE,"E650"),sQuery(id+"F4.wireOp",EDGE,"E651"),sQuery(id+"F4.wireOp",EDGE,"E652"),sQuery(id+"F4.wireOp",EDGE,"E653"),sQuery(id+"F4.wireOp",EDGE,"E654"),sQuery(id+"F4.wireOp",EDGE,"E655"),sQuery(id+"F4.wireOp",EDGE,"E656"),sQuery(id+"F4.wireOp",EDGE,"E657"),sQuery(id+"F4.wireOp",EDGE,"E658"),sQuery(id+"F4.wireOp",EDGE,"E659"),sQuery(id+"F4.wireOp",EDGE,"E660"),sQuery(id+"F4.wireOp",EDGE,"E661"),sQuery(id+"F4.wireOp",EDGE,"E662"),sQuery(id+"F4.wireOp",EDGE,"E663"),sQuery(id+"F4.wireOp",EDGE,"E664"),sQuery(id+"F4.wireOp",EDGE,"E665"),sQuery(id+"F4.wireOp",EDGE,"E665"),sQuery(id+"F4.wireOp",EDGE,"E666"),sQuery(id+"F4.wireOp",EDGE,"E667"),sQuery(id+"F4.wireOp",EDGE,"E668"),sQuery(id+"F4.wireOp",EDGE,"E669"),sQuery(id+"F4.wireOp",EDGE,"E670"),sQuery(id+"F4.wireOp",EDGE,"E671"),sQuery(id+"F4.wireOp",EDGE,"E672"),sQuery(id+"F4.wireOp",EDGE,"E673"),sQuery(id+"F4.wireOp",EDGE,"E674"),sQuery(id+"F4.wireOp",EDGE,"E674"),sQuery(id+"F4.wireOp",EDGE,"E675"),sQuery(id+"F4.wireOp",EDGE,"E676"),sQuery(id+"F4.wireOp",EDGE,"E676"),sQuery(id+"F4.wireOp",EDGE,"E677"),sQuery(id+"F4.wireOp",EDGE,"E678"),sQuery(id+"F4.wireOp",EDGE,"E679"),sQuery(id+"F4.wireOp",EDGE,"E680"),sQuery(id+"F4.wireOp",EDGE,"E681"),sQuery(id+"F4.wireOp",EDGE,"E682"),sQuery(id+"F4.wireOp",EDGE,"E683"),sQuery(id+"F4.wireOp",EDGE,"E684"),sQuery(id+"F4.wireOp",EDGE,"E685"),sQuery(id+"F4.wireOp",EDGE,"E686"),sQuery(id+"F4.wireOp",EDGE,"E687"),sQuery(id+"F4.wireOp",EDGE,"E687"),sQuery(id+"F4.wireOp",EDGE,"E688"),sQuery(id+"F4.wireOp",EDGE,"E689"),sQuery(id+"F4.wireOp",EDGE,"E690"),sQuery(id+"F4.wireOp",EDGE,"E691"),sQuery(id+"F4.wireOp",EDGE,"E692"),sQuery(id+"F4.wireOp",EDGE,"E693"),sQuery(id+"F4.wireOp",EDGE,"E694"),sQuery(id+"F4.wireOp",EDGE,"E695"),sQuery(id+"F4.wireOp",EDGE,"E696"),sQuery(id+"F4.wireOp",EDGE,"E697"),sQuery(id+"F4.wireOp",EDGE,"E698"),sQuery(id+"F4.wireOp",EDGE,"E699"),sQuery(id+"F4.wireOp",EDGE,"E700"),sQuery(id+"F4.wireOp",EDGE,"E701"),sQuery(id+"F4.wireOp",EDGE,"E702"),sQuery(id+"F4.wireOp",EDGE,"E703"),sQuery(id+"F4.wireOp",EDGE,"E704"),sQuery(id+"F4.wireOp",EDGE,"E705"),sQuery(id+"F4.wireOp",EDGE,"E706"),sQuery(id+"F4.wireOp",EDGE,"E707"),sQuery(id+"F4.wireOp",EDGE,"E708"),sQuery(id+"F4.wireOp",EDGE,"E708"),sQuery(id+"F4.wireOp",EDGE,"E708")])]});
            var Q6;
            Q6=makeQuery(id+"F5.opExtrude","SWEPT_BODY",BODY,{"disambiguationData":[OSD([sQuery(id+"F4.wireOp",EDGE,"E709"),sQuery(id+"F4.wireOp",EDGE,"E710"),sQuery(id+"F4.wireOp",EDGE,"E711"),sQuery(id+"F4.wireOp",EDGE,"E712"),sQuery(id+"F4.wireOp",EDGE,"E713"),sQuery(id+"F4.wireOp",EDGE,"E714"),sQuery(id+"F4.wireOp",EDGE,"E715"),sQuery(id+"F4.wireOp",EDGE,"E716"),sQuery(id+"F4.wireOp",EDGE,"E717"),sQuery(id+"F4.wireOp",EDGE,"E718"),sQuery(id+"F4.wireOp",EDGE,"E719"),sQuery(id+"F4.wireOp",EDGE,"E720"),sQuery(id+"F4.wireOp",EDGE,"E721"),sQuery(id+"F4.wireOp",EDGE,"E722"),sQuery(id+"F4.wireOp",EDGE,"E723"),sQuery(id+"F4.wireOp",EDGE,"E723"),sQuery(id+"F4.wireOp",EDGE,"E724"),sQuery(id+"F4.wireOp",EDGE,"E725"),sQuery(id+"F4.wireOp",EDGE,"E726"),sQuery(id+"F4.wireOp",EDGE,"E727"),sQuery(id+"F4.wireOp",EDGE,"E728"),sQuery(id+"F4.wireOp",EDGE,"E729"),sQuery(id+"F4.wireOp",EDGE,"E730"),sQuery(id+"F4.wireOp",EDGE,"E731"),sQuery(id+"F4.wireOp",EDGE,"E732"),sQuery(id+"F4.wireOp",EDGE,"E733"),sQuery(id+"F4.wireOp",EDGE,"E734"),sQuery(id+"F4.wireOp",EDGE,"E735"),sQuery(id+"F4.wireOp",EDGE,"E736"),sQuery(id+"F4.wireOp",EDGE,"E737"),sQuery(id+"F4.wireOp",EDGE,"E738"),sQuery(id+"F4.wireOp",EDGE,"E739"),sQuery(id+"F4.wireOp",EDGE,"E740"),sQuery(id+"F4.wireOp",EDGE,"E741"),sQuery(id+"F4.wireOp",EDGE,"E742"),sQuery(id+"F4.wireOp",EDGE,"E743"),sQuery(id+"F4.wireOp",EDGE,"E744"),sQuery(id+"F4.wireOp",EDGE,"E745"),sQuery(id+"F4.wireOp",EDGE,"E746"),sQuery(id+"F4.wireOp",EDGE,"E747"),sQuery(id+"F4.wireOp",EDGE,"E748"),sQuery(id+"F4.wireOp",EDGE,"E749"),sQuery(id+"F4.wireOp",EDGE,"E750"),sQuery(id+"F4.wireOp",EDGE,"E751"),sQuery(id+"F4.wireOp",EDGE,"E752"),sQuery(id+"F4.wireOp",EDGE,"E753"),sQuery(id+"F4.wireOp",EDGE,"E754"),sQuery(id+"F4.wireOp",EDGE,"E755"),sQuery(id+"F4.wireOp",EDGE,"E756"),sQuery(id+"F4.wireOp",EDGE,"E757"),sQuery(id+"F4.wireOp",EDGE,"E758"),sQuery(id+"F4.wireOp",EDGE,"E758"),sQuery(id+"F4.wireOp",EDGE,"E758"),sQuery(id+"F4.wireOp",EDGE,"E759"),sQuery(id+"F4.wireOp",EDGE,"E760"),sQuery(id+"F4.wireOp",EDGE,"E760"),sQuery(id+"F4.wireOp",EDGE,"E761"),sQuery(id+"F4.wireOp",EDGE,"E762"),sQuery(id+"F4.wireOp",EDGE,"E763"),sQuery(id+"F4.wireOp",EDGE,"E764"),sQuery(id+"F4.wireOp",EDGE,"E765"),sQuery(id+"F4.wireOp",EDGE,"E766"),sQuery(id+"F4.wireOp",EDGE,"E767"),sQuery(id+"F4.wireOp",EDGE,"E768"),sQuery(id+"F4.wireOp",EDGE,"E768"),sQuery(id+"F4.wireOp",EDGE,"E768"),sQuery(id+"F4.wireOp",EDGE,"E769"),sQuery(id+"F4.wireOp",EDGE,"E770"),sQuery(id+"F4.wireOp",EDGE,"E771"),sQuery(id+"F4.wireOp",EDGE,"E772"),sQuery(id+"F4.wireOp",EDGE,"E773"),sQuery(id+"F4.wireOp",EDGE,"E774"),sQuery(id+"F4.wireOp",EDGE,"E775"),sQuery(id+"F4.wireOp",EDGE,"E776"),sQuery(id+"F4.wireOp",EDGE,"E777"),sQuery(id+"F4.wireOp",EDGE,"E778"),sQuery(id+"F4.wireOp",EDGE,"E779"),sQuery(id+"F4.wireOp",EDGE,"E780"),sQuery(id+"F4.wireOp",EDGE,"E781"),sQuery(id+"F4.wireOp",EDGE,"E782"),sQuery(id+"F4.wireOp",EDGE,"E783"),sQuery(id+"F4.wireOp",EDGE,"E784"),sQuery(id+"F4.wireOp",EDGE,"E785"),sQuery(id+"F4.wireOp",EDGE,"E786"),sQuery(id+"F4.wireOp",EDGE,"E787"),sQuery(id+"F4.wireOp",EDGE,"E788"),sQuery(id+"F4.wireOp",EDGE,"E789"),sQuery(id+"F4.wireOp",EDGE,"E790"),sQuery(id+"F4.wireOp",EDGE,"E791"),sQuery(id+"F4.wireOp",EDGE,"E792"),sQuery(id+"F4.wireOp",EDGE,"E793"),sQuery(id+"F4.wireOp",EDGE,"E794"),sQuery(id+"F4.wireOp",EDGE,"E795"),sQuery(id+"F4.wireOp",EDGE,"E796"),sQuery(id+"F4.wireOp",EDGE,"E797"),sQuery(id+"F4.wireOp",EDGE,"E798"),sQuery(id+"F4.wireOp",EDGE,"E799"),sQuery(id+"F4.wireOp",EDGE,"E800"),sQuery(id+"F4.wireOp",EDGE,"E801"),sQuery(id+"F4.wireOp",EDGE,"E802"),sQuery(id+"F4.wireOp",EDGE,"E803"),sQuery(id+"F4.wireOp",EDGE,"E804"),sQuery(id+"F4.wireOp",EDGE,"E805"),sQuery(id+"F4.wireOp",EDGE,"E806"),sQuery(id+"F4.wireOp",EDGE,"E807"),sQuery(id+"F4.wireOp",EDGE,"E808"),sQuery(id+"F4.wireOp",EDGE,"E809"),sQuery(id+"F4.wireOp",EDGE,"E810"),sQuery(id+"F4.wireOp",EDGE,"E811"),sQuery(id+"F4.wireOp",EDGE,"E812"),sQuery(id+"F4.wireOp",EDGE,"E813"),sQuery(id+"F4.wireOp",EDGE,"E814"),sQuery(id+"F4.wireOp",EDGE,"E815"),sQuery(id+"F4.wireOp",EDGE,"E816"),sQuery(id+"F4.wireOp",EDGE,"E817"),sQuery(id+"F4.wireOp",EDGE,"E818"),sQuery(id+"F4.wireOp",EDGE,"E819"),sQuery(id+"F4.wireOp",EDGE,"E820"),sQuery(id+"F4.wireOp",EDGE,"E821"),sQuery(id+"F4.wireOp",EDGE,"E822"),sQuery(id+"F4.wireOp",EDGE,"E823"),sQuery(id+"F4.wireOp",EDGE,"E824"),sQuery(id+"F4.wireOp",EDGE,"E825"),sQuery(id+"F4.wireOp",EDGE,"E826"),sQuery(id+"F4.wireOp",EDGE,"E827"),sQuery(id+"F4.wireOp",EDGE,"E828"),sQuery(id+"F4.wireOp",EDGE,"E829"),sQuery(id+"F4.wireOp",EDGE,"E830"),sQuery(id+"F4.wireOp",EDGE,"E831"),sQuery(id+"F4.wireOp",EDGE,"E832"),sQuery(id+"F4.wireOp",EDGE,"E833")])]});
            var Q7;
            Q7=makeQuery(id+"F5.opExtrude","SWEPT_BODY",BODY,{"disambiguationData":[OSD([sQuery(id+"F4.wireOp",EDGE,"E834"),sQuery(id+"F4.wireOp",EDGE,"E835"),sQuery(id+"F4.wireOp",EDGE,"E836"),sQuery(id+"F4.wireOp",EDGE,"E837"),sQuery(id+"F4.wireOp",EDGE,"E838"),sQuery(id+"F4.wireOp",EDGE,"E839"),sQuery(id+"F4.wireOp",EDGE,"E840"),sQuery(id+"F4.wireOp",EDGE,"E841"),sQuery(id+"F4.wireOp",EDGE,"E842"),sQuery(id+"F4.wireOp",EDGE,"E843"),sQuery(id+"F4.wireOp",EDGE,"E844"),sQuery(id+"F4.wireOp",EDGE,"E845"),sQuery(id+"F4.wireOp",EDGE,"E846"),sQuery(id+"F4.wireOp",EDGE,"E847"),sQuery(id+"F4.wireOp",EDGE,"E848"),sQuery(id+"F4.wireOp",EDGE,"E849"),sQuery(id+"F4.wireOp",EDGE,"E850"),sQuery(id+"F4.wireOp",EDGE,"E851"),sQuery(id+"F4.wireOp",EDGE,"E852"),sQuery(id+"F4.wireOp",EDGE,"E853"),sQuery(id+"F4.wireOp",EDGE,"E854"),sQuery(id+"F4.wireOp",EDGE,"E855"),sQuery(id+"F4.wireOp",EDGE,"E856"),sQuery(id+"F4.wireOp",EDGE,"E857"),sQuery(id+"F4.wireOp",EDGE,"E858"),sQuery(id+"F4.wireOp",EDGE,"E859"),sQuery(id+"F4.wireOp",EDGE,"E860"),sQuery(id+"F4.wireOp",EDGE,"E861"),sQuery(id+"F4.wireOp",EDGE,"E862"),sQuery(id+"F4.wireOp",EDGE,"E863"),sQuery(id+"F4.wireOp",EDGE,"E864"),sQuery(id+"F4.wireOp",EDGE,"E865"),sQuery(id+"F4.wireOp",EDGE,"E866"),sQuery(id+"F4.wireOp",EDGE,"E867"),sQuery(id+"F4.wireOp",EDGE,"E868"),sQuery(id+"F4.wireOp",EDGE,"E869"),sQuery(id+"F4.wireOp",EDGE,"E870"),sQuery(id+"F4.wireOp",EDGE,"E871"),sQuery(id+"F4.wireOp",EDGE,"E872"),sQuery(id+"F4.wireOp",EDGE,"E873"),sQuery(id+"F4.wireOp",EDGE,"E874"),sQuery(id+"F4.wireOp",EDGE,"E875"),sQuery(id+"F4.wireOp",EDGE,"E876"),sQuery(id+"F4.wireOp",EDGE,"E877"),sQuery(id+"F4.wireOp",EDGE,"E878"),sQuery(id+"F4.wireOp",EDGE,"E879"),sQuery(id+"F4.wireOp",EDGE,"E880"),sQuery(id+"F4.wireOp",EDGE,"E881"),sQuery(id+"F4.wireOp",EDGE,"E882"),sQuery(id+"F4.wireOp",EDGE,"E883"),sQuery(id+"F4.wireOp",EDGE,"E884"),sQuery(id+"F4.wireOp",EDGE,"E885"),sQuery(id+"F4.wireOp",EDGE,"E886"),sQuery(id+"F4.wireOp",EDGE,"E887"),sQuery(id+"F4.wireOp",EDGE,"E888"),sQuery(id+"F4.wireOp",EDGE,"E889"),sQuery(id+"F4.wireOp",EDGE,"E890"),sQuery(id+"F4.wireOp",EDGE,"E891"),sQuery(id+"F4.wireOp",EDGE,"E892"),sQuery(id+"F4.wireOp",EDGE,"E893"),sQuery(id+"F4.wireOp",EDGE,"E894"),sQuery(id+"F4.wireOp",EDGE,"E895"),sQuery(id+"F4.wireOp",EDGE,"E896"),sQuery(id+"F4.wireOp",EDGE,"E897"),sQuery(id+"F4.wireOp",EDGE,"E898"),sQuery(id+"F4.wireOp",EDGE,"E899"),sQuery(id+"F4.wireOp",EDGE,"E900"),sQuery(id+"F4.wireOp",EDGE,"E901"),sQuery(id+"F4.wireOp",EDGE,"E901"),sQuery(id+"F4.wireOp",EDGE,"E902"),sQuery(id+"F4.wireOp",EDGE,"E903"),sQuery(id+"F4.wireOp",EDGE,"E904"),sQuery(id+"F4.wireOp",EDGE,"E905"),sQuery(id+"F4.wireOp",EDGE,"E906"),sQuery(id+"F4.wireOp",EDGE,"E907"),sQuery(id+"F4.wireOp",EDGE,"E908"),sQuery(id+"F4.wireOp",EDGE,"E909"),sQuery(id+"F4.wireOp",EDGE,"E910"),sQuery(id+"F4.wireOp",EDGE,"E911"),sQuery(id+"F4.wireOp",EDGE,"E912")])]});
            var Q8;
            Q8=makeQuery(id+"F5.opExtrude","SWEPT_BODY",BODY,{"disambiguationData":[OSD([sQuery(id+"F4.wireOp",EDGE,"E913"),sQuery(id+"F4.wireOp",EDGE,"E914"),sQuery(id+"F4.wireOp",EDGE,"E915"),sQuery(id+"F4.wireOp",EDGE,"E916"),sQuery(id+"F4.wireOp",EDGE,"E917"),sQuery(id+"F4.wireOp",EDGE,"E918"),sQuery(id+"F4.wireOp",EDGE,"E919"),sQuery(id+"F4.wireOp",EDGE,"E920"),sQuery(id+"F4.wireOp",EDGE,"E921"),sQuery(id+"F4.wireOp",EDGE,"E922"),sQuery(id+"F4.wireOp",EDGE,"E923"),sQuery(id+"F4.wireOp",EDGE,"E924"),sQuery(id+"F4.wireOp",EDGE,"E925"),sQuery(id+"F4.wireOp",EDGE,"E926"),sQuery(id+"F4.wireOp",EDGE,"E927"),sQuery(id+"F4.wireOp",EDGE,"E928"),sQuery(id+"F4.wireOp",EDGE,"E929"),sQuery(id+"F4.wireOp",EDGE,"E930"),sQuery(id+"F4.wireOp",EDGE,"E931"),sQuery(id+"F4.wireOp",EDGE,"E932"),sQuery(id+"F4.wireOp",EDGE,"E933"),sQuery(id+"F4.wireOp",EDGE,"E934"),sQuery(id+"F4.wireOp",EDGE,"E935"),sQuery(id+"F4.wireOp",EDGE,"E936"),sQuery(id+"F4.wireOp",EDGE,"E937"),sQuery(id+"F4.wireOp",EDGE,"E938"),sQuery(id+"F4.wireOp",EDGE,"E939"),sQuery(id+"F4.wireOp",EDGE,"E940"),sQuery(id+"F4.wireOp",EDGE,"E941"),sQuery(id+"F4.wireOp",EDGE,"E942"),sQuery(id+"F4.wireOp",EDGE,"E943"),sQuery(id+"F4.wireOp",EDGE,"E944"),sQuery(id+"F4.wireOp",EDGE,"E945"),sQuery(id+"F4.wireOp",EDGE,"E946"),sQuery(id+"F4.wireOp",EDGE,"E947"),sQuery(id+"F4.wireOp",EDGE,"E947"),sQuery(id+"F4.wireOp",EDGE,"E948"),sQuery(id+"F4.wireOp",EDGE,"E949"),sQuery(id+"F4.wireOp",EDGE,"E950"),sQuery(id+"F4.wireOp",EDGE,"E951"),sQuery(id+"F4.wireOp",EDGE,"E952"),sQuery(id+"F4.wireOp",EDGE,"E953"),sQuery(id+"F4.wireOp",EDGE,"E954"),sQuery(id+"F4.wireOp",EDGE,"E955"),sQuery(id+"F4.wireOp",EDGE,"E956"),sQuery(id+"F4.wireOp",EDGE,"E957"),sQuery(id+"F4.wireOp",EDGE,"E958"),sQuery(id+"F4.wireOp",EDGE,"E959"),sQuery(id+"F4.wireOp",EDGE,"E959"),sQuery(id+"F4.wireOp",EDGE,"E960"),sQuery(id+"F4.wireOp",EDGE,"E961"),sQuery(id+"F4.wireOp",EDGE,"E962"),sQuery(id+"F4.wireOp",EDGE,"E963"),sQuery(id+"F4.wireOp",EDGE,"E964"),sQuery(id+"F4.wireOp",EDGE,"E965"),sQuery(id+"F4.wireOp",EDGE,"E966"),sQuery(id+"F4.wireOp",EDGE,"E967"),sQuery(id+"F4.wireOp",EDGE,"E968"),sQuery(id+"F4.wireOp",EDGE,"E969"),sQuery(id+"F4.wireOp",EDGE,"E970"),sQuery(id+"F4.wireOp",EDGE,"E971"),sQuery(id+"F4.wireOp",EDGE,"E972"),sQuery(id+"F4.wireOp",EDGE,"E973"),sQuery(id+"F4.wireOp",EDGE,"E974"),sQuery(id+"F4.wireOp",EDGE,"E975"),sQuery(id+"F4.wireOp",EDGE,"E976"),sQuery(id+"F4.wireOp",EDGE,"E977"),sQuery(id+"F4.wireOp",EDGE,"E978"),sQuery(id+"F4.wireOp",EDGE,"E979"),sQuery(id+"F4.wireOp",EDGE,"E980"),sQuery(id+"F4.wireOp",EDGE,"E981"),sQuery(id+"F4.wireOp",EDGE,"E982"),sQuery(id+"F4.wireOp",EDGE,"E983"),sQuery(id+"F4.wireOp",EDGE,"E984"),sQuery(id+"F4.wireOp",EDGE,"E985"),sQuery(id+"F4.wireOp",EDGE,"E986"),sQuery(id+"F4.wireOp",EDGE,"E987"),sQuery(id+"F4.wireOp",EDGE,"E988"),sQuery(id+"F4.wireOp",EDGE,"E989"),sQuery(id+"F4.wireOp",EDGE,"E990"),sQuery(id+"F4.wireOp",EDGE,"E991"),sQuery(id+"F4.wireOp",EDGE,"E992"),sQuery(id+"F4.wireOp",EDGE,"E992"),sQuery(id+"F4.wireOp",EDGE,"E993"),sQuery(id+"F4.wireOp",EDGE,"E994"),sQuery(id+"F4.wireOp",EDGE,"E995"),sQuery(id+"F4.wireOp",EDGE,"E996"),sQuery(id+"F4.wireOp",EDGE,"E997"),sQuery(id+"F4.wireOp",EDGE,"E998"),sQuery(id+"F4.wireOp",EDGE,"E999"),sQuery(id+"F4.wireOp",EDGE,"E1000"),sQuery(id+"F4.wireOp",EDGE,"E1001"),sQuery(id+"F4.wireOp",EDGE,"E1002"),sQuery(id+"F4.wireOp",EDGE,"E1003"),sQuery(id+"F4.wireOp",EDGE,"E1004"),sQuery(id+"F4.wireOp",EDGE,"E1005"),sQuery(id+"F4.wireOp",EDGE,"E1006"),sQuery(id+"F4.wireOp",EDGE,"E1007"),sQuery(id+"F4.wireOp",EDGE,"E1008"),sQuery(id+"F4.wireOp",EDGE,"E1009"),sQuery(id+"F4.wireOp",EDGE,"E1010"),sQuery(id+"F4.wireOp",EDGE,"E1011"),sQuery(id+"F4.wireOp",EDGE,"E1012"),sQuery(id+"F4.wireOp",EDGE,"E1013"),sQuery(id+"F4.wireOp",EDGE,"E1014"),sQuery(id+"F4.wireOp",EDGE,"E1015"),sQuery(id+"F4.wireOp",EDGE,"E1016"),sQuery(id+"F4.wireOp",EDGE,"E1017"),sQuery(id+"F4.wireOp",EDGE,"E1018"),sQuery(id+"F4.wireOp",EDGE,"E1019")])]});
            var Q9;
            Q9=makeQuery(id+"F5.opExtrude","SWEPT_BODY",BODY,{"disambiguationData":[OSD([sQuery(id+"F4.wireOp",EDGE,"E1020"),sQuery(id+"F4.wireOp",EDGE,"E1021"),sQuery(id+"F4.wireOp",EDGE,"E1022"),sQuery(id+"F4.wireOp",EDGE,"E1023"),sQuery(id+"F4.wireOp",EDGE,"E1024"),sQuery(id+"F4.wireOp",EDGE,"E1025"),sQuery(id+"F4.wireOp",EDGE,"E1026"),sQuery(id+"F4.wireOp",EDGE,"E1027"),sQuery(id+"F4.wireOp",EDGE,"E1028"),sQuery(id+"F4.wireOp",EDGE,"E1029"),sQuery(id+"F4.wireOp",EDGE,"E1030"),sQuery(id+"F4.wireOp",EDGE,"E1031"),sQuery(id+"F4.wireOp",EDGE,"E1031"),sQuery(id+"F4.wireOp",EDGE,"E1032"),sQuery(id+"F4.wireOp",EDGE,"E1033"),sQuery(id+"F4.wireOp",EDGE,"E1034"),sQuery(id+"F4.wireOp",EDGE,"E1035"),sQuery(id+"F4.wireOp",EDGE,"E1036"),sQuery(id+"F4.wireOp",EDGE,"E1037"),sQuery(id+"F4.wireOp",EDGE,"E1038"),sQuery(id+"F4.wireOp",EDGE,"E1039"),sQuery(id+"F4.wireOp",EDGE,"E1040"),sQuery(id+"F4.wireOp",EDGE,"E1041"),sQuery(id+"F4.wireOp",EDGE,"E1041"),sQuery(id+"F4.wireOp",EDGE,"E1042"),sQuery(id+"F4.wireOp",EDGE,"E1043"),sQuery(id+"F4.wireOp",EDGE,"E1044"),sQuery(id+"F4.wireOp",EDGE,"E1045"),sQuery(id+"F4.wireOp",EDGE,"E1046"),sQuery(id+"F4.wireOp",EDGE,"E1047"),sQuery(id+"F4.wireOp",EDGE,"E1048"),sQuery(id+"F4.wireOp",EDGE,"E1049"),sQuery(id+"F4.wireOp",EDGE,"E1049"),sQuery(id+"F4.wireOp",EDGE,"E1049"),sQuery(id+"F4.wireOp",EDGE,"E1049"),sQuery(id+"F4.wireOp",EDGE,"E1050"),sQuery(id+"F4.wireOp",EDGE,"E1051"),sQuery(id+"F4.wireOp",EDGE,"E1052"),sQuery(id+"F4.wireOp",EDGE,"E1053"),sQuery(id+"F4.wireOp",EDGE,"E1054"),sQuery(id+"F4.wireOp",EDGE,"E1055"),sQuery(id+"F4.wireOp",EDGE,"E1056"),sQuery(id+"F4.wireOp",EDGE,"E1057"),sQuery(id+"F4.wireOp",EDGE,"E1058"),sQuery(id+"F4.wireOp",EDGE,"E1059"),sQuery(id+"F4.wireOp",EDGE,"E1060"),sQuery(id+"F4.wireOp",EDGE,"E1061"),sQuery(id+"F4.wireOp",EDGE,"E1062"),sQuery(id+"F4.wireOp",EDGE,"E1063"),sQuery(id+"F4.wireOp",EDGE,"E1064"),sQuery(id+"F4.wireOp",EDGE,"E1065"),sQuery(id+"F4.wireOp",EDGE,"E1066"),sQuery(id+"F4.wireOp",EDGE,"E1067"),sQuery(id+"F4.wireOp",EDGE,"E1068"),sQuery(id+"F4.wireOp",EDGE,"E1069"),sQuery(id+"F4.wireOp",EDGE,"E1070"),sQuery(id+"F4.wireOp",EDGE,"E1071"),sQuery(id+"F4.wireOp",EDGE,"E1072"),sQuery(id+"F4.wireOp",EDGE,"E1073"),sQuery(id+"F4.wireOp",EDGE,"E1074"),sQuery(id+"F4.wireOp",EDGE,"E1075"),sQuery(id+"F4.wireOp",EDGE,"E1076"),sQuery(id+"F4.wireOp",EDGE,"E1077"),sQuery(id+"F4.wireOp",EDGE,"E1078"),sQuery(id+"F4.wireOp",EDGE,"E1079"),sQuery(id+"F4.wireOp",EDGE,"E1080"),sQuery(id+"F4.wireOp",EDGE,"E1081"),sQuery(id+"F4.wireOp",EDGE,"E1082"),sQuery(id+"F4.wireOp",EDGE,"E1083"),sQuery(id+"F4.wireOp",EDGE,"E1083"),sQuery(id+"F4.wireOp",EDGE,"E1084"),sQuery(id+"F4.wireOp",EDGE,"E1085"),sQuery(id+"F4.wireOp",EDGE,"E1086"),sQuery(id+"F4.wireOp",EDGE,"E1087"),sQuery(id+"F4.wireOp",EDGE,"E1088"),sQuery(id+"F4.wireOp",EDGE,"E1089"),sQuery(id+"F4.wireOp",EDGE,"E1090"),sQuery(id+"F4.wireOp",EDGE,"E1090"),sQuery(id+"F4.wireOp",EDGE,"E1091"),sQuery(id+"F4.wireOp",EDGE,"E1092"),sQuery(id+"F4.wireOp",EDGE,"E1093"),sQuery(id+"F4.wireOp",EDGE,"E1094"),sQuery(id+"F4.wireOp",EDGE,"E1095"),sQuery(id+"F4.wireOp",EDGE,"E1096"),sQuery(id+"F4.wireOp",EDGE,"E1097"),sQuery(id+"F4.wireOp",EDGE,"E1098"),sQuery(id+"F4.wireOp",EDGE,"E1099"),sQuery(id+"F4.wireOp",EDGE,"E1100"),sQuery(id+"F4.wireOp",EDGE,"E1101"),sQuery(id+"F4.wireOp",EDGE,"E1102"),sQuery(id+"F4.wireOp",EDGE,"E1103"),sQuery(id+"F4.wireOp",EDGE,"E1104"),sQuery(id+"F4.wireOp",EDGE,"E1105"),sQuery(id+"F4.wireOp",EDGE,"E1106"),sQuery(id+"F4.wireOp",EDGE,"E1107"),sQuery(id+"F4.wireOp",EDGE,"E1108"),sQuery(id+"F4.wireOp",EDGE,"E1109"),sQuery(id+"F4.wireOp",EDGE,"E1110"),sQuery(id+"F4.wireOp",EDGE,"E1110"),sQuery(id+"F4.wireOp",EDGE,"E1110"),sQuery(id+"F4.wireOp",EDGE,"E1111"),sQuery(id+"F4.wireOp",EDGE,"E1112"),sQuery(id+"F4.wireOp",EDGE,"E1113"),sQuery(id+"F4.wireOp",EDGE,"E1114"),sQuery(id+"F4.wireOp",EDGE,"E1115"),sQuery(id+"F4.wireOp",EDGE,"E1116"),sQuery(id+"F4.wireOp",EDGE,"E1117"),sQuery(id+"F4.wireOp",EDGE,"E1118"),sQuery(id+"F4.wireOp",EDGE,"E1119"),sQuery(id+"F4.wireOp",EDGE,"E1120")])]});
            var Q10;
            Q10=makeQuery(id+"F5.opExtrude","SWEPT_BODY",BODY,{"disambiguationData":[OSD([sQuery(id+"F4.wireOp",EDGE,"E1121"),sQuery(id+"F4.wireOp",EDGE,"E1122"),sQuery(id+"F4.wireOp",EDGE,"E1123"),sQuery(id+"F4.wireOp",EDGE,"E1124"),sQuery(id+"F4.wireOp",EDGE,"E1125"),sQuery(id+"F4.wireOp",EDGE,"E1126"),sQuery(id+"F4.wireOp",EDGE,"E1127"),sQuery(id+"F4.wireOp",EDGE,"E1128"),sQuery(id+"F4.wireOp",EDGE,"E1129"),sQuery(id+"F4.wireOp",EDGE,"E1130"),sQuery(id+"F4.wireOp",EDGE,"E1131"),sQuery(id+"F4.wireOp",EDGE,"E1132"),sQuery(id+"F4.wireOp",EDGE,"E1133"),sQuery(id+"F4.wireOp",EDGE,"E1134"),sQuery(id+"F4.wireOp",EDGE,"E1135"),sQuery(id+"F4.wireOp",EDGE,"E1136")])]});
            transform(context, id + "F9", {"entities" : qUnion([Q0, Q1, Q2, Q3, Q4, Q5, Q6, Q7, Q8, Q9, Q10]), "transformType" : TransformType.TRANSLATION_3D, "dx" : 0.7 * mm, "dy" : 0 * mm, "dz" : 0 * mm, "makeCopy" : false});
        }
        {
            var Q0;
            {var subQ0=sQuery(id+"F0.wireOp",EDGE,"E2");Q0=makeQuery(id+"F2.boolean.opBoolean","SPLIT",FACE,{"disambiguationData":[TD([makeQuery(id+"F1.opExtrude","SWEPT_FACE",FACE,{"disambiguationData":[OSD([subQ0])]})])],"derivedFrom":makeQuery(id+"F1.opExtrude","CAP_FACE",FACE,{"disambiguationData":[OSD([subQ0])],"isStart":false})});}
            extrude(context, id + "F10", {"entities" : qUnion([Q0]), "operationType" : NewBodyOperationType.REMOVE, "endBound" : BoundingType.THROUGH_ALL, "depth" : 25 * mm, "offsetDistance" : 25 * mm, "hasSecondDirection" : true, "secondDirectionOppositeDirection" : true, "secondDirectionDepth" : 1 * mm});
        }
        {
            var Q0;
            Q0=makeQuery(id+"F5.opExtrude","SWEPT_BODY",BODY,{"disambiguationData":[OSD([sQuery(id+"F4.wireOp",EDGE,"E4"),sQuery(id+"F4.wireOp",EDGE,"E5"),sQuery(id+"F4.wireOp",EDGE,"E6"),sQuery(id+"F4.wireOp",EDGE,"E7"),sQuery(id+"F4.wireOp",EDGE,"E8"),sQuery(id+"F4.wireOp",EDGE,"E9"),sQuery(id+"F4.wireOp",EDGE,"E10"),sQuery(id+"F4.wireOp",EDGE,"E11"),sQuery(id+"F4.wireOp",EDGE,"E12"),sQuery(id+"F4.wireOp",EDGE,"E13"),sQuery(id+"F4.wireOp",EDGE,"E14"),sQuery(id+"F4.wireOp",EDGE,"E15"),sQuery(id+"F4.wireOp",EDGE,"E16"),sQuery(id+"F4.wireOp",EDGE,"E17"),sQuery(id+"F4.wireOp",EDGE,"E18"),sQuery(id+"F4.wireOp",EDGE,"E19"),sQuery(id+"F4.wireOp",EDGE,"E20"),sQuery(id+"F4.wireOp",EDGE,"E21"),sQuery(id+"F4.wireOp",EDGE,"E22"),sQuery(id+"F4.wireOp",EDGE,"E23"),sQuery(id+"F4.wireOp",EDGE,"E24"),sQuery(id+"F4.wireOp",EDGE,"E25"),sQuery(id+"F4.wireOp",EDGE,"E26"),sQuery(id+"F4.wireOp",EDGE,"E26"),sQuery(id+"F4.wireOp",EDGE,"E27"),sQuery(id+"F4.wireOp",EDGE,"E28"),sQuery(id+"F4.wireOp",EDGE,"E29"),sQuery(id+"F4.wireOp",EDGE,"E30"),sQuery(id+"F4.wireOp",EDGE,"E31"),sQuery(id+"F4.wireOp",EDGE,"E32"),sQuery(id+"F4.wireOp",EDGE,"E33"),sQuery(id+"F4.wireOp",EDGE,"E34"),sQuery(id+"F4.wireOp",EDGE,"E35"),sQuery(id+"F4.wireOp",EDGE,"E36"),sQuery(id+"F4.wireOp",EDGE,"E37"),sQuery(id+"F4.wireOp",EDGE,"E38"),sQuery(id+"F4.wireOp",EDGE,"E39"),sQuery(id+"F4.wireOp",EDGE,"E40"),sQuery(id+"F4.wireOp",EDGE,"E41"),sQuery(id+"F4.wireOp",EDGE,"E42"),sQuery(id+"F4.wireOp",EDGE,"E43"),sQuery(id+"F4.wireOp",EDGE,"E44"),sQuery(id+"F4.wireOp",EDGE,"E45"),sQuery(id+"F4.wireOp",EDGE,"E46"),sQuery(id+"F4.wireOp",EDGE,"E47"),sQuery(id+"F4.wireOp",EDGE,"E48"),sQuery(id+"F4.wireOp",EDGE,"E49"),sQuery(id+"F4.wireOp",EDGE,"E50"),sQuery(id+"F4.wireOp",EDGE,"E51"),sQuery(id+"F4.wireOp",EDGE,"E52"),sQuery(id+"F4.wireOp",EDGE,"E53"),sQuery(id+"F4.wireOp",EDGE,"E54"),sQuery(id+"F4.wireOp",EDGE,"E55"),sQuery(id+"F4.wireOp",EDGE,"E56"),sQuery(id+"F4.wireOp",EDGE,"E57"),sQuery(id+"F4.wireOp",EDGE,"E58"),sQuery(id+"F4.wireOp",EDGE,"E59"),sQuery(id+"F4.wireOp",EDGE,"E60"),sQuery(id+"F4.wireOp",EDGE,"E61"),sQuery(id+"F4.wireOp",EDGE,"E62"),sQuery(id+"F4.wireOp",EDGE,"E63"),sQuery(id+"F4.wireOp",EDGE,"E64"),sQuery(id+"F4.wireOp",EDGE,"E65"),sQuery(id+"F4.wireOp",EDGE,"E65"),sQuery(id+"F4.wireOp",EDGE,"E66"),sQuery(id+"F4.wireOp",EDGE,"E67"),sQuery(id+"F4.wireOp",EDGE,"E68"),sQuery(id+"F4.wireOp",EDGE,"E69"),sQuery(id+"F4.wireOp",EDGE,"E70"),sQuery(id+"F4.wireOp",EDGE,"E71"),sQuery(id+"F4.wireOp",EDGE,"E72"),sQuery(id+"F4.wireOp",EDGE,"E73"),sQuery(id+"F4.wireOp",EDGE,"E74"),sQuery(id+"F4.wireOp",EDGE,"E75"),sQuery(id+"F4.wireOp",EDGE,"E76"),sQuery(id+"F4.wireOp",EDGE,"E77"),sQuery(id+"F4.wireOp",EDGE,"E78"),sQuery(id+"F4.wireOp",EDGE,"E79"),sQuery(id+"F4.wireOp",EDGE,"E80"),sQuery(id+"F4.wireOp",EDGE,"E81"),sQuery(id+"F4.wireOp",EDGE,"E82"),sQuery(id+"F4.wireOp",EDGE,"E83"),sQuery(id+"F4.wireOp",EDGE,"E84"),sQuery(id+"F4.wireOp",EDGE,"E85"),sQuery(id+"F4.wireOp",EDGE,"E86"),sQuery(id+"F4.wireOp",EDGE,"E87"),sQuery(id+"F4.wireOp",EDGE,"E88"),sQuery(id+"F4.wireOp",EDGE,"E89"),sQuery(id+"F4.wireOp",EDGE,"E90"),sQuery(id+"F4.wireOp",EDGE,"E91"),sQuery(id+"F4.wireOp",EDGE,"E92"),sQuery(id+"F4.wireOp",EDGE,"E93"),sQuery(id+"F4.wireOp",EDGE,"E94"),sQuery(id+"F4.wireOp",EDGE,"E95"),sQuery(id+"F4.wireOp",EDGE,"E96"),sQuery(id+"F4.wireOp",EDGE,"E97"),sQuery(id+"F4.wireOp",EDGE,"E98"),sQuery(id+"F4.wireOp",EDGE,"E99"),sQuery(id+"F4.wireOp",EDGE,"E100"),sQuery(id+"F4.wireOp",EDGE,"E101"),sQuery(id+"F4.wireOp",EDGE,"E102"),sQuery(id+"F4.wireOp",EDGE,"E103"),sQuery(id+"F4.wireOp",EDGE,"E104"),sQuery(id+"F4.wireOp",EDGE,"E105"),sQuery(id+"F4.wireOp",EDGE,"E106"),sQuery(id+"F4.wireOp",EDGE,"E107"),sQuery(id+"F4.wireOp",EDGE,"E108"),sQuery(id+"F4.wireOp",EDGE,"E109"),sQuery(id+"F4.wireOp",EDGE,"E110"),sQuery(id+"F4.wireOp",EDGE,"E111"),sQuery(id+"F4.wireOp",EDGE,"E112"),sQuery(id+"F4.wireOp",EDGE,"E113"),sQuery(id+"F4.wireOp",EDGE,"E114"),sQuery(id+"F4.wireOp",EDGE,"E114"),sQuery(id+"F4.wireOp",EDGE,"E115"),sQuery(id+"F4.wireOp",EDGE,"E116")])]});
            var Q1;
            Q1=makeQuery(id+"F5.opExtrude","SWEPT_BODY",BODY,{"disambiguationData":[OSD([sQuery(id+"F4.wireOp",EDGE,"E117"),sQuery(id+"F4.wireOp",EDGE,"E118"),sQuery(id+"F4.wireOp",EDGE,"E119"),sQuery(id+"F4.wireOp",EDGE,"E120"),sQuery(id+"F4.wireOp",EDGE,"E121"),sQuery(id+"F4.wireOp",EDGE,"E122"),sQuery(id+"F4.wireOp",EDGE,"E123"),sQuery(id+"F4.wireOp",EDGE,"E124"),sQuery(id+"F4.wireOp",EDGE,"E125"),sQuery(id+"F4.wireOp",EDGE,"E126"),sQuery(id+"F4.wireOp",EDGE,"E127"),sQuery(id+"F4.wireOp",EDGE,"E128"),sQuery(id+"F4.wireOp",EDGE,"E129"),sQuery(id+"F4.wireOp",EDGE,"E130"),sQuery(id+"F4.wireOp",EDGE,"E131"),sQuery(id+"F4.wireOp",EDGE,"E132"),sQuery(id+"F4.wireOp",EDGE,"E133"),sQuery(id+"F4.wireOp",EDGE,"E133"),sQuery(id+"F4.wireOp",EDGE,"E134"),sQuery(id+"F4.wireOp",EDGE,"E135"),sQuery(id+"F4.wireOp",EDGE,"E136"),sQuery(id+"F4.wireOp",EDGE,"E137"),sQuery(id+"F4.wireOp",EDGE,"E138"),sQuery(id+"F4.wireOp",EDGE,"E139"),sQuery(id+"F4.wireOp",EDGE,"E140"),sQuery(id+"F4.wireOp",EDGE,"E141"),sQuery(id+"F4.wireOp",EDGE,"E142"),sQuery(id+"F4.wireOp",EDGE,"E143"),sQuery(id+"F4.wireOp",EDGE,"E144"),sQuery(id+"F4.wireOp",EDGE,"E145"),sQuery(id+"F4.wireOp",EDGE,"E146"),sQuery(id+"F4.wireOp",EDGE,"E147"),sQuery(id+"F4.wireOp",EDGE,"E148"),sQuery(id+"F4.wireOp",EDGE,"E149"),sQuery(id+"F4.wireOp",EDGE,"E150"),sQuery(id+"F4.wireOp",EDGE,"E151"),sQuery(id+"F4.wireOp",EDGE,"E152"),sQuery(id+"F4.wireOp",EDGE,"E153"),sQuery(id+"F4.wireOp",EDGE,"E154"),sQuery(id+"F4.wireOp",EDGE,"E155"),sQuery(id+"F4.wireOp",EDGE,"E156"),sQuery(id+"F4.wireOp",EDGE,"E157"),sQuery(id+"F4.wireOp",EDGE,"E158"),sQuery(id+"F4.wireOp",EDGE,"E159"),sQuery(id+"F4.wireOp",EDGE,"E160"),sQuery(id+"F4.wireOp",EDGE,"E161"),sQuery(id+"F4.wireOp",EDGE,"E162"),sQuery(id+"F4.wireOp",EDGE,"E162"),sQuery(id+"F4.wireOp",EDGE,"E162"),sQuery(id+"F4.wireOp",EDGE,"E163"),sQuery(id+"F4.wireOp",EDGE,"E164"),sQuery(id+"F4.wireOp",EDGE,"E165"),sQuery(id+"F4.wireOp",EDGE,"E166"),sQuery(id+"F4.wireOp",EDGE,"E167"),sQuery(id+"F4.wireOp",EDGE,"E168"),sQuery(id+"F4.wireOp",EDGE,"E169"),sQuery(id+"F4.wireOp",EDGE,"E170"),sQuery(id+"F4.wireOp",EDGE,"E171"),sQuery(id+"F4.wireOp",EDGE,"E171"),sQuery(id+"F4.wireOp",EDGE,"E172"),sQuery(id+"F4.wireOp",EDGE,"E173"),sQuery(id+"F4.wireOp",EDGE,"E174"),sQuery(id+"F4.wireOp",EDGE,"E175"),sQuery(id+"F4.wireOp",EDGE,"E176"),sQuery(id+"F4.wireOp",EDGE,"E177"),sQuery(id+"F4.wireOp",EDGE,"E178"),sQuery(id+"F4.wireOp",EDGE,"E179"),sQuery(id+"F4.wireOp",EDGE,"E180"),sQuery(id+"F4.wireOp",EDGE,"E181"),sQuery(id+"F4.wireOp",EDGE,"E182"),sQuery(id+"F4.wireOp",EDGE,"E183"),sQuery(id+"F4.wireOp",EDGE,"E184"),sQuery(id+"F4.wireOp",EDGE,"E185"),sQuery(id+"F4.wireOp",EDGE,"E186"),sQuery(id+"F4.wireOp",EDGE,"E187"),sQuery(id+"F4.wireOp",EDGE,"E188"),sQuery(id+"F4.wireOp",EDGE,"E189"),sQuery(id+"F4.wireOp",EDGE,"E190"),sQuery(id+"F4.wireOp",EDGE,"E191"),sQuery(id+"F4.wireOp",EDGE,"E192"),sQuery(id+"F4.wireOp",EDGE,"E193"),sQuery(id+"F4.wireOp",EDGE,"E194"),sQuery(id+"F4.wireOp",EDGE,"E195"),sQuery(id+"F4.wireOp",EDGE,"E196"),sQuery(id+"F4.wireOp",EDGE,"E197"),sQuery(id+"F4.wireOp",EDGE,"E198"),sQuery(id+"F4.wireOp",EDGE,"E199"),sQuery(id+"F4.wireOp",EDGE,"E200"),sQuery(id+"F4.wireOp",EDGE,"E201"),sQuery(id+"F4.wireOp",EDGE,"E202"),sQuery(id+"F4.wireOp",EDGE,"E203"),sQuery(id+"F4.wireOp",EDGE,"E204"),sQuery(id+"F4.wireOp",EDGE,"E205"),sQuery(id+"F4.wireOp",EDGE,"E206"),sQuery(id+"F4.wireOp",EDGE,"E207"),sQuery(id+"F4.wireOp",EDGE,"E208"),sQuery(id+"F4.wireOp",EDGE,"E209"),sQuery(id+"F4.wireOp",EDGE,"E210"),sQuery(id+"F4.wireOp",EDGE,"E211"),sQuery(id+"F4.wireOp",EDGE,"E212"),sQuery(id+"F4.wireOp",EDGE,"E213"),sQuery(id+"F4.wireOp",EDGE,"E214"),sQuery(id+"F4.wireOp",EDGE,"E215"),sQuery(id+"F4.wireOp",EDGE,"E216"),sQuery(id+"F4.wireOp",EDGE,"E217"),sQuery(id+"F4.wireOp",EDGE,"E218"),sQuery(id+"F4.wireOp",EDGE,"E219"),sQuery(id+"F4.wireOp",EDGE,"E220"),sQuery(id+"F4.wireOp",EDGE,"E221"),sQuery(id+"F4.wireOp",EDGE,"E222"),sQuery(id+"F4.wireOp",EDGE,"E223"),sQuery(id+"F4.wireOp",EDGE,"E224"),sQuery(id+"F4.wireOp",EDGE,"E225"),sQuery(id+"F4.wireOp",EDGE,"E226"),sQuery(id+"F4.wireOp",EDGE,"E227"),sQuery(id+"F4.wireOp",EDGE,"E228"),sQuery(id+"F4.wireOp",EDGE,"E229"),sQuery(id+"F4.wireOp",EDGE,"E230"),sQuery(id+"F4.wireOp",EDGE,"E231"),sQuery(id+"F4.wireOp",EDGE,"E232"),sQuery(id+"F4.wireOp",EDGE,"E233"),sQuery(id+"F4.wireOp",EDGE,"E234"),sQuery(id+"F4.wireOp",EDGE,"E235"),sQuery(id+"F4.wireOp",EDGE,"E236"),sQuery(id+"F4.wireOp",EDGE,"E237"),sQuery(id+"F4.wireOp",EDGE,"E238"),sQuery(id+"F4.wireOp",EDGE,"E239"),sQuery(id+"F4.wireOp",EDGE,"E240"),sQuery(id+"F4.wireOp",EDGE,"E241"),sQuery(id+"F4.wireOp",EDGE,"E242"),sQuery(id+"F4.wireOp",EDGE,"E243"),sQuery(id+"F4.wireOp",EDGE,"E244"),sQuery(id+"F4.wireOp",EDGE,"E245"),sQuery(id+"F4.wireOp",EDGE,"E246"),sQuery(id+"F4.wireOp",EDGE,"E247"),sQuery(id+"F4.wireOp",EDGE,"E248"),sQuery(id+"F4.wireOp",EDGE,"E249"),sQuery(id+"F4.wireOp",EDGE,"E250"),sQuery(id+"F4.wireOp",EDGE,"E250"),sQuery(id+"F4.wireOp",EDGE,"E251"),sQuery(id+"F4.wireOp",EDGE,"E252"),sQuery(id+"F4.wireOp",EDGE,"E253"),sQuery(id+"F4.wireOp",EDGE,"E254"),sQuery(id+"F4.wireOp",EDGE,"E255"),sQuery(id+"F4.wireOp",EDGE,"E256"),sQuery(id+"F4.wireOp",EDGE,"E257"),sQuery(id+"F4.wireOp",EDGE,"E258"),sQuery(id+"F4.wireOp",EDGE,"E259"),sQuery(id+"F4.wireOp",EDGE,"E260"),sQuery(id+"F4.wireOp",EDGE,"E261"),sQuery(id+"F4.wireOp",EDGE,"E262"),sQuery(id+"F4.wireOp",EDGE,"E262"),sQuery(id+"F4.wireOp",EDGE,"E262"),sQuery(id+"F4.wireOp",EDGE,"E263"),sQuery(id+"F4.wireOp",EDGE,"E264"),sQuery(id+"F4.wireOp",EDGE,"E265"),sQuery(id+"F4.wireOp",EDGE,"E266"),sQuery(id+"F4.wireOp",EDGE,"E267"),sQuery(id+"F4.wireOp",EDGE,"E268"),sQuery(id+"F4.wireOp",EDGE,"E269"),sQuery(id+"F4.wireOp",EDGE,"E270"),sQuery(id+"F4.wireOp",EDGE,"E271"),sQuery(id+"F4.wireOp",EDGE,"E272"),sQuery(id+"F4.wireOp",EDGE,"E273"),sQuery(id+"F4.wireOp",EDGE,"E274"),sQuery(id+"F4.wireOp",EDGE,"E275"),sQuery(id+"F4.wireOp",EDGE,"E276"),sQuery(id+"F4.wireOp",EDGE,"E277"),sQuery(id+"F4.wireOp",EDGE,"E278"),sQuery(id+"F4.wireOp",EDGE,"E279"),sQuery(id+"F4.wireOp",EDGE,"E280"),sQuery(id+"F4.wireOp",EDGE,"E281"),sQuery(id+"F4.wireOp",EDGE,"E282"),sQuery(id+"F4.wireOp",EDGE,"E283"),sQuery(id+"F4.wireOp",EDGE,"E284"),sQuery(id+"F4.wireOp",EDGE,"E285"),sQuery(id+"F4.wireOp",EDGE,"E286"),sQuery(id+"F4.wireOp",EDGE,"E287"),sQuery(id+"F4.wireOp",EDGE,"E288")])]});
            var Q2;
            Q2=makeQuery(id+"F5.opExtrude","SWEPT_BODY",BODY,{"disambiguationData":[OSD([sQuery(id+"F4.wireOp",EDGE,"E289"),sQuery(id+"F4.wireOp",EDGE,"E290"),sQuery(id+"F4.wireOp",EDGE,"E291"),sQuery(id+"F4.wireOp",EDGE,"E292"),sQuery(id+"F4.wireOp",EDGE,"E293"),sQuery(id+"F4.wireOp",EDGE,"E294"),sQuery(id+"F4.wireOp",EDGE,"E295"),sQuery(id+"F4.wireOp",EDGE,"E296"),sQuery(id+"F4.wireOp",EDGE,"E297"),sQuery(id+"F4.wireOp",EDGE,"E298"),sQuery(id+"F4.wireOp",EDGE,"E299"),sQuery(id+"F4.wireOp",EDGE,"E300"),sQuery(id+"F4.wireOp",EDGE,"E301"),sQuery(id+"F4.wireOp",EDGE,"E302"),sQuery(id+"F4.wireOp",EDGE,"E303"),sQuery(id+"F4.wireOp",EDGE,"E304"),sQuery(id+"F4.wireOp",EDGE,"E305"),sQuery(id+"F4.wireOp",EDGE,"E306"),sQuery(id+"F4.wireOp",EDGE,"E307"),sQuery(id+"F4.wireOp",EDGE,"E308"),sQuery(id+"F4.wireOp",EDGE,"E309"),sQuery(id+"F4.wireOp",EDGE,"E310"),sQuery(id+"F4.wireOp",EDGE,"E311"),sQuery(id+"F4.wireOp",EDGE,"E312"),sQuery(id+"F4.wireOp",EDGE,"E313"),sQuery(id+"F4.wireOp",EDGE,"E314"),sQuery(id+"F4.wireOp",EDGE,"E315"),sQuery(id+"F4.wireOp",EDGE,"E316"),sQuery(id+"F4.wireOp",EDGE,"E317"),sQuery(id+"F4.wireOp",EDGE,"E318"),sQuery(id+"F4.wireOp",EDGE,"E319"),sQuery(id+"F4.wireOp",EDGE,"E320"),sQuery(id+"F4.wireOp",EDGE,"E321"),sQuery(id+"F4.wireOp",EDGE,"E322"),sQuery(id+"F4.wireOp",EDGE,"E323"),sQuery(id+"F4.wireOp",EDGE,"E324"),sQuery(id+"F4.wireOp",EDGE,"E325"),sQuery(id+"F4.wireOp",EDGE,"E326"),sQuery(id+"F4.wireOp",EDGE,"E327"),sQuery(id+"F4.wireOp",EDGE,"E328"),sQuery(id+"F4.wireOp",EDGE,"E329"),sQuery(id+"F4.wireOp",EDGE,"E330"),sQuery(id+"F4.wireOp",EDGE,"E331"),sQuery(id+"F4.wireOp",EDGE,"E332"),sQuery(id+"F4.wireOp",EDGE,"E333"),sQuery(id+"F4.wireOp",EDGE,"E334"),sQuery(id+"F4.wireOp",EDGE,"E335"),sQuery(id+"F4.wireOp",EDGE,"E336"),sQuery(id+"F4.wireOp",EDGE,"E337"),sQuery(id+"F4.wireOp",EDGE,"E338"),sQuery(id+"F4.wireOp",EDGE,"E339"),sQuery(id+"F4.wireOp",EDGE,"E340"),sQuery(id+"F4.wireOp",EDGE,"E341"),sQuery(id+"F4.wireOp",EDGE,"E342"),sQuery(id+"F4.wireOp",EDGE,"E343"),sQuery(id+"F4.wireOp",EDGE,"E344"),sQuery(id+"F4.wireOp",EDGE,"E345"),sQuery(id+"F4.wireOp",EDGE,"E346"),sQuery(id+"F4.wireOp",EDGE,"E346"),sQuery(id+"F4.wireOp",EDGE,"E347"),sQuery(id+"F4.wireOp",EDGE,"E348"),sQuery(id+"F4.wireOp",EDGE,"E349"),sQuery(id+"F4.wireOp",EDGE,"E350"),sQuery(id+"F4.wireOp",EDGE,"E351"),sQuery(id+"F4.wireOp",EDGE,"E352"),sQuery(id+"F4.wireOp",EDGE,"E353"),sQuery(id+"F4.wireOp",EDGE,"E354"),sQuery(id+"F4.wireOp",EDGE,"E355"),sQuery(id+"F4.wireOp",EDGE,"E356"),sQuery(id+"F4.wireOp",EDGE,"E357"),sQuery(id+"F4.wireOp",EDGE,"E358"),sQuery(id+"F4.wireOp",EDGE,"E359"),sQuery(id+"F4.wireOp",EDGE,"E360"),sQuery(id+"F4.wireOp",EDGE,"E361"),sQuery(id+"F4.wireOp",EDGE,"E362"),sQuery(id+"F4.wireOp",EDGE,"E363"),sQuery(id+"F4.wireOp",EDGE,"E364"),sQuery(id+"F4.wireOp",EDGE,"E365"),sQuery(id+"F4.wireOp",EDGE,"E366"),sQuery(id+"F4.wireOp",EDGE,"E367"),sQuery(id+"F4.wireOp",EDGE,"E368"),sQuery(id+"F4.wireOp",EDGE,"E369"),sQuery(id+"F4.wireOp",EDGE,"E370"),sQuery(id+"F4.wireOp",EDGE,"E371"),sQuery(id+"F4.wireOp",EDGE,"E371"),sQuery(id+"F4.wireOp",EDGE,"E372"),sQuery(id+"F4.wireOp",EDGE,"E373"),sQuery(id+"F4.wireOp",EDGE,"E374"),sQuery(id+"F4.wireOp",EDGE,"E375"),sQuery(id+"F4.wireOp",EDGE,"E376"),sQuery(id+"F4.wireOp",EDGE,"E377"),sQuery(id+"F4.wireOp",EDGE,"E378"),sQuery(id+"F4.wireOp",EDGE,"E379"),sQuery(id+"F4.wireOp",EDGE,"E380"),sQuery(id+"F4.wireOp",EDGE,"E381"),sQuery(id+"F4.wireOp",EDGE,"E382"),sQuery(id+"F4.wireOp",EDGE,"E383"),sQuery(id+"F4.wireOp",EDGE,"E384"),sQuery(id+"F4.wireOp",EDGE,"E385"),sQuery(id+"F4.wireOp",EDGE,"E386"),sQuery(id+"F4.wireOp",EDGE,"E387"),sQuery(id+"F4.wireOp",EDGE,"E388"),sQuery(id+"F4.wireOp",EDGE,"E389"),sQuery(id+"F4.wireOp",EDGE,"E390"),sQuery(id+"F4.wireOp",EDGE,"E391"),sQuery(id+"F4.wireOp",EDGE,"E392"),sQuery(id+"F4.wireOp",EDGE,"E392"),sQuery(id+"F4.wireOp",EDGE,"E393"),sQuery(id+"F4.wireOp",EDGE,"E394"),sQuery(id+"F4.wireOp",EDGE,"E395"),sQuery(id+"F4.wireOp",EDGE,"E396"),sQuery(id+"F4.wireOp",EDGE,"E397"),sQuery(id+"F4.wireOp",EDGE,"E398"),sQuery(id+"F4.wireOp",EDGE,"E399"),sQuery(id+"F4.wireOp",EDGE,"E400"),sQuery(id+"F4.wireOp",EDGE,"E401"),sQuery(id+"F4.wireOp",EDGE,"E402"),sQuery(id+"F4.wireOp",EDGE,"E403"),sQuery(id+"F4.wireOp",EDGE,"E404"),sQuery(id+"F4.wireOp",EDGE,"E405"),sQuery(id+"F4.wireOp",EDGE,"E406"),sQuery(id+"F4.wireOp",EDGE,"E407"),sQuery(id+"F4.wireOp",EDGE,"E408"),sQuery(id+"F4.wireOp",EDGE,"E409"),sQuery(id+"F4.wireOp",EDGE,"E410"),sQuery(id+"F4.wireOp",EDGE,"E411"),sQuery(id+"F4.wireOp",EDGE,"E412"),sQuery(id+"F4.wireOp",EDGE,"E413"),sQuery(id+"F4.wireOp",EDGE,"E414"),sQuery(id+"F4.wireOp",EDGE,"E415"),sQuery(id+"F4.wireOp",EDGE,"E416"),sQuery(id+"F4.wireOp",EDGE,"E417"),sQuery(id+"F4.wireOp",EDGE,"E418"),sQuery(id+"F4.wireOp",EDGE,"E419"),sQuery(id+"F4.wireOp",EDGE,"E420"),sQuery(id+"F4.wireOp",EDGE,"E421"),sQuery(id+"F4.wireOp",EDGE,"E422"),sQuery(id+"F4.wireOp",EDGE,"E423"),sQuery(id+"F4.wireOp",EDGE,"E424"),sQuery(id+"F4.wireOp",EDGE,"E425"),sQuery(id+"F4.wireOp",EDGE,"E426"),sQuery(id+"F4.wireOp",EDGE,"E427"),sQuery(id+"F4.wireOp",EDGE,"E428"),sQuery(id+"F4.wireOp",EDGE,"E429"),sQuery(id+"F4.wireOp",EDGE,"E430"),sQuery(id+"F4.wireOp",EDGE,"E431"),sQuery(id+"F4.wireOp",EDGE,"E431"),sQuery(id+"F4.wireOp",EDGE,"E432"),sQuery(id+"F4.wireOp",EDGE,"E433"),sQuery(id+"F4.wireOp",EDGE,"E434"),sQuery(id+"F4.wireOp",EDGE,"E435"),sQuery(id+"F4.wireOp",EDGE,"E436"),sQuery(id+"F4.wireOp",EDGE,"E436"),sQuery(id+"F4.wireOp",EDGE,"E437"),sQuery(id+"F4.wireOp",EDGE,"E438"),sQuery(id+"F4.wireOp",EDGE,"E439"),sQuery(id+"F4.wireOp",EDGE,"E440"),sQuery(id+"F4.wireOp",EDGE,"E441"),sQuery(id+"F4.wireOp",EDGE,"E442"),sQuery(id+"F4.wireOp",EDGE,"E443"),sQuery(id+"F4.wireOp",EDGE,"E444"),sQuery(id+"F4.wireOp",EDGE,"E445"),sQuery(id+"F4.wireOp",EDGE,"E446"),sQuery(id+"F4.wireOp",EDGE,"E447"),sQuery(id+"F4.wireOp",EDGE,"E448"),sQuery(id+"F4.wireOp",EDGE,"E448"),sQuery(id+"F4.wireOp",EDGE,"E449"),sQuery(id+"F4.wireOp",EDGE,"E450"),sQuery(id+"F4.wireOp",EDGE,"E451"),sQuery(id+"F4.wireOp",EDGE,"E452"),sQuery(id+"F4.wireOp",EDGE,"E453"),sQuery(id+"F4.wireOp",EDGE,"E454"),sQuery(id+"F4.wireOp",EDGE,"E455"),sQuery(id+"F4.wireOp",EDGE,"E456"),sQuery(id+"F4.wireOp",EDGE,"E457"),sQuery(id+"F4.wireOp",EDGE,"E458"),sQuery(id+"F4.wireOp",EDGE,"E459"),sQuery(id+"F4.wireOp",EDGE,"E460"),sQuery(id+"F4.wireOp",EDGE,"E461")])]});
            var Q3;
            Q3=makeQuery(id+"F5.opExtrude","SWEPT_BODY",BODY,{"disambiguationData":[OSD([sQuery(id+"F4.wireOp",EDGE,"E462"),sQuery(id+"F4.wireOp",EDGE,"E463"),sQuery(id+"F4.wireOp",EDGE,"E464"),sQuery(id+"F4.wireOp",EDGE,"E465"),sQuery(id+"F4.wireOp",EDGE,"E466"),sQuery(id+"F4.wireOp",EDGE,"E467"),sQuery(id+"F4.wireOp",EDGE,"E468"),sQuery(id+"F4.wireOp",EDGE,"E469"),sQuery(id+"F4.wireOp",EDGE,"E470"),sQuery(id+"F4.wireOp",EDGE,"E471"),sQuery(id+"F4.wireOp",EDGE,"E472"),sQuery(id+"F4.wireOp",EDGE,"E473"),sQuery(id+"F4.wireOp",EDGE,"E474"),sQuery(id+"F4.wireOp",EDGE,"E475"),sQuery(id+"F4.wireOp",EDGE,"E476"),sQuery(id+"F4.wireOp",EDGE,"E477"),sQuery(id+"F4.wireOp",EDGE,"E478"),sQuery(id+"F4.wireOp",EDGE,"E479"),sQuery(id+"F4.wireOp",EDGE,"E480"),sQuery(id+"F4.wireOp",EDGE,"E481"),sQuery(id+"F4.wireOp",EDGE,"E482"),sQuery(id+"F4.wireOp",EDGE,"E483"),sQuery(id+"F4.wireOp",EDGE,"E484"),sQuery(id+"F4.wireOp",EDGE,"E485"),sQuery(id+"F4.wireOp",EDGE,"E486"),sQuery(id+"F4.wireOp",EDGE,"E487"),sQuery(id+"F4.wireOp",EDGE,"E488"),sQuery(id+"F4.wireOp",EDGE,"E489"),sQuery(id+"F4.wireOp",EDGE,"E490"),sQuery(id+"F4.wireOp",EDGE,"E491"),sQuery(id+"F4.wireOp",EDGE,"E492"),sQuery(id+"F4.wireOp",EDGE,"E493"),sQuery(id+"F4.wireOp",EDGE,"E494"),sQuery(id+"F4.wireOp",EDGE,"E495"),sQuery(id+"F4.wireOp",EDGE,"E496"),sQuery(id+"F4.wireOp",EDGE,"E497"),sQuery(id+"F4.wireOp",EDGE,"E498"),sQuery(id+"F4.wireOp",EDGE,"E499"),sQuery(id+"F4.wireOp",EDGE,"E500"),sQuery(id+"F4.wireOp",EDGE,"E501"),sQuery(id+"F4.wireOp",EDGE,"E502"),sQuery(id+"F4.wireOp",EDGE,"E503"),sQuery(id+"F4.wireOp",EDGE,"E504"),sQuery(id+"F4.wireOp",EDGE,"E505"),sQuery(id+"F4.wireOp",EDGE,"E506"),sQuery(id+"F4.wireOp",EDGE,"E507"),sQuery(id+"F4.wireOp",EDGE,"E508"),sQuery(id+"F4.wireOp",EDGE,"E509"),sQuery(id+"F4.wireOp",EDGE,"E510"),sQuery(id+"F4.wireOp",EDGE,"E511"),sQuery(id+"F4.wireOp",EDGE,"E512"),sQuery(id+"F4.wireOp",EDGE,"E513"),sQuery(id+"F4.wireOp",EDGE,"E514"),sQuery(id+"F4.wireOp",EDGE,"E515"),sQuery(id+"F4.wireOp",EDGE,"E516"),sQuery(id+"F4.wireOp",EDGE,"E517"),sQuery(id+"F4.wireOp",EDGE,"E518"),sQuery(id+"F4.wireOp",EDGE,"E519"),sQuery(id+"F4.wireOp",EDGE,"E520"),sQuery(id+"F4.wireOp",EDGE,"E521"),sQuery(id+"F4.wireOp",EDGE,"E522"),sQuery(id+"F4.wireOp",EDGE,"E523"),sQuery(id+"F4.wireOp",EDGE,"E524"),sQuery(id+"F4.wireOp",EDGE,"E525"),sQuery(id+"F4.wireOp",EDGE,"E525"),sQuery(id+"F4.wireOp",EDGE,"E525"),sQuery(id+"F4.wireOp",EDGE,"E526"),sQuery(id+"F4.wireOp",EDGE,"E527"),sQuery(id+"F4.wireOp",EDGE,"E528"),sQuery(id+"F4.wireOp",EDGE,"E529"),sQuery(id+"F4.wireOp",EDGE,"E530"),sQuery(id+"F4.wireOp",EDGE,"E531"),sQuery(id+"F4.wireOp",EDGE,"E531"),sQuery(id+"F4.wireOp",EDGE,"E531"),sQuery(id+"F4.wireOp",EDGE,"E532"),sQuery(id+"F4.wireOp",EDGE,"E533"),sQuery(id+"F4.wireOp",EDGE,"E534"),sQuery(id+"F4.wireOp",EDGE,"E535"),sQuery(id+"F4.wireOp",EDGE,"E536"),sQuery(id+"F4.wireOp",EDGE,"E537"),sQuery(id+"F4.wireOp",EDGE,"E538"),sQuery(id+"F4.wireOp",EDGE,"E539"),sQuery(id+"F4.wireOp",EDGE,"E540"),sQuery(id+"F4.wireOp",EDGE,"E541"),sQuery(id+"F4.wireOp",EDGE,"E542"),sQuery(id+"F4.wireOp",EDGE,"E543"),sQuery(id+"F4.wireOp",EDGE,"E544"),sQuery(id+"F4.wireOp",EDGE,"E545"),sQuery(id+"F4.wireOp",EDGE,"E546"),sQuery(id+"F4.wireOp",EDGE,"E547"),sQuery(id+"F4.wireOp",EDGE,"E548"),sQuery(id+"F4.wireOp",EDGE,"E549"),sQuery(id+"F4.wireOp",EDGE,"E550"),sQuery(id+"F4.wireOp",EDGE,"E551"),sQuery(id+"F4.wireOp",EDGE,"E552"),sQuery(id+"F4.wireOp",EDGE,"E553"),sQuery(id+"F4.wireOp",EDGE,"E554"),sQuery(id+"F4.wireOp",EDGE,"E555"),sQuery(id+"F4.wireOp",EDGE,"E556"),sQuery(id+"F4.wireOp",EDGE,"E557"),sQuery(id+"F4.wireOp",EDGE,"E558"),sQuery(id+"F4.wireOp",EDGE,"E559"),sQuery(id+"F4.wireOp",EDGE,"E560"),sQuery(id+"F4.wireOp",EDGE,"E561"),sQuery(id+"F4.wireOp",EDGE,"E562"),sQuery(id+"F4.wireOp",EDGE,"E562"),sQuery(id+"F4.wireOp",EDGE,"E563"),sQuery(id+"F4.wireOp",EDGE,"E564"),sQuery(id+"F4.wireOp",EDGE,"E565"),sQuery(id+"F4.wireOp",EDGE,"E566"),sQuery(id+"F4.wireOp",EDGE,"E567"),sQuery(id+"F4.wireOp",EDGE,"E565"),sQuery(id+"F4.wireOp",EDGE,"E568"),sQuery(id+"F4.wireOp",EDGE,"E569"),sQuery(id+"F4.wireOp",EDGE,"E569"),sQuery(id+"F4.wireOp",EDGE,"E570"),sQuery(id+"F4.wireOp",EDGE,"E571"),sQuery(id+"F4.wireOp",EDGE,"E572"),sQuery(id+"F4.wireOp",EDGE,"E573"),sQuery(id+"F4.wireOp",EDGE,"E574")])]});
            var Q4;
            Q4=makeQuery(id+"F5.opExtrude","SWEPT_BODY",BODY,{"disambiguationData":[OSD([sQuery(id+"F4.wireOp",EDGE,"E575"),sQuery(id+"F4.wireOp",EDGE,"E576"),sQuery(id+"F4.wireOp",EDGE,"E577"),sQuery(id+"F4.wireOp",EDGE,"E578"),sQuery(id+"F4.wireOp",EDGE,"E579"),sQuery(id+"F4.wireOp",EDGE,"E580"),sQuery(id+"F4.wireOp",EDGE,"E581"),sQuery(id+"F4.wireOp",EDGE,"E582"),sQuery(id+"F4.wireOp",EDGE,"E583"),sQuery(id+"F4.wireOp",EDGE,"E584"),sQuery(id+"F4.wireOp",EDGE,"E585"),sQuery(id+"F4.wireOp",EDGE,"E586"),sQuery(id+"F4.wireOp",EDGE,"E587"),sQuery(id+"F4.wireOp",EDGE,"E588"),sQuery(id+"F4.wireOp",EDGE,"E589"),sQuery(id+"F4.wireOp",EDGE,"E590"),sQuery(id+"F4.wireOp",EDGE,"E591"),sQuery(id+"F4.wireOp",EDGE,"E592"),sQuery(id+"F4.wireOp",EDGE,"E593"),sQuery(id+"F4.wireOp",EDGE,"E594"),sQuery(id+"F4.wireOp",EDGE,"E595"),sQuery(id+"F4.wireOp",EDGE,"E596"),sQuery(id+"F4.wireOp",EDGE,"E597"),sQuery(id+"F4.wireOp",EDGE,"E598"),sQuery(id+"F4.wireOp",EDGE,"E599"),sQuery(id+"F4.wireOp",EDGE,"E600"),sQuery(id+"F4.wireOp",EDGE,"E601"),sQuery(id+"F4.wireOp",EDGE,"E602"),sQuery(id+"F4.wireOp",EDGE,"E603")])]});
            var Q5;
            Q5=makeQuery(id+"F5.opExtrude","SWEPT_BODY",BODY,{"disambiguationData":[OSD([sQuery(id+"F4.wireOp",EDGE,"E604"),sQuery(id+"F4.wireOp",EDGE,"E605"),sQuery(id+"F4.wireOp",EDGE,"E606"),sQuery(id+"F4.wireOp",EDGE,"E607"),sQuery(id+"F4.wireOp",EDGE,"E608"),sQuery(id+"F4.wireOp",EDGE,"E609"),sQuery(id+"F4.wireOp",EDGE,"E610"),sQuery(id+"F4.wireOp",EDGE,"E611"),sQuery(id+"F4.wireOp",EDGE,"E612"),sQuery(id+"F4.wireOp",EDGE,"E613"),sQuery(id+"F4.wireOp",EDGE,"E614"),sQuery(id+"F4.wireOp",EDGE,"E615"),sQuery(id+"F4.wireOp",EDGE,"E616"),sQuery(id+"F4.wireOp",EDGE,"E617"),sQuery(id+"F4.wireOp",EDGE,"E617"),sQuery(id+"F4.wireOp",EDGE,"E618"),sQuery(id+"F4.wireOp",EDGE,"E619"),sQuery(id+"F4.wireOp",EDGE,"E620"),sQuery(id+"F4.wireOp",EDGE,"E621"),sQuery(id+"F4.wireOp",EDGE,"E622"),sQuery(id+"F4.wireOp",EDGE,"E623"),sQuery(id+"F4.wireOp",EDGE,"E624"),sQuery(id+"F4.wireOp",EDGE,"E625"),sQuery(id+"F4.wireOp",EDGE,"E626"),sQuery(id+"F4.wireOp",EDGE,"E627"),sQuery(id+"F4.wireOp",EDGE,"E628"),sQuery(id+"F4.wireOp",EDGE,"E629"),sQuery(id+"F4.wireOp",EDGE,"E630"),sQuery(id+"F4.wireOp",EDGE,"E631"),sQuery(id+"F4.wireOp",EDGE,"E632"),sQuery(id+"F4.wireOp",EDGE,"E633"),sQuery(id+"F4.wireOp",EDGE,"E634"),sQuery(id+"F4.wireOp",EDGE,"E635"),sQuery(id+"F4.wireOp",EDGE,"E636"),sQuery(id+"F4.wireOp",EDGE,"E637"),sQuery(id+"F4.wireOp",EDGE,"E638"),sQuery(id+"F4.wireOp",EDGE,"E639"),sQuery(id+"F4.wireOp",EDGE,"E640"),sQuery(id+"F4.wireOp",EDGE,"E641"),sQuery(id+"F4.wireOp",EDGE,"E642"),sQuery(id+"F4.wireOp",EDGE,"E643"),sQuery(id+"F4.wireOp",EDGE,"E644"),sQuery(id+"F4.wireOp",EDGE,"E645"),sQuery(id+"F4.wireOp",EDGE,"E646"),sQuery(id+"F4.wireOp",EDGE,"E647"),sQuery(id+"F4.wireOp",EDGE,"E648"),sQuery(id+"F4.wireOp",EDGE,"E649"),sQuery(id+"F4.wireOp",EDGE,"E650"),sQuery(id+"F4.wireOp",EDGE,"E651"),sQuery(id+"F4.wireOp",EDGE,"E652"),sQuery(id+"F4.wireOp",EDGE,"E653"),sQuery(id+"F4.wireOp",EDGE,"E654"),sQuery(id+"F4.wireOp",EDGE,"E655"),sQuery(id+"F4.wireOp",EDGE,"E656"),sQuery(id+"F4.wireOp",EDGE,"E657"),sQuery(id+"F4.wireOp",EDGE,"E658"),sQuery(id+"F4.wireOp",EDGE,"E659"),sQuery(id+"F4.wireOp",EDGE,"E660"),sQuery(id+"F4.wireOp",EDGE,"E661"),sQuery(id+"F4.wireOp",EDGE,"E662"),sQuery(id+"F4.wireOp",EDGE,"E663"),sQuery(id+"F4.wireOp",EDGE,"E664"),sQuery(id+"F4.wireOp",EDGE,"E665"),sQuery(id+"F4.wireOp",EDGE,"E665"),sQuery(id+"F4.wireOp",EDGE,"E666"),sQuery(id+"F4.wireOp",EDGE,"E667"),sQuery(id+"F4.wireOp",EDGE,"E668"),sQuery(id+"F4.wireOp",EDGE,"E669"),sQuery(id+"F4.wireOp",EDGE,"E670"),sQuery(id+"F4.wireOp",EDGE,"E671"),sQuery(id+"F4.wireOp",EDGE,"E672"),sQuery(id+"F4.wireOp",EDGE,"E673"),sQuery(id+"F4.wireOp",EDGE,"E674"),sQuery(id+"F4.wireOp",EDGE,"E674"),sQuery(id+"F4.wireOp",EDGE,"E675"),sQuery(id+"F4.wireOp",EDGE,"E676"),sQuery(id+"F4.wireOp",EDGE,"E676"),sQuery(id+"F4.wireOp",EDGE,"E677"),sQuery(id+"F4.wireOp",EDGE,"E678"),sQuery(id+"F4.wireOp",EDGE,"E679"),sQuery(id+"F4.wireOp",EDGE,"E680"),sQuery(id+"F4.wireOp",EDGE,"E681"),sQuery(id+"F4.wireOp",EDGE,"E682"),sQuery(id+"F4.wireOp",EDGE,"E683"),sQuery(id+"F4.wireOp",EDGE,"E684"),sQuery(id+"F4.wireOp",EDGE,"E685"),sQuery(id+"F4.wireOp",EDGE,"E686"),sQuery(id+"F4.wireOp",EDGE,"E687"),sQuery(id+"F4.wireOp",EDGE,"E687"),sQuery(id+"F4.wireOp",EDGE,"E688"),sQuery(id+"F4.wireOp",EDGE,"E689"),sQuery(id+"F4.wireOp",EDGE,"E690"),sQuery(id+"F4.wireOp",EDGE,"E691"),sQuery(id+"F4.wireOp",EDGE,"E692"),sQuery(id+"F4.wireOp",EDGE,"E693"),sQuery(id+"F4.wireOp",EDGE,"E694"),sQuery(id+"F4.wireOp",EDGE,"E695"),sQuery(id+"F4.wireOp",EDGE,"E696"),sQuery(id+"F4.wireOp",EDGE,"E697"),sQuery(id+"F4.wireOp",EDGE,"E698"),sQuery(id+"F4.wireOp",EDGE,"E699"),sQuery(id+"F4.wireOp",EDGE,"E700"),sQuery(id+"F4.wireOp",EDGE,"E701"),sQuery(id+"F4.wireOp",EDGE,"E702"),sQuery(id+"F4.wireOp",EDGE,"E703"),sQuery(id+"F4.wireOp",EDGE,"E704"),sQuery(id+"F4.wireOp",EDGE,"E705"),sQuery(id+"F4.wireOp",EDGE,"E706"),sQuery(id+"F4.wireOp",EDGE,"E707"),sQuery(id+"F4.wireOp",EDGE,"E708"),sQuery(id+"F4.wireOp",EDGE,"E708"),sQuery(id+"F4.wireOp",EDGE,"E708")])]});
            var Q6;
            Q6=makeQuery(id+"F5.opExtrude","SWEPT_BODY",BODY,{"disambiguationData":[OSD([sQuery(id+"F4.wireOp",EDGE,"E709"),sQuery(id+"F4.wireOp",EDGE,"E710"),sQuery(id+"F4.wireOp",EDGE,"E711"),sQuery(id+"F4.wireOp",EDGE,"E712"),sQuery(id+"F4.wireOp",EDGE,"E713"),sQuery(id+"F4.wireOp",EDGE,"E714"),sQuery(id+"F4.wireOp",EDGE,"E715"),sQuery(id+"F4.wireOp",EDGE,"E716"),sQuery(id+"F4.wireOp",EDGE,"E717"),sQuery(id+"F4.wireOp",EDGE,"E718"),sQuery(id+"F4.wireOp",EDGE,"E719"),sQuery(id+"F4.wireOp",EDGE,"E720"),sQuery(id+"F4.wireOp",EDGE,"E721"),sQuery(id+"F4.wireOp",EDGE,"E722"),sQuery(id+"F4.wireOp",EDGE,"E723"),sQuery(id+"F4.wireOp",EDGE,"E723"),sQuery(id+"F4.wireOp",EDGE,"E724"),sQuery(id+"F4.wireOp",EDGE,"E725"),sQuery(id+"F4.wireOp",EDGE,"E726"),sQuery(id+"F4.wireOp",EDGE,"E727"),sQuery(id+"F4.wireOp",EDGE,"E728"),sQuery(id+"F4.wireOp",EDGE,"E729"),sQuery(id+"F4.wireOp",EDGE,"E730"),sQuery(id+"F4.wireOp",EDGE,"E731"),sQuery(id+"F4.wireOp",EDGE,"E732"),sQuery(id+"F4.wireOp",EDGE,"E733"),sQuery(id+"F4.wireOp",EDGE,"E734"),sQuery(id+"F4.wireOp",EDGE,"E735"),sQuery(id+"F4.wireOp",EDGE,"E736"),sQuery(id+"F4.wireOp",EDGE,"E737"),sQuery(id+"F4.wireOp",EDGE,"E738"),sQuery(id+"F4.wireOp",EDGE,"E739"),sQuery(id+"F4.wireOp",EDGE,"E740"),sQuery(id+"F4.wireOp",EDGE,"E741"),sQuery(id+"F4.wireOp",EDGE,"E742"),sQuery(id+"F4.wireOp",EDGE,"E743"),sQuery(id+"F4.wireOp",EDGE,"E744"),sQuery(id+"F4.wireOp",EDGE,"E745"),sQuery(id+"F4.wireOp",EDGE,"E746"),sQuery(id+"F4.wireOp",EDGE,"E747"),sQuery(id+"F4.wireOp",EDGE,"E748"),sQuery(id+"F4.wireOp",EDGE,"E749"),sQuery(id+"F4.wireOp",EDGE,"E750"),sQuery(id+"F4.wireOp",EDGE,"E751"),sQuery(id+"F4.wireOp",EDGE,"E752"),sQuery(id+"F4.wireOp",EDGE,"E753"),sQuery(id+"F4.wireOp",EDGE,"E754"),sQuery(id+"F4.wireOp",EDGE,"E755"),sQuery(id+"F4.wireOp",EDGE,"E756"),sQuery(id+"F4.wireOp",EDGE,"E757"),sQuery(id+"F4.wireOp",EDGE,"E758"),sQuery(id+"F4.wireOp",EDGE,"E758"),sQuery(id+"F4.wireOp",EDGE,"E758"),sQuery(id+"F4.wireOp",EDGE,"E759"),sQuery(id+"F4.wireOp",EDGE,"E760"),sQuery(id+"F4.wireOp",EDGE,"E760"),sQuery(id+"F4.wireOp",EDGE,"E761"),sQuery(id+"F4.wireOp",EDGE,"E762"),sQuery(id+"F4.wireOp",EDGE,"E763"),sQuery(id+"F4.wireOp",EDGE,"E764"),sQuery(id+"F4.wireOp",EDGE,"E765"),sQuery(id+"F4.wireOp",EDGE,"E766"),sQuery(id+"F4.wireOp",EDGE,"E767"),sQuery(id+"F4.wireOp",EDGE,"E768"),sQuery(id+"F4.wireOp",EDGE,"E768"),sQuery(id+"F4.wireOp",EDGE,"E768"),sQuery(id+"F4.wireOp",EDGE,"E769"),sQuery(id+"F4.wireOp",EDGE,"E770"),sQuery(id+"F4.wireOp",EDGE,"E771"),sQuery(id+"F4.wireOp",EDGE,"E772"),sQuery(id+"F4.wireOp",EDGE,"E773"),sQuery(id+"F4.wireOp",EDGE,"E774"),sQuery(id+"F4.wireOp",EDGE,"E775"),sQuery(id+"F4.wireOp",EDGE,"E776"),sQuery(id+"F4.wireOp",EDGE,"E777"),sQuery(id+"F4.wireOp",EDGE,"E778"),sQuery(id+"F4.wireOp",EDGE,"E779"),sQuery(id+"F4.wireOp",EDGE,"E780"),sQuery(id+"F4.wireOp",EDGE,"E781"),sQuery(id+"F4.wireOp",EDGE,"E782"),sQuery(id+"F4.wireOp",EDGE,"E783"),sQuery(id+"F4.wireOp",EDGE,"E784"),sQuery(id+"F4.wireOp",EDGE,"E785"),sQuery(id+"F4.wireOp",EDGE,"E786"),sQuery(id+"F4.wireOp",EDGE,"E787"),sQuery(id+"F4.wireOp",EDGE,"E788"),sQuery(id+"F4.wireOp",EDGE,"E789"),sQuery(id+"F4.wireOp",EDGE,"E790"),sQuery(id+"F4.wireOp",EDGE,"E791"),sQuery(id+"F4.wireOp",EDGE,"E792"),sQuery(id+"F4.wireOp",EDGE,"E793"),sQuery(id+"F4.wireOp",EDGE,"E794"),sQuery(id+"F4.wireOp",EDGE,"E795"),sQuery(id+"F4.wireOp",EDGE,"E796"),sQuery(id+"F4.wireOp",EDGE,"E797"),sQuery(id+"F4.wireOp",EDGE,"E798"),sQuery(id+"F4.wireOp",EDGE,"E799"),sQuery(id+"F4.wireOp",EDGE,"E800"),sQuery(id+"F4.wireOp",EDGE,"E801"),sQuery(id+"F4.wireOp",EDGE,"E802"),sQuery(id+"F4.wireOp",EDGE,"E803"),sQuery(id+"F4.wireOp",EDGE,"E804"),sQuery(id+"F4.wireOp",EDGE,"E805"),sQuery(id+"F4.wireOp",EDGE,"E806"),sQuery(id+"F4.wireOp",EDGE,"E807"),sQuery(id+"F4.wireOp",EDGE,"E808"),sQuery(id+"F4.wireOp",EDGE,"E809"),sQuery(id+"F4.wireOp",EDGE,"E810"),sQuery(id+"F4.wireOp",EDGE,"E811"),sQuery(id+"F4.wireOp",EDGE,"E812"),sQuery(id+"F4.wireOp",EDGE,"E813"),sQuery(id+"F4.wireOp",EDGE,"E814"),sQuery(id+"F4.wireOp",EDGE,"E815"),sQuery(id+"F4.wireOp",EDGE,"E816"),sQuery(id+"F4.wireOp",EDGE,"E817"),sQuery(id+"F4.wireOp",EDGE,"E818"),sQuery(id+"F4.wireOp",EDGE,"E819"),sQuery(id+"F4.wireOp",EDGE,"E820"),sQuery(id+"F4.wireOp",EDGE,"E821"),sQuery(id+"F4.wireOp",EDGE,"E822"),sQuery(id+"F4.wireOp",EDGE,"E823"),sQuery(id+"F4.wireOp",EDGE,"E824"),sQuery(id+"F4.wireOp",EDGE,"E825"),sQuery(id+"F4.wireOp",EDGE,"E826"),sQuery(id+"F4.wireOp",EDGE,"E827"),sQuery(id+"F4.wireOp",EDGE,"E828"),sQuery(id+"F4.wireOp",EDGE,"E829"),sQuery(id+"F4.wireOp",EDGE,"E830"),sQuery(id+"F4.wireOp",EDGE,"E831"),sQuery(id+"F4.wireOp",EDGE,"E832"),sQuery(id+"F4.wireOp",EDGE,"E833")])]});
            var Q7;
            Q7=makeQuery(id+"F5.opExtrude","SWEPT_BODY",BODY,{"disambiguationData":[OSD([sQuery(id+"F4.wireOp",EDGE,"E834"),sQuery(id+"F4.wireOp",EDGE,"E835"),sQuery(id+"F4.wireOp",EDGE,"E836"),sQuery(id+"F4.wireOp",EDGE,"E837"),sQuery(id+"F4.wireOp",EDGE,"E838"),sQuery(id+"F4.wireOp",EDGE,"E839"),sQuery(id+"F4.wireOp",EDGE,"E840"),sQuery(id+"F4.wireOp",EDGE,"E841"),sQuery(id+"F4.wireOp",EDGE,"E842"),sQuery(id+"F4.wireOp",EDGE,"E843"),sQuery(id+"F4.wireOp",EDGE,"E844"),sQuery(id+"F4.wireOp",EDGE,"E845"),sQuery(id+"F4.wireOp",EDGE,"E846"),sQuery(id+"F4.wireOp",EDGE,"E847"),sQuery(id+"F4.wireOp",EDGE,"E848"),sQuery(id+"F4.wireOp",EDGE,"E849"),sQuery(id+"F4.wireOp",EDGE,"E850"),sQuery(id+"F4.wireOp",EDGE,"E851"),sQuery(id+"F4.wireOp",EDGE,"E852"),sQuery(id+"F4.wireOp",EDGE,"E853"),sQuery(id+"F4.wireOp",EDGE,"E854"),sQuery(id+"F4.wireOp",EDGE,"E855"),sQuery(id+"F4.wireOp",EDGE,"E856"),sQuery(id+"F4.wireOp",EDGE,"E857"),sQuery(id+"F4.wireOp",EDGE,"E858"),sQuery(id+"F4.wireOp",EDGE,"E859"),sQuery(id+"F4.wireOp",EDGE,"E860"),sQuery(id+"F4.wireOp",EDGE,"E861"),sQuery(id+"F4.wireOp",EDGE,"E862"),sQuery(id+"F4.wireOp",EDGE,"E863"),sQuery(id+"F4.wireOp",EDGE,"E864"),sQuery(id+"F4.wireOp",EDGE,"E865"),sQuery(id+"F4.wireOp",EDGE,"E866"),sQuery(id+"F4.wireOp",EDGE,"E867"),sQuery(id+"F4.wireOp",EDGE,"E868"),sQuery(id+"F4.wireOp",EDGE,"E869"),sQuery(id+"F4.wireOp",EDGE,"E870"),sQuery(id+"F4.wireOp",EDGE,"E871"),sQuery(id+"F4.wireOp",EDGE,"E872"),sQuery(id+"F4.wireOp",EDGE,"E873"),sQuery(id+"F4.wireOp",EDGE,"E874"),sQuery(id+"F4.wireOp",EDGE,"E875"),sQuery(id+"F4.wireOp",EDGE,"E876"),sQuery(id+"F4.wireOp",EDGE,"E877"),sQuery(id+"F4.wireOp",EDGE,"E878"),sQuery(id+"F4.wireOp",EDGE,"E879"),sQuery(id+"F4.wireOp",EDGE,"E880"),sQuery(id+"F4.wireOp",EDGE,"E881"),sQuery(id+"F4.wireOp",EDGE,"E882"),sQuery(id+"F4.wireOp",EDGE,"E883"),sQuery(id+"F4.wireOp",EDGE,"E884"),sQuery(id+"F4.wireOp",EDGE,"E885"),sQuery(id+"F4.wireOp",EDGE,"E886"),sQuery(id+"F4.wireOp",EDGE,"E887"),sQuery(id+"F4.wireOp",EDGE,"E888"),sQuery(id+"F4.wireOp",EDGE,"E889"),sQuery(id+"F4.wireOp",EDGE,"E890"),sQuery(id+"F4.wireOp",EDGE,"E891"),sQuery(id+"F4.wireOp",EDGE,"E892"),sQuery(id+"F4.wireOp",EDGE,"E893"),sQuery(id+"F4.wireOp",EDGE,"E894"),sQuery(id+"F4.wireOp",EDGE,"E895"),sQuery(id+"F4.wireOp",EDGE,"E896"),sQuery(id+"F4.wireOp",EDGE,"E897"),sQuery(id+"F4.wireOp",EDGE,"E898"),sQuery(id+"F4.wireOp",EDGE,"E899"),sQuery(id+"F4.wireOp",EDGE,"E900"),sQuery(id+"F4.wireOp",EDGE,"E901"),sQuery(id+"F4.wireOp",EDGE,"E901"),sQuery(id+"F4.wireOp",EDGE,"E902"),sQuery(id+"F4.wireOp",EDGE,"E903"),sQuery(id+"F4.wireOp",EDGE,"E904"),sQuery(id+"F4.wireOp",EDGE,"E905"),sQuery(id+"F4.wireOp",EDGE,"E906"),sQuery(id+"F4.wireOp",EDGE,"E907"),sQuery(id+"F4.wireOp",EDGE,"E908"),sQuery(id+"F4.wireOp",EDGE,"E909"),sQuery(id+"F4.wireOp",EDGE,"E910"),sQuery(id+"F4.wireOp",EDGE,"E911"),sQuery(id+"F4.wireOp",EDGE,"E912")])]});
            var Q8;
            Q8=makeQuery(id+"F5.opExtrude","SWEPT_BODY",BODY,{"disambiguationData":[OSD([sQuery(id+"F4.wireOp",EDGE,"E913"),sQuery(id+"F4.wireOp",EDGE,"E914"),sQuery(id+"F4.wireOp",EDGE,"E915"),sQuery(id+"F4.wireOp",EDGE,"E916"),sQuery(id+"F4.wireOp",EDGE,"E917"),sQuery(id+"F4.wireOp",EDGE,"E918"),sQuery(id+"F4.wireOp",EDGE,"E919"),sQuery(id+"F4.wireOp",EDGE,"E920"),sQuery(id+"F4.wireOp",EDGE,"E921"),sQuery(id+"F4.wireOp",EDGE,"E922"),sQuery(id+"F4.wireOp",EDGE,"E923"),sQuery(id+"F4.wireOp",EDGE,"E924"),sQuery(id+"F4.wireOp",EDGE,"E925"),sQuery(id+"F4.wireOp",EDGE,"E926"),sQuery(id+"F4.wireOp",EDGE,"E927"),sQuery(id+"F4.wireOp",EDGE,"E928"),sQuery(id+"F4.wireOp",EDGE,"E929"),sQuery(id+"F4.wireOp",EDGE,"E930"),sQuery(id+"F4.wireOp",EDGE,"E931"),sQuery(id+"F4.wireOp",EDGE,"E932"),sQuery(id+"F4.wireOp",EDGE,"E933"),sQuery(id+"F4.wireOp",EDGE,"E934"),sQuery(id+"F4.wireOp",EDGE,"E935"),sQuery(id+"F4.wireOp",EDGE,"E936"),sQuery(id+"F4.wireOp",EDGE,"E937"),sQuery(id+"F4.wireOp",EDGE,"E938"),sQuery(id+"F4.wireOp",EDGE,"E939"),sQuery(id+"F4.wireOp",EDGE,"E940"),sQuery(id+"F4.wireOp",EDGE,"E941"),sQuery(id+"F4.wireOp",EDGE,"E942"),sQuery(id+"F4.wireOp",EDGE,"E943"),sQuery(id+"F4.wireOp",EDGE,"E944"),sQuery(id+"F4.wireOp",EDGE,"E945"),sQuery(id+"F4.wireOp",EDGE,"E946"),sQuery(id+"F4.wireOp",EDGE,"E947"),sQuery(id+"F4.wireOp",EDGE,"E947"),sQuery(id+"F4.wireOp",EDGE,"E948"),sQuery(id+"F4.wireOp",EDGE,"E949"),sQuery(id+"F4.wireOp",EDGE,"E950"),sQuery(id+"F4.wireOp",EDGE,"E951"),sQuery(id+"F4.wireOp",EDGE,"E952"),sQuery(id+"F4.wireOp",EDGE,"E953"),sQuery(id+"F4.wireOp",EDGE,"E954"),sQuery(id+"F4.wireOp",EDGE,"E955"),sQuery(id+"F4.wireOp",EDGE,"E956"),sQuery(id+"F4.wireOp",EDGE,"E957"),sQuery(id+"F4.wireOp",EDGE,"E958"),sQuery(id+"F4.wireOp",EDGE,"E959"),sQuery(id+"F4.wireOp",EDGE,"E959"),sQuery(id+"F4.wireOp",EDGE,"E960"),sQuery(id+"F4.wireOp",EDGE,"E961"),sQuery(id+"F4.wireOp",EDGE,"E962"),sQuery(id+"F4.wireOp",EDGE,"E963"),sQuery(id+"F4.wireOp",EDGE,"E964"),sQuery(id+"F4.wireOp",EDGE,"E965"),sQuery(id+"F4.wireOp",EDGE,"E966"),sQuery(id+"F4.wireOp",EDGE,"E967"),sQuery(id+"F4.wireOp",EDGE,"E968"),sQuery(id+"F4.wireOp",EDGE,"E969"),sQuery(id+"F4.wireOp",EDGE,"E970"),sQuery(id+"F4.wireOp",EDGE,"E971"),sQuery(id+"F4.wireOp",EDGE,"E972"),sQuery(id+"F4.wireOp",EDGE,"E973"),sQuery(id+"F4.wireOp",EDGE,"E974"),sQuery(id+"F4.wireOp",EDGE,"E975"),sQuery(id+"F4.wireOp",EDGE,"E976"),sQuery(id+"F4.wireOp",EDGE,"E977"),sQuery(id+"F4.wireOp",EDGE,"E978"),sQuery(id+"F4.wireOp",EDGE,"E979"),sQuery(id+"F4.wireOp",EDGE,"E980"),sQuery(id+"F4.wireOp",EDGE,"E981"),sQuery(id+"F4.wireOp",EDGE,"E982"),sQuery(id+"F4.wireOp",EDGE,"E983"),sQuery(id+"F4.wireOp",EDGE,"E984"),sQuery(id+"F4.wireOp",EDGE,"E985"),sQuery(id+"F4.wireOp",EDGE,"E986"),sQuery(id+"F4.wireOp",EDGE,"E987"),sQuery(id+"F4.wireOp",EDGE,"E988"),sQuery(id+"F4.wireOp",EDGE,"E989"),sQuery(id+"F4.wireOp",EDGE,"E990"),sQuery(id+"F4.wireOp",EDGE,"E991"),sQuery(id+"F4.wireOp",EDGE,"E992"),sQuery(id+"F4.wireOp",EDGE,"E992"),sQuery(id+"F4.wireOp",EDGE,"E993"),sQuery(id+"F4.wireOp",EDGE,"E994"),sQuery(id+"F4.wireOp",EDGE,"E995"),sQuery(id+"F4.wireOp",EDGE,"E996"),sQuery(id+"F4.wireOp",EDGE,"E997"),sQuery(id+"F4.wireOp",EDGE,"E998"),sQuery(id+"F4.wireOp",EDGE,"E999"),sQuery(id+"F4.wireOp",EDGE,"E1000"),sQuery(id+"F4.wireOp",EDGE,"E1001"),sQuery(id+"F4.wireOp",EDGE,"E1002"),sQuery(id+"F4.wireOp",EDGE,"E1003"),sQuery(id+"F4.wireOp",EDGE,"E1004"),sQuery(id+"F4.wireOp",EDGE,"E1005"),sQuery(id+"F4.wireOp",EDGE,"E1006"),sQuery(id+"F4.wireOp",EDGE,"E1007"),sQuery(id+"F4.wireOp",EDGE,"E1008"),sQuery(id+"F4.wireOp",EDGE,"E1009"),sQuery(id+"F4.wireOp",EDGE,"E1010"),sQuery(id+"F4.wireOp",EDGE,"E1011"),sQuery(id+"F4.wireOp",EDGE,"E1012"),sQuery(id+"F4.wireOp",EDGE,"E1013"),sQuery(id+"F4.wireOp",EDGE,"E1014"),sQuery(id+"F4.wireOp",EDGE,"E1015"),sQuery(id+"F4.wireOp",EDGE,"E1016"),sQuery(id+"F4.wireOp",EDGE,"E1017"),sQuery(id+"F4.wireOp",EDGE,"E1018"),sQuery(id+"F4.wireOp",EDGE,"E1019")])]});
            var Q9;
            Q9=makeQuery(id+"F5.opExtrude","SWEPT_BODY",BODY,{"disambiguationData":[OSD([sQuery(id+"F4.wireOp",EDGE,"E1020"),sQuery(id+"F4.wireOp",EDGE,"E1021"),sQuery(id+"F4.wireOp",EDGE,"E1022"),sQuery(id+"F4.wireOp",EDGE,"E1023"),sQuery(id+"F4.wireOp",EDGE,"E1024"),sQuery(id+"F4.wireOp",EDGE,"E1025"),sQuery(id+"F4.wireOp",EDGE,"E1026"),sQuery(id+"F4.wireOp",EDGE,"E1027"),sQuery(id+"F4.wireOp",EDGE,"E1028"),sQuery(id+"F4.wireOp",EDGE,"E1029"),sQuery(id+"F4.wireOp",EDGE,"E1030"),sQuery(id+"F4.wireOp",EDGE,"E1031"),sQuery(id+"F4.wireOp",EDGE,"E1031"),sQuery(id+"F4.wireOp",EDGE,"E1032"),sQuery(id+"F4.wireOp",EDGE,"E1033"),sQuery(id+"F4.wireOp",EDGE,"E1034"),sQuery(id+"F4.wireOp",EDGE,"E1035"),sQuery(id+"F4.wireOp",EDGE,"E1036"),sQuery(id+"F4.wireOp",EDGE,"E1037"),sQuery(id+"F4.wireOp",EDGE,"E1038"),sQuery(id+"F4.wireOp",EDGE,"E1039"),sQuery(id+"F4.wireOp",EDGE,"E1040"),sQuery(id+"F4.wireOp",EDGE,"E1041"),sQuery(id+"F4.wireOp",EDGE,"E1041"),sQuery(id+"F4.wireOp",EDGE,"E1042"),sQuery(id+"F4.wireOp",EDGE,"E1043"),sQuery(id+"F4.wireOp",EDGE,"E1044"),sQuery(id+"F4.wireOp",EDGE,"E1045"),sQuery(id+"F4.wireOp",EDGE,"E1046"),sQuery(id+"F4.wireOp",EDGE,"E1047"),sQuery(id+"F4.wireOp",EDGE,"E1048"),sQuery(id+"F4.wireOp",EDGE,"E1049"),sQuery(id+"F4.wireOp",EDGE,"E1049"),sQuery(id+"F4.wireOp",EDGE,"E1049"),sQuery(id+"F4.wireOp",EDGE,"E1049"),sQuery(id+"F4.wireOp",EDGE,"E1050"),sQuery(id+"F4.wireOp",EDGE,"E1051"),sQuery(id+"F4.wireOp",EDGE,"E1052"),sQuery(id+"F4.wireOp",EDGE,"E1053"),sQuery(id+"F4.wireOp",EDGE,"E1054"),sQuery(id+"F4.wireOp",EDGE,"E1055"),sQuery(id+"F4.wireOp",EDGE,"E1056"),sQuery(id+"F4.wireOp",EDGE,"E1057"),sQuery(id+"F4.wireOp",EDGE,"E1058"),sQuery(id+"F4.wireOp",EDGE,"E1059"),sQuery(id+"F4.wireOp",EDGE,"E1060"),sQuery(id+"F4.wireOp",EDGE,"E1061"),sQuery(id+"F4.wireOp",EDGE,"E1062"),sQuery(id+"F4.wireOp",EDGE,"E1063"),sQuery(id+"F4.wireOp",EDGE,"E1064"),sQuery(id+"F4.wireOp",EDGE,"E1065"),sQuery(id+"F4.wireOp",EDGE,"E1066"),sQuery(id+"F4.wireOp",EDGE,"E1067"),sQuery(id+"F4.wireOp",EDGE,"E1068"),sQuery(id+"F4.wireOp",EDGE,"E1069"),sQuery(id+"F4.wireOp",EDGE,"E1070"),sQuery(id+"F4.wireOp",EDGE,"E1071"),sQuery(id+"F4.wireOp",EDGE,"E1072"),sQuery(id+"F4.wireOp",EDGE,"E1073"),sQuery(id+"F4.wireOp",EDGE,"E1074"),sQuery(id+"F4.wireOp",EDGE,"E1075"),sQuery(id+"F4.wireOp",EDGE,"E1076"),sQuery(id+"F4.wireOp",EDGE,"E1077"),sQuery(id+"F4.wireOp",EDGE,"E1078"),sQuery(id+"F4.wireOp",EDGE,"E1079"),sQuery(id+"F4.wireOp",EDGE,"E1080"),sQuery(id+"F4.wireOp",EDGE,"E1081"),sQuery(id+"F4.wireOp",EDGE,"E1082"),sQuery(id+"F4.wireOp",EDGE,"E1083"),sQuery(id+"F4.wireOp",EDGE,"E1083"),sQuery(id+"F4.wireOp",EDGE,"E1084"),sQuery(id+"F4.wireOp",EDGE,"E1085"),sQuery(id+"F4.wireOp",EDGE,"E1086"),sQuery(id+"F4.wireOp",EDGE,"E1087"),sQuery(id+"F4.wireOp",EDGE,"E1088"),sQuery(id+"F4.wireOp",EDGE,"E1089"),sQuery(id+"F4.wireOp",EDGE,"E1090"),sQuery(id+"F4.wireOp",EDGE,"E1090"),sQuery(id+"F4.wireOp",EDGE,"E1091"),sQuery(id+"F4.wireOp",EDGE,"E1092"),sQuery(id+"F4.wireOp",EDGE,"E1093"),sQuery(id+"F4.wireOp",EDGE,"E1094"),sQuery(id+"F4.wireOp",EDGE,"E1095"),sQuery(id+"F4.wireOp",EDGE,"E1096"),sQuery(id+"F4.wireOp",EDGE,"E1097"),sQuery(id+"F4.wireOp",EDGE,"E1098"),sQuery(id+"F4.wireOp",EDGE,"E1099"),sQuery(id+"F4.wireOp",EDGE,"E1100"),sQuery(id+"F4.wireOp",EDGE,"E1101"),sQuery(id+"F4.wireOp",EDGE,"E1102"),sQuery(id+"F4.wireOp",EDGE,"E1103"),sQuery(id+"F4.wireOp",EDGE,"E1104"),sQuery(id+"F4.wireOp",EDGE,"E1105"),sQuery(id+"F4.wireOp",EDGE,"E1106"),sQuery(id+"F4.wireOp",EDGE,"E1107"),sQuery(id+"F4.wireOp",EDGE,"E1108"),sQuery(id+"F4.wireOp",EDGE,"E1109"),sQuery(id+"F4.wireOp",EDGE,"E1110"),sQuery(id+"F4.wireOp",EDGE,"E1110"),sQuery(id+"F4.wireOp",EDGE,"E1110"),sQuery(id+"F4.wireOp",EDGE,"E1111"),sQuery(id+"F4.wireOp",EDGE,"E1112"),sQuery(id+"F4.wireOp",EDGE,"E1113"),sQuery(id+"F4.wireOp",EDGE,"E1114"),sQuery(id+"F4.wireOp",EDGE,"E1115"),sQuery(id+"F4.wireOp",EDGE,"E1116"),sQuery(id+"F4.wireOp",EDGE,"E1117"),sQuery(id+"F4.wireOp",EDGE,"E1118"),sQuery(id+"F4.wireOp",EDGE,"E1119"),sQuery(id+"F4.wireOp",EDGE,"E1120")])]});
            var Q10;
            Q10=makeQuery(id+"F5.opExtrude","SWEPT_BODY",BODY,{"disambiguationData":[OSD([sQuery(id+"F4.wireOp",EDGE,"E1121"),sQuery(id+"F4.wireOp",EDGE,"E1122"),sQuery(id+"F4.wireOp",EDGE,"E1123"),sQuery(id+"F4.wireOp",EDGE,"E1124"),sQuery(id+"F4.wireOp",EDGE,"E1125"),sQuery(id+"F4.wireOp",EDGE,"E1126"),sQuery(id+"F4.wireOp",EDGE,"E1127"),sQuery(id+"F4.wireOp",EDGE,"E1128"),sQuery(id+"F4.wireOp",EDGE,"E1129"),sQuery(id+"F4.wireOp",EDGE,"E1130"),sQuery(id+"F4.wireOp",EDGE,"E1131"),sQuery(id+"F4.wireOp",EDGE,"E1132"),sQuery(id+"F4.wireOp",EDGE,"E1133"),sQuery(id+"F4.wireOp",EDGE,"E1134"),sQuery(id+"F4.wireOp",EDGE,"E1135"),sQuery(id+"F4.wireOp",EDGE,"E1136")])]});
            var Q11;
            Q11=makeQuery(id+"F1.opExtrude","SWEPT_BODY",BODY,{"disambiguationData":[OSD([sQuery(id+"F0.wireOp",EDGE,"E2")])]});
            booleanBodies(context, id + "F11", {"operationType" : BooleanOperationType.SUBTRACTION, "tools" : qUnion([Q0, Q1, Q2, Q3, Q4, Q5, Q6, Q7, Q8, Q9, Q10]), "targets" : qUnion([Q11])});
        }
        {
            var Q0;
            Q0=makeQuery(id+"F3.opExtrude","CAP_EDGE",EDGE,{"disambiguationData":[OSD([sQuery(id+"F0.wireOp",EDGE,"E0")])],"isStart":false});
            var Q1;
            Q1=makeQuery(id+"F2.opExtrude","CAP_EDGE",EDGE,{"disambiguationData":[OSD([sQuery(id+"F0.wireOp",EDGE,"E1")])],"isStart":false});
            var Q2;
            Q2=makeQuery(id+"F1.opExtrude","CAP_EDGE",EDGE,{"disambiguationData":[OSD([sQuery(id+"F0.wireOp",EDGE,"E2")])],"isStart":false});
            var Q3;
            Q3=makeQuery(id+"F1.opExtrude","CAP_EDGE",EDGE,{"disambiguationData":[OSD([sQuery(id+"F0.wireOp",EDGE,"E2")])],"isStart":true});
            fillet(context, id + "F12", {"entities" : qUnion([Q0, Q1, Q2, Q3]), "radius" : .5 * mm, "tangentPropagation" : true, "allowEdgeOverflow" : false});
        }
    });
